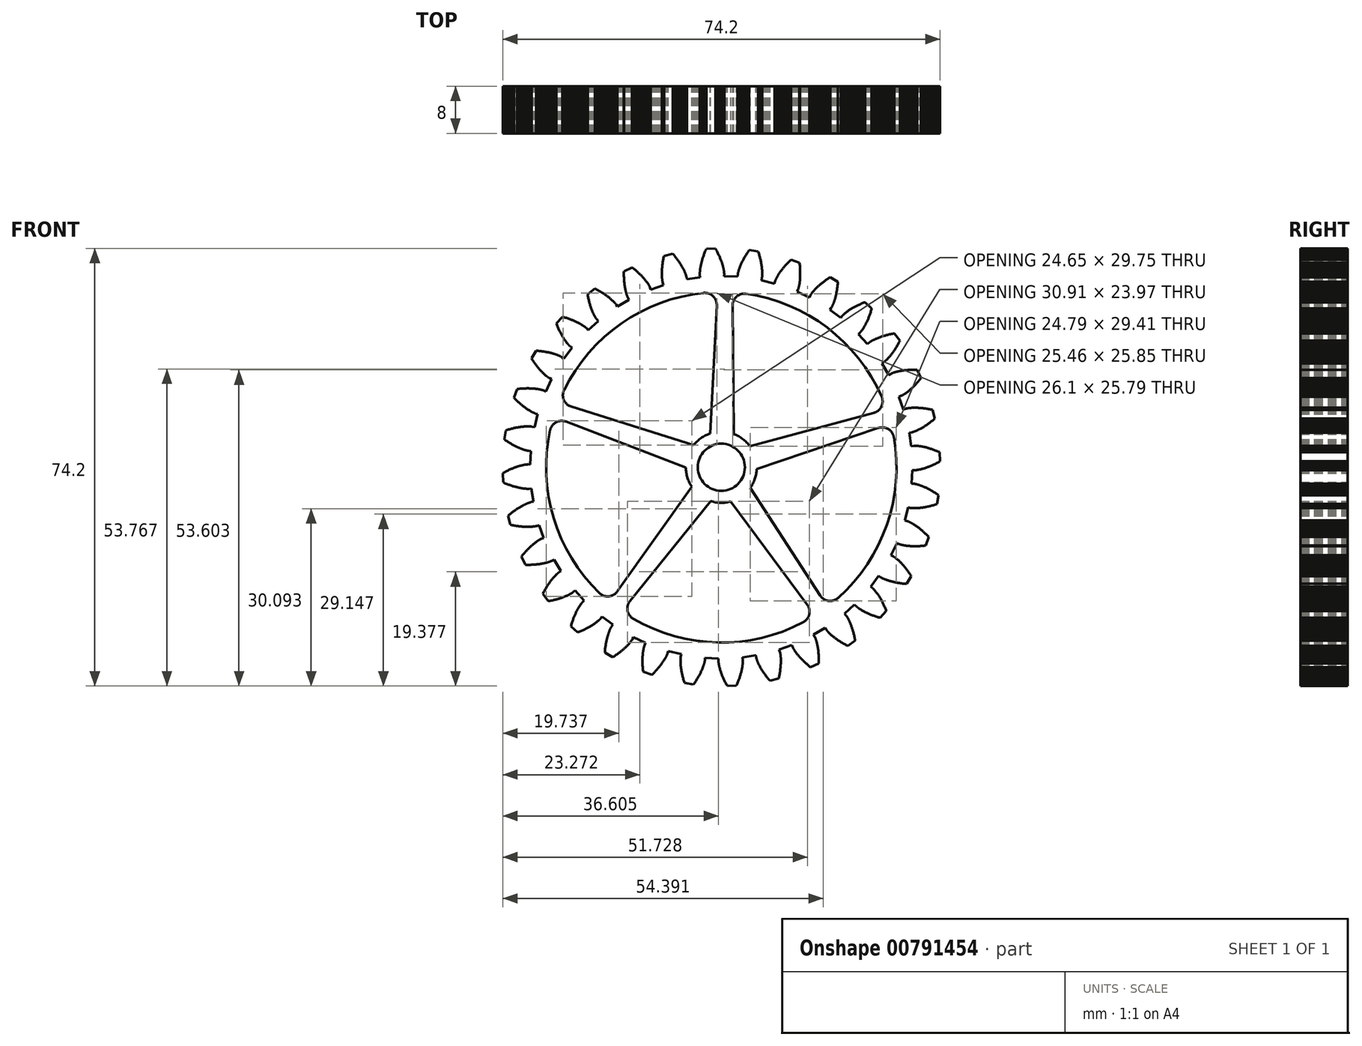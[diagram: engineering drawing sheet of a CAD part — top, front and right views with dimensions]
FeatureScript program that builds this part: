
annotation { "Feature Type Name" : "Feature", "Feature Type Description" : "" }
export const myFeature = defineFeature(function(context is Context, id is Id, definition is map)
    precondition{}
    {
        {
            var Q0;
            Q0=qCreatedBy(makeId("Front.planeOp"),FACE);
            var sketch = newSketch(context, id + "F0", { "sketchPlane" : qUnion([Q0])});
            skLineSegment(sketch, "E0", {"start": v(-0.78, 27.44) * mm, "end": v(-1.9, 5.7) * mm});
            skLineSegment(sketch, "E1", {"start": v(1.9, 27.38) * mm, "end": v(2.14, 5.63) * mm});
            skLineSegment(sketch, "E2", {"start": v(-26.33, 7.74) * mm, "end": v(-6.02, -0.05) * mm});
            skLineSegment(sketch, "E3", {"start": v(-25.45, 10.27) * mm, "end": v(-4.69, 3.77) * mm});
            skLineSegment(sketch, "E4", {"start": v(-15.5, -22.65) * mm, "end": v(-1.81, -5.74) * mm});
            skLineSegment(sketch, "E5", {"start": v(-17.63, -21.04) * mm, "end": v(-5.04, -3.3) * mm});
            skLineSegment(sketch, "E6", {"start": v(16.76, -21.74) * mm, "end": v(4.9, -3.5) * mm});
            skLineSegment(sketch, "E7", {"start": v(14.56, -23.27) * mm, "end": v(1.58, -5.8) * mm});
            skLineSegment(sketch, "E8", {"start": v(25.85, 9.22) * mm, "end": v(4.84, 3.58) * mm});
            skLineSegment(sketch, "E9", {"start": v(26.63, 6.66) * mm, "end": v(6.01, -0.3) * mm});
            skArc(sketch, "E10", {"start": v(19.81, -22.15) * mm, "mid": v(28.07, -9.76) * mm, "end": v(29.28, 5.08) * mm});
            skArc(sketch, "E11", {"start": v(-14.94, -25.69) * mm, "mid": v(-0.6, -29.7) * mm, "end": v(13.88, -26.28) * mm});
            skArc(sketch, "E12", {"start": v(-29.05, 6.27) * mm, "mid": v(-28.44, -8.6) * mm, "end": v(-20.7, -21.32) * mm});
            skArc(sketch, "E13", {"start": v(-3.01, 29.56) * mm, "mid": v(-16.97, 24.4) * mm, "end": v(-26.67, 13.1) * mm});
            skArc(sketch, "E14", {"start": v(27.18, 12) * mm, "mid": v(17.95, 23.68) * mm, "end": v(4.22, 29.41) * mm});
            skArc(sketch, "E15", {"start": v(-26.33, 7.74) * mm, "mid": v(-28.03, 7.63) * mm, "end": v(-29.05, 6.27) * mm});
            skArc(sketch, "E16", {"start": v(-26.67, 13.1) * mm, "mid": v(-26.71, 11.4) * mm, "end": v(-25.45, 10.27) * mm});
            skArc(sketch, "E17", {"start": v(-0.78, 27.44) * mm, "mid": v(-1.4, 29.01) * mm, "end": v(-3.01, 29.56) * mm});
            skArc(sketch, "E18", {"start": v(4.22, 29.41) * mm, "mid": v(2.6, 28.93) * mm, "end": v(1.9, 27.38) * mm});
            skArc(sketch, "E19", {"start": v(25.85, 9.22) * mm, "mid": v(27.16, 10.3) * mm, "end": v(27.18, 12) * mm});
            skArc(sketch, "E20", {"start": v(29.28, 5.08) * mm, "mid": v(28.32, 6.48) * mm, "end": v(26.63, 6.66) * mm});
            skArc(sketch, "E21", {"start": v(16.76, -21.74) * mm, "mid": v(18.2, -22.65) * mm, "end": v(19.81, -22.15) * mm});
            skArc(sketch, "E22", {"start": v(13.88, -26.28) * mm, "mid": v(14.9, -24.93) * mm, "end": v(14.56, -23.27) * mm});
            skArc(sketch, "E23", {"start": v(-15.5, -22.65) * mm, "mid": v(-15.92, -24.3) * mm, "end": v(-14.94, -25.69) * mm});
            skArc(sketch, "E24", {"start": v(-20.7, -21.32) * mm, "mid": v(-19.1, -21.88) * mm, "end": v(-17.63, -21.04) * mm});
            skLineSegment(sketch, "E25", {"start": v(-32.42, 0.48) * mm, "end": v(-32.83, 0.49) * mm});
            skLineSegment(sketch, "E26", {"start": v(-32.83, 0.49) * mm, "end": v(-32.84, 0.49) * mm});
            skLineSegment(sketch, "E27", {"start": v(-32.84, 0.49) * mm, "end": v(-32.85, 0.49) * mm});
            skLineSegment(sketch, "E28", {"start": v(-32.85, 0.49) * mm, "end": v(-32.86, 0.49) * mm});
            skLineSegment(sketch, "E29", {"start": v(-32.86, 0.49) * mm, "end": v(-32.88, 0.49) * mm});
            skLineSegment(sketch, "E30", {"start": v(-32.88, 0.49) * mm, "end": v(-32.9, 0.49) * mm});
            skLineSegment(sketch, "E31", {"start": v(-32.9, 0.49) * mm, "end": v(-32.94, 0.48) * mm});
            skLineSegment(sketch, "E32", {"start": v(-32.94, 0.48) * mm, "end": v(-32.97, 0.48) * mm});
            skLineSegment(sketch, "E33", {"start": v(-32.97, 0.48) * mm, "end": v(-33, 0.48) * mm});
            skLineSegment(sketch, "E34", {"start": v(-33, 0.48) * mm, "end": v(-33.04, 0.48) * mm});
            skLineSegment(sketch, "E35", {"start": v(-33.04, 0.48) * mm, "end": v(-33.09, 0.47) * mm});
            skLineSegment(sketch, "E36", {"start": v(-33.09, 0.47) * mm, "end": v(-33.13, 0.47) * mm});
            skLineSegment(sketch, "E37", {"start": v(-33.13, 0.47) * mm, "end": v(-33.18, 0.46) * mm});
            skLineSegment(sketch, "E38", {"start": v(-33.18, 0.46) * mm, "end": v(-33.24, 0.45) * mm});
            skLineSegment(sketch, "E39", {"start": v(-33.24, 0.45) * mm, "end": v(-33.3, 0.44) * mm});
            skLineSegment(sketch, "E40", {"start": v(-33.3, 0.44) * mm, "end": v(-33.36, 0.43) * mm});
            skLineSegment(sketch, "E41", {"start": v(-33.36, 0.43) * mm, "end": v(-33.42, 0.42) * mm});
            skLineSegment(sketch, "E42", {"start": v(-33.42, 0.42) * mm, "end": v(-33.5, 0.4) * mm});
            skLineSegment(sketch, "E43", {"start": v(-33.5, 0.4) * mm, "end": v(-33.57, 0.4) * mm});
            skLineSegment(sketch, "E44", {"start": v(-33.57, 0.4) * mm, "end": v(-33.64, 0.38) * mm});
            skLineSegment(sketch, "E45", {"start": v(-33.64, 0.38) * mm, "end": v(-33.72, 0.36) * mm});
            skLineSegment(sketch, "E46", {"start": v(-33.72, 0.36) * mm, "end": v(-33.8, 0.34) * mm});
            skLineSegment(sketch, "E47", {"start": v(-33.8, 0.34) * mm, "end": v(-33.9, 0.32) * mm});
            skLineSegment(sketch, "E48", {"start": v(-33.9, 0.32) * mm, "end": v(-33.99, 0.3) * mm});
            skLineSegment(sketch, "E49", {"start": v(-33.99, 0.3) * mm, "end": v(-34.08, 0.27) * mm});
            skLineSegment(sketch, "E50", {"start": v(-34.08, 0.27) * mm, "end": v(-34.18, 0.24) * mm});
            skLineSegment(sketch, "E51", {"start": v(-34.18, 0.24) * mm, "end": v(-34.28, 0.22) * mm});
            skLineSegment(sketch, "E52", {"start": v(-34.28, 0.22) * mm, "end": v(-34.39, 0.18) * mm});
            skLineSegment(sketch, "E53", {"start": v(-34.39, 0.18) * mm, "end": v(-34.5, 0.15) * mm});
            skLineSegment(sketch, "E54", {"start": v(-34.5, 0.15) * mm, "end": v(-34.6, 0.11) * mm});
            skLineSegment(sketch, "E55", {"start": v(-34.6, 0.11) * mm, "end": v(-34.72, 0.07) * mm});
            skLineSegment(sketch, "E56", {"start": v(-34.72, 0.07) * mm, "end": v(-34.84, 0.03) * mm});
            skLineSegment(sketch, "E57", {"start": v(-34.84, 0.03) * mm, "end": v(-34.96, -0.01) * mm});
            skLineSegment(sketch, "E58", {"start": v(-34.96, -0.01) * mm, "end": v(-35.09, -0.06) * mm});
            skLineSegment(sketch, "E59", {"start": v(-35.09, -0.06) * mm, "end": v(-35.21, -0.1) * mm});
            skLineSegment(sketch, "E60", {"start": v(-35.21, -0.1) * mm, "end": v(-35.35, -0.16) * mm});
            skLineSegment(sketch, "E61", {"start": v(-35.35, -0.16) * mm, "end": v(-35.48, -0.21) * mm});
            skLineSegment(sketch, "E62", {"start": v(-35.48, -0.21) * mm, "end": v(-35.62, -0.27) * mm});
            skLineSegment(sketch, "E63", {"start": v(-35.62, -0.27) * mm, "end": v(-35.76, -0.33) * mm});
            skLineSegment(sketch, "E64", {"start": v(-35.76, -0.33) * mm, "end": v(-35.9, -0.4) * mm});
            skLineSegment(sketch, "E65", {"start": v(-35.9, -0.4) * mm, "end": v(-36.05, -0.46) * mm});
            skLineSegment(sketch, "E66", {"start": v(-36.05, -0.46) * mm, "end": v(-36.2, -0.53) * mm});
            skLineSegment(sketch, "E67", {"start": v(-36.2, -0.53) * mm, "end": v(-36.35, -0.6) * mm});
            skLineSegment(sketch, "E68", {"start": v(-36.35, -0.6) * mm, "end": v(-36.5, -0.69) * mm});
            skLineSegment(sketch, "E69", {"start": v(-36.5, -0.69) * mm, "end": v(-36.66, -0.77) * mm});
            skLineSegment(sketch, "E70", {"start": v(-36.66, -0.77) * mm, "end": v(-36.81, -0.85) * mm});
            skLineSegment(sketch, "E71", {"start": v(-36.81, -0.85) * mm, "end": v(-36.98, -0.94) * mm});
            skLineSegment(sketch, "E72", {"start": v(-36.98, -0.94) * mm, "end": v(-37.1, -1.03) * mm});
            skLineSegment(sketch, "E73", {"start": v(-37.1, -1.03) * mm, "end": v(-37.03, -2.54) * mm});
            skLineSegment(sketch, "E74", {"start": v(-37.03, -2.54) * mm, "end": v(-36.9, -2.62) * mm});
            skLineSegment(sketch, "E75", {"start": v(-36.9, -2.62) * mm, "end": v(-36.73, -2.7) * mm});
            skLineSegment(sketch, "E76", {"start": v(-36.73, -2.7) * mm, "end": v(-36.56, -2.76) * mm});
            skLineSegment(sketch, "E77", {"start": v(-36.56, -2.76) * mm, "end": v(-36.4, -2.82) * mm});
            skLineSegment(sketch, "E78", {"start": v(-36.4, -2.82) * mm, "end": v(-36.24, -2.89) * mm});
            skLineSegment(sketch, "E79", {"start": v(-36.24, -2.89) * mm, "end": v(-36.08, -2.95) * mm});
            skLineSegment(sketch, "E80", {"start": v(-36.08, -2.95) * mm, "end": v(-35.92, -3) * mm});
            skLineSegment(sketch, "E81", {"start": v(-35.92, -3) * mm, "end": v(-35.77, -3.05) * mm});
            skLineSegment(sketch, "E82", {"start": v(-35.77, -3.05) * mm, "end": v(-35.62, -3.1) * mm});
            skLineSegment(sketch, "E83", {"start": v(-35.62, -3.1) * mm, "end": v(-35.48, -3.15) * mm});
            skLineSegment(sketch, "E84", {"start": v(-35.48, -3.15) * mm, "end": v(-35.34, -3.2) * mm});
            skLineSegment(sketch, "E85", {"start": v(-35.34, -3.2) * mm, "end": v(-35.2, -3.24) * mm});
            skLineSegment(sketch, "E86", {"start": v(-35.2, -3.24) * mm, "end": v(-35.06, -3.28) * mm});
            skLineSegment(sketch, "E87", {"start": v(-35.06, -3.28) * mm, "end": v(-34.93, -3.32) * mm});
            skLineSegment(sketch, "E88", {"start": v(-34.93, -3.32) * mm, "end": v(-34.8, -3.35) * mm});
            skLineSegment(sketch, "E89", {"start": v(-34.8, -3.35) * mm, "end": v(-34.68, -3.38) * mm});
            skLineSegment(sketch, "E90", {"start": v(-34.68, -3.38) * mm, "end": v(-34.55, -3.41) * mm});
            skLineSegment(sketch, "E91", {"start": v(-34.55, -3.41) * mm, "end": v(-34.44, -3.44) * mm});
            skLineSegment(sketch, "E92", {"start": v(-34.44, -3.44) * mm, "end": v(-34.32, -3.46) * mm});
            skLineSegment(sketch, "E93", {"start": v(-34.32, -3.46) * mm, "end": v(-34.2, -3.49) * mm});
            skLineSegment(sketch, "E94", {"start": v(-34.2, -3.49) * mm, "end": v(-34.1, -3.5) * mm});
            skLineSegment(sketch, "E95", {"start": v(-34.1, -3.5) * mm, "end": v(-34, -3.53) * mm});
            skLineSegment(sketch, "E96", {"start": v(-34, -3.53) * mm, "end": v(-33.9, -3.55) * mm});
            skLineSegment(sketch, "E97", {"start": v(-33.9, -3.55) * mm, "end": v(-33.8, -3.56) * mm});
            skLineSegment(sketch, "E98", {"start": v(-33.8, -3.56) * mm, "end": v(-33.7, -3.58) * mm});
            skLineSegment(sketch, "E99", {"start": v(-33.7, -3.58) * mm, "end": v(-33.62, -3.59) * mm});
            skLineSegment(sketch, "E100", {"start": v(-33.62, -3.59) * mm, "end": v(-33.53, -3.6) * mm});
            skLineSegment(sketch, "E101", {"start": v(-33.53, -3.6) * mm, "end": v(-33.45, -3.6) * mm});
            skLineSegment(sketch, "E102", {"start": v(-33.45, -3.6) * mm, "end": v(-33.37, -3.62) * mm});
            skLineSegment(sketch, "E103", {"start": v(-33.37, -3.62) * mm, "end": v(-33.3, -3.63) * mm});
            skLineSegment(sketch, "E104", {"start": v(-33.3, -3.63) * mm, "end": v(-33.23, -3.63) * mm});
            skLineSegment(sketch, "E105", {"start": v(-33.23, -3.63) * mm, "end": v(-33.16, -3.64) * mm});
            skLineSegment(sketch, "E106", {"start": v(-33.16, -3.64) * mm, "end": v(-33.1, -3.64) * mm});
            skLineSegment(sketch, "E107", {"start": v(-33.1, -3.64) * mm, "end": v(-33.04, -3.64) * mm});
            skLineSegment(sketch, "E108", {"start": v(-33.04, -3.64) * mm, "end": v(-32.98, -3.65) * mm});
            skLineSegment(sketch, "E109", {"start": v(-32.98, -3.65) * mm, "end": v(-32.93, -3.65) * mm});
            skLineSegment(sketch, "E110", {"start": v(-32.93, -3.65) * mm, "end": v(-32.89, -3.65) * mm});
            skLineSegment(sketch, "E111", {"start": v(-32.89, -3.65) * mm, "end": v(-32.84, -3.65) * mm});
            skLineSegment(sketch, "E112", {"start": v(-32.84, -3.65) * mm, "end": v(-32.8, -3.65) * mm});
            skLineSegment(sketch, "E113", {"start": v(-32.8, -3.65) * mm, "end": v(-32.77, -3.65) * mm});
            skLineSegment(sketch, "E114", {"start": v(-32.77, -3.65) * mm, "end": v(-32.74, -3.65) * mm});
            skLineSegment(sketch, "E115", {"start": v(-32.74, -3.65) * mm, "end": v(-32.7, -3.65) * mm});
            skLineSegment(sketch, "E116", {"start": v(-32.7, -3.65) * mm, "end": v(-32.69, -3.65) * mm});
            skLineSegment(sketch, "E117", {"start": v(-32.69, -3.65) * mm, "end": v(-32.67, -3.64) * mm});
            skLineSegment(sketch, "E118", {"start": v(-32.67, -3.64) * mm, "end": v(-32.65, -3.64) * mm});
            skLineSegment(sketch, "E119", {"start": v(-32.65, -3.64) * mm, "end": v(-32.64, -3.64) * mm});
            skLineSegment(sketch, "E120", {"start": v(-32.64, -3.64) * mm, "end": v(-32.63, -3.64) * mm});
            skLineSegment(sketch, "E121", {"start": v(-32.63, -3.64) * mm, "end": v(-32.22, -3.6) * mm});
            skLineSegment(sketch, "E122", {"start": v(-32.22, -3.6) * mm, "end": v(-31.9, -5.85) * mm});
            skLineSegment(sketch, "E123", {"start": v(-31.9, -5.85) * mm, "end": v(-32.3, -5.92) * mm});
            skLineSegment(sketch, "E124", {"start": v(-32.3, -5.92) * mm, "end": v(-32.3, -5.93) * mm});
            skLineSegment(sketch, "E125", {"start": v(-32.3, -5.93) * mm, "end": v(-32.31, -5.93) * mm});
            skLineSegment(sketch, "E126", {"start": v(-32.31, -5.93) * mm, "end": v(-32.33, -5.93) * mm});
            skLineSegment(sketch, "E127", {"start": v(-32.33, -5.93) * mm, "end": v(-32.35, -5.94) * mm});
            skLineSegment(sketch, "E128", {"start": v(-32.35, -5.94) * mm, "end": v(-32.37, -5.94) * mm});
            skLineSegment(sketch, "E129", {"start": v(-32.37, -5.94) * mm, "end": v(-32.4, -5.95) * mm});
            skLineSegment(sketch, "E130", {"start": v(-32.4, -5.95) * mm, "end": v(-32.43, -5.96) * mm});
            skLineSegment(sketch, "E131", {"start": v(-32.43, -5.96) * mm, "end": v(-32.46, -5.97) * mm});
            skLineSegment(sketch, "E132", {"start": v(-32.46, -5.97) * mm, "end": v(-32.5, -5.98) * mm});
            skLineSegment(sketch, "E133", {"start": v(-32.5, -5.98) * mm, "end": v(-32.54, -6) * mm});
            skLineSegment(sketch, "E134", {"start": v(-32.54, -6) * mm, "end": v(-32.59, -6) * mm});
            skLineSegment(sketch, "E135", {"start": v(-32.59, -6) * mm, "end": v(-32.63, -6.02) * mm});
            skLineSegment(sketch, "E136", {"start": v(-32.63, -6.02) * mm, "end": v(-32.69, -6.04) * mm});
            skLineSegment(sketch, "E137", {"start": v(-32.69, -6.04) * mm, "end": v(-32.74, -6.06) * mm});
            skLineSegment(sketch, "E138", {"start": v(-32.74, -6.06) * mm, "end": v(-32.8, -6.08) * mm});
            skLineSegment(sketch, "E139", {"start": v(-32.8, -6.08) * mm, "end": v(-32.86, -6.1) * mm});
            skLineSegment(sketch, "E140", {"start": v(-32.86, -6.1) * mm, "end": v(-32.93, -6.13) * mm});
            skLineSegment(sketch, "E141", {"start": v(-32.93, -6.13) * mm, "end": v(-33, -6.16) * mm});
            skLineSegment(sketch, "E142", {"start": v(-33, -6.16) * mm, "end": v(-33.07, -6.2) * mm});
            skLineSegment(sketch, "E143", {"start": v(-33.07, -6.2) * mm, "end": v(-33.15, -6.23) * mm});
            skLineSegment(sketch, "E144", {"start": v(-33.15, -6.23) * mm, "end": v(-33.22, -6.26) * mm});
            skLineSegment(sketch, "E145", {"start": v(-33.22, -6.26) * mm, "end": v(-33.3, -6.3) * mm});
            skLineSegment(sketch, "E146", {"start": v(-33.3, -6.3) * mm, "end": v(-33.4, -6.34) * mm});
            skLineSegment(sketch, "E147", {"start": v(-33.4, -6.34) * mm, "end": v(-33.48, -6.38) * mm});
            skLineSegment(sketch, "E148", {"start": v(-33.48, -6.38) * mm, "end": v(-33.57, -6.43) * mm});
            skLineSegment(sketch, "E149", {"start": v(-33.57, -6.43) * mm, "end": v(-33.66, -6.48) * mm});
            skLineSegment(sketch, "E150", {"start": v(-33.66, -6.48) * mm, "end": v(-33.76, -6.53) * mm});
            skLineSegment(sketch, "E151", {"start": v(-33.76, -6.53) * mm, "end": v(-33.86, -6.58) * mm});
            skLineSegment(sketch, "E152", {"start": v(-33.86, -6.58) * mm, "end": v(-33.96, -6.64) * mm});
            skLineSegment(sketch, "E153", {"start": v(-33.96, -6.64) * mm, "end": v(-34.07, -6.7) * mm});
            skLineSegment(sketch, "E154", {"start": v(-34.07, -6.7) * mm, "end": v(-34.18, -6.76) * mm});
            skLineSegment(sketch, "E155", {"start": v(-34.18, -6.76) * mm, "end": v(-34.29, -6.83) * mm});
            skLineSegment(sketch, "E156", {"start": v(-34.29, -6.83) * mm, "end": v(-34.4, -6.9) * mm});
            skLineSegment(sketch, "E157", {"start": v(-34.4, -6.9) * mm, "end": v(-34.52, -6.97) * mm});
            skLineSegment(sketch, "E158", {"start": v(-34.52, -6.97) * mm, "end": v(-34.64, -7.05) * mm});
            skLineSegment(sketch, "E159", {"start": v(-34.64, -7.05) * mm, "end": v(-34.76, -7.13) * mm});
            skLineSegment(sketch, "E160", {"start": v(-34.76, -7.13) * mm, "end": v(-34.88, -7.21) * mm});
            skLineSegment(sketch, "E161", {"start": v(-34.88, -7.21) * mm, "end": v(-35, -7.3) * mm});
            skLineSegment(sketch, "E162", {"start": v(-35, -7.3) * mm, "end": v(-35.13, -7.4) * mm});
            skLineSegment(sketch, "E163", {"start": v(-35.13, -7.4) * mm, "end": v(-35.26, -7.49) * mm});
            skLineSegment(sketch, "E164", {"start": v(-35.26, -7.49) * mm, "end": v(-35.4, -7.59) * mm});
            skLineSegment(sketch, "E165", {"start": v(-35.4, -7.59) * mm, "end": v(-35.53, -7.69) * mm});
            skLineSegment(sketch, "E166", {"start": v(-35.53, -7.69) * mm, "end": v(-35.66, -7.8) * mm});
            skLineSegment(sketch, "E167", {"start": v(-35.66, -7.8) * mm, "end": v(-35.8, -7.9) * mm});
            skLineSegment(sketch, "E168", {"start": v(-35.8, -7.9) * mm, "end": v(-35.94, -8.02) * mm});
            skLineSegment(sketch, "E169", {"start": v(-35.94, -8.02) * mm, "end": v(-36.08, -8.14) * mm});
            skLineSegment(sketch, "E170", {"start": v(-36.08, -8.14) * mm, "end": v(-36.19, -8.25) * mm});
            skLineSegment(sketch, "E171", {"start": v(-36.19, -8.25) * mm, "end": v(-35.82, -9.72) * mm});
            skLineSegment(sketch, "E172", {"start": v(-35.82, -9.72) * mm, "end": v(-35.68, -9.77) * mm});
            skLineSegment(sketch, "E173", {"start": v(-35.68, -9.77) * mm, "end": v(-35.5, -9.8) * mm});
            skLineSegment(sketch, "E174", {"start": v(-35.5, -9.8) * mm, "end": v(-35.32, -9.84) * mm});
            skLineSegment(sketch, "E175", {"start": v(-35.32, -9.84) * mm, "end": v(-35.15, -9.87) * mm});
            skLineSegment(sketch, "E176", {"start": v(-35.15, -9.87) * mm, "end": v(-34.98, -9.9) * mm});
            skLineSegment(sketch, "E177", {"start": v(-34.98, -9.9) * mm, "end": v(-34.8, -9.93) * mm});
            skLineSegment(sketch, "E178", {"start": v(-34.8, -9.93) * mm, "end": v(-34.65, -9.95) * mm});
            skLineSegment(sketch, "E179", {"start": v(-34.65, -9.95) * mm, "end": v(-34.49, -9.98) * mm});
            skLineSegment(sketch, "E180", {"start": v(-34.49, -9.98) * mm, "end": v(-34.33, -10) * mm});
            skLineSegment(sketch, "E181", {"start": v(-34.33, -10) * mm, "end": v(-34.18, -10.01) * mm});
            skLineSegment(sketch, "E182", {"start": v(-34.18, -10.01) * mm, "end": v(-34.03, -10.03) * mm});
            skLineSegment(sketch, "E183", {"start": v(-34.03, -10.03) * mm, "end": v(-33.89, -10.04) * mm});
            skLineSegment(sketch, "E184", {"start": v(-33.89, -10.04) * mm, "end": v(-33.75, -10.06) * mm});
            skLineSegment(sketch, "E185", {"start": v(-33.75, -10.06) * mm, "end": v(-33.61, -10.07) * mm});
            skLineSegment(sketch, "E186", {"start": v(-33.61, -10.07) * mm, "end": v(-33.48, -10.07) * mm});
            skLineSegment(sketch, "E187", {"start": v(-33.48, -10.07) * mm, "end": v(-33.35, -10.08) * mm});
            skLineSegment(sketch, "E188", {"start": v(-33.35, -10.08) * mm, "end": v(-33.22, -10.09) * mm});
            skLineSegment(sketch, "E189", {"start": v(-33.22, -10.09) * mm, "end": v(-33.1, -10.1) * mm});
            skLineSegment(sketch, "E190", {"start": v(-33.1, -10.1) * mm, "end": v(-32.99, -10.1) * mm});
            skLineSegment(sketch, "E191", {"start": v(-32.99, -10.1) * mm, "end": v(-32.87, -10.1) * mm});
            skLineSegment(sketch, "E192", {"start": v(-32.87, -10.1) * mm, "end": v(-32.76, -10.1) * mm});
            skLineSegment(sketch, "E193", {"start": v(-32.76, -10.1) * mm, "end": v(-32.66, -10.1) * mm});
            skLineSegment(sketch, "E194", {"start": v(-32.66, -10.1) * mm, "end": v(-32.55, -10.1) * mm});
            skLineSegment(sketch, "E195", {"start": v(-32.55, -10.1) * mm, "end": v(-32.46, -10.09) * mm});
            skLineSegment(sketch, "E196", {"start": v(-32.46, -10.09) * mm, "end": v(-32.36, -10.08) * mm});
            skLineSegment(sketch, "E197", {"start": v(-32.36, -10.08) * mm, "end": v(-32.27, -10.08) * mm});
            skLineSegment(sketch, "E198", {"start": v(-32.27, -10.08) * mm, "end": v(-32.19, -10.07) * mm});
            skLineSegment(sketch, "E199", {"start": v(-32.19, -10.07) * mm, "end": v(-32.1, -10.07) * mm});
            skLineSegment(sketch, "E200", {"start": v(-32.1, -10.07) * mm, "end": v(-32.03, -10.06) * mm});
            skLineSegment(sketch, "E201", {"start": v(-32.03, -10.06) * mm, "end": v(-31.95, -10.05) * mm});
            skLineSegment(sketch, "E202", {"start": v(-31.95, -10.05) * mm, "end": v(-31.88, -10.04) * mm});
            skLineSegment(sketch, "E203", {"start": v(-31.88, -10.04) * mm, "end": v(-31.82, -10.04) * mm});
            skLineSegment(sketch, "E204", {"start": v(-31.82, -10.04) * mm, "end": v(-31.75, -10.03) * mm});
            skLineSegment(sketch, "E205", {"start": v(-31.75, -10.03) * mm, "end": v(-31.7, -10.02) * mm});
            skLineSegment(sketch, "E206", {"start": v(-31.7, -10.02) * mm, "end": v(-31.64, -10.01) * mm});
            skLineSegment(sketch, "E207", {"start": v(-31.64, -10.01) * mm, "end": v(-31.59, -10) * mm});
            skLineSegment(sketch, "E208", {"start": v(-31.59, -10) * mm, "end": v(-31.54, -10) * mm});
            skLineSegment(sketch, "E209", {"start": v(-31.54, -10) * mm, "end": v(-31.5, -9.99) * mm});
            skLineSegment(sketch, "E210", {"start": v(-31.5, -9.99) * mm, "end": v(-31.46, -9.98) * mm});
            skLineSegment(sketch, "E211", {"start": v(-31.46, -9.98) * mm, "end": v(-31.43, -9.97) * mm});
            skLineSegment(sketch, "E212", {"start": v(-31.43, -9.97) * mm, "end": v(-31.4, -9.96) * mm});
            skLineSegment(sketch, "E213", {"start": v(-31.4, -9.96) * mm, "end": v(-31.37, -9.96) * mm});
            skLineSegment(sketch, "E214", {"start": v(-31.37, -9.96) * mm, "end": v(-31.35, -9.95) * mm});
            skLineSegment(sketch, "E215", {"start": v(-31.35, -9.95) * mm, "end": v(-31.33, -9.95) * mm});
            skLineSegment(sketch, "E216", {"start": v(-31.33, -9.95) * mm, "end": v(-31.31, -9.94) * mm});
            skLineSegment(sketch, "E217", {"start": v(-31.31, -9.94) * mm, "end": v(-31.3, -9.94) * mm});
            skLineSegment(sketch, "E218", {"start": v(-31.3, -9.94) * mm, "end": v(-31.3, -9.94) * mm});
            skLineSegment(sketch, "E219", {"start": v(-31.3, -9.94) * mm, "end": v(-30.9, -9.81) * mm});
            skLineSegment(sketch, "E220", {"start": v(-30.9, -9.81) * mm, "end": v(-30.14, -11.96) * mm});
            skLineSegment(sketch, "E221", {"start": v(-30.14, -11.96) * mm, "end": v(-30.52, -12.11) * mm});
            skLineSegment(sketch, "E222", {"start": v(-30.52, -12.11) * mm, "end": v(-30.52, -12.11) * mm});
            skLineSegment(sketch, "E223", {"start": v(-30.52, -12.11) * mm, "end": v(-30.54, -12.12) * mm});
            skLineSegment(sketch, "E224", {"start": v(-30.54, -12.12) * mm, "end": v(-30.55, -12.13) * mm});
            skLineSegment(sketch, "E225", {"start": v(-30.55, -12.13) * mm, "end": v(-30.57, -12.13) * mm});
            skLineSegment(sketch, "E226", {"start": v(-30.57, -12.13) * mm, "end": v(-30.59, -12.14) * mm});
            skLineSegment(sketch, "E227", {"start": v(-30.59, -12.14) * mm, "end": v(-30.61, -12.16) * mm});
            skLineSegment(sketch, "E228", {"start": v(-30.61, -12.16) * mm, "end": v(-30.64, -12.17) * mm});
            skLineSegment(sketch, "E229", {"start": v(-30.64, -12.17) * mm, "end": v(-30.67, -12.19) * mm});
            skLineSegment(sketch, "E230", {"start": v(-30.67, -12.19) * mm, "end": v(-30.7, -12.2) * mm});
            skLineSegment(sketch, "E231", {"start": v(-30.7, -12.2) * mm, "end": v(-30.75, -12.23) * mm});
            skLineSegment(sketch, "E232", {"start": v(-30.75, -12.23) * mm, "end": v(-30.79, -12.25) * mm});
            skLineSegment(sketch, "E233", {"start": v(-30.79, -12.25) * mm, "end": v(-30.83, -12.27) * mm});
            skLineSegment(sketch, "E234", {"start": v(-30.83, -12.27) * mm, "end": v(-30.88, -12.3) * mm});
            skLineSegment(sketch, "E235", {"start": v(-30.88, -12.3) * mm, "end": v(-30.93, -12.33) * mm});
            skLineSegment(sketch, "E236", {"start": v(-30.93, -12.33) * mm, "end": v(-30.98, -12.37) * mm});
            skLineSegment(sketch, "E237", {"start": v(-30.98, -12.37) * mm, "end": v(-31.04, -12.4) * mm});
            skLineSegment(sketch, "E238", {"start": v(-31.04, -12.4) * mm, "end": v(-31.1, -12.44) * mm});
            skLineSegment(sketch, "E239", {"start": v(-31.1, -12.44) * mm, "end": v(-31.16, -12.48) * mm});
            skLineSegment(sketch, "E240", {"start": v(-31.16, -12.48) * mm, "end": v(-31.23, -12.53) * mm});
            skLineSegment(sketch, "E241", {"start": v(-31.23, -12.53) * mm, "end": v(-31.3, -12.57) * mm});
            skLineSegment(sketch, "E242", {"start": v(-31.3, -12.57) * mm, "end": v(-31.36, -12.62) * mm});
            skLineSegment(sketch, "E243", {"start": v(-31.36, -12.62) * mm, "end": v(-31.44, -12.68) * mm});
            skLineSegment(sketch, "E244", {"start": v(-31.44, -12.68) * mm, "end": v(-31.51, -12.73) * mm});
            skLineSegment(sketch, "E245", {"start": v(-31.51, -12.73) * mm, "end": v(-31.6, -12.8) * mm});
            skLineSegment(sketch, "E246", {"start": v(-31.6, -12.8) * mm, "end": v(-31.67, -12.85) * mm});
            skLineSegment(sketch, "E247", {"start": v(-31.67, -12.85) * mm, "end": v(-31.75, -12.92) * mm});
            skLineSegment(sketch, "E248", {"start": v(-31.75, -12.92) * mm, "end": v(-31.84, -12.99) * mm});
            skLineSegment(sketch, "E249", {"start": v(-31.84, -12.99) * mm, "end": v(-31.93, -13.06) * mm});
            skLineSegment(sketch, "E250", {"start": v(-31.93, -13.06) * mm, "end": v(-32.02, -13.14) * mm});
            skLineSegment(sketch, "E251", {"start": v(-32.02, -13.14) * mm, "end": v(-32.1, -13.22) * mm});
            skLineSegment(sketch, "E252", {"start": v(-32.1, -13.22) * mm, "end": v(-32.2, -13.3) * mm});
            skLineSegment(sketch, "E253", {"start": v(-32.2, -13.3) * mm, "end": v(-32.3, -13.39) * mm});
            skLineSegment(sketch, "E254", {"start": v(-32.3, -13.39) * mm, "end": v(-32.4, -13.48) * mm});
            skLineSegment(sketch, "E255", {"start": v(-32.4, -13.48) * mm, "end": v(-32.5, -13.57) * mm});
            skLineSegment(sketch, "E256", {"start": v(-32.5, -13.57) * mm, "end": v(-32.6, -13.67) * mm});
            skLineSegment(sketch, "E257", {"start": v(-32.6, -13.67) * mm, "end": v(-32.7, -13.77) * mm});
            skLineSegment(sketch, "E258", {"start": v(-32.7, -13.77) * mm, "end": v(-32.8, -13.88) * mm});
            skLineSegment(sketch, "E259", {"start": v(-32.8, -13.88) * mm, "end": v(-32.9, -14) * mm});
            skLineSegment(sketch, "E260", {"start": v(-32.9, -14) * mm, "end": v(-33.02, -14.1) * mm});
            skLineSegment(sketch, "E261", {"start": v(-33.02, -14.1) * mm, "end": v(-33.12, -14.22) * mm});
            skLineSegment(sketch, "E262", {"start": v(-33.12, -14.22) * mm, "end": v(-33.23, -14.35) * mm});
            skLineSegment(sketch, "E263", {"start": v(-33.23, -14.35) * mm, "end": v(-33.35, -14.47) * mm});
            skLineSegment(sketch, "E264", {"start": v(-33.35, -14.47) * mm, "end": v(-33.46, -14.6) * mm});
            skLineSegment(sketch, "E265", {"start": v(-33.46, -14.6) * mm, "end": v(-33.57, -14.74) * mm});
            skLineSegment(sketch, "E266", {"start": v(-33.57, -14.74) * mm, "end": v(-33.69, -14.88) * mm});
            skLineSegment(sketch, "E267", {"start": v(-33.69, -14.88) * mm, "end": v(-33.8, -15.02) * mm});
            skLineSegment(sketch, "E268", {"start": v(-33.8, -15.02) * mm, "end": v(-33.88, -15.15) * mm});
            skLineSegment(sketch, "E269", {"start": v(-33.88, -15.15) * mm, "end": v(-33.24, -16.52) * mm});
            skLineSegment(sketch, "E270", {"start": v(-33.24, -16.52) * mm, "end": v(-33.08, -16.54) * mm});
            skLineSegment(sketch, "E271", {"start": v(-33.08, -16.54) * mm, "end": v(-32.9, -16.54) * mm});
            skLineSegment(sketch, "E272", {"start": v(-32.9, -16.54) * mm, "end": v(-32.72, -16.54) * mm});
            skLineSegment(sketch, "E273", {"start": v(-32.72, -16.54) * mm, "end": v(-32.54, -16.54) * mm});
            skLineSegment(sketch, "E274", {"start": v(-32.54, -16.54) * mm, "end": v(-32.37, -16.53) * mm});
            skLineSegment(sketch, "E275", {"start": v(-32.37, -16.53) * mm, "end": v(-32.2, -16.53) * mm});
            skLineSegment(sketch, "E276", {"start": v(-32.2, -16.53) * mm, "end": v(-32.04, -16.52) * mm});
            skLineSegment(sketch, "E277", {"start": v(-32.04, -16.52) * mm, "end": v(-31.88, -16.51) * mm});
            skLineSegment(sketch, "E278", {"start": v(-31.88, -16.51) * mm, "end": v(-31.72, -16.5) * mm});
            skLineSegment(sketch, "E279", {"start": v(-31.72, -16.5) * mm, "end": v(-31.57, -16.49) * mm});
            skLineSegment(sketch, "E280", {"start": v(-31.57, -16.49) * mm, "end": v(-31.42, -16.48) * mm});
            skLineSegment(sketch, "E281", {"start": v(-31.42, -16.48) * mm, "end": v(-31.28, -16.46) * mm});
            skLineSegment(sketch, "E282", {"start": v(-31.28, -16.46) * mm, "end": v(-31.14, -16.45) * mm});
            skLineSegment(sketch, "E283", {"start": v(-31.14, -16.45) * mm, "end": v(-31, -16.43) * mm});
            skLineSegment(sketch, "E284", {"start": v(-31, -16.43) * mm, "end": v(-30.87, -16.41) * mm});
            skLineSegment(sketch, "E285", {"start": v(-30.87, -16.41) * mm, "end": v(-30.74, -16.4) * mm});
            skLineSegment(sketch, "E286", {"start": v(-30.74, -16.4) * mm, "end": v(-30.62, -16.37) * mm});
            skLineSegment(sketch, "E287", {"start": v(-30.62, -16.37) * mm, "end": v(-30.5, -16.36) * mm});
            skLineSegment(sketch, "E288", {"start": v(-30.5, -16.36) * mm, "end": v(-30.38, -16.33) * mm});
            skLineSegment(sketch, "E289", {"start": v(-30.38, -16.33) * mm, "end": v(-30.27, -16.31) * mm});
            skLineSegment(sketch, "E290", {"start": v(-30.27, -16.31) * mm, "end": v(-30.16, -16.3) * mm});
            skLineSegment(sketch, "E291", {"start": v(-30.16, -16.3) * mm, "end": v(-30.06, -16.27) * mm});
            skLineSegment(sketch, "E292", {"start": v(-30.06, -16.27) * mm, "end": v(-29.96, -16.25) * mm});
            skLineSegment(sketch, "E293", {"start": v(-29.96, -16.25) * mm, "end": v(-29.86, -16.23) * mm});
            skLineSegment(sketch, "E294", {"start": v(-29.86, -16.23) * mm, "end": v(-29.77, -16.2) * mm});
            skLineSegment(sketch, "E295", {"start": v(-29.77, -16.2) * mm, "end": v(-29.69, -16.18) * mm});
            skLineSegment(sketch, "E296", {"start": v(-29.69, -16.18) * mm, "end": v(-29.6, -16.16) * mm});
            skLineSegment(sketch, "E297", {"start": v(-29.6, -16.16) * mm, "end": v(-29.52, -16.14) * mm});
            skLineSegment(sketch, "E298", {"start": v(-29.52, -16.14) * mm, "end": v(-29.45, -16.11) * mm});
            skLineSegment(sketch, "E299", {"start": v(-29.45, -16.11) * mm, "end": v(-29.38, -16.1) * mm});
            skLineSegment(sketch, "E300", {"start": v(-29.38, -16.1) * mm, "end": v(-29.3, -16.07) * mm});
            skLineSegment(sketch, "E301", {"start": v(-29.3, -16.07) * mm, "end": v(-29.25, -16.05) * mm});
            skLineSegment(sketch, "E302", {"start": v(-29.25, -16.05) * mm, "end": v(-29.19, -16.03) * mm});
            skLineSegment(sketch, "E303", {"start": v(-29.19, -16.03) * mm, "end": v(-29.13, -16.01) * mm});
            skLineSegment(sketch, "E304", {"start": v(-29.13, -16.01) * mm, "end": v(-29.08, -16) * mm});
            skLineSegment(sketch, "E305", {"start": v(-29.08, -16) * mm, "end": v(-29.03, -15.97) * mm});
            skLineSegment(sketch, "E306", {"start": v(-29.03, -15.97) * mm, "end": v(-28.99, -15.96) * mm});
            skLineSegment(sketch, "E307", {"start": v(-28.99, -15.96) * mm, "end": v(-28.95, -15.94) * mm});
            skLineSegment(sketch, "E308", {"start": v(-28.95, -15.94) * mm, "end": v(-28.91, -15.92) * mm});
            skLineSegment(sketch, "E309", {"start": v(-28.91, -15.92) * mm, "end": v(-28.88, -15.91) * mm});
            skLineSegment(sketch, "E310", {"start": v(-28.88, -15.91) * mm, "end": v(-28.85, -15.9) * mm});
            skLineSegment(sketch, "E311", {"start": v(-28.85, -15.9) * mm, "end": v(-28.82, -15.89) * mm});
            skLineSegment(sketch, "E312", {"start": v(-28.82, -15.89) * mm, "end": v(-28.8, -15.88) * mm});
            skLineSegment(sketch, "E313", {"start": v(-28.8, -15.88) * mm, "end": v(-28.78, -15.87) * mm});
            skLineSegment(sketch, "E314", {"start": v(-28.78, -15.87) * mm, "end": v(-28.77, -15.86) * mm});
            skLineSegment(sketch, "E315", {"start": v(-28.77, -15.86) * mm, "end": v(-28.76, -15.86) * mm});
            skLineSegment(sketch, "E316", {"start": v(-28.76, -15.86) * mm, "end": v(-28.75, -15.85) * mm});
            skLineSegment(sketch, "E317", {"start": v(-28.75, -15.85) * mm, "end": v(-28.4, -15.65) * mm});
            skLineSegment(sketch, "E318", {"start": v(-28.4, -15.65) * mm, "end": v(-27.22, -17.6) * mm});
            skLineSegment(sketch, "E319", {"start": v(-27.22, -17.6) * mm, "end": v(-27.57, -17.83) * mm});
            skLineSegment(sketch, "E320", {"start": v(-27.57, -17.83) * mm, "end": v(-27.57, -17.84) * mm});
            skLineSegment(sketch, "E321", {"start": v(-27.57, -17.84) * mm, "end": v(-27.58, -17.84) * mm});
            skLineSegment(sketch, "E322", {"start": v(-27.58, -17.84) * mm, "end": v(-27.6, -17.85) * mm});
            skLineSegment(sketch, "E323", {"start": v(-27.6, -17.85) * mm, "end": v(-27.61, -17.86) * mm});
            skLineSegment(sketch, "E324", {"start": v(-27.61, -17.86) * mm, "end": v(-27.63, -17.88) * mm});
            skLineSegment(sketch, "E325", {"start": v(-27.63, -17.88) * mm, "end": v(-27.65, -17.9) * mm});
            skLineSegment(sketch, "E326", {"start": v(-27.65, -17.9) * mm, "end": v(-27.68, -17.91) * mm});
            skLineSegment(sketch, "E327", {"start": v(-27.68, -17.91) * mm, "end": v(-27.7, -17.94) * mm});
            skLineSegment(sketch, "E328", {"start": v(-27.7, -17.94) * mm, "end": v(-27.74, -17.96) * mm});
            skLineSegment(sketch, "E329", {"start": v(-27.74, -17.96) * mm, "end": v(-27.77, -17.99) * mm});
            skLineSegment(sketch, "E330", {"start": v(-27.77, -17.99) * mm, "end": v(-27.8, -18.02) * mm});
            skLineSegment(sketch, "E331", {"start": v(-27.8, -18.02) * mm, "end": v(-27.85, -18.05) * mm});
            skLineSegment(sketch, "E332", {"start": v(-27.85, -18.05) * mm, "end": v(-27.89, -18.1) * mm});
            skLineSegment(sketch, "E333", {"start": v(-27.89, -18.1) * mm, "end": v(-27.93, -18.13) * mm});
            skLineSegment(sketch, "E334", {"start": v(-27.93, -18.13) * mm, "end": v(-27.98, -18.17) * mm});
            skLineSegment(sketch, "E335", {"start": v(-27.98, -18.17) * mm, "end": v(-28.02, -18.22) * mm});
            skLineSegment(sketch, "E336", {"start": v(-28.02, -18.22) * mm, "end": v(-28.08, -18.27) * mm});
            skLineSegment(sketch, "E337", {"start": v(-28.08, -18.27) * mm, "end": v(-28.13, -18.32) * mm});
            skLineSegment(sketch, "E338", {"start": v(-28.13, -18.32) * mm, "end": v(-28.18, -18.38) * mm});
            skLineSegment(sketch, "E339", {"start": v(-28.18, -18.38) * mm, "end": v(-28.24, -18.44) * mm});
            skLineSegment(sketch, "E340", {"start": v(-28.24, -18.44) * mm, "end": v(-28.3, -18.5) * mm});
            skLineSegment(sketch, "E341", {"start": v(-28.3, -18.5) * mm, "end": v(-28.36, -18.57) * mm});
            skLineSegment(sketch, "E342", {"start": v(-28.36, -18.57) * mm, "end": v(-28.42, -18.64) * mm});
            skLineSegment(sketch, "E343", {"start": v(-28.42, -18.64) * mm, "end": v(-28.49, -18.7) * mm});
            skLineSegment(sketch, "E344", {"start": v(-28.49, -18.7) * mm, "end": v(-28.56, -18.79) * mm});
            skLineSegment(sketch, "E345", {"start": v(-28.56, -18.79) * mm, "end": v(-28.62, -18.87) * mm});
            skLineSegment(sketch, "E346", {"start": v(-28.62, -18.87) * mm, "end": v(-28.7, -18.95) * mm});
            skLineSegment(sketch, "E347", {"start": v(-28.7, -18.95) * mm, "end": v(-28.76, -19.04) * mm});
            skLineSegment(sketch, "E348", {"start": v(-28.76, -19.04) * mm, "end": v(-28.84, -19.13) * mm});
            skLineSegment(sketch, "E349", {"start": v(-28.84, -19.13) * mm, "end": v(-28.91, -19.23) * mm});
            skLineSegment(sketch, "E350", {"start": v(-28.91, -19.23) * mm, "end": v(-28.99, -19.33) * mm});
            skLineSegment(sketch, "E351", {"start": v(-28.99, -19.33) * mm, "end": v(-29.06, -19.43) * mm});
            skLineSegment(sketch, "E352", {"start": v(-29.06, -19.43) * mm, "end": v(-29.14, -19.54) * mm});
            skLineSegment(sketch, "E353", {"start": v(-29.14, -19.54) * mm, "end": v(-29.22, -19.65) * mm});
            skLineSegment(sketch, "E354", {"start": v(-29.22, -19.65) * mm, "end": v(-29.3, -19.77) * mm});
            skLineSegment(sketch, "E355", {"start": v(-29.3, -19.77) * mm, "end": v(-29.38, -19.89) * mm});
            skLineSegment(sketch, "E356", {"start": v(-29.38, -19.89) * mm, "end": v(-29.46, -20.01) * mm});
            skLineSegment(sketch, "E357", {"start": v(-29.46, -20.01) * mm, "end": v(-29.55, -20.14) * mm});
            skLineSegment(sketch, "E358", {"start": v(-29.55, -20.14) * mm, "end": v(-29.63, -20.27) * mm});
            skLineSegment(sketch, "E359", {"start": v(-29.63, -20.27) * mm, "end": v(-29.71, -20.41) * mm});
            skLineSegment(sketch, "E360", {"start": v(-29.71, -20.41) * mm, "end": v(-29.8, -20.55) * mm});
            skLineSegment(sketch, "E361", {"start": v(-29.8, -20.55) * mm, "end": v(-29.88, -20.7) * mm});
            skLineSegment(sketch, "E362", {"start": v(-29.88, -20.7) * mm, "end": v(-29.97, -20.85) * mm});
            skLineSegment(sketch, "E363", {"start": v(-29.97, -20.85) * mm, "end": v(-30.05, -21) * mm});
            skLineSegment(sketch, "E364", {"start": v(-30.05, -21) * mm, "end": v(-30.14, -21.16) * mm});
            skLineSegment(sketch, "E365", {"start": v(-30.14, -21.16) * mm, "end": v(-30.22, -21.32) * mm});
            skLineSegment(sketch, "E366", {"start": v(-30.22, -21.32) * mm, "end": v(-30.28, -21.47) * mm});
            skLineSegment(sketch, "E367", {"start": v(-30.28, -21.47) * mm, "end": v(-29.38, -22.68) * mm});
            skLineSegment(sketch, "E368", {"start": v(-29.38, -22.68) * mm, "end": v(-29.22, -22.67) * mm});
            skLineSegment(sketch, "E369", {"start": v(-29.22, -22.67) * mm, "end": v(-29.04, -22.64) * mm});
            skLineSegment(sketch, "E370", {"start": v(-29.04, -22.64) * mm, "end": v(-28.87, -22.6) * mm});
            skLineSegment(sketch, "E371", {"start": v(-28.87, -22.6) * mm, "end": v(-28.7, -22.57) * mm});
            skLineSegment(sketch, "E372", {"start": v(-28.7, -22.57) * mm, "end": v(-28.52, -22.53) * mm});
            skLineSegment(sketch, "E373", {"start": v(-28.52, -22.53) * mm, "end": v(-28.36, -22.5) * mm});
            skLineSegment(sketch, "E374", {"start": v(-28.36, -22.5) * mm, "end": v(-28.2, -22.45) * mm});
            skLineSegment(sketch, "E375", {"start": v(-28.2, -22.45) * mm, "end": v(-28.05, -22.41) * mm});
            skLineSegment(sketch, "E376", {"start": v(-28.05, -22.41) * mm, "end": v(-27.9, -22.37) * mm});
            skLineSegment(sketch, "E377", {"start": v(-27.9, -22.37) * mm, "end": v(-27.75, -22.33) * mm});
            skLineSegment(sketch, "E378", {"start": v(-27.75, -22.33) * mm, "end": v(-27.6, -22.3) * mm});
            skLineSegment(sketch, "E379", {"start": v(-27.6, -22.3) * mm, "end": v(-27.47, -22.25) * mm});
            skLineSegment(sketch, "E380", {"start": v(-27.47, -22.25) * mm, "end": v(-27.33, -22.2) * mm});
            skLineSegment(sketch, "E381", {"start": v(-27.33, -22.2) * mm, "end": v(-27.2, -22.16) * mm});
            skLineSegment(sketch, "E382", {"start": v(-27.2, -22.16) * mm, "end": v(-27.08, -22.12) * mm});
            skLineSegment(sketch, "E383", {"start": v(-27.08, -22.12) * mm, "end": v(-26.95, -22.08) * mm});
            skLineSegment(sketch, "E384", {"start": v(-26.95, -22.08) * mm, "end": v(-26.84, -22.03) * mm});
            skLineSegment(sketch, "E385", {"start": v(-26.84, -22.03) * mm, "end": v(-26.72, -22) * mm});
            skLineSegment(sketch, "E386", {"start": v(-26.72, -22) * mm, "end": v(-26.61, -21.95) * mm});
            skLineSegment(sketch, "E387", {"start": v(-26.61, -21.95) * mm, "end": v(-26.5, -21.9) * mm});
            skLineSegment(sketch, "E388", {"start": v(-26.5, -21.9) * mm, "end": v(-26.4, -21.86) * mm});
            skLineSegment(sketch, "E389", {"start": v(-26.4, -21.86) * mm, "end": v(-26.3, -21.82) * mm});
            skLineSegment(sketch, "E390", {"start": v(-26.3, -21.82) * mm, "end": v(-26.21, -21.78) * mm});
            skLineSegment(sketch, "E391", {"start": v(-26.21, -21.78) * mm, "end": v(-26.13, -21.74) * mm});
            skLineSegment(sketch, "E392", {"start": v(-26.13, -21.74) * mm, "end": v(-26.04, -21.7) * mm});
            skLineSegment(sketch, "E393", {"start": v(-26.04, -21.7) * mm, "end": v(-25.96, -21.66) * mm});
            skLineSegment(sketch, "E394", {"start": v(-25.96, -21.66) * mm, "end": v(-25.88, -21.62) * mm});
            skLineSegment(sketch, "E395", {"start": v(-25.88, -21.62) * mm, "end": v(-25.8, -21.59) * mm});
            skLineSegment(sketch, "E396", {"start": v(-25.8, -21.59) * mm, "end": v(-25.74, -21.55) * mm});
            skLineSegment(sketch, "E397", {"start": v(-25.74, -21.55) * mm, "end": v(-25.67, -21.51) * mm});
            skLineSegment(sketch, "E398", {"start": v(-25.67, -21.51) * mm, "end": v(-25.61, -21.48) * mm});
            skLineSegment(sketch, "E399", {"start": v(-25.61, -21.48) * mm, "end": v(-25.55, -21.45) * mm});
            skLineSegment(sketch, "E400", {"start": v(-25.55, -21.45) * mm, "end": v(-25.5, -21.42) * mm});
            skLineSegment(sketch, "E401", {"start": v(-25.5, -21.42) * mm, "end": v(-25.45, -21.39) * mm});
            skLineSegment(sketch, "E402", {"start": v(-25.45, -21.39) * mm, "end": v(-25.4, -21.36) * mm});
            skLineSegment(sketch, "E403", {"start": v(-25.4, -21.36) * mm, "end": v(-25.36, -21.33) * mm});
            skLineSegment(sketch, "E404", {"start": v(-25.36, -21.33) * mm, "end": v(-25.32, -21.3) * mm});
            skLineSegment(sketch, "E405", {"start": v(-25.32, -21.3) * mm, "end": v(-25.28, -21.28) * mm});
            skLineSegment(sketch, "E406", {"start": v(-25.28, -21.28) * mm, "end": v(-25.25, -21.26) * mm});
            skLineSegment(sketch, "E407", {"start": v(-25.25, -21.26) * mm, "end": v(-25.22, -21.24) * mm});
            skLineSegment(sketch, "E408", {"start": v(-25.22, -21.24) * mm, "end": v(-25.2, -21.22) * mm});
            skLineSegment(sketch, "E409", {"start": v(-25.2, -21.22) * mm, "end": v(-25.17, -21.2) * mm});
            skLineSegment(sketch, "E410", {"start": v(-25.17, -21.2) * mm, "end": v(-25.15, -21.2) * mm});
            skLineSegment(sketch, "E411", {"start": v(-25.15, -21.2) * mm, "end": v(-25.14, -21.18) * mm});
            skLineSegment(sketch, "E412", {"start": v(-25.14, -21.18) * mm, "end": v(-25.12, -21.17) * mm});
            skLineSegment(sketch, "E413", {"start": v(-25.12, -21.17) * mm, "end": v(-25.11, -21.16) * mm});
            skLineSegment(sketch, "E414", {"start": v(-25.11, -21.16) * mm, "end": v(-25.1, -21.16) * mm});
            skLineSegment(sketch, "E415", {"start": v(-25.1, -21.16) * mm, "end": v(-24.8, -20.9) * mm});
            skLineSegment(sketch, "E416", {"start": v(-24.8, -20.9) * mm, "end": v(-23.27, -22.58) * mm});
            skLineSegment(sketch, "E417", {"start": v(-23.27, -22.58) * mm, "end": v(-23.56, -22.87) * mm});
            skLineSegment(sketch, "E418", {"start": v(-23.56, -22.87) * mm, "end": v(-23.56, -22.87) * mm});
            skLineSegment(sketch, "E419", {"start": v(-23.56, -22.87) * mm, "end": v(-23.57, -22.88) * mm});
            skLineSegment(sketch, "E420", {"start": v(-23.57, -22.88) * mm, "end": v(-23.58, -22.9) * mm});
            skLineSegment(sketch, "E421", {"start": v(-23.58, -22.9) * mm, "end": v(-23.6, -22.9) * mm});
            skLineSegment(sketch, "E422", {"start": v(-23.6, -22.9) * mm, "end": v(-23.61, -22.93) * mm});
            skLineSegment(sketch, "E423", {"start": v(-23.61, -22.93) * mm, "end": v(-23.63, -22.95) * mm});
            skLineSegment(sketch, "E424", {"start": v(-23.63, -22.95) * mm, "end": v(-23.65, -22.97) * mm});
            skLineSegment(sketch, "E425", {"start": v(-23.65, -22.97) * mm, "end": v(-23.68, -23) * mm});
            skLineSegment(sketch, "E426", {"start": v(-23.68, -23) * mm, "end": v(-23.7, -23.03) * mm});
            skLineSegment(sketch, "E427", {"start": v(-23.7, -23.03) * mm, "end": v(-23.73, -23.06) * mm});
            skLineSegment(sketch, "E428", {"start": v(-23.73, -23.06) * mm, "end": v(-23.76, -23.1) * mm});
            skLineSegment(sketch, "E429", {"start": v(-23.76, -23.1) * mm, "end": v(-23.79, -23.14) * mm});
            skLineSegment(sketch, "E430", {"start": v(-23.79, -23.14) * mm, "end": v(-23.82, -23.18) * mm});
            skLineSegment(sketch, "E431", {"start": v(-23.82, -23.18) * mm, "end": v(-23.86, -23.23) * mm});
            skLineSegment(sketch, "E432", {"start": v(-23.86, -23.23) * mm, "end": v(-23.9, -23.28) * mm});
            skLineSegment(sketch, "E433", {"start": v(-23.9, -23.28) * mm, "end": v(-23.93, -23.34) * mm});
            skLineSegment(sketch, "E434", {"start": v(-23.93, -23.34) * mm, "end": v(-23.97, -23.4) * mm});
            skLineSegment(sketch, "E435", {"start": v(-23.97, -23.4) * mm, "end": v(-24.01, -23.46) * mm});
            skLineSegment(sketch, "E436", {"start": v(-24.01, -23.46) * mm, "end": v(-24.06, -23.52) * mm});
            skLineSegment(sketch, "E437", {"start": v(-24.06, -23.52) * mm, "end": v(-24.1, -23.6) * mm});
            skLineSegment(sketch, "E438", {"start": v(-24.1, -23.6) * mm, "end": v(-24.15, -23.66) * mm});
            skLineSegment(sketch, "E439", {"start": v(-24.15, -23.66) * mm, "end": v(-24.2, -23.74) * mm});
            skLineSegment(sketch, "E440", {"start": v(-24.2, -23.74) * mm, "end": v(-24.24, -23.82) * mm});
            skLineSegment(sketch, "E441", {"start": v(-24.24, -23.82) * mm, "end": v(-24.3, -23.9) * mm});
            skLineSegment(sketch, "E442", {"start": v(-24.3, -23.9) * mm, "end": v(-24.34, -24) * mm});
            skLineSegment(sketch, "E443", {"start": v(-24.34, -24) * mm, "end": v(-24.4, -24.09) * mm});
            skLineSegment(sketch, "E444", {"start": v(-24.4, -24.09) * mm, "end": v(-24.44, -24.19) * mm});
            skLineSegment(sketch, "E445", {"start": v(-24.44, -24.19) * mm, "end": v(-24.5, -24.29) * mm});
            skLineSegment(sketch, "E446", {"start": v(-24.5, -24.29) * mm, "end": v(-24.55, -24.4) * mm});
            skLineSegment(sketch, "E447", {"start": v(-24.55, -24.4) * mm, "end": v(-24.6, -24.5) * mm});
            skLineSegment(sketch, "E448", {"start": v(-24.6, -24.5) * mm, "end": v(-24.66, -24.61) * mm});
            skLineSegment(sketch, "E449", {"start": v(-24.66, -24.61) * mm, "end": v(-24.71, -24.73) * mm});
            skLineSegment(sketch, "E450", {"start": v(-24.71, -24.73) * mm, "end": v(-24.77, -24.85) * mm});
            skLineSegment(sketch, "E451", {"start": v(-24.77, -24.85) * mm, "end": v(-24.83, -24.98) * mm});
            skLineSegment(sketch, "E452", {"start": v(-24.83, -24.98) * mm, "end": v(-24.88, -25.1) * mm});
            skLineSegment(sketch, "E453", {"start": v(-24.88, -25.1) * mm, "end": v(-24.94, -25.24) * mm});
            skLineSegment(sketch, "E454", {"start": v(-24.94, -25.24) * mm, "end": v(-25, -25.38) * mm});
            skLineSegment(sketch, "E455", {"start": v(-25, -25.38) * mm, "end": v(-25.05, -25.52) * mm});
            skLineSegment(sketch, "E456", {"start": v(-25.05, -25.52) * mm, "end": v(-25.1, -25.67) * mm});
            skLineSegment(sketch, "E457", {"start": v(-25.1, -25.67) * mm, "end": v(-25.16, -25.82) * mm});
            skLineSegment(sketch, "E458", {"start": v(-25.16, -25.82) * mm, "end": v(-25.21, -25.97) * mm});
            skLineSegment(sketch, "E459", {"start": v(-25.21, -25.97) * mm, "end": v(-25.27, -26.13) * mm});
            skLineSegment(sketch, "E460", {"start": v(-25.27, -26.13) * mm, "end": v(-25.32, -26.3) * mm});
            skLineSegment(sketch, "E461", {"start": v(-25.32, -26.3) * mm, "end": v(-25.38, -26.46) * mm});
            skLineSegment(sketch, "E462", {"start": v(-25.38, -26.46) * mm, "end": v(-25.43, -26.63) * mm});
            skLineSegment(sketch, "E463", {"start": v(-25.43, -26.63) * mm, "end": v(-25.48, -26.81) * mm});
            skLineSegment(sketch, "E464", {"start": v(-25.48, -26.81) * mm, "end": v(-25.5, -26.96) * mm});
            skLineSegment(sketch, "E465", {"start": v(-25.5, -26.96) * mm, "end": v(-24.39, -27.98) * mm});
            skLineSegment(sketch, "E466", {"start": v(-24.39, -27.98) * mm, "end": v(-24.24, -27.94) * mm});
            skLineSegment(sketch, "E467", {"start": v(-24.24, -27.94) * mm, "end": v(-24.07, -27.87) * mm});
            skLineSegment(sketch, "E468", {"start": v(-24.07, -27.87) * mm, "end": v(-23.9, -27.8) * mm});
            skLineSegment(sketch, "E469", {"start": v(-23.9, -27.8) * mm, "end": v(-23.74, -27.73) * mm});
            skLineSegment(sketch, "E470", {"start": v(-23.74, -27.73) * mm, "end": v(-23.58, -27.66) * mm});
            skLineSegment(sketch, "E471", {"start": v(-23.58, -27.66) * mm, "end": v(-23.43, -27.6) * mm});
            skLineSegment(sketch, "E472", {"start": v(-23.43, -27.6) * mm, "end": v(-23.28, -27.52) * mm});
            skLineSegment(sketch, "E473", {"start": v(-23.28, -27.52) * mm, "end": v(-23.13, -27.45) * mm});
            skLineSegment(sketch, "E474", {"start": v(-23.13, -27.45) * mm, "end": v(-23, -27.39) * mm});
            skLineSegment(sketch, "E475", {"start": v(-23, -27.39) * mm, "end": v(-22.86, -27.32) * mm});
            skLineSegment(sketch, "E476", {"start": v(-22.86, -27.32) * mm, "end": v(-22.73, -27.25) * mm});
            skLineSegment(sketch, "E477", {"start": v(-22.73, -27.25) * mm, "end": v(-22.6, -27.18) * mm});
            skLineSegment(sketch, "E478", {"start": v(-22.6, -27.18) * mm, "end": v(-22.47, -27.11) * mm});
            skLineSegment(sketch, "E479", {"start": v(-22.47, -27.11) * mm, "end": v(-22.35, -27.04) * mm});
            skLineSegment(sketch, "E480", {"start": v(-22.35, -27.04) * mm, "end": v(-22.24, -26.98) * mm});
            skLineSegment(sketch, "E481", {"start": v(-22.24, -26.98) * mm, "end": v(-22.13, -26.91) * mm});
            skLineSegment(sketch, "E482", {"start": v(-22.13, -26.91) * mm, "end": v(-22.02, -26.85) * mm});
            skLineSegment(sketch, "E483", {"start": v(-22.02, -26.85) * mm, "end": v(-21.92, -26.78) * mm});
            skLineSegment(sketch, "E484", {"start": v(-21.92, -26.78) * mm, "end": v(-21.82, -26.72) * mm});
            skLineSegment(sketch, "E485", {"start": v(-21.82, -26.72) * mm, "end": v(-21.72, -26.66) * mm});
            skLineSegment(sketch, "E486", {"start": v(-21.72, -26.66) * mm, "end": v(-21.63, -26.6) * mm});
            skLineSegment(sketch, "E487", {"start": v(-21.63, -26.6) * mm, "end": v(-21.55, -26.53) * mm});
            skLineSegment(sketch, "E488", {"start": v(-21.55, -26.53) * mm, "end": v(-21.46, -26.48) * mm});
            skLineSegment(sketch, "E489", {"start": v(-21.46, -26.48) * mm, "end": v(-21.38, -26.42) * mm});
            skLineSegment(sketch, "E490", {"start": v(-21.38, -26.42) * mm, "end": v(-21.3, -26.36) * mm});
            skLineSegment(sketch, "E491", {"start": v(-21.3, -26.36) * mm, "end": v(-21.23, -26.3) * mm});
            skLineSegment(sketch, "E492", {"start": v(-21.23, -26.3) * mm, "end": v(-21.17, -26.26) * mm});
            skLineSegment(sketch, "E493", {"start": v(-21.17, -26.26) * mm, "end": v(-21.1, -26.2) * mm});
            skLineSegment(sketch, "E494", {"start": v(-21.1, -26.2) * mm, "end": v(-21.04, -26.16) * mm});
            skLineSegment(sketch, "E495", {"start": v(-21.04, -26.16) * mm, "end": v(-20.98, -26.1) * mm});
            skLineSegment(sketch, "E496", {"start": v(-20.98, -26.1) * mm, "end": v(-20.93, -26.06) * mm});
            skLineSegment(sketch, "E497", {"start": v(-20.93, -26.06) * mm, "end": v(-20.88, -26.02) * mm});
            skLineSegment(sketch, "E498", {"start": v(-20.88, -26.02) * mm, "end": v(-20.83, -25.98) * mm});
            skLineSegment(sketch, "E499", {"start": v(-20.83, -25.98) * mm, "end": v(-20.79, -25.94) * mm});
            skLineSegment(sketch, "E500", {"start": v(-20.79, -25.94) * mm, "end": v(-20.75, -25.9) * mm});
            skLineSegment(sketch, "E501", {"start": v(-20.75, -25.9) * mm, "end": v(-20.7, -25.87) * mm});
            skLineSegment(sketch, "E502", {"start": v(-20.7, -25.87) * mm, "end": v(-20.67, -25.83) * mm});
            skLineSegment(sketch, "E503", {"start": v(-20.67, -25.83) * mm, "end": v(-20.64, -25.8) * mm});
            skLineSegment(sketch, "E504", {"start": v(-20.64, -25.8) * mm, "end": v(-20.62, -25.78) * mm});
            skLineSegment(sketch, "E505", {"start": v(-20.62, -25.78) * mm, "end": v(-20.6, -25.75) * mm});
            skLineSegment(sketch, "E506", {"start": v(-20.6, -25.75) * mm, "end": v(-20.57, -25.73) * mm});
            skLineSegment(sketch, "E507", {"start": v(-20.57, -25.73) * mm, "end": v(-20.55, -25.7) * mm});
            skLineSegment(sketch, "E508", {"start": v(-20.55, -25.7) * mm, "end": v(-20.53, -25.69) * mm});
            skLineSegment(sketch, "E509", {"start": v(-20.53, -25.69) * mm, "end": v(-20.52, -25.67) * mm});
            skLineSegment(sketch, "E510", {"start": v(-20.52, -25.67) * mm, "end": v(-20.51, -25.66) * mm});
            skLineSegment(sketch, "E511", {"start": v(-20.51, -25.66) * mm, "end": v(-20.5, -25.65) * mm});
            skLineSegment(sketch, "E512", {"start": v(-20.5, -25.65) * mm, "end": v(-20.5, -25.65) * mm});
            skLineSegment(sketch, "E513", {"start": v(-20.5, -25.65) * mm, "end": v(-20.24, -25.33) * mm});
            skLineSegment(sketch, "E514", {"start": v(-20.24, -25.33) * mm, "end": v(-18.41, -26.69) * mm});
            skLineSegment(sketch, "E515", {"start": v(-18.41, -26.69) * mm, "end": v(-18.65, -27.02) * mm});
            skLineSegment(sketch, "E516", {"start": v(-18.65, -27.02) * mm, "end": v(-18.65, -27.03) * mm});
            skLineSegment(sketch, "E517", {"start": v(-18.65, -27.03) * mm, "end": v(-18.66, -27.04) * mm});
            skLineSegment(sketch, "E518", {"start": v(-18.66, -27.04) * mm, "end": v(-18.66, -27.05) * mm});
            skLineSegment(sketch, "E519", {"start": v(-18.66, -27.05) * mm, "end": v(-18.68, -27.07) * mm});
            skLineSegment(sketch, "E520", {"start": v(-18.68, -27.07) * mm, "end": v(-18.69, -27.1) * mm});
            skLineSegment(sketch, "E521", {"start": v(-18.69, -27.1) * mm, "end": v(-18.7, -27.12) * mm});
            skLineSegment(sketch, "E522", {"start": v(-18.7, -27.12) * mm, "end": v(-18.72, -27.14) * mm});
            skLineSegment(sketch, "E523", {"start": v(-18.72, -27.14) * mm, "end": v(-18.73, -27.17) * mm});
            skLineSegment(sketch, "E524", {"start": v(-18.73, -27.17) * mm, "end": v(-18.75, -27.2) * mm});
            skLineSegment(sketch, "E525", {"start": v(-18.75, -27.2) * mm, "end": v(-18.77, -27.25) * mm});
            skLineSegment(sketch, "E526", {"start": v(-18.77, -27.25) * mm, "end": v(-18.8, -27.29) * mm});
            skLineSegment(sketch, "E527", {"start": v(-18.8, -27.29) * mm, "end": v(-18.82, -27.34) * mm});
            skLineSegment(sketch, "E528", {"start": v(-18.82, -27.34) * mm, "end": v(-18.84, -27.38) * mm});
            skLineSegment(sketch, "E529", {"start": v(-18.84, -27.38) * mm, "end": v(-18.87, -27.44) * mm});
            skLineSegment(sketch, "E530", {"start": v(-18.87, -27.44) * mm, "end": v(-18.9, -27.5) * mm});
            skLineSegment(sketch, "E531", {"start": v(-18.9, -27.5) * mm, "end": v(-18.92, -27.56) * mm});
            skLineSegment(sketch, "E532", {"start": v(-18.92, -27.56) * mm, "end": v(-18.95, -27.62) * mm});
            skLineSegment(sketch, "E533", {"start": v(-18.95, -27.62) * mm, "end": v(-18.98, -27.7) * mm});
            skLineSegment(sketch, "E534", {"start": v(-18.98, -27.7) * mm, "end": v(-19, -27.76) * mm});
            skLineSegment(sketch, "E535", {"start": v(-19, -27.76) * mm, "end": v(-19.04, -27.84) * mm});
            skLineSegment(sketch, "E536", {"start": v(-19.04, -27.84) * mm, "end": v(-19.07, -27.92) * mm});
            skLineSegment(sketch, "E537", {"start": v(-19.07, -27.92) * mm, "end": v(-19.1, -28) * mm});
            skLineSegment(sketch, "E538", {"start": v(-19.1, -28) * mm, "end": v(-19.13, -28.1) * mm});
            skLineSegment(sketch, "E539", {"start": v(-19.13, -28.1) * mm, "end": v(-19.16, -28.19) * mm});
            skLineSegment(sketch, "E540", {"start": v(-19.16, -28.19) * mm, "end": v(-19.2, -28.28) * mm});
            skLineSegment(sketch, "E541", {"start": v(-19.2, -28.28) * mm, "end": v(-19.22, -28.38) * mm});
            skLineSegment(sketch, "E542", {"start": v(-19.22, -28.38) * mm, "end": v(-19.26, -28.49) * mm});
            skLineSegment(sketch, "E543", {"start": v(-19.26, -28.49) * mm, "end": v(-19.29, -28.6) * mm});
            skLineSegment(sketch, "E544", {"start": v(-19.29, -28.6) * mm, "end": v(-19.32, -28.71) * mm});
            skLineSegment(sketch, "E545", {"start": v(-19.32, -28.71) * mm, "end": v(-19.35, -28.83) * mm});
            skLineSegment(sketch, "E546", {"start": v(-19.35, -28.83) * mm, "end": v(-19.38, -28.95) * mm});
            skLineSegment(sketch, "E547", {"start": v(-19.38, -28.95) * mm, "end": v(-19.42, -29.08) * mm});
            skLineSegment(sketch, "E548", {"start": v(-19.42, -29.08) * mm, "end": v(-19.45, -29.2) * mm});
            skLineSegment(sketch, "E549", {"start": v(-19.45, -29.2) * mm, "end": v(-19.48, -29.34) * mm});
            skLineSegment(sketch, "E550", {"start": v(-19.48, -29.34) * mm, "end": v(-19.5, -29.48) * mm});
            skLineSegment(sketch, "E551", {"start": v(-19.5, -29.48) * mm, "end": v(-19.53, -29.62) * mm});
            skLineSegment(sketch, "E552", {"start": v(-19.53, -29.62) * mm, "end": v(-19.56, -29.77) * mm});
            skLineSegment(sketch, "E553", {"start": v(-19.56, -29.77) * mm, "end": v(-19.59, -29.92) * mm});
            skLineSegment(sketch, "E554", {"start": v(-19.59, -29.92) * mm, "end": v(-19.61, -30.07) * mm});
            skLineSegment(sketch, "E555", {"start": v(-19.61, -30.07) * mm, "end": v(-19.64, -30.23) * mm});
            skLineSegment(sketch, "E556", {"start": v(-19.64, -30.23) * mm, "end": v(-19.66, -30.4) * mm});
            skLineSegment(sketch, "E557", {"start": v(-19.66, -30.4) * mm, "end": v(-19.69, -30.56) * mm});
            skLineSegment(sketch, "E558", {"start": v(-19.69, -30.56) * mm, "end": v(-19.7, -30.73) * mm});
            skLineSegment(sketch, "E559", {"start": v(-19.7, -30.73) * mm, "end": v(-19.73, -30.9) * mm});
            skLineSegment(sketch, "E560", {"start": v(-19.73, -30.9) * mm, "end": v(-19.74, -31.08) * mm});
            skLineSegment(sketch, "E561", {"start": v(-19.74, -31.08) * mm, "end": v(-19.76, -31.27) * mm});
            skLineSegment(sketch, "E562", {"start": v(-19.76, -31.27) * mm, "end": v(-19.76, -31.42) * mm});
            skLineSegment(sketch, "E563", {"start": v(-19.76, -31.42) * mm, "end": v(-18.46, -32.2) * mm});
            skLineSegment(sketch, "E564", {"start": v(-18.46, -32.2) * mm, "end": v(-18.32, -32.13) * mm});
            skLineSegment(sketch, "E565", {"start": v(-18.32, -32.13) * mm, "end": v(-18.17, -32.03) * mm});
            skLineSegment(sketch, "E566", {"start": v(-18.17, -32.03) * mm, "end": v(-18.02, -31.93) * mm});
            skLineSegment(sketch, "E567", {"start": v(-18.02, -31.93) * mm, "end": v(-17.87, -31.83) * mm});
            skLineSegment(sketch, "E568", {"start": v(-17.87, -31.83) * mm, "end": v(-17.73, -31.73) * mm});
            skLineSegment(sketch, "E569", {"start": v(-17.73, -31.73) * mm, "end": v(-17.6, -31.63) * mm});
            skLineSegment(sketch, "E570", {"start": v(-17.6, -31.63) * mm, "end": v(-17.46, -31.54) * mm});
            skLineSegment(sketch, "E571", {"start": v(-17.46, -31.54) * mm, "end": v(-17.33, -31.44) * mm});
            skLineSegment(sketch, "E572", {"start": v(-17.33, -31.44) * mm, "end": v(-17.2, -31.34) * mm});
            skLineSegment(sketch, "E573", {"start": v(-17.2, -31.34) * mm, "end": v(-17.09, -31.25) * mm});
            skLineSegment(sketch, "E574", {"start": v(-17.09, -31.25) * mm, "end": v(-16.97, -31.16) * mm});
            skLineSegment(sketch, "E575", {"start": v(-16.97, -31.16) * mm, "end": v(-16.86, -31.07) * mm});
            skLineSegment(sketch, "E576", {"start": v(-16.86, -31.07) * mm, "end": v(-16.75, -30.97) * mm});
            skLineSegment(sketch, "E577", {"start": v(-16.75, -30.97) * mm, "end": v(-16.65, -30.89) * mm});
            skLineSegment(sketch, "E578", {"start": v(-16.65, -30.89) * mm, "end": v(-16.55, -30.8) * mm});
            skLineSegment(sketch, "E579", {"start": v(-16.55, -30.8) * mm, "end": v(-16.45, -30.71) * mm});
            skLineSegment(sketch, "E580", {"start": v(-16.45, -30.71) * mm, "end": v(-16.36, -30.63) * mm});
            skLineSegment(sketch, "E581", {"start": v(-16.36, -30.63) * mm, "end": v(-16.27, -30.54) * mm});
            skLineSegment(sketch, "E582", {"start": v(-16.27, -30.54) * mm, "end": v(-16.19, -30.46) * mm});
            skLineSegment(sketch, "E583", {"start": v(-16.19, -30.46) * mm, "end": v(-16.1, -30.38) * mm});
            skLineSegment(sketch, "E584", {"start": v(-16.1, -30.38) * mm, "end": v(-16.03, -30.3) * mm});
            skLineSegment(sketch, "E585", {"start": v(-16.03, -30.3) * mm, "end": v(-15.95, -30.23) * mm});
            skLineSegment(sketch, "E586", {"start": v(-15.95, -30.23) * mm, "end": v(-15.88, -30.15) * mm});
            skLineSegment(sketch, "E587", {"start": v(-15.88, -30.15) * mm, "end": v(-15.82, -30.08) * mm});
            skLineSegment(sketch, "E588", {"start": v(-15.82, -30.08) * mm, "end": v(-15.75, -30.01) * mm});
            skLineSegment(sketch, "E589", {"start": v(-15.75, -30.01) * mm, "end": v(-15.7, -29.95) * mm});
            skLineSegment(sketch, "E590", {"start": v(-15.7, -29.95) * mm, "end": v(-15.64, -29.88) * mm});
            skLineSegment(sketch, "E591", {"start": v(-15.64, -29.88) * mm, "end": v(-15.58, -29.82) * mm});
            skLineSegment(sketch, "E592", {"start": v(-15.58, -29.82) * mm, "end": v(-15.53, -29.76) * mm});
            skLineSegment(sketch, "E593", {"start": v(-15.53, -29.76) * mm, "end": v(-15.49, -29.7) * mm});
            skLineSegment(sketch, "E594", {"start": v(-15.49, -29.7) * mm, "end": v(-15.44, -29.65) * mm});
            skLineSegment(sketch, "E595", {"start": v(-15.44, -29.65) * mm, "end": v(-15.4, -29.6) * mm});
            skLineSegment(sketch, "E596", {"start": v(-15.4, -29.6) * mm, "end": v(-15.36, -29.54) * mm});
            skLineSegment(sketch, "E597", {"start": v(-15.36, -29.54) * mm, "end": v(-15.33, -29.5) * mm});
            skLineSegment(sketch, "E598", {"start": v(-15.33, -29.5) * mm, "end": v(-15.3, -29.45) * mm});
            skLineSegment(sketch, "E599", {"start": v(-15.3, -29.45) * mm, "end": v(-15.26, -29.4) * mm});
            skLineSegment(sketch, "E600", {"start": v(-15.26, -29.4) * mm, "end": v(-15.24, -29.37) * mm});
            skLineSegment(sketch, "E601", {"start": v(-15.24, -29.37) * mm, "end": v(-15.21, -29.34) * mm});
            skLineSegment(sketch, "E602", {"start": v(-15.21, -29.34) * mm, "end": v(-15.2, -29.3) * mm});
            skLineSegment(sketch, "E603", {"start": v(-15.2, -29.3) * mm, "end": v(-15.17, -29.27) * mm});
            skLineSegment(sketch, "E604", {"start": v(-15.17, -29.27) * mm, "end": v(-15.15, -29.25) * mm});
            skLineSegment(sketch, "E605", {"start": v(-15.15, -29.25) * mm, "end": v(-15.14, -29.22) * mm});
            skLineSegment(sketch, "E606", {"start": v(-15.14, -29.22) * mm, "end": v(-15.13, -29.2) * mm});
            skLineSegment(sketch, "E607", {"start": v(-15.13, -29.2) * mm, "end": v(-15.12, -29.19) * mm});
            skLineSegment(sketch, "E608", {"start": v(-15.12, -29.19) * mm, "end": v(-15.1, -29.17) * mm});
            skLineSegment(sketch, "E609", {"start": v(-15.1, -29.17) * mm, "end": v(-15.1, -29.16) * mm});
            skLineSegment(sketch, "E610", {"start": v(-15.1, -29.16) * mm, "end": v(-15.1, -29.15) * mm});
            skLineSegment(sketch, "E611", {"start": v(-15.1, -29.15) * mm, "end": v(-14.91, -28.8) * mm});
            skLineSegment(sketch, "E612", {"start": v(-14.91, -28.8) * mm, "end": v(-12.85, -29.77) * mm});
            skLineSegment(sketch, "E613", {"start": v(-12.85, -29.77) * mm, "end": v(-13.01, -30.14) * mm});
            skLineSegment(sketch, "E614", {"start": v(-13.01, -30.14) * mm, "end": v(-13.02, -30.15) * mm});
            skLineSegment(sketch, "E615", {"start": v(-13.02, -30.15) * mm, "end": v(-13.02, -30.16) * mm});
            skLineSegment(sketch, "E616", {"start": v(-13.02, -30.16) * mm, "end": v(-13.03, -30.18) * mm});
            skLineSegment(sketch, "E617", {"start": v(-13.03, -30.18) * mm, "end": v(-13.03, -30.2) * mm});
            skLineSegment(sketch, "E618", {"start": v(-13.03, -30.2) * mm, "end": v(-13.04, -30.22) * mm});
            skLineSegment(sketch, "E619", {"start": v(-13.04, -30.22) * mm, "end": v(-13.05, -30.24) * mm});
            skLineSegment(sketch, "E620", {"start": v(-13.05, -30.24) * mm, "end": v(-13.06, -30.27) * mm});
            skLineSegment(sketch, "E621", {"start": v(-13.06, -30.27) * mm, "end": v(-13.07, -30.3) * mm});
            skLineSegment(sketch, "E622", {"start": v(-13.07, -30.3) * mm, "end": v(-13.08, -30.34) * mm});
            skLineSegment(sketch, "E623", {"start": v(-13.08, -30.34) * mm, "end": v(-13.1, -30.39) * mm});
            skLineSegment(sketch, "E624", {"start": v(-13.1, -30.39) * mm, "end": v(-13.1, -30.43) * mm});
            skLineSegment(sketch, "E625", {"start": v(-13.1, -30.43) * mm, "end": v(-13.12, -30.48) * mm});
            skLineSegment(sketch, "E626", {"start": v(-13.12, -30.48) * mm, "end": v(-13.14, -30.53) * mm});
            skLineSegment(sketch, "E627", {"start": v(-13.14, -30.53) * mm, "end": v(-13.15, -30.6) * mm});
            skLineSegment(sketch, "E628", {"start": v(-13.15, -30.6) * mm, "end": v(-13.17, -30.65) * mm});
            skLineSegment(sketch, "E629", {"start": v(-13.17, -30.65) * mm, "end": v(-13.18, -30.72) * mm});
            skLineSegment(sketch, "E630", {"start": v(-13.18, -30.72) * mm, "end": v(-13.2, -30.79) * mm});
            skLineSegment(sketch, "E631", {"start": v(-13.2, -30.79) * mm, "end": v(-13.2, -30.86) * mm});
            skLineSegment(sketch, "E632", {"start": v(-13.2, -30.86) * mm, "end": v(-13.22, -30.94) * mm});
            skLineSegment(sketch, "E633", {"start": v(-13.22, -30.94) * mm, "end": v(-13.24, -31.02) * mm});
            skLineSegment(sketch, "E634", {"start": v(-13.24, -31.02) * mm, "end": v(-13.25, -31.1) * mm});
            skLineSegment(sketch, "E635", {"start": v(-13.25, -31.1) * mm, "end": v(-13.27, -31.2) * mm});
            skLineSegment(sketch, "E636", {"start": v(-13.27, -31.2) * mm, "end": v(-13.28, -31.29) * mm});
            skLineSegment(sketch, "E637", {"start": v(-13.28, -31.29) * mm, "end": v(-13.3, -31.38) * mm});
            skLineSegment(sketch, "E638", {"start": v(-13.3, -31.38) * mm, "end": v(-13.3, -31.48) * mm});
            skLineSegment(sketch, "E639", {"start": v(-13.3, -31.48) * mm, "end": v(-13.32, -31.59) * mm});
            skLineSegment(sketch, "E640", {"start": v(-13.32, -31.59) * mm, "end": v(-13.33, -31.7) * mm});
            skLineSegment(sketch, "E641", {"start": v(-13.33, -31.7) * mm, "end": v(-13.34, -31.81) * mm});
            skLineSegment(sketch, "E642", {"start": v(-13.34, -31.81) * mm, "end": v(-13.35, -31.93) * mm});
            skLineSegment(sketch, "E643", {"start": v(-13.35, -31.93) * mm, "end": v(-13.36, -32.05) * mm});
            skLineSegment(sketch, "E644", {"start": v(-13.36, -32.05) * mm, "end": v(-13.36, -32.18) * mm});
            skLineSegment(sketch, "E645", {"start": v(-13.36, -32.18) * mm, "end": v(-13.37, -32.3) * mm});
            skLineSegment(sketch, "E646", {"start": v(-13.37, -32.3) * mm, "end": v(-13.37, -32.44) * mm});
            skLineSegment(sketch, "E647", {"start": v(-13.37, -32.44) * mm, "end": v(-13.38, -32.57) * mm});
            skLineSegment(sketch, "E648", {"start": v(-13.38, -32.57) * mm, "end": v(-13.38, -32.72) * mm});
            skLineSegment(sketch, "E649", {"start": v(-13.38, -32.72) * mm, "end": v(-13.38, -32.86) * mm});
            skLineSegment(sketch, "E650", {"start": v(-13.38, -32.86) * mm, "end": v(-13.38, -33) * mm});
            skLineSegment(sketch, "E651", {"start": v(-13.38, -33) * mm, "end": v(-13.38, -33.16) * mm});
            skLineSegment(sketch, "E652", {"start": v(-13.38, -33.16) * mm, "end": v(-13.37, -33.32) * mm});
            skLineSegment(sketch, "E653", {"start": v(-13.37, -33.32) * mm, "end": v(-13.37, -33.48) * mm});
            skLineSegment(sketch, "E654", {"start": v(-13.37, -33.48) * mm, "end": v(-13.36, -33.64) * mm});
            skLineSegment(sketch, "E655", {"start": v(-13.36, -33.64) * mm, "end": v(-13.35, -33.81) * mm});
            skLineSegment(sketch, "E656", {"start": v(-13.35, -33.81) * mm, "end": v(-13.33, -33.98) * mm});
            skLineSegment(sketch, "E657", {"start": v(-13.33, -33.98) * mm, "end": v(-13.32, -34.16) * mm});
            skLineSegment(sketch, "E658", {"start": v(-13.32, -34.16) * mm, "end": v(-13.3, -34.34) * mm});
            skLineSegment(sketch, "E659", {"start": v(-13.3, -34.34) * mm, "end": v(-13.28, -34.52) * mm});
            skLineSegment(sketch, "E660", {"start": v(-13.28, -34.52) * mm, "end": v(-13.25, -34.67) * mm});
            skLineSegment(sketch, "E661", {"start": v(-13.25, -34.67) * mm, "end": v(-11.82, -35.18) * mm});
            skLineSegment(sketch, "E662", {"start": v(-11.82, -35.18) * mm, "end": v(-11.7, -35.09) * mm});
            skLineSegment(sketch, "E663", {"start": v(-11.7, -35.09) * mm, "end": v(-11.57, -34.96) * mm});
            skLineSegment(sketch, "E664", {"start": v(-11.57, -34.96) * mm, "end": v(-11.44, -34.83) * mm});
            skLineSegment(sketch, "E665", {"start": v(-11.44, -34.83) * mm, "end": v(-11.32, -34.7) * mm});
            skLineSegment(sketch, "E666", {"start": v(-11.32, -34.7) * mm, "end": v(-11.2, -34.58) * mm});
            skLineSegment(sketch, "E667", {"start": v(-11.2, -34.58) * mm, "end": v(-11.08, -34.46) * mm});
            skLineSegment(sketch, "E668", {"start": v(-11.08, -34.46) * mm, "end": v(-10.97, -34.34) * mm});
            skLineSegment(sketch, "E669", {"start": v(-10.97, -34.34) * mm, "end": v(-10.87, -34.22) * mm});
            skLineSegment(sketch, "E670", {"start": v(-10.87, -34.22) * mm, "end": v(-10.76, -34.1) * mm});
            skLineSegment(sketch, "E671", {"start": v(-10.76, -34.1) * mm, "end": v(-10.66, -33.98) * mm});
            skLineSegment(sketch, "E672", {"start": v(-10.66, -33.98) * mm, "end": v(-10.57, -33.87) * mm});
            skLineSegment(sketch, "E673", {"start": v(-10.57, -33.87) * mm, "end": v(-10.48, -33.76) * mm});
            skLineSegment(sketch, "E674", {"start": v(-10.48, -33.76) * mm, "end": v(-10.39, -33.65) * mm});
            skLineSegment(sketch, "E675", {"start": v(-10.39, -33.65) * mm, "end": v(-10.3, -33.54) * mm});
            skLineSegment(sketch, "E676", {"start": v(-10.3, -33.54) * mm, "end": v(-10.22, -33.43) * mm});
            skLineSegment(sketch, "E677", {"start": v(-10.22, -33.43) * mm, "end": v(-10.15, -33.33) * mm});
            skLineSegment(sketch, "E678", {"start": v(-10.15, -33.33) * mm, "end": v(-10.07, -33.23) * mm});
            skLineSegment(sketch, "E679", {"start": v(-10.07, -33.23) * mm, "end": v(-10, -33.13) * mm});
            skLineSegment(sketch, "E680", {"start": v(-10, -33.13) * mm, "end": v(-9.93, -33.03) * mm});
            skLineSegment(sketch, "E681", {"start": v(-9.93, -33.03) * mm, "end": v(-9.87, -32.94) * mm});
            skLineSegment(sketch, "E682", {"start": v(-9.87, -32.94) * mm, "end": v(-9.8, -32.85) * mm});
            skLineSegment(sketch, "E683", {"start": v(-9.8, -32.85) * mm, "end": v(-9.75, -32.76) * mm});
            skLineSegment(sketch, "E684", {"start": v(-9.75, -32.76) * mm, "end": v(-9.7, -32.67) * mm});
            skLineSegment(sketch, "E685", {"start": v(-9.7, -32.67) * mm, "end": v(-9.64, -32.6) * mm});
            skLineSegment(sketch, "E686", {"start": v(-9.64, -32.6) * mm, "end": v(-9.6, -32.51) * mm});
            skLineSegment(sketch, "E687", {"start": v(-9.6, -32.51) * mm, "end": v(-9.55, -32.43) * mm});
            skLineSegment(sketch, "E688", {"start": v(-9.55, -32.43) * mm, "end": v(-9.5, -32.36) * mm});
            skLineSegment(sketch, "E689", {"start": v(-9.5, -32.36) * mm, "end": v(-9.47, -32.29) * mm});
            skLineSegment(sketch, "E690", {"start": v(-9.47, -32.29) * mm, "end": v(-9.43, -32.22) * mm});
            skLineSegment(sketch, "E691", {"start": v(-9.43, -32.22) * mm, "end": v(-9.4, -32.15) * mm});
            skLineSegment(sketch, "E692", {"start": v(-9.4, -32.15) * mm, "end": v(-9.36, -32.09) * mm});
            skLineSegment(sketch, "E693", {"start": v(-9.36, -32.09) * mm, "end": v(-9.33, -32.03) * mm});
            skLineSegment(sketch, "E694", {"start": v(-9.33, -32.03) * mm, "end": v(-9.3, -31.97) * mm});
            skLineSegment(sketch, "E695", {"start": v(-9.3, -31.97) * mm, "end": v(-9.28, -31.92) * mm});
            skLineSegment(sketch, "E696", {"start": v(-9.28, -31.92) * mm, "end": v(-9.25, -31.87) * mm});
            skLineSegment(sketch, "E697", {"start": v(-9.25, -31.87) * mm, "end": v(-9.23, -31.82) * mm});
            skLineSegment(sketch, "E698", {"start": v(-9.23, -31.82) * mm, "end": v(-9.21, -31.78) * mm});
            skLineSegment(sketch, "E699", {"start": v(-9.21, -31.78) * mm, "end": v(-9.2, -31.74) * mm});
            skLineSegment(sketch, "E700", {"start": v(-9.2, -31.74) * mm, "end": v(-9.18, -31.7) * mm});
            skLineSegment(sketch, "E701", {"start": v(-9.18, -31.7) * mm, "end": v(-9.17, -31.67) * mm});
            skLineSegment(sketch, "E702", {"start": v(-9.17, -31.67) * mm, "end": v(-9.16, -31.64) * mm});
            skLineSegment(sketch, "E703", {"start": v(-9.16, -31.64) * mm, "end": v(-9.15, -31.61) * mm});
            skLineSegment(sketch, "E704", {"start": v(-9.15, -31.61) * mm, "end": v(-9.14, -31.6) * mm});
            skLineSegment(sketch, "E705", {"start": v(-9.14, -31.6) * mm, "end": v(-9.13, -31.57) * mm});
            skLineSegment(sketch, "E706", {"start": v(-9.13, -31.57) * mm, "end": v(-9.13, -31.56) * mm});
            skLineSegment(sketch, "E707", {"start": v(-9.13, -31.56) * mm, "end": v(-9.12, -31.55) * mm});
            skLineSegment(sketch, "E708", {"start": v(-9.12, -31.55) * mm, "end": v(-9.12, -31.54) * mm});
            skLineSegment(sketch, "E709", {"start": v(-9.12, -31.54) * mm, "end": v(-9, -31.15) * mm});
            skLineSegment(sketch, "E710", {"start": v(-9, -31.15) * mm, "end": v(-6.8, -31.7) * mm});
            skLineSegment(sketch, "E711", {"start": v(-6.8, -31.7) * mm, "end": v(-6.88, -32.1) * mm});
            skLineSegment(sketch, "E712", {"start": v(-6.88, -32.1) * mm, "end": v(-6.89, -32.1) * mm});
            skLineSegment(sketch, "E713", {"start": v(-6.89, -32.1) * mm, "end": v(-6.89, -32.12) * mm});
            skLineSegment(sketch, "E714", {"start": v(-6.89, -32.12) * mm, "end": v(-6.9, -32.14) * mm});
            skLineSegment(sketch, "E715", {"start": v(-6.9, -32.14) * mm, "end": v(-6.9, -32.16) * mm});
            skLineSegment(sketch, "E716", {"start": v(-6.9, -32.16) * mm, "end": v(-6.9, -32.18) * mm});
            skLineSegment(sketch, "E717", {"start": v(-6.9, -32.18) * mm, "end": v(-6.9, -32.2) * mm});
            skLineSegment(sketch, "E718", {"start": v(-6.9, -32.2) * mm, "end": v(-6.9, -32.24) * mm});
            skLineSegment(sketch, "E719", {"start": v(-6.9, -32.24) * mm, "end": v(-6.9, -32.27) * mm});
            skLineSegment(sketch, "E720", {"start": v(-6.9, -32.27) * mm, "end": v(-6.91, -32.31) * mm});
            skLineSegment(sketch, "E721", {"start": v(-6.91, -32.31) * mm, "end": v(-6.92, -32.36) * mm});
            skLineSegment(sketch, "E722", {"start": v(-6.92, -32.36) * mm, "end": v(-6.92, -32.4) * mm});
            skLineSegment(sketch, "E723", {"start": v(-6.92, -32.4) * mm, "end": v(-6.92, -32.46) * mm});
            skLineSegment(sketch, "E724", {"start": v(-6.92, -32.46) * mm, "end": v(-6.93, -32.51) * mm});
            skLineSegment(sketch, "E725", {"start": v(-6.93, -32.51) * mm, "end": v(-6.93, -32.57) * mm});
            skLineSegment(sketch, "E726", {"start": v(-6.93, -32.57) * mm, "end": v(-6.93, -32.63) * mm});
            skLineSegment(sketch, "E727", {"start": v(-6.93, -32.63) * mm, "end": v(-6.93, -32.7) * mm});
            skLineSegment(sketch, "E728", {"start": v(-6.93, -32.7) * mm, "end": v(-6.93, -32.77) * mm});
            skLineSegment(sketch, "E729", {"start": v(-6.93, -32.77) * mm, "end": v(-6.93, -32.84) * mm});
            skLineSegment(sketch, "E730", {"start": v(-6.93, -32.84) * mm, "end": v(-6.93, -32.92) * mm});
            skLineSegment(sketch, "E731", {"start": v(-6.93, -32.92) * mm, "end": v(-6.93, -33) * mm});
            skLineSegment(sketch, "E732", {"start": v(-6.93, -33) * mm, "end": v(-6.93, -33.1) * mm});
            skLineSegment(sketch, "E733", {"start": v(-6.93, -33.1) * mm, "end": v(-6.93, -33.18) * mm});
            skLineSegment(sketch, "E734", {"start": v(-6.93, -33.18) * mm, "end": v(-6.92, -33.28) * mm});
            skLineSegment(sketch, "E735", {"start": v(-6.92, -33.28) * mm, "end": v(-6.92, -33.37) * mm});
            skLineSegment(sketch, "E736", {"start": v(-6.92, -33.37) * mm, "end": v(-6.9, -33.48) * mm});
            skLineSegment(sketch, "E737", {"start": v(-6.9, -33.48) * mm, "end": v(-6.9, -33.58) * mm});
            skLineSegment(sketch, "E738", {"start": v(-6.9, -33.58) * mm, "end": v(-6.89, -33.7) * mm});
            skLineSegment(sketch, "E739", {"start": v(-6.89, -33.7) * mm, "end": v(-6.88, -33.8) * mm});
            skLineSegment(sketch, "E740", {"start": v(-6.88, -33.8) * mm, "end": v(-6.86, -33.92) * mm});
            skLineSegment(sketch, "E741", {"start": v(-6.86, -33.92) * mm, "end": v(-6.85, -34.04) * mm});
            skLineSegment(sketch, "E742", {"start": v(-6.85, -34.04) * mm, "end": v(-6.83, -34.16) * mm});
            skLineSegment(sketch, "E743", {"start": v(-6.83, -34.16) * mm, "end": v(-6.81, -34.3) * mm});
            skLineSegment(sketch, "E744", {"start": v(-6.81, -34.3) * mm, "end": v(-6.79, -34.42) * mm});
            skLineSegment(sketch, "E745", {"start": v(-6.79, -34.42) * mm, "end": v(-6.77, -34.56) * mm});
            skLineSegment(sketch, "E746", {"start": v(-6.77, -34.56) * mm, "end": v(-6.74, -34.7) * mm});
            skLineSegment(sketch, "E747", {"start": v(-6.74, -34.7) * mm, "end": v(-6.71, -34.84) * mm});
            skLineSegment(sketch, "E748", {"start": v(-6.71, -34.84) * mm, "end": v(-6.68, -34.99) * mm});
            skLineSegment(sketch, "E749", {"start": v(-6.68, -34.99) * mm, "end": v(-6.65, -35.13) * mm});
            skLineSegment(sketch, "E750", {"start": v(-6.65, -35.13) * mm, "end": v(-6.61, -35.29) * mm});
            skLineSegment(sketch, "E751", {"start": v(-6.61, -35.29) * mm, "end": v(-6.58, -35.44) * mm});
            skLineSegment(sketch, "E752", {"start": v(-6.58, -35.44) * mm, "end": v(-6.54, -35.6) * mm});
            skLineSegment(sketch, "E753", {"start": v(-6.54, -35.6) * mm, "end": v(-6.5, -35.77) * mm});
            skLineSegment(sketch, "E754", {"start": v(-6.5, -35.77) * mm, "end": v(-6.45, -35.93) * mm});
            skLineSegment(sketch, "E755", {"start": v(-6.45, -35.93) * mm, "end": v(-6.4, -36.1) * mm});
            skLineSegment(sketch, "E756", {"start": v(-6.4, -36.1) * mm, "end": v(-6.35, -36.27) * mm});
            skLineSegment(sketch, "E757", {"start": v(-6.35, -36.27) * mm, "end": v(-6.3, -36.45) * mm});
            skLineSegment(sketch, "E758", {"start": v(-6.3, -36.45) * mm, "end": v(-6.23, -36.6) * mm});
            skLineSegment(sketch, "E759", {"start": v(-6.23, -36.6) * mm, "end": v(-4.73, -36.81) * mm});
            skLineSegment(sketch, "E760", {"start": v(-4.73, -36.81) * mm, "end": v(-4.63, -36.7) * mm});
            skLineSegment(sketch, "E761", {"start": v(-4.63, -36.7) * mm, "end": v(-4.53, -36.55) * mm});
            skLineSegment(sketch, "E762", {"start": v(-4.53, -36.55) * mm, "end": v(-4.43, -36.4) * mm});
            skLineSegment(sketch, "E763", {"start": v(-4.43, -36.4) * mm, "end": v(-4.33, -36.25) * mm});
            skLineSegment(sketch, "E764", {"start": v(-4.33, -36.25) * mm, "end": v(-4.24, -36.1) * mm});
            skLineSegment(sketch, "E765", {"start": v(-4.24, -36.1) * mm, "end": v(-4.15, -35.96) * mm});
            skLineSegment(sketch, "E766", {"start": v(-4.15, -35.96) * mm, "end": v(-4.06, -35.82) * mm});
            skLineSegment(sketch, "E767", {"start": v(-4.06, -35.82) * mm, "end": v(-3.98, -35.68) * mm});
            skLineSegment(sketch, "E768", {"start": v(-3.98, -35.68) * mm, "end": v(-3.9, -35.54) * mm});
            skLineSegment(sketch, "E769", {"start": v(-3.9, -35.54) * mm, "end": v(-3.83, -35.41) * mm});
            skLineSegment(sketch, "E770", {"start": v(-3.83, -35.41) * mm, "end": v(-3.76, -35.28) * mm});
            skLineSegment(sketch, "E771", {"start": v(-3.76, -35.28) * mm, "end": v(-3.69, -35.15) * mm});
            skLineSegment(sketch, "E772", {"start": v(-3.69, -35.15) * mm, "end": v(-3.62, -35.03) * mm});
            skLineSegment(sketch, "E773", {"start": v(-3.62, -35.03) * mm, "end": v(-3.56, -34.9) * mm});
            skLineSegment(sketch, "E774", {"start": v(-3.56, -34.9) * mm, "end": v(-3.5, -34.79) * mm});
            skLineSegment(sketch, "E775", {"start": v(-3.5, -34.79) * mm, "end": v(-3.45, -34.67) * mm});
            skLineSegment(sketch, "E776", {"start": v(-3.45, -34.67) * mm, "end": v(-3.4, -34.56) * mm});
            skLineSegment(sketch, "E777", {"start": v(-3.4, -34.56) * mm, "end": v(-3.35, -34.45) * mm});
            skLineSegment(sketch, "E778", {"start": v(-3.35, -34.45) * mm, "end": v(-3.3, -34.34) * mm});
            skLineSegment(sketch, "E779", {"start": v(-3.3, -34.34) * mm, "end": v(-3.25, -34.23) * mm});
            skLineSegment(sketch, "E780", {"start": v(-3.25, -34.23) * mm, "end": v(-3.21, -34.13) * mm});
            skLineSegment(sketch, "E781", {"start": v(-3.21, -34.13) * mm, "end": v(-3.17, -34.03) * mm});
            skLineSegment(sketch, "E782", {"start": v(-3.17, -34.03) * mm, "end": v(-3.14, -33.94) * mm});
            skLineSegment(sketch, "E783", {"start": v(-3.14, -33.94) * mm, "end": v(-3.1, -33.85) * mm});
            skLineSegment(sketch, "E784", {"start": v(-3.1, -33.85) * mm, "end": v(-3.07, -33.76) * mm});
            skLineSegment(sketch, "E785", {"start": v(-3.07, -33.76) * mm, "end": v(-3.04, -33.67) * mm});
            skLineSegment(sketch, "E786", {"start": v(-3.04, -33.67) * mm, "end": v(-3.01, -33.6) * mm});
            skLineSegment(sketch, "E787", {"start": v(-3.01, -33.6) * mm, "end": v(-2.99, -33.51) * mm});
            skLineSegment(sketch, "E788", {"start": v(-2.99, -33.51) * mm, "end": v(-2.96, -33.44) * mm});
            skLineSegment(sketch, "E789", {"start": v(-2.96, -33.44) * mm, "end": v(-2.94, -33.37) * mm});
            skLineSegment(sketch, "E790", {"start": v(-2.94, -33.37) * mm, "end": v(-2.92, -33.3) * mm});
            skLineSegment(sketch, "E791", {"start": v(-2.92, -33.3) * mm, "end": v(-2.9, -33.23) * mm});
            skLineSegment(sketch, "E792", {"start": v(-2.9, -33.23) * mm, "end": v(-2.89, -33.17) * mm});
            skLineSegment(sketch, "E793", {"start": v(-2.89, -33.17) * mm, "end": v(-2.87, -33.12) * mm});
            skLineSegment(sketch, "E794", {"start": v(-2.87, -33.12) * mm, "end": v(-2.86, -33.06) * mm});
            skLineSegment(sketch, "E795", {"start": v(-2.86, -33.06) * mm, "end": v(-2.85, -33.01) * mm});
            skLineSegment(sketch, "E796", {"start": v(-2.85, -33.01) * mm, "end": v(-2.84, -32.97) * mm});
            skLineSegment(sketch, "E797", {"start": v(-2.84, -32.97) * mm, "end": v(-2.83, -32.92) * mm});
            skLineSegment(sketch, "E798", {"start": v(-2.83, -32.92) * mm, "end": v(-2.82, -32.89) * mm});
            skLineSegment(sketch, "E799", {"start": v(-2.82, -32.89) * mm, "end": v(-2.81, -32.85) * mm});
            skLineSegment(sketch, "E800", {"start": v(-2.81, -32.85) * mm, "end": v(-2.8, -32.82) * mm});
            skLineSegment(sketch, "E801", {"start": v(-2.8, -32.82) * mm, "end": v(-2.8, -32.8) * mm});
            skLineSegment(sketch, "E802", {"start": v(-2.8, -32.8) * mm, "end": v(-2.8, -32.77) * mm});
            skLineSegment(sketch, "E803", {"start": v(-2.8, -32.77) * mm, "end": v(-2.8, -32.75) * mm});
            skLineSegment(sketch, "E804", {"start": v(-2.8, -32.75) * mm, "end": v(-2.8, -32.73) * mm});
            skLineSegment(sketch, "E805", {"start": v(-2.8, -32.73) * mm, "end": v(-2.8, -32.72) * mm});
            skLineSegment(sketch, "E806", {"start": v(-2.8, -32.72) * mm, "end": v(-2.8, -32.71) * mm});
            skLineSegment(sketch, "E807", {"start": v(-2.8, -32.71) * mm, "end": v(-2.76, -32.3) * mm});
            skLineSegment(sketch, "E808", {"start": v(-2.76, -32.3) * mm, "end": v(-0.48, -32.42) * mm});
            skLineSegment(sketch, "E809", {"start": v(-0.48, -32.42) * mm, "end": v(-0.49, -32.83) * mm});
            skLineSegment(sketch, "E810", {"start": v(-0.49, -32.83) * mm, "end": v(-0.49, -32.84) * mm});
            skLineSegment(sketch, "E811", {"start": v(-0.49, -32.84) * mm, "end": v(-0.49, -32.85) * mm});
            skLineSegment(sketch, "E812", {"start": v(-0.49, -32.85) * mm, "end": v(-0.49, -32.86) * mm});
            skLineSegment(sketch, "E813", {"start": v(-0.49, -32.86) * mm, "end": v(-0.49, -32.88) * mm});
            skLineSegment(sketch, "E814", {"start": v(-0.49, -32.88) * mm, "end": v(-0.49, -32.9) * mm});
            skLineSegment(sketch, "E815", {"start": v(-0.49, -32.9) * mm, "end": v(-0.48, -32.94) * mm});
            skLineSegment(sketch, "E816", {"start": v(-0.48, -32.94) * mm, "end": v(-0.48, -32.97) * mm});
            skLineSegment(sketch, "E817", {"start": v(-0.48, -32.97) * mm, "end": v(-0.48, -33) * mm});
            skLineSegment(sketch, "E818", {"start": v(-0.48, -33) * mm, "end": v(-0.48, -33.04) * mm});
            skLineSegment(sketch, "E819", {"start": v(-0.48, -33.04) * mm, "end": v(-0.47, -33.09) * mm});
            skLineSegment(sketch, "E820", {"start": v(-0.47, -33.09) * mm, "end": v(-0.47, -33.13) * mm});
            skLineSegment(sketch, "E821", {"start": v(-0.47, -33.13) * mm, "end": v(-0.46, -33.18) * mm});
            skLineSegment(sketch, "E822", {"start": v(-0.46, -33.18) * mm, "end": v(-0.45, -33.24) * mm});
            skLineSegment(sketch, "E823", {"start": v(-0.45, -33.24) * mm, "end": v(-0.44, -33.3) * mm});
            skLineSegment(sketch, "E824", {"start": v(-0.44, -33.3) * mm, "end": v(-0.43, -33.36) * mm});
            skLineSegment(sketch, "E825", {"start": v(-0.43, -33.36) * mm, "end": v(-0.42, -33.42) * mm});
            skLineSegment(sketch, "E826", {"start": v(-0.42, -33.42) * mm, "end": v(-0.4, -33.5) * mm});
            skLineSegment(sketch, "E827", {"start": v(-0.4, -33.5) * mm, "end": v(-0.4, -33.57) * mm});
            skLineSegment(sketch, "E828", {"start": v(-0.4, -33.57) * mm, "end": v(-0.38, -33.64) * mm});
            skLineSegment(sketch, "E829", {"start": v(-0.38, -33.64) * mm, "end": v(-0.36, -33.72) * mm});
            skLineSegment(sketch, "E830", {"start": v(-0.36, -33.72) * mm, "end": v(-0.34, -33.8) * mm});
            skLineSegment(sketch, "E831", {"start": v(-0.34, -33.8) * mm, "end": v(-0.32, -33.9) * mm});
            skLineSegment(sketch, "E832", {"start": v(-0.32, -33.9) * mm, "end": v(-0.3, -33.99) * mm});
            skLineSegment(sketch, "E833", {"start": v(-0.3, -33.99) * mm, "end": v(-0.27, -34.08) * mm});
            skLineSegment(sketch, "E834", {"start": v(-0.27, -34.08) * mm, "end": v(-0.24, -34.18) * mm});
            skLineSegment(sketch, "E835", {"start": v(-0.24, -34.18) * mm, "end": v(-0.22, -34.28) * mm});
            skLineSegment(sketch, "E836", {"start": v(-0.22, -34.28) * mm, "end": v(-0.18, -34.39) * mm});
            skLineSegment(sketch, "E837", {"start": v(-0.18, -34.39) * mm, "end": v(-0.15, -34.5) * mm});
            skLineSegment(sketch, "E838", {"start": v(-0.15, -34.5) * mm, "end": v(-0.11, -34.6) * mm});
            skLineSegment(sketch, "E839", {"start": v(-0.11, -34.6) * mm, "end": v(-0.07, -34.72) * mm});
            skLineSegment(sketch, "E840", {"start": v(-0.07, -34.72) * mm, "end": v(-0.03, -34.84) * mm});
            skLineSegment(sketch, "E841", {"start": v(-0.03, -34.84) * mm, "end": v(0.01, -34.96) * mm});
            skLineSegment(sketch, "E842", {"start": v(0.01, -34.96) * mm, "end": v(0.06, -35.09) * mm});
            skLineSegment(sketch, "E843", {"start": v(0.06, -35.09) * mm, "end": v(0.1, -35.21) * mm});
            skLineSegment(sketch, "E844", {"start": v(0.1, -35.21) * mm, "end": v(0.16, -35.35) * mm});
            skLineSegment(sketch, "E845", {"start": v(0.16, -35.35) * mm, "end": v(0.21, -35.48) * mm});
            skLineSegment(sketch, "E846", {"start": v(0.21, -35.48) * mm, "end": v(0.27, -35.62) * mm});
            skLineSegment(sketch, "E847", {"start": v(0.27, -35.62) * mm, "end": v(0.33, -35.76) * mm});
            skLineSegment(sketch, "E848", {"start": v(0.33, -35.76) * mm, "end": v(0.4, -35.9) * mm});
            skLineSegment(sketch, "E849", {"start": v(0.4, -35.9) * mm, "end": v(0.46, -36.05) * mm});
            skLineSegment(sketch, "E850", {"start": v(0.46, -36.05) * mm, "end": v(0.53, -36.2) * mm});
            skLineSegment(sketch, "E851", {"start": v(0.53, -36.2) * mm, "end": v(0.6, -36.35) * mm});
            skLineSegment(sketch, "E852", {"start": v(0.6, -36.35) * mm, "end": v(0.69, -36.5) * mm});
            skLineSegment(sketch, "E853", {"start": v(0.69, -36.5) * mm, "end": v(0.77, -36.66) * mm});
            skLineSegment(sketch, "E854", {"start": v(0.77, -36.66) * mm, "end": v(0.85, -36.81) * mm});
            skLineSegment(sketch, "E855", {"start": v(0.85, -36.81) * mm, "end": v(0.94, -36.98) * mm});
            skLineSegment(sketch, "E856", {"start": v(0.94, -36.98) * mm, "end": v(1.03, -37.1) * mm});
            skLineSegment(sketch, "E857", {"start": v(1.03, -37.1) * mm, "end": v(2.54, -37.03) * mm});
            skLineSegment(sketch, "E858", {"start": v(2.54, -37.03) * mm, "end": v(2.62, -36.9) * mm});
            skLineSegment(sketch, "E859", {"start": v(2.62, -36.9) * mm, "end": v(2.7, -36.73) * mm});
            skLineSegment(sketch, "E860", {"start": v(2.7, -36.73) * mm, "end": v(2.76, -36.56) * mm});
            skLineSegment(sketch, "E861", {"start": v(2.76, -36.56) * mm, "end": v(2.82, -36.4) * mm});
            skLineSegment(sketch, "E862", {"start": v(2.82, -36.4) * mm, "end": v(2.89, -36.24) * mm});
            skLineSegment(sketch, "E863", {"start": v(2.89, -36.24) * mm, "end": v(2.95, -36.08) * mm});
            skLineSegment(sketch, "E864", {"start": v(2.95, -36.08) * mm, "end": v(3, -35.92) * mm});
            skLineSegment(sketch, "E865", {"start": v(3, -35.92) * mm, "end": v(3.05, -35.77) * mm});
            skLineSegment(sketch, "E866", {"start": v(3.05, -35.77) * mm, "end": v(3.1, -35.62) * mm});
            skLineSegment(sketch, "E867", {"start": v(3.1, -35.62) * mm, "end": v(3.15, -35.48) * mm});
            skLineSegment(sketch, "E868", {"start": v(3.15, -35.48) * mm, "end": v(3.2, -35.34) * mm});
            skLineSegment(sketch, "E869", {"start": v(3.2, -35.34) * mm, "end": v(3.24, -35.2) * mm});
            skLineSegment(sketch, "E870", {"start": v(3.24, -35.2) * mm, "end": v(3.28, -35.06) * mm});
            skLineSegment(sketch, "E871", {"start": v(3.28, -35.06) * mm, "end": v(3.32, -34.93) * mm});
            skLineSegment(sketch, "E872", {"start": v(3.32, -34.93) * mm, "end": v(3.35, -34.8) * mm});
            skLineSegment(sketch, "E873", {"start": v(3.35, -34.8) * mm, "end": v(3.38, -34.68) * mm});
            skLineSegment(sketch, "E874", {"start": v(3.38, -34.68) * mm, "end": v(3.41, -34.55) * mm});
            skLineSegment(sketch, "E875", {"start": v(3.41, -34.55) * mm, "end": v(3.44, -34.44) * mm});
            skLineSegment(sketch, "E876", {"start": v(3.44, -34.44) * mm, "end": v(3.46, -34.32) * mm});
            skLineSegment(sketch, "E877", {"start": v(3.46, -34.32) * mm, "end": v(3.49, -34.2) * mm});
            skLineSegment(sketch, "E878", {"start": v(3.49, -34.2) * mm, "end": v(3.5, -34.1) * mm});
            skLineSegment(sketch, "E879", {"start": v(3.5, -34.1) * mm, "end": v(3.53, -34) * mm});
            skLineSegment(sketch, "E880", {"start": v(3.53, -34) * mm, "end": v(3.55, -33.9) * mm});
            skLineSegment(sketch, "E881", {"start": v(3.55, -33.9) * mm, "end": v(3.56, -33.8) * mm});
            skLineSegment(sketch, "E882", {"start": v(3.56, -33.8) * mm, "end": v(3.58, -33.7) * mm});
            skLineSegment(sketch, "E883", {"start": v(3.58, -33.7) * mm, "end": v(3.59, -33.62) * mm});
            skLineSegment(sketch, "E884", {"start": v(3.59, -33.62) * mm, "end": v(3.6, -33.53) * mm});
            skLineSegment(sketch, "E885", {"start": v(3.6, -33.53) * mm, "end": v(3.6, -33.45) * mm});
            skLineSegment(sketch, "E886", {"start": v(3.6, -33.45) * mm, "end": v(3.62, -33.37) * mm});
            skLineSegment(sketch, "E887", {"start": v(3.62, -33.37) * mm, "end": v(3.63, -33.3) * mm});
            skLineSegment(sketch, "E888", {"start": v(3.63, -33.3) * mm, "end": v(3.63, -33.23) * mm});
            skLineSegment(sketch, "E889", {"start": v(3.63, -33.23) * mm, "end": v(3.64, -33.16) * mm});
            skLineSegment(sketch, "E890", {"start": v(3.64, -33.16) * mm, "end": v(3.64, -33.1) * mm});
            skLineSegment(sketch, "E891", {"start": v(3.64, -33.1) * mm, "end": v(3.64, -33.04) * mm});
            skLineSegment(sketch, "E892", {"start": v(3.64, -33.04) * mm, "end": v(3.65, -32.98) * mm});
            skLineSegment(sketch, "E893", {"start": v(3.65, -32.98) * mm, "end": v(3.65, -32.93) * mm});
            skLineSegment(sketch, "E894", {"start": v(3.65, -32.93) * mm, "end": v(3.65, -32.89) * mm});
            skLineSegment(sketch, "E895", {"start": v(3.65, -32.89) * mm, "end": v(3.65, -32.84) * mm});
            skLineSegment(sketch, "E896", {"start": v(3.65, -32.84) * mm, "end": v(3.65, -32.8) * mm});
            skLineSegment(sketch, "E897", {"start": v(3.65, -32.8) * mm, "end": v(3.65, -32.77) * mm});
            skLineSegment(sketch, "E898", {"start": v(3.65, -32.77) * mm, "end": v(3.65, -32.74) * mm});
            skLineSegment(sketch, "E899", {"start": v(3.65, -32.74) * mm, "end": v(3.65, -32.7) * mm});
            skLineSegment(sketch, "E900", {"start": v(3.65, -32.7) * mm, "end": v(3.65, -32.69) * mm});
            skLineSegment(sketch, "E901", {"start": v(3.65, -32.69) * mm, "end": v(3.64, -32.67) * mm});
            skLineSegment(sketch, "E902", {"start": v(3.64, -32.67) * mm, "end": v(3.64, -32.65) * mm});
            skLineSegment(sketch, "E903", {"start": v(3.64, -32.65) * mm, "end": v(3.64, -32.64) * mm});
            skLineSegment(sketch, "E904", {"start": v(3.64, -32.64) * mm, "end": v(3.64, -32.63) * mm});
            skLineSegment(sketch, "E905", {"start": v(3.64, -32.63) * mm, "end": v(3.6, -32.22) * mm});
            skLineSegment(sketch, "E906", {"start": v(3.6, -32.22) * mm, "end": v(5.85, -31.9) * mm});
            skLineSegment(sketch, "E907", {"start": v(5.85, -31.9) * mm, "end": v(5.92, -32.3) * mm});
            skLineSegment(sketch, "E908", {"start": v(5.92, -32.3) * mm, "end": v(5.93, -32.3) * mm});
            skLineSegment(sketch, "E909", {"start": v(5.93, -32.3) * mm, "end": v(5.93, -32.31) * mm});
            skLineSegment(sketch, "E910", {"start": v(5.93, -32.31) * mm, "end": v(5.93, -32.33) * mm});
            skLineSegment(sketch, "E911", {"start": v(5.93, -32.33) * mm, "end": v(5.94, -32.35) * mm});
            skLineSegment(sketch, "E912", {"start": v(5.94, -32.35) * mm, "end": v(5.94, -32.37) * mm});
            skLineSegment(sketch, "E913", {"start": v(5.94, -32.37) * mm, "end": v(5.95, -32.4) * mm});
            skLineSegment(sketch, "E914", {"start": v(5.95, -32.4) * mm, "end": v(5.96, -32.43) * mm});
            skLineSegment(sketch, "E915", {"start": v(5.96, -32.43) * mm, "end": v(5.97, -32.46) * mm});
            skLineSegment(sketch, "E916", {"start": v(5.97, -32.46) * mm, "end": v(5.98, -32.5) * mm});
            skLineSegment(sketch, "E917", {"start": v(5.98, -32.5) * mm, "end": v(6, -32.54) * mm});
            skLineSegment(sketch, "E918", {"start": v(6, -32.54) * mm, "end": v(6, -32.59) * mm});
            skLineSegment(sketch, "E919", {"start": v(6, -32.59) * mm, "end": v(6.02, -32.63) * mm});
            skLineSegment(sketch, "E920", {"start": v(6.02, -32.63) * mm, "end": v(6.04, -32.69) * mm});
            skLineSegment(sketch, "E921", {"start": v(6.04, -32.69) * mm, "end": v(6.06, -32.74) * mm});
            skLineSegment(sketch, "E922", {"start": v(6.06, -32.74) * mm, "end": v(6.08, -32.8) * mm});
            skLineSegment(sketch, "E923", {"start": v(6.08, -32.8) * mm, "end": v(6.1, -32.86) * mm});
            skLineSegment(sketch, "E924", {"start": v(6.1, -32.86) * mm, "end": v(6.13, -32.93) * mm});
            skLineSegment(sketch, "E925", {"start": v(6.13, -32.93) * mm, "end": v(6.16, -33) * mm});
            skLineSegment(sketch, "E926", {"start": v(6.16, -33) * mm, "end": v(6.2, -33.07) * mm});
            skLineSegment(sketch, "E927", {"start": v(6.2, -33.07) * mm, "end": v(6.23, -33.15) * mm});
            skLineSegment(sketch, "E928", {"start": v(6.23, -33.15) * mm, "end": v(6.26, -33.22) * mm});
            skLineSegment(sketch, "E929", {"start": v(6.26, -33.22) * mm, "end": v(6.3, -33.3) * mm});
            skLineSegment(sketch, "E930", {"start": v(6.3, -33.3) * mm, "end": v(6.34, -33.4) * mm});
            skLineSegment(sketch, "E931", {"start": v(6.34, -33.4) * mm, "end": v(6.38, -33.48) * mm});
            skLineSegment(sketch, "E932", {"start": v(6.38, -33.48) * mm, "end": v(6.43, -33.57) * mm});
            skLineSegment(sketch, "E933", {"start": v(6.43, -33.57) * mm, "end": v(6.48, -33.66) * mm});
            skLineSegment(sketch, "E934", {"start": v(6.48, -33.66) * mm, "end": v(6.53, -33.76) * mm});
            skLineSegment(sketch, "E935", {"start": v(6.53, -33.76) * mm, "end": v(6.58, -33.86) * mm});
            skLineSegment(sketch, "E936", {"start": v(6.58, -33.86) * mm, "end": v(6.64, -33.96) * mm});
            skLineSegment(sketch, "E937", {"start": v(6.64, -33.96) * mm, "end": v(6.7, -34.07) * mm});
            skLineSegment(sketch, "E938", {"start": v(6.7, -34.07) * mm, "end": v(6.76, -34.18) * mm});
            skLineSegment(sketch, "E939", {"start": v(6.76, -34.18) * mm, "end": v(6.83, -34.29) * mm});
            skLineSegment(sketch, "E940", {"start": v(6.83, -34.29) * mm, "end": v(6.9, -34.4) * mm});
            skLineSegment(sketch, "E941", {"start": v(6.9, -34.4) * mm, "end": v(6.97, -34.52) * mm});
            skLineSegment(sketch, "E942", {"start": v(6.97, -34.52) * mm, "end": v(7.05, -34.64) * mm});
            skLineSegment(sketch, "E943", {"start": v(7.05, -34.64) * mm, "end": v(7.13, -34.76) * mm});
            skLineSegment(sketch, "E944", {"start": v(7.13, -34.76) * mm, "end": v(7.21, -34.88) * mm});
            skLineSegment(sketch, "E945", {"start": v(7.21, -34.88) * mm, "end": v(7.3, -35) * mm});
            skLineSegment(sketch, "E946", {"start": v(7.3, -35) * mm, "end": v(7.4, -35.13) * mm});
            skLineSegment(sketch, "E947", {"start": v(7.4, -35.13) * mm, "end": v(7.49, -35.26) * mm});
            skLineSegment(sketch, "E948", {"start": v(7.49, -35.26) * mm, "end": v(7.59, -35.4) * mm});
            skLineSegment(sketch, "E949", {"start": v(7.59, -35.4) * mm, "end": v(7.69, -35.53) * mm});
            skLineSegment(sketch, "E950", {"start": v(7.69, -35.53) * mm, "end": v(7.8, -35.66) * mm});
            skLineSegment(sketch, "E951", {"start": v(7.8, -35.66) * mm, "end": v(7.9, -35.8) * mm});
            skLineSegment(sketch, "E952", {"start": v(7.9, -35.8) * mm, "end": v(8.02, -35.94) * mm});
            skLineSegment(sketch, "E953", {"start": v(8.02, -35.94) * mm, "end": v(8.14, -36.08) * mm});
            skLineSegment(sketch, "E954", {"start": v(8.14, -36.08) * mm, "end": v(8.25, -36.19) * mm});
            skLineSegment(sketch, "E955", {"start": v(8.25, -36.19) * mm, "end": v(9.72, -35.82) * mm});
            skLineSegment(sketch, "E956", {"start": v(9.72, -35.82) * mm, "end": v(9.77, -35.68) * mm});
            skLineSegment(sketch, "E957", {"start": v(9.77, -35.68) * mm, "end": v(9.8, -35.5) * mm});
            skLineSegment(sketch, "E958", {"start": v(9.8, -35.5) * mm, "end": v(9.84, -35.32) * mm});
            skLineSegment(sketch, "E959", {"start": v(9.84, -35.32) * mm, "end": v(9.87, -35.15) * mm});
            skLineSegment(sketch, "E960", {"start": v(9.87, -35.15) * mm, "end": v(9.9, -34.98) * mm});
            skLineSegment(sketch, "E961", {"start": v(9.9, -34.98) * mm, "end": v(9.93, -34.8) * mm});
            skLineSegment(sketch, "E962", {"start": v(9.93, -34.8) * mm, "end": v(9.95, -34.65) * mm});
            skLineSegment(sketch, "E963", {"start": v(9.95, -34.65) * mm, "end": v(9.98, -34.49) * mm});
            skLineSegment(sketch, "E964", {"start": v(9.98, -34.49) * mm, "end": v(10, -34.33) * mm});
            skLineSegment(sketch, "E965", {"start": v(10, -34.33) * mm, "end": v(10.01, -34.18) * mm});
            skLineSegment(sketch, "E966", {"start": v(10.01, -34.18) * mm, "end": v(10.03, -34.03) * mm});
            skLineSegment(sketch, "E967", {"start": v(10.03, -34.03) * mm, "end": v(10.04, -33.89) * mm});
            skLineSegment(sketch, "E968", {"start": v(10.04, -33.89) * mm, "end": v(10.06, -33.75) * mm});
            skLineSegment(sketch, "E969", {"start": v(10.06, -33.75) * mm, "end": v(10.07, -33.61) * mm});
            skLineSegment(sketch, "E970", {"start": v(10.07, -33.61) * mm, "end": v(10.07, -33.48) * mm});
            skLineSegment(sketch, "E971", {"start": v(10.07, -33.48) * mm, "end": v(10.08, -33.35) * mm});
            skLineSegment(sketch, "E972", {"start": v(10.08, -33.35) * mm, "end": v(10.09, -33.22) * mm});
            skLineSegment(sketch, "E973", {"start": v(10.09, -33.22) * mm, "end": v(10.1, -33.1) * mm});
            skLineSegment(sketch, "E974", {"start": v(10.1, -33.1) * mm, "end": v(10.1, -32.99) * mm});
            skLineSegment(sketch, "E975", {"start": v(10.1, -32.99) * mm, "end": v(10.1, -32.87) * mm});
            skLineSegment(sketch, "E976", {"start": v(10.1, -32.87) * mm, "end": v(10.1, -32.76) * mm});
            skLineSegment(sketch, "E977", {"start": v(10.1, -32.76) * mm, "end": v(10.1, -32.66) * mm});
            skLineSegment(sketch, "E978", {"start": v(10.1, -32.66) * mm, "end": v(10.1, -32.55) * mm});
            skLineSegment(sketch, "E979", {"start": v(10.1, -32.55) * mm, "end": v(10.09, -32.46) * mm});
            skLineSegment(sketch, "E980", {"start": v(10.09, -32.46) * mm, "end": v(10.08, -32.36) * mm});
            skLineSegment(sketch, "E981", {"start": v(10.08, -32.36) * mm, "end": v(10.08, -32.27) * mm});
            skLineSegment(sketch, "E982", {"start": v(10.08, -32.27) * mm, "end": v(10.07, -32.19) * mm});
            skLineSegment(sketch, "E983", {"start": v(10.07, -32.19) * mm, "end": v(10.07, -32.1) * mm});
            skLineSegment(sketch, "E984", {"start": v(10.07, -32.1) * mm, "end": v(10.06, -32.03) * mm});
            skLineSegment(sketch, "E985", {"start": v(10.06, -32.03) * mm, "end": v(10.05, -31.95) * mm});
            skLineSegment(sketch, "E986", {"start": v(10.05, -31.95) * mm, "end": v(10.04, -31.88) * mm});
            skLineSegment(sketch, "E987", {"start": v(10.04, -31.88) * mm, "end": v(10.04, -31.82) * mm});
            skLineSegment(sketch, "E988", {"start": v(10.04, -31.82) * mm, "end": v(10.03, -31.75) * mm});
            skLineSegment(sketch, "E989", {"start": v(10.03, -31.75) * mm, "end": v(10.02, -31.7) * mm});
            skLineSegment(sketch, "E990", {"start": v(10.02, -31.7) * mm, "end": v(10.01, -31.64) * mm});
            skLineSegment(sketch, "E991", {"start": v(10.01, -31.64) * mm, "end": v(10, -31.59) * mm});
            skLineSegment(sketch, "E992", {"start": v(10, -31.59) * mm, "end": v(10, -31.54) * mm});
            skLineSegment(sketch, "E993", {"start": v(10, -31.54) * mm, "end": v(9.99, -31.5) * mm});
            skLineSegment(sketch, "E994", {"start": v(9.99, -31.5) * mm, "end": v(9.98, -31.46) * mm});
            skLineSegment(sketch, "E995", {"start": v(9.98, -31.46) * mm, "end": v(9.97, -31.43) * mm});
            skLineSegment(sketch, "E996", {"start": v(9.97, -31.43) * mm, "end": v(9.96, -31.4) * mm});
            skLineSegment(sketch, "E997", {"start": v(9.96, -31.4) * mm, "end": v(9.96, -31.37) * mm});
            skLineSegment(sketch, "E998", {"start": v(9.96, -31.37) * mm, "end": v(9.95, -31.35) * mm});
            skLineSegment(sketch, "E999", {"start": v(9.95, -31.35) * mm, "end": v(9.95, -31.33) * mm});
            skLineSegment(sketch, "E1000", {"start": v(9.95, -31.33) * mm, "end": v(9.94, -31.31) * mm});
            skLineSegment(sketch, "E1001", {"start": v(9.94, -31.31) * mm, "end": v(9.94, -31.3) * mm});
            skLineSegment(sketch, "E1002", {"start": v(9.94, -31.3) * mm, "end": v(9.94, -31.3) * mm});
            skLineSegment(sketch, "E1003", {"start": v(9.94, -31.3) * mm, "end": v(9.81, -30.9) * mm});
            skLineSegment(sketch, "E1004", {"start": v(9.81, -30.9) * mm, "end": v(11.96, -30.14) * mm});
            skLineSegment(sketch, "E1005", {"start": v(11.96, -30.14) * mm, "end": v(12.11, -30.52) * mm});
            skLineSegment(sketch, "E1006", {"start": v(12.11, -30.52) * mm, "end": v(12.11, -30.52) * mm});
            skLineSegment(sketch, "E1007", {"start": v(12.11, -30.52) * mm, "end": v(12.12, -30.54) * mm});
            skLineSegment(sketch, "E1008", {"start": v(12.12, -30.54) * mm, "end": v(12.13, -30.55) * mm});
            skLineSegment(sketch, "E1009", {"start": v(12.13, -30.55) * mm, "end": v(12.13, -30.57) * mm});
            skLineSegment(sketch, "E1010", {"start": v(12.13, -30.57) * mm, "end": v(12.14, -30.59) * mm});
            skLineSegment(sketch, "E1011", {"start": v(12.14, -30.59) * mm, "end": v(12.16, -30.61) * mm});
            skLineSegment(sketch, "E1012", {"start": v(12.16, -30.61) * mm, "end": v(12.17, -30.64) * mm});
            skLineSegment(sketch, "E1013", {"start": v(12.17, -30.64) * mm, "end": v(12.19, -30.67) * mm});
            skLineSegment(sketch, "E1014", {"start": v(12.19, -30.67) * mm, "end": v(12.2, -30.7) * mm});
            skLineSegment(sketch, "E1015", {"start": v(12.2, -30.7) * mm, "end": v(12.23, -30.75) * mm});
            skLineSegment(sketch, "E1016", {"start": v(12.23, -30.75) * mm, "end": v(12.25, -30.79) * mm});
            skLineSegment(sketch, "E1017", {"start": v(12.25, -30.79) * mm, "end": v(12.27, -30.83) * mm});
            skLineSegment(sketch, "E1018", {"start": v(12.27, -30.83) * mm, "end": v(12.3, -30.88) * mm});
            skLineSegment(sketch, "E1019", {"start": v(12.3, -30.88) * mm, "end": v(12.33, -30.93) * mm});
            skLineSegment(sketch, "E1020", {"start": v(12.33, -30.93) * mm, "end": v(12.37, -30.98) * mm});
            skLineSegment(sketch, "E1021", {"start": v(12.37, -30.98) * mm, "end": v(12.4, -31.04) * mm});
            skLineSegment(sketch, "E1022", {"start": v(12.4, -31.04) * mm, "end": v(12.44, -31.1) * mm});
            skLineSegment(sketch, "E1023", {"start": v(12.44, -31.1) * mm, "end": v(12.48, -31.16) * mm});
            skLineSegment(sketch, "E1024", {"start": v(12.48, -31.16) * mm, "end": v(12.53, -31.23) * mm});
            skLineSegment(sketch, "E1025", {"start": v(12.53, -31.23) * mm, "end": v(12.57, -31.3) * mm});
            skLineSegment(sketch, "E1026", {"start": v(12.57, -31.3) * mm, "end": v(12.62, -31.36) * mm});
            skLineSegment(sketch, "E1027", {"start": v(12.62, -31.36) * mm, "end": v(12.68, -31.44) * mm});
            skLineSegment(sketch, "E1028", {"start": v(12.68, -31.44) * mm, "end": v(12.73, -31.51) * mm});
            skLineSegment(sketch, "E1029", {"start": v(12.73, -31.51) * mm, "end": v(12.8, -31.6) * mm});
            skLineSegment(sketch, "E1030", {"start": v(12.8, -31.6) * mm, "end": v(12.85, -31.67) * mm});
            skLineSegment(sketch, "E1031", {"start": v(12.85, -31.67) * mm, "end": v(12.92, -31.75) * mm});
            skLineSegment(sketch, "E1032", {"start": v(12.92, -31.75) * mm, "end": v(12.99, -31.84) * mm});
            skLineSegment(sketch, "E1033", {"start": v(12.99, -31.84) * mm, "end": v(13.06, -31.93) * mm});
            skLineSegment(sketch, "E1034", {"start": v(13.06, -31.93) * mm, "end": v(13.14, -32.02) * mm});
            skLineSegment(sketch, "E1035", {"start": v(13.14, -32.02) * mm, "end": v(13.22, -32.1) * mm});
            skLineSegment(sketch, "E1036", {"start": v(13.22, -32.1) * mm, "end": v(13.3, -32.2) * mm});
            skLineSegment(sketch, "E1037", {"start": v(13.3, -32.2) * mm, "end": v(13.39, -32.3) * mm});
            skLineSegment(sketch, "E1038", {"start": v(13.39, -32.3) * mm, "end": v(13.48, -32.4) * mm});
            skLineSegment(sketch, "E1039", {"start": v(13.48, -32.4) * mm, "end": v(13.57, -32.5) * mm});
            skLineSegment(sketch, "E1040", {"start": v(13.57, -32.5) * mm, "end": v(13.67, -32.6) * mm});
            skLineSegment(sketch, "E1041", {"start": v(13.67, -32.6) * mm, "end": v(13.77, -32.7) * mm});
            skLineSegment(sketch, "E1042", {"start": v(13.77, -32.7) * mm, "end": v(13.88, -32.8) * mm});
            skLineSegment(sketch, "E1043", {"start": v(13.88, -32.8) * mm, "end": v(14, -32.9) * mm});
            skLineSegment(sketch, "E1044", {"start": v(14, -32.9) * mm, "end": v(14.1, -33.02) * mm});
            skLineSegment(sketch, "E1045", {"start": v(14.1, -33.02) * mm, "end": v(14.22, -33.12) * mm});
            skLineSegment(sketch, "E1046", {"start": v(14.22, -33.12) * mm, "end": v(14.35, -33.23) * mm});
            skLineSegment(sketch, "E1047", {"start": v(14.35, -33.23) * mm, "end": v(14.47, -33.35) * mm});
            skLineSegment(sketch, "E1048", {"start": v(14.47, -33.35) * mm, "end": v(14.6, -33.46) * mm});
            skLineSegment(sketch, "E1049", {"start": v(14.6, -33.46) * mm, "end": v(14.74, -33.57) * mm});
            skLineSegment(sketch, "E1050", {"start": v(14.74, -33.57) * mm, "end": v(14.88, -33.69) * mm});
            skLineSegment(sketch, "E1051", {"start": v(14.88, -33.69) * mm, "end": v(15.02, -33.8) * mm});
            skLineSegment(sketch, "E1052", {"start": v(15.02, -33.8) * mm, "end": v(15.15, -33.88) * mm});
            skLineSegment(sketch, "E1053", {"start": v(15.15, -33.88) * mm, "end": v(16.52, -33.24) * mm});
            skLineSegment(sketch, "E1054", {"start": v(16.52, -33.24) * mm, "end": v(16.54, -33.08) * mm});
            skLineSegment(sketch, "E1055", {"start": v(16.54, -33.08) * mm, "end": v(16.54, -32.9) * mm});
            skLineSegment(sketch, "E1056", {"start": v(16.54, -32.9) * mm, "end": v(16.54, -32.72) * mm});
            skLineSegment(sketch, "E1057", {"start": v(16.54, -32.72) * mm, "end": v(16.54, -32.54) * mm});
            skLineSegment(sketch, "E1058", {"start": v(16.54, -32.54) * mm, "end": v(16.53, -32.37) * mm});
            skLineSegment(sketch, "E1059", {"start": v(16.53, -32.37) * mm, "end": v(16.53, -32.2) * mm});
            skLineSegment(sketch, "E1060", {"start": v(16.53, -32.2) * mm, "end": v(16.52, -32.04) * mm});
            skLineSegment(sketch, "E1061", {"start": v(16.52, -32.04) * mm, "end": v(16.51, -31.88) * mm});
            skLineSegment(sketch, "E1062", {"start": v(16.51, -31.88) * mm, "end": v(16.5, -31.72) * mm});
            skLineSegment(sketch, "E1063", {"start": v(16.5, -31.72) * mm, "end": v(16.49, -31.57) * mm});
            skLineSegment(sketch, "E1064", {"start": v(16.49, -31.57) * mm, "end": v(16.48, -31.42) * mm});
            skLineSegment(sketch, "E1065", {"start": v(16.48, -31.42) * mm, "end": v(16.46, -31.28) * mm});
            skLineSegment(sketch, "E1066", {"start": v(16.46, -31.28) * mm, "end": v(16.45, -31.14) * mm});
            skLineSegment(sketch, "E1067", {"start": v(16.45, -31.14) * mm, "end": v(16.43, -31) * mm});
            skLineSegment(sketch, "E1068", {"start": v(16.43, -31) * mm, "end": v(16.41, -30.87) * mm});
            skLineSegment(sketch, "E1069", {"start": v(16.41, -30.87) * mm, "end": v(16.4, -30.74) * mm});
            skLineSegment(sketch, "E1070", {"start": v(16.4, -30.74) * mm, "end": v(16.37, -30.62) * mm});
            skLineSegment(sketch, "E1071", {"start": v(16.37, -30.62) * mm, "end": v(16.36, -30.5) * mm});
            skLineSegment(sketch, "E1072", {"start": v(16.36, -30.5) * mm, "end": v(16.33, -30.38) * mm});
            skLineSegment(sketch, "E1073", {"start": v(16.33, -30.38) * mm, "end": v(16.31, -30.27) * mm});
            skLineSegment(sketch, "E1074", {"start": v(16.31, -30.27) * mm, "end": v(16.3, -30.16) * mm});
            skLineSegment(sketch, "E1075", {"start": v(16.3, -30.16) * mm, "end": v(16.27, -30.06) * mm});
            skLineSegment(sketch, "E1076", {"start": v(16.27, -30.06) * mm, "end": v(16.25, -29.96) * mm});
            skLineSegment(sketch, "E1077", {"start": v(16.25, -29.96) * mm, "end": v(16.23, -29.86) * mm});
            skLineSegment(sketch, "E1078", {"start": v(16.23, -29.86) * mm, "end": v(16.2, -29.77) * mm});
            skLineSegment(sketch, "E1079", {"start": v(16.2, -29.77) * mm, "end": v(16.18, -29.69) * mm});
            skLineSegment(sketch, "E1080", {"start": v(16.18, -29.69) * mm, "end": v(16.16, -29.6) * mm});
            skLineSegment(sketch, "E1081", {"start": v(16.16, -29.6) * mm, "end": v(16.14, -29.52) * mm});
            skLineSegment(sketch, "E1082", {"start": v(16.14, -29.52) * mm, "end": v(16.11, -29.45) * mm});
            skLineSegment(sketch, "E1083", {"start": v(16.11, -29.45) * mm, "end": v(16.1, -29.38) * mm});
            skLineSegment(sketch, "E1084", {"start": v(16.1, -29.38) * mm, "end": v(16.07, -29.3) * mm});
            skLineSegment(sketch, "E1085", {"start": v(16.07, -29.3) * mm, "end": v(16.05, -29.25) * mm});
            skLineSegment(sketch, "E1086", {"start": v(16.05, -29.25) * mm, "end": v(16.03, -29.19) * mm});
            skLineSegment(sketch, "E1087", {"start": v(16.03, -29.19) * mm, "end": v(16.01, -29.13) * mm});
            skLineSegment(sketch, "E1088", {"start": v(16.01, -29.13) * mm, "end": v(16, -29.08) * mm});
            skLineSegment(sketch, "E1089", {"start": v(16, -29.08) * mm, "end": v(15.97, -29.03) * mm});
            skLineSegment(sketch, "E1090", {"start": v(15.97, -29.03) * mm, "end": v(15.96, -28.99) * mm});
            skLineSegment(sketch, "E1091", {"start": v(15.96, -28.99) * mm, "end": v(15.94, -28.95) * mm});
            skLineSegment(sketch, "E1092", {"start": v(15.94, -28.95) * mm, "end": v(15.92, -28.91) * mm});
            skLineSegment(sketch, "E1093", {"start": v(15.92, -28.91) * mm, "end": v(15.91, -28.88) * mm});
            skLineSegment(sketch, "E1094", {"start": v(15.91, -28.88) * mm, "end": v(15.9, -28.85) * mm});
            skLineSegment(sketch, "E1095", {"start": v(15.9, -28.85) * mm, "end": v(15.89, -28.82) * mm});
            skLineSegment(sketch, "E1096", {"start": v(15.89, -28.82) * mm, "end": v(15.88, -28.8) * mm});
            skLineSegment(sketch, "E1097", {"start": v(15.88, -28.8) * mm, "end": v(15.87, -28.78) * mm});
            skLineSegment(sketch, "E1098", {"start": v(15.87, -28.78) * mm, "end": v(15.86, -28.77) * mm});
            skLineSegment(sketch, "E1099", {"start": v(15.86, -28.77) * mm, "end": v(15.86, -28.76) * mm});
            skLineSegment(sketch, "E1100", {"start": v(15.86, -28.76) * mm, "end": v(15.85, -28.75) * mm});
            skLineSegment(sketch, "E1101", {"start": v(15.85, -28.75) * mm, "end": v(15.65, -28.4) * mm});
            skLineSegment(sketch, "E1102", {"start": v(15.65, -28.4) * mm, "end": v(17.6, -27.22) * mm});
            skLineSegment(sketch, "E1103", {"start": v(17.6, -27.22) * mm, "end": v(17.83, -27.57) * mm});
            skLineSegment(sketch, "E1104", {"start": v(17.83, -27.57) * mm, "end": v(17.84, -27.57) * mm});
            skLineSegment(sketch, "E1105", {"start": v(17.84, -27.57) * mm, "end": v(17.84, -27.58) * mm});
            skLineSegment(sketch, "E1106", {"start": v(17.84, -27.58) * mm, "end": v(17.85, -27.6) * mm});
            skLineSegment(sketch, "E1107", {"start": v(17.85, -27.6) * mm, "end": v(17.86, -27.61) * mm});
            skLineSegment(sketch, "E1108", {"start": v(17.86, -27.61) * mm, "end": v(17.88, -27.63) * mm});
            skLineSegment(sketch, "E1109", {"start": v(17.88, -27.63) * mm, "end": v(17.9, -27.65) * mm});
            skLineSegment(sketch, "E1110", {"start": v(17.9, -27.65) * mm, "end": v(17.91, -27.68) * mm});
            skLineSegment(sketch, "E1111", {"start": v(17.91, -27.68) * mm, "end": v(17.94, -27.7) * mm});
            skLineSegment(sketch, "E1112", {"start": v(17.94, -27.7) * mm, "end": v(17.96, -27.74) * mm});
            skLineSegment(sketch, "E1113", {"start": v(17.96, -27.74) * mm, "end": v(17.99, -27.77) * mm});
            skLineSegment(sketch, "E1114", {"start": v(17.99, -27.77) * mm, "end": v(18.02, -27.8) * mm});
            skLineSegment(sketch, "E1115", {"start": v(18.02, -27.8) * mm, "end": v(18.05, -27.85) * mm});
            skLineSegment(sketch, "E1116", {"start": v(18.05, -27.85) * mm, "end": v(18.1, -27.89) * mm});
            skLineSegment(sketch, "E1117", {"start": v(18.1, -27.89) * mm, "end": v(18.13, -27.93) * mm});
            skLineSegment(sketch, "E1118", {"start": v(18.13, -27.93) * mm, "end": v(18.17, -27.98) * mm});
            skLineSegment(sketch, "E1119", {"start": v(18.17, -27.98) * mm, "end": v(18.22, -28.02) * mm});
            skLineSegment(sketch, "E1120", {"start": v(18.22, -28.02) * mm, "end": v(18.27, -28.08) * mm});
            skLineSegment(sketch, "E1121", {"start": v(18.27, -28.08) * mm, "end": v(18.32, -28.13) * mm});
            skLineSegment(sketch, "E1122", {"start": v(18.32, -28.13) * mm, "end": v(18.38, -28.18) * mm});
            skLineSegment(sketch, "E1123", {"start": v(18.38, -28.18) * mm, "end": v(18.44, -28.24) * mm});
            skLineSegment(sketch, "E1124", {"start": v(18.44, -28.24) * mm, "end": v(18.5, -28.3) * mm});
            skLineSegment(sketch, "E1125", {"start": v(18.5, -28.3) * mm, "end": v(18.57, -28.36) * mm});
            skLineSegment(sketch, "E1126", {"start": v(18.57, -28.36) * mm, "end": v(18.64, -28.42) * mm});
            skLineSegment(sketch, "E1127", {"start": v(18.64, -28.42) * mm, "end": v(18.7, -28.49) * mm});
            skLineSegment(sketch, "E1128", {"start": v(18.7, -28.49) * mm, "end": v(18.79, -28.56) * mm});
            skLineSegment(sketch, "E1129", {"start": v(18.79, -28.56) * mm, "end": v(18.87, -28.62) * mm});
            skLineSegment(sketch, "E1130", {"start": v(18.87, -28.62) * mm, "end": v(18.95, -28.7) * mm});
            skLineSegment(sketch, "E1131", {"start": v(18.95, -28.7) * mm, "end": v(19.04, -28.76) * mm});
            skLineSegment(sketch, "E1132", {"start": v(19.04, -28.76) * mm, "end": v(19.13, -28.84) * mm});
            skLineSegment(sketch, "E1133", {"start": v(19.13, -28.84) * mm, "end": v(19.23, -28.91) * mm});
            skLineSegment(sketch, "E1134", {"start": v(19.23, -28.91) * mm, "end": v(19.33, -28.99) * mm});
            skLineSegment(sketch, "E1135", {"start": v(19.33, -28.99) * mm, "end": v(19.43, -29.06) * mm});
            skLineSegment(sketch, "E1136", {"start": v(19.43, -29.06) * mm, "end": v(19.54, -29.14) * mm});
            skLineSegment(sketch, "E1137", {"start": v(19.54, -29.14) * mm, "end": v(19.65, -29.22) * mm});
            skLineSegment(sketch, "E1138", {"start": v(19.65, -29.22) * mm, "end": v(19.77, -29.3) * mm});
            skLineSegment(sketch, "E1139", {"start": v(19.77, -29.3) * mm, "end": v(19.89, -29.38) * mm});
            skLineSegment(sketch, "E1140", {"start": v(19.89, -29.38) * mm, "end": v(20.01, -29.46) * mm});
            skLineSegment(sketch, "E1141", {"start": v(20.01, -29.46) * mm, "end": v(20.14, -29.55) * mm});
            skLineSegment(sketch, "E1142", {"start": v(20.14, -29.55) * mm, "end": v(20.27, -29.63) * mm});
            skLineSegment(sketch, "E1143", {"start": v(20.27, -29.63) * mm, "end": v(20.41, -29.71) * mm});
            skLineSegment(sketch, "E1144", {"start": v(20.41, -29.71) * mm, "end": v(20.55, -29.8) * mm});
            skLineSegment(sketch, "E1145", {"start": v(20.55, -29.8) * mm, "end": v(20.7, -29.88) * mm});
            skLineSegment(sketch, "E1146", {"start": v(20.7, -29.88) * mm, "end": v(20.85, -29.97) * mm});
            skLineSegment(sketch, "E1147", {"start": v(20.85, -29.97) * mm, "end": v(21, -30.05) * mm});
            skLineSegment(sketch, "E1148", {"start": v(21, -30.05) * mm, "end": v(21.16, -30.14) * mm});
            skLineSegment(sketch, "E1149", {"start": v(21.16, -30.14) * mm, "end": v(21.32, -30.22) * mm});
            skLineSegment(sketch, "E1150", {"start": v(21.32, -30.22) * mm, "end": v(21.47, -30.28) * mm});
            skLineSegment(sketch, "E1151", {"start": v(21.47, -30.28) * mm, "end": v(22.68, -29.38) * mm});
            skLineSegment(sketch, "E1152", {"start": v(22.68, -29.38) * mm, "end": v(22.67, -29.22) * mm});
            skLineSegment(sketch, "E1153", {"start": v(22.67, -29.22) * mm, "end": v(22.64, -29.04) * mm});
            skLineSegment(sketch, "E1154", {"start": v(22.64, -29.04) * mm, "end": v(22.6, -28.87) * mm});
            skLineSegment(sketch, "E1155", {"start": v(22.6, -28.87) * mm, "end": v(22.57, -28.7) * mm});
            skLineSegment(sketch, "E1156", {"start": v(22.57, -28.7) * mm, "end": v(22.53, -28.52) * mm});
            skLineSegment(sketch, "E1157", {"start": v(22.53, -28.52) * mm, "end": v(22.5, -28.36) * mm});
            skLineSegment(sketch, "E1158", {"start": v(22.5, -28.36) * mm, "end": v(22.45, -28.2) * mm});
            skLineSegment(sketch, "E1159", {"start": v(22.45, -28.2) * mm, "end": v(22.41, -28.05) * mm});
            skLineSegment(sketch, "E1160", {"start": v(22.41, -28.05) * mm, "end": v(22.37, -27.9) * mm});
            skLineSegment(sketch, "E1161", {"start": v(22.37, -27.9) * mm, "end": v(22.33, -27.75) * mm});
            skLineSegment(sketch, "E1162", {"start": v(22.33, -27.75) * mm, "end": v(22.3, -27.6) * mm});
            skLineSegment(sketch, "E1163", {"start": v(22.3, -27.6) * mm, "end": v(22.25, -27.47) * mm});
            skLineSegment(sketch, "E1164", {"start": v(22.25, -27.47) * mm, "end": v(22.2, -27.33) * mm});
            skLineSegment(sketch, "E1165", {"start": v(22.2, -27.33) * mm, "end": v(22.16, -27.2) * mm});
            skLineSegment(sketch, "E1166", {"start": v(22.16, -27.2) * mm, "end": v(22.12, -27.08) * mm});
            skLineSegment(sketch, "E1167", {"start": v(22.12, -27.08) * mm, "end": v(22.08, -26.95) * mm});
            skLineSegment(sketch, "E1168", {"start": v(22.08, -26.95) * mm, "end": v(22.03, -26.84) * mm});
            skLineSegment(sketch, "E1169", {"start": v(22.03, -26.84) * mm, "end": v(22, -26.72) * mm});
            skLineSegment(sketch, "E1170", {"start": v(22, -26.72) * mm, "end": v(21.95, -26.61) * mm});
            skLineSegment(sketch, "E1171", {"start": v(21.95, -26.61) * mm, "end": v(21.9, -26.5) * mm});
            skLineSegment(sketch, "E1172", {"start": v(21.9, -26.5) * mm, "end": v(21.86, -26.4) * mm});
            skLineSegment(sketch, "E1173", {"start": v(21.86, -26.4) * mm, "end": v(21.82, -26.3) * mm});
            skLineSegment(sketch, "E1174", {"start": v(21.82, -26.3) * mm, "end": v(21.78, -26.21) * mm});
            skLineSegment(sketch, "E1175", {"start": v(21.78, -26.21) * mm, "end": v(21.74, -26.13) * mm});
            skLineSegment(sketch, "E1176", {"start": v(21.74, -26.13) * mm, "end": v(21.7, -26.04) * mm});
            skLineSegment(sketch, "E1177", {"start": v(21.7, -26.04) * mm, "end": v(21.66, -25.96) * mm});
            skLineSegment(sketch, "E1178", {"start": v(21.66, -25.96) * mm, "end": v(21.62, -25.88) * mm});
            skLineSegment(sketch, "E1179", {"start": v(21.62, -25.88) * mm, "end": v(21.59, -25.8) * mm});
            skLineSegment(sketch, "E1180", {"start": v(21.59, -25.8) * mm, "end": v(21.55, -25.74) * mm});
            skLineSegment(sketch, "E1181", {"start": v(21.55, -25.74) * mm, "end": v(21.51, -25.67) * mm});
            skLineSegment(sketch, "E1182", {"start": v(21.51, -25.67) * mm, "end": v(21.48, -25.61) * mm});
            skLineSegment(sketch, "E1183", {"start": v(21.48, -25.61) * mm, "end": v(21.45, -25.55) * mm});
            skLineSegment(sketch, "E1184", {"start": v(21.45, -25.55) * mm, "end": v(21.42, -25.5) * mm});
            skLineSegment(sketch, "E1185", {"start": v(21.42, -25.5) * mm, "end": v(21.39, -25.45) * mm});
            skLineSegment(sketch, "E1186", {"start": v(21.39, -25.45) * mm, "end": v(21.36, -25.4) * mm});
            skLineSegment(sketch, "E1187", {"start": v(21.36, -25.4) * mm, "end": v(21.33, -25.36) * mm});
            skLineSegment(sketch, "E1188", {"start": v(21.33, -25.36) * mm, "end": v(21.3, -25.32) * mm});
            skLineSegment(sketch, "E1189", {"start": v(21.3, -25.32) * mm, "end": v(21.28, -25.28) * mm});
            skLineSegment(sketch, "E1190", {"start": v(21.28, -25.28) * mm, "end": v(21.26, -25.25) * mm});
            skLineSegment(sketch, "E1191", {"start": v(21.26, -25.25) * mm, "end": v(21.24, -25.22) * mm});
            skLineSegment(sketch, "E1192", {"start": v(21.24, -25.22) * mm, "end": v(21.22, -25.2) * mm});
            skLineSegment(sketch, "E1193", {"start": v(21.22, -25.2) * mm, "end": v(21.2, -25.17) * mm});
            skLineSegment(sketch, "E1194", {"start": v(21.2, -25.17) * mm, "end": v(21.2, -25.15) * mm});
            skLineSegment(sketch, "E1195", {"start": v(21.2, -25.15) * mm, "end": v(21.18, -25.14) * mm});
            skLineSegment(sketch, "E1196", {"start": v(21.18, -25.14) * mm, "end": v(21.17, -25.12) * mm});
            skLineSegment(sketch, "E1197", {"start": v(21.17, -25.12) * mm, "end": v(21.16, -25.11) * mm});
            skLineSegment(sketch, "E1198", {"start": v(21.16, -25.11) * mm, "end": v(21.16, -25.1) * mm});
            skLineSegment(sketch, "E1199", {"start": v(21.16, -25.1) * mm, "end": v(20.9, -24.8) * mm});
            skLineSegment(sketch, "E1200", {"start": v(20.9, -24.8) * mm, "end": v(22.58, -23.27) * mm});
            skLineSegment(sketch, "E1201", {"start": v(22.58, -23.27) * mm, "end": v(22.87, -23.56) * mm});
            skLineSegment(sketch, "E1202", {"start": v(22.87, -23.56) * mm, "end": v(22.87, -23.56) * mm});
            skLineSegment(sketch, "E1203", {"start": v(22.87, -23.56) * mm, "end": v(22.88, -23.57) * mm});
            skLineSegment(sketch, "E1204", {"start": v(22.88, -23.57) * mm, "end": v(22.9, -23.58) * mm});
            skLineSegment(sketch, "E1205", {"start": v(22.9, -23.58) * mm, "end": v(22.9, -23.6) * mm});
            skLineSegment(sketch, "E1206", {"start": v(22.9, -23.6) * mm, "end": v(22.93, -23.61) * mm});
            skLineSegment(sketch, "E1207", {"start": v(22.93, -23.61) * mm, "end": v(22.95, -23.63) * mm});
            skLineSegment(sketch, "E1208", {"start": v(22.95, -23.63) * mm, "end": v(22.97, -23.65) * mm});
            skLineSegment(sketch, "E1209", {"start": v(22.97, -23.65) * mm, "end": v(23, -23.68) * mm});
            skLineSegment(sketch, "E1210", {"start": v(23, -23.68) * mm, "end": v(23.03, -23.7) * mm});
            skLineSegment(sketch, "E1211", {"start": v(23.03, -23.7) * mm, "end": v(23.06, -23.73) * mm});
            skLineSegment(sketch, "E1212", {"start": v(23.06, -23.73) * mm, "end": v(23.1, -23.76) * mm});
            skLineSegment(sketch, "E1213", {"start": v(23.1, -23.76) * mm, "end": v(23.14, -23.79) * mm});
            skLineSegment(sketch, "E1214", {"start": v(23.14, -23.79) * mm, "end": v(23.18, -23.82) * mm});
            skLineSegment(sketch, "E1215", {"start": v(23.18, -23.82) * mm, "end": v(23.23, -23.86) * mm});
            skLineSegment(sketch, "E1216", {"start": v(23.23, -23.86) * mm, "end": v(23.28, -23.9) * mm});
            skLineSegment(sketch, "E1217", {"start": v(23.28, -23.9) * mm, "end": v(23.34, -23.93) * mm});
            skLineSegment(sketch, "E1218", {"start": v(23.34, -23.93) * mm, "end": v(23.4, -23.97) * mm});
            skLineSegment(sketch, "E1219", {"start": v(23.4, -23.97) * mm, "end": v(23.46, -24.01) * mm});
            skLineSegment(sketch, "E1220", {"start": v(23.46, -24.01) * mm, "end": v(23.52, -24.06) * mm});
            skLineSegment(sketch, "E1221", {"start": v(23.52, -24.06) * mm, "end": v(23.6, -24.1) * mm});
            skLineSegment(sketch, "E1222", {"start": v(23.6, -24.1) * mm, "end": v(23.66, -24.15) * mm});
            skLineSegment(sketch, "E1223", {"start": v(23.66, -24.15) * mm, "end": v(23.74, -24.2) * mm});
            skLineSegment(sketch, "E1224", {"start": v(23.74, -24.2) * mm, "end": v(23.82, -24.24) * mm});
            skLineSegment(sketch, "E1225", {"start": v(23.82, -24.24) * mm, "end": v(23.9, -24.3) * mm});
            skLineSegment(sketch, "E1226", {"start": v(23.9, -24.3) * mm, "end": v(24, -24.34) * mm});
            skLineSegment(sketch, "E1227", {"start": v(24, -24.34) * mm, "end": v(24.09, -24.4) * mm});
            skLineSegment(sketch, "E1228", {"start": v(24.09, -24.4) * mm, "end": v(24.19, -24.44) * mm});
            skLineSegment(sketch, "E1229", {"start": v(24.19, -24.44) * mm, "end": v(24.29, -24.5) * mm});
            skLineSegment(sketch, "E1230", {"start": v(24.29, -24.5) * mm, "end": v(24.4, -24.55) * mm});
            skLineSegment(sketch, "E1231", {"start": v(24.4, -24.55) * mm, "end": v(24.5, -24.6) * mm});
            skLineSegment(sketch, "E1232", {"start": v(24.5, -24.6) * mm, "end": v(24.61, -24.66) * mm});
            skLineSegment(sketch, "E1233", {"start": v(24.61, -24.66) * mm, "end": v(24.73, -24.71) * mm});
            skLineSegment(sketch, "E1234", {"start": v(24.73, -24.71) * mm, "end": v(24.85, -24.77) * mm});
            skLineSegment(sketch, "E1235", {"start": v(24.85, -24.77) * mm, "end": v(24.98, -24.83) * mm});
            skLineSegment(sketch, "E1236", {"start": v(24.98, -24.83) * mm, "end": v(25.1, -24.88) * mm});
            skLineSegment(sketch, "E1237", {"start": v(25.1, -24.88) * mm, "end": v(25.24, -24.94) * mm});
            skLineSegment(sketch, "E1238", {"start": v(25.24, -24.94) * mm, "end": v(25.38, -25) * mm});
            skLineSegment(sketch, "E1239", {"start": v(25.38, -25) * mm, "end": v(25.52, -25.05) * mm});
            skLineSegment(sketch, "E1240", {"start": v(25.52, -25.05) * mm, "end": v(25.67, -25.1) * mm});
            skLineSegment(sketch, "E1241", {"start": v(25.67, -25.1) * mm, "end": v(25.82, -25.16) * mm});
            skLineSegment(sketch, "E1242", {"start": v(25.82, -25.16) * mm, "end": v(25.97, -25.21) * mm});
            skLineSegment(sketch, "E1243", {"start": v(25.97, -25.21) * mm, "end": v(26.13, -25.27) * mm});
            skLineSegment(sketch, "E1244", {"start": v(26.13, -25.27) * mm, "end": v(26.3, -25.32) * mm});
            skLineSegment(sketch, "E1245", {"start": v(26.3, -25.32) * mm, "end": v(26.46, -25.38) * mm});
            skLineSegment(sketch, "E1246", {"start": v(26.46, -25.38) * mm, "end": v(26.63, -25.43) * mm});
            skLineSegment(sketch, "E1247", {"start": v(26.63, -25.43) * mm, "end": v(26.81, -25.48) * mm});
            skLineSegment(sketch, "E1248", {"start": v(26.81, -25.48) * mm, "end": v(26.96, -25.5) * mm});
            skLineSegment(sketch, "E1249", {"start": v(26.96, -25.5) * mm, "end": v(27.98, -24.39) * mm});
            skLineSegment(sketch, "E1250", {"start": v(27.98, -24.39) * mm, "end": v(27.94, -24.24) * mm});
            skLineSegment(sketch, "E1251", {"start": v(27.94, -24.24) * mm, "end": v(27.87, -24.07) * mm});
            skLineSegment(sketch, "E1252", {"start": v(27.87, -24.07) * mm, "end": v(27.8, -23.9) * mm});
            skLineSegment(sketch, "E1253", {"start": v(27.8, -23.9) * mm, "end": v(27.73, -23.74) * mm});
            skLineSegment(sketch, "E1254", {"start": v(27.73, -23.74) * mm, "end": v(27.66, -23.58) * mm});
            skLineSegment(sketch, "E1255", {"start": v(27.66, -23.58) * mm, "end": v(27.6, -23.43) * mm});
            skLineSegment(sketch, "E1256", {"start": v(27.6, -23.43) * mm, "end": v(27.52, -23.28) * mm});
            skLineSegment(sketch, "E1257", {"start": v(27.52, -23.28) * mm, "end": v(27.45, -23.13) * mm});
            skLineSegment(sketch, "E1258", {"start": v(27.45, -23.13) * mm, "end": v(27.39, -23) * mm});
            skLineSegment(sketch, "E1259", {"start": v(27.39, -23) * mm, "end": v(27.32, -22.86) * mm});
            skLineSegment(sketch, "E1260", {"start": v(27.32, -22.86) * mm, "end": v(27.25, -22.73) * mm});
            skLineSegment(sketch, "E1261", {"start": v(27.25, -22.73) * mm, "end": v(27.18, -22.6) * mm});
            skLineSegment(sketch, "E1262", {"start": v(27.18, -22.6) * mm, "end": v(27.11, -22.47) * mm});
            skLineSegment(sketch, "E1263", {"start": v(27.11, -22.47) * mm, "end": v(27.04, -22.35) * mm});
            skLineSegment(sketch, "E1264", {"start": v(27.04, -22.35) * mm, "end": v(26.98, -22.24) * mm});
            skLineSegment(sketch, "E1265", {"start": v(26.98, -22.24) * mm, "end": v(26.91, -22.13) * mm});
            skLineSegment(sketch, "E1266", {"start": v(26.91, -22.13) * mm, "end": v(26.85, -22.02) * mm});
            skLineSegment(sketch, "E1267", {"start": v(26.85, -22.02) * mm, "end": v(26.78, -21.92) * mm});
            skLineSegment(sketch, "E1268", {"start": v(26.78, -21.92) * mm, "end": v(26.72, -21.82) * mm});
            skLineSegment(sketch, "E1269", {"start": v(26.72, -21.82) * mm, "end": v(26.66, -21.72) * mm});
            skLineSegment(sketch, "E1270", {"start": v(26.66, -21.72) * mm, "end": v(26.6, -21.63) * mm});
            skLineSegment(sketch, "E1271", {"start": v(26.6, -21.63) * mm, "end": v(26.53, -21.55) * mm});
            skLineSegment(sketch, "E1272", {"start": v(26.53, -21.55) * mm, "end": v(26.48, -21.46) * mm});
            skLineSegment(sketch, "E1273", {"start": v(26.48, -21.46) * mm, "end": v(26.42, -21.38) * mm});
            skLineSegment(sketch, "E1274", {"start": v(26.42, -21.38) * mm, "end": v(26.36, -21.3) * mm});
            skLineSegment(sketch, "E1275", {"start": v(26.36, -21.3) * mm, "end": v(26.3, -21.23) * mm});
            skLineSegment(sketch, "E1276", {"start": v(26.3, -21.23) * mm, "end": v(26.26, -21.17) * mm});
            skLineSegment(sketch, "E1277", {"start": v(26.26, -21.17) * mm, "end": v(26.2, -21.1) * mm});
            skLineSegment(sketch, "E1278", {"start": v(26.2, -21.1) * mm, "end": v(26.16, -21.04) * mm});
            skLineSegment(sketch, "E1279", {"start": v(26.16, -21.04) * mm, "end": v(26.1, -20.98) * mm});
            skLineSegment(sketch, "E1280", {"start": v(26.1, -20.98) * mm, "end": v(26.06, -20.93) * mm});
            skLineSegment(sketch, "E1281", {"start": v(26.06, -20.93) * mm, "end": v(26.02, -20.88) * mm});
            skLineSegment(sketch, "E1282", {"start": v(26.02, -20.88) * mm, "end": v(25.98, -20.83) * mm});
            skLineSegment(sketch, "E1283", {"start": v(25.98, -20.83) * mm, "end": v(25.94, -20.79) * mm});
            skLineSegment(sketch, "E1284", {"start": v(25.94, -20.79) * mm, "end": v(25.9, -20.75) * mm});
            skLineSegment(sketch, "E1285", {"start": v(25.9, -20.75) * mm, "end": v(25.87, -20.7) * mm});
            skLineSegment(sketch, "E1286", {"start": v(25.87, -20.7) * mm, "end": v(25.83, -20.67) * mm});
            skLineSegment(sketch, "E1287", {"start": v(25.83, -20.67) * mm, "end": v(25.8, -20.64) * mm});
            skLineSegment(sketch, "E1288", {"start": v(25.8, -20.64) * mm, "end": v(25.78, -20.62) * mm});
            skLineSegment(sketch, "E1289", {"start": v(25.78, -20.62) * mm, "end": v(25.75, -20.6) * mm});
            skLineSegment(sketch, "E1290", {"start": v(25.75, -20.6) * mm, "end": v(25.73, -20.57) * mm});
            skLineSegment(sketch, "E1291", {"start": v(25.73, -20.57) * mm, "end": v(25.7, -20.55) * mm});
            skLineSegment(sketch, "E1292", {"start": v(25.7, -20.55) * mm, "end": v(25.69, -20.53) * mm});
            skLineSegment(sketch, "E1293", {"start": v(25.69, -20.53) * mm, "end": v(25.67, -20.52) * mm});
            skLineSegment(sketch, "E1294", {"start": v(25.67, -20.52) * mm, "end": v(25.66, -20.51) * mm});
            skLineSegment(sketch, "E1295", {"start": v(25.66, -20.51) * mm, "end": v(25.65, -20.5) * mm});
            skLineSegment(sketch, "E1296", {"start": v(25.65, -20.5) * mm, "end": v(25.65, -20.5) * mm});
            skLineSegment(sketch, "E1297", {"start": v(25.65, -20.5) * mm, "end": v(25.33, -20.24) * mm});
            skLineSegment(sketch, "E1298", {"start": v(25.33, -20.24) * mm, "end": v(26.69, -18.41) * mm});
            skLineSegment(sketch, "E1299", {"start": v(26.69, -18.41) * mm, "end": v(27.02, -18.65) * mm});
            skLineSegment(sketch, "E1300", {"start": v(27.02, -18.65) * mm, "end": v(27.03, -18.65) * mm});
            skLineSegment(sketch, "E1301", {"start": v(27.03, -18.65) * mm, "end": v(27.04, -18.66) * mm});
            skLineSegment(sketch, "E1302", {"start": v(27.04, -18.66) * mm, "end": v(27.05, -18.66) * mm});
            skLineSegment(sketch, "E1303", {"start": v(27.05, -18.66) * mm, "end": v(27.07, -18.68) * mm});
            skLineSegment(sketch, "E1304", {"start": v(27.07, -18.68) * mm, "end": v(27.1, -18.69) * mm});
            skLineSegment(sketch, "E1305", {"start": v(27.1, -18.69) * mm, "end": v(27.12, -18.7) * mm});
            skLineSegment(sketch, "E1306", {"start": v(27.12, -18.7) * mm, "end": v(27.14, -18.72) * mm});
            skLineSegment(sketch, "E1307", {"start": v(27.14, -18.72) * mm, "end": v(27.17, -18.73) * mm});
            skLineSegment(sketch, "E1308", {"start": v(27.17, -18.73) * mm, "end": v(27.2, -18.75) * mm});
            skLineSegment(sketch, "E1309", {"start": v(27.2, -18.75) * mm, "end": v(27.25, -18.77) * mm});
            skLineSegment(sketch, "E1310", {"start": v(27.25, -18.77) * mm, "end": v(27.29, -18.8) * mm});
            skLineSegment(sketch, "E1311", {"start": v(27.29, -18.8) * mm, "end": v(27.34, -18.82) * mm});
            skLineSegment(sketch, "E1312", {"start": v(27.34, -18.82) * mm, "end": v(27.38, -18.84) * mm});
            skLineSegment(sketch, "E1313", {"start": v(27.38, -18.84) * mm, "end": v(27.44, -18.87) * mm});
            skLineSegment(sketch, "E1314", {"start": v(27.44, -18.87) * mm, "end": v(27.5, -18.9) * mm});
            skLineSegment(sketch, "E1315", {"start": v(27.5, -18.9) * mm, "end": v(27.56, -18.92) * mm});
            skLineSegment(sketch, "E1316", {"start": v(27.56, -18.92) * mm, "end": v(27.62, -18.95) * mm});
            skLineSegment(sketch, "E1317", {"start": v(27.62, -18.95) * mm, "end": v(27.7, -18.98) * mm});
            skLineSegment(sketch, "E1318", {"start": v(27.7, -18.98) * mm, "end": v(27.76, -19) * mm});
            skLineSegment(sketch, "E1319", {"start": v(27.76, -19) * mm, "end": v(27.84, -19.04) * mm});
            skLineSegment(sketch, "E1320", {"start": v(27.84, -19.04) * mm, "end": v(27.92, -19.07) * mm});
            skLineSegment(sketch, "E1321", {"start": v(27.92, -19.07) * mm, "end": v(28, -19.1) * mm});
            skLineSegment(sketch, "E1322", {"start": v(28, -19.1) * mm, "end": v(28.1, -19.13) * mm});
            skLineSegment(sketch, "E1323", {"start": v(28.1, -19.13) * mm, "end": v(28.19, -19.16) * mm});
            skLineSegment(sketch, "E1324", {"start": v(28.19, -19.16) * mm, "end": v(28.28, -19.2) * mm});
            skLineSegment(sketch, "E1325", {"start": v(28.28, -19.2) * mm, "end": v(28.38, -19.22) * mm});
            skLineSegment(sketch, "E1326", {"start": v(28.38, -19.22) * mm, "end": v(28.49, -19.26) * mm});
            skLineSegment(sketch, "E1327", {"start": v(28.49, -19.26) * mm, "end": v(28.6, -19.29) * mm});
            skLineSegment(sketch, "E1328", {"start": v(28.6, -19.29) * mm, "end": v(28.71, -19.32) * mm});
            skLineSegment(sketch, "E1329", {"start": v(28.71, -19.32) * mm, "end": v(28.83, -19.35) * mm});
            skLineSegment(sketch, "E1330", {"start": v(28.83, -19.35) * mm, "end": v(28.95, -19.38) * mm});
            skLineSegment(sketch, "E1331", {"start": v(28.95, -19.38) * mm, "end": v(29.08, -19.42) * mm});
            skLineSegment(sketch, "E1332", {"start": v(29.08, -19.42) * mm, "end": v(29.2, -19.45) * mm});
            skLineSegment(sketch, "E1333", {"start": v(29.2, -19.45) * mm, "end": v(29.34, -19.48) * mm});
            skLineSegment(sketch, "E1334", {"start": v(29.34, -19.48) * mm, "end": v(29.48, -19.5) * mm});
            skLineSegment(sketch, "E1335", {"start": v(29.48, -19.5) * mm, "end": v(29.62, -19.53) * mm});
            skLineSegment(sketch, "E1336", {"start": v(29.62, -19.53) * mm, "end": v(29.77, -19.56) * mm});
            skLineSegment(sketch, "E1337", {"start": v(29.77, -19.56) * mm, "end": v(29.92, -19.59) * mm});
            skLineSegment(sketch, "E1338", {"start": v(29.92, -19.59) * mm, "end": v(30.07, -19.61) * mm});
            skLineSegment(sketch, "E1339", {"start": v(30.07, -19.61) * mm, "end": v(30.23, -19.64) * mm});
            skLineSegment(sketch, "E1340", {"start": v(30.23, -19.64) * mm, "end": v(30.4, -19.66) * mm});
            skLineSegment(sketch, "E1341", {"start": v(30.4, -19.66) * mm, "end": v(30.56, -19.69) * mm});
            skLineSegment(sketch, "E1342", {"start": v(30.56, -19.69) * mm, "end": v(30.73, -19.7) * mm});
            skLineSegment(sketch, "E1343", {"start": v(30.73, -19.7) * mm, "end": v(30.9, -19.73) * mm});
            skLineSegment(sketch, "E1344", {"start": v(30.9, -19.73) * mm, "end": v(31.08, -19.74) * mm});
            skLineSegment(sketch, "E1345", {"start": v(31.08, -19.74) * mm, "end": v(31.27, -19.76) * mm});
            skLineSegment(sketch, "E1346", {"start": v(31.27, -19.76) * mm, "end": v(31.42, -19.76) * mm});
            skLineSegment(sketch, "E1347", {"start": v(31.42, -19.76) * mm, "end": v(32.2, -18.46) * mm});
            skLineSegment(sketch, "E1348", {"start": v(32.2, -18.46) * mm, "end": v(32.13, -18.32) * mm});
            skLineSegment(sketch, "E1349", {"start": v(32.13, -18.32) * mm, "end": v(32.03, -18.17) * mm});
            skLineSegment(sketch, "E1350", {"start": v(32.03, -18.17) * mm, "end": v(31.93, -18.02) * mm});
            skLineSegment(sketch, "E1351", {"start": v(31.93, -18.02) * mm, "end": v(31.83, -17.87) * mm});
            skLineSegment(sketch, "E1352", {"start": v(31.83, -17.87) * mm, "end": v(31.73, -17.73) * mm});
            skLineSegment(sketch, "E1353", {"start": v(31.73, -17.73) * mm, "end": v(31.63, -17.6) * mm});
            skLineSegment(sketch, "E1354", {"start": v(31.63, -17.6) * mm, "end": v(31.54, -17.46) * mm});
            skLineSegment(sketch, "E1355", {"start": v(31.54, -17.46) * mm, "end": v(31.44, -17.33) * mm});
            skLineSegment(sketch, "E1356", {"start": v(31.44, -17.33) * mm, "end": v(31.34, -17.2) * mm});
            skLineSegment(sketch, "E1357", {"start": v(31.34, -17.2) * mm, "end": v(31.25, -17.09) * mm});
            skLineSegment(sketch, "E1358", {"start": v(31.25, -17.09) * mm, "end": v(31.16, -16.97) * mm});
            skLineSegment(sketch, "E1359", {"start": v(31.16, -16.97) * mm, "end": v(31.07, -16.86) * mm});
            skLineSegment(sketch, "E1360", {"start": v(31.07, -16.86) * mm, "end": v(30.97, -16.75) * mm});
            skLineSegment(sketch, "E1361", {"start": v(30.97, -16.75) * mm, "end": v(30.89, -16.65) * mm});
            skLineSegment(sketch, "E1362", {"start": v(30.89, -16.65) * mm, "end": v(30.8, -16.55) * mm});
            skLineSegment(sketch, "E1363", {"start": v(30.8, -16.55) * mm, "end": v(30.71, -16.45) * mm});
            skLineSegment(sketch, "E1364", {"start": v(30.71, -16.45) * mm, "end": v(30.63, -16.36) * mm});
            skLineSegment(sketch, "E1365", {"start": v(30.63, -16.36) * mm, "end": v(30.54, -16.27) * mm});
            skLineSegment(sketch, "E1366", {"start": v(30.54, -16.27) * mm, "end": v(30.46, -16.19) * mm});
            skLineSegment(sketch, "E1367", {"start": v(30.46, -16.19) * mm, "end": v(30.38, -16.1) * mm});
            skLineSegment(sketch, "E1368", {"start": v(30.38, -16.1) * mm, "end": v(30.3, -16.03) * mm});
            skLineSegment(sketch, "E1369", {"start": v(30.3, -16.03) * mm, "end": v(30.23, -15.95) * mm});
            skLineSegment(sketch, "E1370", {"start": v(30.23, -15.95) * mm, "end": v(30.15, -15.88) * mm});
            skLineSegment(sketch, "E1371", {"start": v(30.15, -15.88) * mm, "end": v(30.08, -15.82) * mm});
            skLineSegment(sketch, "E1372", {"start": v(30.08, -15.82) * mm, "end": v(30.01, -15.75) * mm});
            skLineSegment(sketch, "E1373", {"start": v(30.01, -15.75) * mm, "end": v(29.95, -15.7) * mm});
            skLineSegment(sketch, "E1374", {"start": v(29.95, -15.7) * mm, "end": v(29.88, -15.64) * mm});
            skLineSegment(sketch, "E1375", {"start": v(29.88, -15.64) * mm, "end": v(29.82, -15.58) * mm});
            skLineSegment(sketch, "E1376", {"start": v(29.82, -15.58) * mm, "end": v(29.76, -15.53) * mm});
            skLineSegment(sketch, "E1377", {"start": v(29.76, -15.53) * mm, "end": v(29.7, -15.49) * mm});
            skLineSegment(sketch, "E1378", {"start": v(29.7, -15.49) * mm, "end": v(29.65, -15.44) * mm});
            skLineSegment(sketch, "E1379", {"start": v(29.65, -15.44) * mm, "end": v(29.6, -15.4) * mm});
            skLineSegment(sketch, "E1380", {"start": v(29.6, -15.4) * mm, "end": v(29.54, -15.36) * mm});
            skLineSegment(sketch, "E1381", {"start": v(29.54, -15.36) * mm, "end": v(29.5, -15.33) * mm});
            skLineSegment(sketch, "E1382", {"start": v(29.5, -15.33) * mm, "end": v(29.45, -15.3) * mm});
            skLineSegment(sketch, "E1383", {"start": v(29.45, -15.3) * mm, "end": v(29.4, -15.26) * mm});
            skLineSegment(sketch, "E1384", {"start": v(29.4, -15.26) * mm, "end": v(29.37, -15.24) * mm});
            skLineSegment(sketch, "E1385", {"start": v(29.37, -15.24) * mm, "end": v(29.34, -15.21) * mm});
            skLineSegment(sketch, "E1386", {"start": v(29.34, -15.21) * mm, "end": v(29.3, -15.2) * mm});
            skLineSegment(sketch, "E1387", {"start": v(29.3, -15.2) * mm, "end": v(29.27, -15.17) * mm});
            skLineSegment(sketch, "E1388", {"start": v(29.27, -15.17) * mm, "end": v(29.25, -15.15) * mm});
            skLineSegment(sketch, "E1389", {"start": v(29.25, -15.15) * mm, "end": v(29.22, -15.14) * mm});
            skLineSegment(sketch, "E1390", {"start": v(29.22, -15.14) * mm, "end": v(29.2, -15.13) * mm});
            skLineSegment(sketch, "E1391", {"start": v(29.2, -15.13) * mm, "end": v(29.19, -15.12) * mm});
            skLineSegment(sketch, "E1392", {"start": v(29.19, -15.12) * mm, "end": v(29.17, -15.1) * mm});
            skLineSegment(sketch, "E1393", {"start": v(29.17, -15.1) * mm, "end": v(29.16, -15.1) * mm});
            skLineSegment(sketch, "E1394", {"start": v(29.16, -15.1) * mm, "end": v(29.15, -15.1) * mm});
            skLineSegment(sketch, "E1395", {"start": v(29.15, -15.1) * mm, "end": v(28.8, -14.91) * mm});
            skLineSegment(sketch, "E1396", {"start": v(28.8, -14.91) * mm, "end": v(29.77, -12.85) * mm});
            skLineSegment(sketch, "E1397", {"start": v(29.77, -12.85) * mm, "end": v(30.14, -13.01) * mm});
            skLineSegment(sketch, "E1398", {"start": v(30.14, -13.01) * mm, "end": v(30.15, -13.02) * mm});
            skLineSegment(sketch, "E1399", {"start": v(30.15, -13.02) * mm, "end": v(30.16, -13.02) * mm});
            skLineSegment(sketch, "E1400", {"start": v(30.16, -13.02) * mm, "end": v(30.18, -13.03) * mm});
            skLineSegment(sketch, "E1401", {"start": v(30.18, -13.03) * mm, "end": v(30.2, -13.03) * mm});
            skLineSegment(sketch, "E1402", {"start": v(30.2, -13.03) * mm, "end": v(30.22, -13.04) * mm});
            skLineSegment(sketch, "E1403", {"start": v(30.22, -13.04) * mm, "end": v(30.24, -13.05) * mm});
            skLineSegment(sketch, "E1404", {"start": v(30.24, -13.05) * mm, "end": v(30.27, -13.06) * mm});
            skLineSegment(sketch, "E1405", {"start": v(30.27, -13.06) * mm, "end": v(30.3, -13.07) * mm});
            skLineSegment(sketch, "E1406", {"start": v(30.3, -13.07) * mm, "end": v(30.34, -13.08) * mm});
            skLineSegment(sketch, "E1407", {"start": v(30.34, -13.08) * mm, "end": v(30.39, -13.1) * mm});
            skLineSegment(sketch, "E1408", {"start": v(30.39, -13.1) * mm, "end": v(30.43, -13.1) * mm});
            skLineSegment(sketch, "E1409", {"start": v(30.43, -13.1) * mm, "end": v(30.48, -13.12) * mm});
            skLineSegment(sketch, "E1410", {"start": v(30.48, -13.12) * mm, "end": v(30.53, -13.14) * mm});
            skLineSegment(sketch, "E1411", {"start": v(30.53, -13.14) * mm, "end": v(30.6, -13.15) * mm});
            skLineSegment(sketch, "E1412", {"start": v(30.6, -13.15) * mm, "end": v(30.65, -13.17) * mm});
            skLineSegment(sketch, "E1413", {"start": v(30.65, -13.17) * mm, "end": v(30.72, -13.18) * mm});
            skLineSegment(sketch, "E1414", {"start": v(30.72, -13.18) * mm, "end": v(30.79, -13.2) * mm});
            skLineSegment(sketch, "E1415", {"start": v(30.79, -13.2) * mm, "end": v(30.86, -13.2) * mm});
            skLineSegment(sketch, "E1416", {"start": v(30.86, -13.2) * mm, "end": v(30.94, -13.22) * mm});
            skLineSegment(sketch, "E1417", {"start": v(30.94, -13.22) * mm, "end": v(31.02, -13.24) * mm});
            skLineSegment(sketch, "E1418", {"start": v(31.02, -13.24) * mm, "end": v(31.1, -13.25) * mm});
            skLineSegment(sketch, "E1419", {"start": v(31.1, -13.25) * mm, "end": v(31.2, -13.27) * mm});
            skLineSegment(sketch, "E1420", {"start": v(31.2, -13.27) * mm, "end": v(31.29, -13.28) * mm});
            skLineSegment(sketch, "E1421", {"start": v(31.29, -13.28) * mm, "end": v(31.38, -13.3) * mm});
            skLineSegment(sketch, "E1422", {"start": v(31.38, -13.3) * mm, "end": v(31.48, -13.3) * mm});
            skLineSegment(sketch, "E1423", {"start": v(31.48, -13.3) * mm, "end": v(31.59, -13.32) * mm});
            skLineSegment(sketch, "E1424", {"start": v(31.59, -13.32) * mm, "end": v(31.7, -13.33) * mm});
            skLineSegment(sketch, "E1425", {"start": v(31.7, -13.33) * mm, "end": v(31.81, -13.34) * mm});
            skLineSegment(sketch, "E1426", {"start": v(31.81, -13.34) * mm, "end": v(31.93, -13.35) * mm});
            skLineSegment(sketch, "E1427", {"start": v(31.93, -13.35) * mm, "end": v(32.05, -13.36) * mm});
            skLineSegment(sketch, "E1428", {"start": v(32.05, -13.36) * mm, "end": v(32.18, -13.36) * mm});
            skLineSegment(sketch, "E1429", {"start": v(32.18, -13.36) * mm, "end": v(32.3, -13.37) * mm});
            skLineSegment(sketch, "E1430", {"start": v(32.3, -13.37) * mm, "end": v(32.44, -13.37) * mm});
            skLineSegment(sketch, "E1431", {"start": v(32.44, -13.37) * mm, "end": v(32.57, -13.38) * mm});
            skLineSegment(sketch, "E1432", {"start": v(32.57, -13.38) * mm, "end": v(32.72, -13.38) * mm});
            skLineSegment(sketch, "E1433", {"start": v(32.72, -13.38) * mm, "end": v(32.86, -13.38) * mm});
            skLineSegment(sketch, "E1434", {"start": v(32.86, -13.38) * mm, "end": v(33, -13.38) * mm});
            skLineSegment(sketch, "E1435", {"start": v(33, -13.38) * mm, "end": v(33.16, -13.38) * mm});
            skLineSegment(sketch, "E1436", {"start": v(33.16, -13.38) * mm, "end": v(33.32, -13.37) * mm});
            skLineSegment(sketch, "E1437", {"start": v(33.32, -13.37) * mm, "end": v(33.48, -13.37) * mm});
            skLineSegment(sketch, "E1438", {"start": v(33.48, -13.37) * mm, "end": v(33.64, -13.36) * mm});
            skLineSegment(sketch, "E1439", {"start": v(33.64, -13.36) * mm, "end": v(33.81, -13.35) * mm});
            skLineSegment(sketch, "E1440", {"start": v(33.81, -13.35) * mm, "end": v(33.98, -13.33) * mm});
            skLineSegment(sketch, "E1441", {"start": v(33.98, -13.33) * mm, "end": v(34.16, -13.32) * mm});
            skLineSegment(sketch, "E1442", {"start": v(34.16, -13.32) * mm, "end": v(34.34, -13.3) * mm});
            skLineSegment(sketch, "E1443", {"start": v(34.34, -13.3) * mm, "end": v(34.52, -13.28) * mm});
            skLineSegment(sketch, "E1444", {"start": v(34.52, -13.28) * mm, "end": v(34.67, -13.25) * mm});
            skLineSegment(sketch, "E1445", {"start": v(34.67, -13.25) * mm, "end": v(35.18, -11.82) * mm});
            skLineSegment(sketch, "E1446", {"start": v(35.18, -11.82) * mm, "end": v(35.09, -11.7) * mm});
            skLineSegment(sketch, "E1447", {"start": v(35.09, -11.7) * mm, "end": v(34.96, -11.57) * mm});
            skLineSegment(sketch, "E1448", {"start": v(34.96, -11.57) * mm, "end": v(34.83, -11.44) * mm});
            skLineSegment(sketch, "E1449", {"start": v(34.83, -11.44) * mm, "end": v(34.7, -11.32) * mm});
            skLineSegment(sketch, "E1450", {"start": v(34.7, -11.32) * mm, "end": v(34.58, -11.2) * mm});
            skLineSegment(sketch, "E1451", {"start": v(34.58, -11.2) * mm, "end": v(34.46, -11.08) * mm});
            skLineSegment(sketch, "E1452", {"start": v(34.46, -11.08) * mm, "end": v(34.34, -10.97) * mm});
            skLineSegment(sketch, "E1453", {"start": v(34.34, -10.97) * mm, "end": v(34.22, -10.87) * mm});
            skLineSegment(sketch, "E1454", {"start": v(34.22, -10.87) * mm, "end": v(34.1, -10.76) * mm});
            skLineSegment(sketch, "E1455", {"start": v(34.1, -10.76) * mm, "end": v(33.98, -10.66) * mm});
            skLineSegment(sketch, "E1456", {"start": v(33.98, -10.66) * mm, "end": v(33.87, -10.57) * mm});
            skLineSegment(sketch, "E1457", {"start": v(33.87, -10.57) * mm, "end": v(33.76, -10.48) * mm});
            skLineSegment(sketch, "E1458", {"start": v(33.76, -10.48) * mm, "end": v(33.65, -10.39) * mm});
            skLineSegment(sketch, "E1459", {"start": v(33.65, -10.39) * mm, "end": v(33.54, -10.3) * mm});
            skLineSegment(sketch, "E1460", {"start": v(33.54, -10.3) * mm, "end": v(33.43, -10.22) * mm});
            skLineSegment(sketch, "E1461", {"start": v(33.43, -10.22) * mm, "end": v(33.33, -10.15) * mm});
            skLineSegment(sketch, "E1462", {"start": v(33.33, -10.15) * mm, "end": v(33.23, -10.07) * mm});
            skLineSegment(sketch, "E1463", {"start": v(33.23, -10.07) * mm, "end": v(33.13, -10) * mm});
            skLineSegment(sketch, "E1464", {"start": v(33.13, -10) * mm, "end": v(33.03, -9.93) * mm});
            skLineSegment(sketch, "E1465", {"start": v(33.03, -9.93) * mm, "end": v(32.94, -9.87) * mm});
            skLineSegment(sketch, "E1466", {"start": v(32.94, -9.87) * mm, "end": v(32.85, -9.8) * mm});
            skLineSegment(sketch, "E1467", {"start": v(32.85, -9.8) * mm, "end": v(32.76, -9.75) * mm});
            skLineSegment(sketch, "E1468", {"start": v(32.76, -9.75) * mm, "end": v(32.67, -9.7) * mm});
            skLineSegment(sketch, "E1469", {"start": v(32.67, -9.7) * mm, "end": v(32.6, -9.64) * mm});
            skLineSegment(sketch, "E1470", {"start": v(32.6, -9.64) * mm, "end": v(32.51, -9.6) * mm});
            skLineSegment(sketch, "E1471", {"start": v(32.51, -9.6) * mm, "end": v(32.43, -9.55) * mm});
            skLineSegment(sketch, "E1472", {"start": v(32.43, -9.55) * mm, "end": v(32.36, -9.5) * mm});
            skLineSegment(sketch, "E1473", {"start": v(32.36, -9.5) * mm, "end": v(32.29, -9.47) * mm});
            skLineSegment(sketch, "E1474", {"start": v(32.29, -9.47) * mm, "end": v(32.22, -9.43) * mm});
            skLineSegment(sketch, "E1475", {"start": v(32.22, -9.43) * mm, "end": v(32.15, -9.4) * mm});
            skLineSegment(sketch, "E1476", {"start": v(32.15, -9.4) * mm, "end": v(32.09, -9.36) * mm});
            skLineSegment(sketch, "E1477", {"start": v(32.09, -9.36) * mm, "end": v(32.03, -9.33) * mm});
            skLineSegment(sketch, "E1478", {"start": v(32.03, -9.33) * mm, "end": v(31.97, -9.3) * mm});
            skLineSegment(sketch, "E1479", {"start": v(31.97, -9.3) * mm, "end": v(31.92, -9.28) * mm});
            skLineSegment(sketch, "E1480", {"start": v(31.92, -9.28) * mm, "end": v(31.87, -9.25) * mm});
            skLineSegment(sketch, "E1481", {"start": v(31.87, -9.25) * mm, "end": v(31.82, -9.23) * mm});
            skLineSegment(sketch, "E1482", {"start": v(31.82, -9.23) * mm, "end": v(31.78, -9.21) * mm});
            skLineSegment(sketch, "E1483", {"start": v(31.78, -9.21) * mm, "end": v(31.74, -9.2) * mm});
            skLineSegment(sketch, "E1484", {"start": v(31.74, -9.2) * mm, "end": v(31.7, -9.18) * mm});
            skLineSegment(sketch, "E1485", {"start": v(31.7, -9.18) * mm, "end": v(31.67, -9.17) * mm});
            skLineSegment(sketch, "E1486", {"start": v(31.67, -9.17) * mm, "end": v(31.64, -9.16) * mm});
            skLineSegment(sketch, "E1487", {"start": v(31.64, -9.16) * mm, "end": v(31.61, -9.15) * mm});
            skLineSegment(sketch, "E1488", {"start": v(31.61, -9.15) * mm, "end": v(31.6, -9.14) * mm});
            skLineSegment(sketch, "E1489", {"start": v(31.6, -9.14) * mm, "end": v(31.57, -9.13) * mm});
            skLineSegment(sketch, "E1490", {"start": v(31.57, -9.13) * mm, "end": v(31.56, -9.13) * mm});
            skLineSegment(sketch, "E1491", {"start": v(31.56, -9.13) * mm, "end": v(31.55, -9.12) * mm});
            skLineSegment(sketch, "E1492", {"start": v(31.55, -9.12) * mm, "end": v(31.54, -9.12) * mm});
            skLineSegment(sketch, "E1493", {"start": v(31.54, -9.12) * mm, "end": v(31.15, -9) * mm});
            skLineSegment(sketch, "E1494", {"start": v(31.15, -9) * mm, "end": v(31.7, -6.8) * mm});
            skLineSegment(sketch, "E1495", {"start": v(31.7, -6.8) * mm, "end": v(32.1, -6.88) * mm});
            skLineSegment(sketch, "E1496", {"start": v(32.1, -6.88) * mm, "end": v(32.1, -6.89) * mm});
            skLineSegment(sketch, "E1497", {"start": v(32.1, -6.89) * mm, "end": v(32.12, -6.89) * mm});
            skLineSegment(sketch, "E1498", {"start": v(32.12, -6.89) * mm, "end": v(32.14, -6.9) * mm});
            skLineSegment(sketch, "E1499", {"start": v(32.14, -6.9) * mm, "end": v(32.16, -6.9) * mm});
            skLineSegment(sketch, "E1500", {"start": v(32.16, -6.9) * mm, "end": v(32.18, -6.9) * mm});
            skLineSegment(sketch, "E1501", {"start": v(32.18, -6.9) * mm, "end": v(32.2, -6.9) * mm});
            skLineSegment(sketch, "E1502", {"start": v(32.2, -6.9) * mm, "end": v(32.24, -6.9) * mm});
            skLineSegment(sketch, "E1503", {"start": v(32.24, -6.9) * mm, "end": v(32.27, -6.9) * mm});
            skLineSegment(sketch, "E1504", {"start": v(32.27, -6.9) * mm, "end": v(32.31, -6.91) * mm});
            skLineSegment(sketch, "E1505", {"start": v(32.31, -6.91) * mm, "end": v(32.36, -6.92) * mm});
            skLineSegment(sketch, "E1506", {"start": v(32.36, -6.92) * mm, "end": v(32.4, -6.92) * mm});
            skLineSegment(sketch, "E1507", {"start": v(32.4, -6.92) * mm, "end": v(32.46, -6.92) * mm});
            skLineSegment(sketch, "E1508", {"start": v(32.46, -6.92) * mm, "end": v(32.51, -6.93) * mm});
            skLineSegment(sketch, "E1509", {"start": v(32.51, -6.93) * mm, "end": v(32.57, -6.93) * mm});
            skLineSegment(sketch, "E1510", {"start": v(32.57, -6.93) * mm, "end": v(32.63, -6.93) * mm});
            skLineSegment(sketch, "E1511", {"start": v(32.63, -6.93) * mm, "end": v(32.7, -6.93) * mm});
            skLineSegment(sketch, "E1512", {"start": v(32.7, -6.93) * mm, "end": v(32.77, -6.93) * mm});
            skLineSegment(sketch, "E1513", {"start": v(32.77, -6.93) * mm, "end": v(32.84, -6.93) * mm});
            skLineSegment(sketch, "E1514", {"start": v(32.84, -6.93) * mm, "end": v(32.92, -6.93) * mm});
            skLineSegment(sketch, "E1515", {"start": v(32.92, -6.93) * mm, "end": v(33, -6.93) * mm});
            skLineSegment(sketch, "E1516", {"start": v(33, -6.93) * mm, "end": v(33.1, -6.93) * mm});
            skLineSegment(sketch, "E1517", {"start": v(33.1, -6.93) * mm, "end": v(33.18, -6.93) * mm});
            skLineSegment(sketch, "E1518", {"start": v(33.18, -6.93) * mm, "end": v(33.28, -6.92) * mm});
            skLineSegment(sketch, "E1519", {"start": v(33.28, -6.92) * mm, "end": v(33.37, -6.92) * mm});
            skLineSegment(sketch, "E1520", {"start": v(33.37, -6.92) * mm, "end": v(33.48, -6.9) * mm});
            skLineSegment(sketch, "E1521", {"start": v(33.48, -6.9) * mm, "end": v(33.58, -6.9) * mm});
            skLineSegment(sketch, "E1522", {"start": v(33.58, -6.9) * mm, "end": v(33.7, -6.89) * mm});
            skLineSegment(sketch, "E1523", {"start": v(33.7, -6.89) * mm, "end": v(33.8, -6.88) * mm});
            skLineSegment(sketch, "E1524", {"start": v(33.8, -6.88) * mm, "end": v(33.92, -6.86) * mm});
            skLineSegment(sketch, "E1525", {"start": v(33.92, -6.86) * mm, "end": v(34.04, -6.85) * mm});
            skLineSegment(sketch, "E1526", {"start": v(34.04, -6.85) * mm, "end": v(34.16, -6.83) * mm});
            skLineSegment(sketch, "E1527", {"start": v(34.16, -6.83) * mm, "end": v(34.3, -6.81) * mm});
            skLineSegment(sketch, "E1528", {"start": v(34.3, -6.81) * mm, "end": v(34.42, -6.79) * mm});
            skLineSegment(sketch, "E1529", {"start": v(34.42, -6.79) * mm, "end": v(34.56, -6.77) * mm});
            skLineSegment(sketch, "E1530", {"start": v(34.56, -6.77) * mm, "end": v(34.7, -6.74) * mm});
            skLineSegment(sketch, "E1531", {"start": v(34.7, -6.74) * mm, "end": v(34.84, -6.71) * mm});
            skLineSegment(sketch, "E1532", {"start": v(34.84, -6.71) * mm, "end": v(34.99, -6.68) * mm});
            skLineSegment(sketch, "E1533", {"start": v(34.99, -6.68) * mm, "end": v(35.13, -6.65) * mm});
            skLineSegment(sketch, "E1534", {"start": v(35.13, -6.65) * mm, "end": v(35.29, -6.61) * mm});
            skLineSegment(sketch, "E1535", {"start": v(35.29, -6.61) * mm, "end": v(35.44, -6.58) * mm});
            skLineSegment(sketch, "E1536", {"start": v(35.44, -6.58) * mm, "end": v(35.6, -6.54) * mm});
            skLineSegment(sketch, "E1537", {"start": v(35.6, -6.54) * mm, "end": v(35.77, -6.5) * mm});
            skLineSegment(sketch, "E1538", {"start": v(35.77, -6.5) * mm, "end": v(35.93, -6.45) * mm});
            skLineSegment(sketch, "E1539", {"start": v(35.93, -6.45) * mm, "end": v(36.1, -6.4) * mm});
            skLineSegment(sketch, "E1540", {"start": v(36.1, -6.4) * mm, "end": v(36.27, -6.35) * mm});
            skLineSegment(sketch, "E1541", {"start": v(36.27, -6.35) * mm, "end": v(36.45, -6.3) * mm});
            skLineSegment(sketch, "E1542", {"start": v(36.45, -6.3) * mm, "end": v(36.6, -6.23) * mm});
            skLineSegment(sketch, "E1543", {"start": v(36.6, -6.23) * mm, "end": v(36.81, -4.73) * mm});
            skLineSegment(sketch, "E1544", {"start": v(36.81, -4.73) * mm, "end": v(36.7, -4.63) * mm});
            skLineSegment(sketch, "E1545", {"start": v(36.7, -4.63) * mm, "end": v(36.55, -4.53) * mm});
            skLineSegment(sketch, "E1546", {"start": v(36.55, -4.53) * mm, "end": v(36.4, -4.43) * mm});
            skLineSegment(sketch, "E1547", {"start": v(36.4, -4.43) * mm, "end": v(36.25, -4.33) * mm});
            skLineSegment(sketch, "E1548", {"start": v(36.25, -4.33) * mm, "end": v(36.1, -4.24) * mm});
            skLineSegment(sketch, "E1549", {"start": v(36.1, -4.24) * mm, "end": v(35.96, -4.15) * mm});
            skLineSegment(sketch, "E1550", {"start": v(35.96, -4.15) * mm, "end": v(35.82, -4.06) * mm});
            skLineSegment(sketch, "E1551", {"start": v(35.82, -4.06) * mm, "end": v(35.68, -3.98) * mm});
            skLineSegment(sketch, "E1552", {"start": v(35.68, -3.98) * mm, "end": v(35.54, -3.9) * mm});
            skLineSegment(sketch, "E1553", {"start": v(35.54, -3.9) * mm, "end": v(35.41, -3.83) * mm});
            skLineSegment(sketch, "E1554", {"start": v(35.41, -3.83) * mm, "end": v(35.28, -3.76) * mm});
            skLineSegment(sketch, "E1555", {"start": v(35.28, -3.76) * mm, "end": v(35.15, -3.69) * mm});
            skLineSegment(sketch, "E1556", {"start": v(35.15, -3.69) * mm, "end": v(35.03, -3.62) * mm});
            skLineSegment(sketch, "E1557", {"start": v(35.03, -3.62) * mm, "end": v(34.9, -3.56) * mm});
            skLineSegment(sketch, "E1558", {"start": v(34.9, -3.56) * mm, "end": v(34.79, -3.5) * mm});
            skLineSegment(sketch, "E1559", {"start": v(34.79, -3.5) * mm, "end": v(34.67, -3.45) * mm});
            skLineSegment(sketch, "E1560", {"start": v(34.67, -3.45) * mm, "end": v(34.56, -3.4) * mm});
            skLineSegment(sketch, "E1561", {"start": v(34.56, -3.4) * mm, "end": v(34.45, -3.35) * mm});
            skLineSegment(sketch, "E1562", {"start": v(34.45, -3.35) * mm, "end": v(34.34, -3.3) * mm});
            skLineSegment(sketch, "E1563", {"start": v(34.34, -3.3) * mm, "end": v(34.23, -3.25) * mm});
            skLineSegment(sketch, "E1564", {"start": v(34.23, -3.25) * mm, "end": v(34.13, -3.21) * mm});
            skLineSegment(sketch, "E1565", {"start": v(34.13, -3.21) * mm, "end": v(34.03, -3.17) * mm});
            skLineSegment(sketch, "E1566", {"start": v(34.03, -3.17) * mm, "end": v(33.94, -3.14) * mm});
            skLineSegment(sketch, "E1567", {"start": v(33.94, -3.14) * mm, "end": v(33.85, -3.1) * mm});
            skLineSegment(sketch, "E1568", {"start": v(33.85, -3.1) * mm, "end": v(33.76, -3.07) * mm});
            skLineSegment(sketch, "E1569", {"start": v(33.76, -3.07) * mm, "end": v(33.67, -3.04) * mm});
            skLineSegment(sketch, "E1570", {"start": v(33.67, -3.04) * mm, "end": v(33.6, -3.01) * mm});
            skLineSegment(sketch, "E1571", {"start": v(33.6, -3.01) * mm, "end": v(33.51, -2.99) * mm});
            skLineSegment(sketch, "E1572", {"start": v(33.51, -2.99) * mm, "end": v(33.44, -2.96) * mm});
            skLineSegment(sketch, "E1573", {"start": v(33.44, -2.96) * mm, "end": v(33.37, -2.94) * mm});
            skLineSegment(sketch, "E1574", {"start": v(33.37, -2.94) * mm, "end": v(33.3, -2.92) * mm});
            skLineSegment(sketch, "E1575", {"start": v(33.3, -2.92) * mm, "end": v(33.23, -2.9) * mm});
            skLineSegment(sketch, "E1576", {"start": v(33.23, -2.9) * mm, "end": v(33.17, -2.89) * mm});
            skLineSegment(sketch, "E1577", {"start": v(33.17, -2.89) * mm, "end": v(33.12, -2.87) * mm});
            skLineSegment(sketch, "E1578", {"start": v(33.12, -2.87) * mm, "end": v(33.06, -2.86) * mm});
            skLineSegment(sketch, "E1579", {"start": v(33.06, -2.86) * mm, "end": v(33.01, -2.85) * mm});
            skLineSegment(sketch, "E1580", {"start": v(33.01, -2.85) * mm, "end": v(32.97, -2.84) * mm});
            skLineSegment(sketch, "E1581", {"start": v(32.97, -2.84) * mm, "end": v(32.92, -2.83) * mm});
            skLineSegment(sketch, "E1582", {"start": v(32.92, -2.83) * mm, "end": v(32.89, -2.82) * mm});
            skLineSegment(sketch, "E1583", {"start": v(32.89, -2.82) * mm, "end": v(32.85, -2.81) * mm});
            skLineSegment(sketch, "E1584", {"start": v(32.85, -2.81) * mm, "end": v(32.82, -2.8) * mm});
            skLineSegment(sketch, "E1585", {"start": v(32.82, -2.8) * mm, "end": v(32.8, -2.8) * mm});
            skLineSegment(sketch, "E1586", {"start": v(32.8, -2.8) * mm, "end": v(32.77, -2.8) * mm});
            skLineSegment(sketch, "E1587", {"start": v(32.77, -2.8) * mm, "end": v(32.75, -2.8) * mm});
            skLineSegment(sketch, "E1588", {"start": v(32.75, -2.8) * mm, "end": v(32.73, -2.8) * mm});
            skLineSegment(sketch, "E1589", {"start": v(32.73, -2.8) * mm, "end": v(32.72, -2.8) * mm});
            skLineSegment(sketch, "E1590", {"start": v(32.72, -2.8) * mm, "end": v(32.71, -2.8) * mm});
            skLineSegment(sketch, "E1591", {"start": v(32.71, -2.8) * mm, "end": v(32.3, -2.76) * mm});
            skLineSegment(sketch, "E1592", {"start": v(32.3, -2.76) * mm, "end": v(32.42, -0.48) * mm});
            skLineSegment(sketch, "E1593", {"start": v(32.42, -0.48) * mm, "end": v(32.83, -0.49) * mm});
            skLineSegment(sketch, "E1594", {"start": v(32.83, -0.49) * mm, "end": v(32.84, -0.49) * mm});
            skLineSegment(sketch, "E1595", {"start": v(32.84, -0.49) * mm, "end": v(32.85, -0.49) * mm});
            skLineSegment(sketch, "E1596", {"start": v(32.85, -0.49) * mm, "end": v(32.86, -0.49) * mm});
            skLineSegment(sketch, "E1597", {"start": v(32.86, -0.49) * mm, "end": v(32.88, -0.49) * mm});
            skLineSegment(sketch, "E1598", {"start": v(32.88, -0.49) * mm, "end": v(32.9, -0.49) * mm});
            skLineSegment(sketch, "E1599", {"start": v(32.9, -0.49) * mm, "end": v(32.94, -0.48) * mm});
            skLineSegment(sketch, "E1600", {"start": v(32.94, -0.48) * mm, "end": v(32.97, -0.48) * mm});
            skLineSegment(sketch, "E1601", {"start": v(32.97, -0.48) * mm, "end": v(33, -0.48) * mm});
            skLineSegment(sketch, "E1602", {"start": v(33, -0.48) * mm, "end": v(33.04, -0.48) * mm});
            skLineSegment(sketch, "E1603", {"start": v(33.04, -0.48) * mm, "end": v(33.09, -0.47) * mm});
            skLineSegment(sketch, "E1604", {"start": v(33.09, -0.47) * mm, "end": v(33.13, -0.47) * mm});
            skLineSegment(sketch, "E1605", {"start": v(33.13, -0.47) * mm, "end": v(33.18, -0.46) * mm});
            skLineSegment(sketch, "E1606", {"start": v(33.18, -0.46) * mm, "end": v(33.24, -0.45) * mm});
            skLineSegment(sketch, "E1607", {"start": v(33.24, -0.45) * mm, "end": v(33.3, -0.44) * mm});
            skLineSegment(sketch, "E1608", {"start": v(33.3, -0.44) * mm, "end": v(33.36, -0.43) * mm});
            skLineSegment(sketch, "E1609", {"start": v(33.36, -0.43) * mm, "end": v(33.42, -0.42) * mm});
            skLineSegment(sketch, "E1610", {"start": v(33.42, -0.42) * mm, "end": v(33.5, -0.4) * mm});
            skLineSegment(sketch, "E1611", {"start": v(33.5, -0.4) * mm, "end": v(33.57, -0.4) * mm});
            skLineSegment(sketch, "E1612", {"start": v(33.57, -0.4) * mm, "end": v(33.64, -0.38) * mm});
            skLineSegment(sketch, "E1613", {"start": v(33.64, -0.38) * mm, "end": v(33.72, -0.36) * mm});
            skLineSegment(sketch, "E1614", {"start": v(33.72, -0.36) * mm, "end": v(33.8, -0.34) * mm});
            skLineSegment(sketch, "E1615", {"start": v(33.8, -0.34) * mm, "end": v(33.9, -0.32) * mm});
            skLineSegment(sketch, "E1616", {"start": v(33.9, -0.32) * mm, "end": v(33.99, -0.3) * mm});
            skLineSegment(sketch, "E1617", {"start": v(33.99, -0.3) * mm, "end": v(34.08, -0.27) * mm});
            skLineSegment(sketch, "E1618", {"start": v(34.08, -0.27) * mm, "end": v(34.18, -0.24) * mm});
            skLineSegment(sketch, "E1619", {"start": v(34.18, -0.24) * mm, "end": v(34.28, -0.22) * mm});
            skLineSegment(sketch, "E1620", {"start": v(34.28, -0.22) * mm, "end": v(34.39, -0.18) * mm});
            skLineSegment(sketch, "E1621", {"start": v(34.39, -0.18) * mm, "end": v(34.5, -0.15) * mm});
            skLineSegment(sketch, "E1622", {"start": v(34.5, -0.15) * mm, "end": v(34.6, -0.11) * mm});
            skLineSegment(sketch, "E1623", {"start": v(34.6, -0.11) * mm, "end": v(34.72, -0.07) * mm});
            skLineSegment(sketch, "E1624", {"start": v(34.72, -0.07) * mm, "end": v(34.84, -0.03) * mm});
            skLineSegment(sketch, "E1625", {"start": v(34.84, -0.03) * mm, "end": v(34.96, 0.01) * mm});
            skLineSegment(sketch, "E1626", {"start": v(34.96, 0.01) * mm, "end": v(35.09, 0.06) * mm});
            skLineSegment(sketch, "E1627", {"start": v(35.09, 0.06) * mm, "end": v(35.21, 0.1) * mm});
            skLineSegment(sketch, "E1628", {"start": v(35.21, 0.1) * mm, "end": v(35.35, 0.16) * mm});
            skLineSegment(sketch, "E1629", {"start": v(35.35, 0.16) * mm, "end": v(35.48, 0.21) * mm});
            skLineSegment(sketch, "E1630", {"start": v(35.48, 0.21) * mm, "end": v(35.62, 0.27) * mm});
            skLineSegment(sketch, "E1631", {"start": v(35.62, 0.27) * mm, "end": v(35.76, 0.33) * mm});
            skLineSegment(sketch, "E1632", {"start": v(35.76, 0.33) * mm, "end": v(35.9, 0.4) * mm});
            skLineSegment(sketch, "E1633", {"start": v(35.9, 0.4) * mm, "end": v(36.05, 0.46) * mm});
            skLineSegment(sketch, "E1634", {"start": v(36.05, 0.46) * mm, "end": v(36.2, 0.53) * mm});
            skLineSegment(sketch, "E1635", {"start": v(36.2, 0.53) * mm, "end": v(36.35, 0.6) * mm});
            skLineSegment(sketch, "E1636", {"start": v(36.35, 0.6) * mm, "end": v(36.5, 0.69) * mm});
            skLineSegment(sketch, "E1637", {"start": v(36.5, 0.69) * mm, "end": v(36.66, 0.77) * mm});
            skLineSegment(sketch, "E1638", {"start": v(36.66, 0.77) * mm, "end": v(36.81, 0.85) * mm});
            skLineSegment(sketch, "E1639", {"start": v(36.81, 0.85) * mm, "end": v(36.98, 0.94) * mm});
            skLineSegment(sketch, "E1640", {"start": v(36.98, 0.94) * mm, "end": v(37.1, 1.03) * mm});
            skLineSegment(sketch, "E1641", {"start": v(37.1, 1.03) * mm, "end": v(37.03, 2.54) * mm});
            skLineSegment(sketch, "E1642", {"start": v(37.03, 2.54) * mm, "end": v(36.9, 2.62) * mm});
            skLineSegment(sketch, "E1643", {"start": v(36.9, 2.62) * mm, "end": v(36.73, 2.7) * mm});
            skLineSegment(sketch, "E1644", {"start": v(36.73, 2.7) * mm, "end": v(36.56, 2.76) * mm});
            skLineSegment(sketch, "E1645", {"start": v(36.56, 2.76) * mm, "end": v(36.4, 2.82) * mm});
            skLineSegment(sketch, "E1646", {"start": v(36.4, 2.82) * mm, "end": v(36.24, 2.89) * mm});
            skLineSegment(sketch, "E1647", {"start": v(36.24, 2.89) * mm, "end": v(36.08, 2.95) * mm});
            skLineSegment(sketch, "E1648", {"start": v(36.08, 2.95) * mm, "end": v(35.92, 3) * mm});
            skLineSegment(sketch, "E1649", {"start": v(35.92, 3) * mm, "end": v(35.77, 3.05) * mm});
            skLineSegment(sketch, "E1650", {"start": v(35.77, 3.05) * mm, "end": v(35.62, 3.1) * mm});
            skLineSegment(sketch, "E1651", {"start": v(35.62, 3.1) * mm, "end": v(35.48, 3.15) * mm});
            skLineSegment(sketch, "E1652", {"start": v(35.48, 3.15) * mm, "end": v(35.34, 3.2) * mm});
            skLineSegment(sketch, "E1653", {"start": v(35.34, 3.2) * mm, "end": v(35.2, 3.24) * mm});
            skLineSegment(sketch, "E1654", {"start": v(35.2, 3.24) * mm, "end": v(35.06, 3.28) * mm});
            skLineSegment(sketch, "E1655", {"start": v(35.06, 3.28) * mm, "end": v(34.93, 3.32) * mm});
            skLineSegment(sketch, "E1656", {"start": v(34.93, 3.32) * mm, "end": v(34.8, 3.35) * mm});
            skLineSegment(sketch, "E1657", {"start": v(34.8, 3.35) * mm, "end": v(34.68, 3.38) * mm});
            skLineSegment(sketch, "E1658", {"start": v(34.68, 3.38) * mm, "end": v(34.55, 3.41) * mm});
            skLineSegment(sketch, "E1659", {"start": v(34.55, 3.41) * mm, "end": v(34.44, 3.44) * mm});
            skLineSegment(sketch, "E1660", {"start": v(34.44, 3.44) * mm, "end": v(34.32, 3.46) * mm});
            skLineSegment(sketch, "E1661", {"start": v(34.32, 3.46) * mm, "end": v(34.2, 3.49) * mm});
            skLineSegment(sketch, "E1662", {"start": v(34.2, 3.49) * mm, "end": v(34.1, 3.5) * mm});
            skLineSegment(sketch, "E1663", {"start": v(34.1, 3.5) * mm, "end": v(34, 3.53) * mm});
            skLineSegment(sketch, "E1664", {"start": v(34, 3.53) * mm, "end": v(33.9, 3.55) * mm});
            skLineSegment(sketch, "E1665", {"start": v(33.9, 3.55) * mm, "end": v(33.8, 3.56) * mm});
            skLineSegment(sketch, "E1666", {"start": v(33.8, 3.56) * mm, "end": v(33.7, 3.58) * mm});
            skLineSegment(sketch, "E1667", {"start": v(33.7, 3.58) * mm, "end": v(33.62, 3.59) * mm});
            skLineSegment(sketch, "E1668", {"start": v(33.62, 3.59) * mm, "end": v(33.53, 3.6) * mm});
            skLineSegment(sketch, "E1669", {"start": v(33.53, 3.6) * mm, "end": v(33.45, 3.6) * mm});
            skLineSegment(sketch, "E1670", {"start": v(33.45, 3.6) * mm, "end": v(33.37, 3.62) * mm});
            skLineSegment(sketch, "E1671", {"start": v(33.37, 3.62) * mm, "end": v(33.3, 3.63) * mm});
            skLineSegment(sketch, "E1672", {"start": v(33.3, 3.63) * mm, "end": v(33.23, 3.63) * mm});
            skLineSegment(sketch, "E1673", {"start": v(33.23, 3.63) * mm, "end": v(33.16, 3.64) * mm});
            skLineSegment(sketch, "E1674", {"start": v(33.16, 3.64) * mm, "end": v(33.1, 3.64) * mm});
            skLineSegment(sketch, "E1675", {"start": v(33.1, 3.64) * mm, "end": v(33.04, 3.64) * mm});
            skLineSegment(sketch, "E1676", {"start": v(33.04, 3.64) * mm, "end": v(32.98, 3.65) * mm});
            skLineSegment(sketch, "E1677", {"start": v(32.98, 3.65) * mm, "end": v(32.93, 3.65) * mm});
            skLineSegment(sketch, "E1678", {"start": v(32.93, 3.65) * mm, "end": v(32.89, 3.65) * mm});
            skLineSegment(sketch, "E1679", {"start": v(32.89, 3.65) * mm, "end": v(32.84, 3.65) * mm});
            skLineSegment(sketch, "E1680", {"start": v(32.84, 3.65) * mm, "end": v(32.8, 3.65) * mm});
            skLineSegment(sketch, "E1681", {"start": v(32.8, 3.65) * mm, "end": v(32.77, 3.65) * mm});
            skLineSegment(sketch, "E1682", {"start": v(32.77, 3.65) * mm, "end": v(32.74, 3.65) * mm});
            skLineSegment(sketch, "E1683", {"start": v(32.74, 3.65) * mm, "end": v(32.7, 3.65) * mm});
            skLineSegment(sketch, "E1684", {"start": v(32.7, 3.65) * mm, "end": v(32.69, 3.65) * mm});
            skLineSegment(sketch, "E1685", {"start": v(32.69, 3.65) * mm, "end": v(32.67, 3.64) * mm});
            skLineSegment(sketch, "E1686", {"start": v(32.67, 3.64) * mm, "end": v(32.65, 3.64) * mm});
            skLineSegment(sketch, "E1687", {"start": v(32.65, 3.64) * mm, "end": v(32.64, 3.64) * mm});
            skLineSegment(sketch, "E1688", {"start": v(32.64, 3.64) * mm, "end": v(32.63, 3.64) * mm});
            skLineSegment(sketch, "E1689", {"start": v(32.63, 3.64) * mm, "end": v(32.22, 3.6) * mm});
            skLineSegment(sketch, "E1690", {"start": v(32.22, 3.6) * mm, "end": v(31.9, 5.85) * mm});
            skLineSegment(sketch, "E1691", {"start": v(31.9, 5.85) * mm, "end": v(32.3, 5.92) * mm});
            skLineSegment(sketch, "E1692", {"start": v(32.3, 5.92) * mm, "end": v(32.3, 5.93) * mm});
            skLineSegment(sketch, "E1693", {"start": v(32.3, 5.93) * mm, "end": v(32.31, 5.93) * mm});
            skLineSegment(sketch, "E1694", {"start": v(32.31, 5.93) * mm, "end": v(32.33, 5.93) * mm});
            skLineSegment(sketch, "E1695", {"start": v(32.33, 5.93) * mm, "end": v(32.35, 5.94) * mm});
            skLineSegment(sketch, "E1696", {"start": v(32.35, 5.94) * mm, "end": v(32.37, 5.94) * mm});
            skLineSegment(sketch, "E1697", {"start": v(32.37, 5.94) * mm, "end": v(32.4, 5.95) * mm});
            skLineSegment(sketch, "E1698", {"start": v(32.4, 5.95) * mm, "end": v(32.43, 5.96) * mm});
            skLineSegment(sketch, "E1699", {"start": v(32.43, 5.96) * mm, "end": v(32.46, 5.97) * mm});
            skLineSegment(sketch, "E1700", {"start": v(32.46, 5.97) * mm, "end": v(32.5, 5.98) * mm});
            skLineSegment(sketch, "E1701", {"start": v(32.5, 5.98) * mm, "end": v(32.54, 6) * mm});
            skLineSegment(sketch, "E1702", {"start": v(32.54, 6) * mm, "end": v(32.59, 6) * mm});
            skLineSegment(sketch, "E1703", {"start": v(32.59, 6) * mm, "end": v(32.63, 6.02) * mm});
            skLineSegment(sketch, "E1704", {"start": v(32.63, 6.02) * mm, "end": v(32.69, 6.04) * mm});
            skLineSegment(sketch, "E1705", {"start": v(32.69, 6.04) * mm, "end": v(32.74, 6.06) * mm});
            skLineSegment(sketch, "E1706", {"start": v(32.74, 6.06) * mm, "end": v(32.8, 6.08) * mm});
            skLineSegment(sketch, "E1707", {"start": v(32.8, 6.08) * mm, "end": v(32.86, 6.1) * mm});
            skLineSegment(sketch, "E1708", {"start": v(32.86, 6.1) * mm, "end": v(32.93, 6.13) * mm});
            skLineSegment(sketch, "E1709", {"start": v(32.93, 6.13) * mm, "end": v(33, 6.16) * mm});
            skLineSegment(sketch, "E1710", {"start": v(33, 6.16) * mm, "end": v(33.07, 6.2) * mm});
            skLineSegment(sketch, "E1711", {"start": v(33.07, 6.2) * mm, "end": v(33.15, 6.23) * mm});
            skLineSegment(sketch, "E1712", {"start": v(33.15, 6.23) * mm, "end": v(33.22, 6.26) * mm});
            skLineSegment(sketch, "E1713", {"start": v(33.22, 6.26) * mm, "end": v(33.3, 6.3) * mm});
            skLineSegment(sketch, "E1714", {"start": v(33.3, 6.3) * mm, "end": v(33.4, 6.34) * mm});
            skLineSegment(sketch, "E1715", {"start": v(33.4, 6.34) * mm, "end": v(33.48, 6.38) * mm});
            skLineSegment(sketch, "E1716", {"start": v(33.48, 6.38) * mm, "end": v(33.57, 6.43) * mm});
            skLineSegment(sketch, "E1717", {"start": v(33.57, 6.43) * mm, "end": v(33.66, 6.48) * mm});
            skLineSegment(sketch, "E1718", {"start": v(33.66, 6.48) * mm, "end": v(33.76, 6.53) * mm});
            skLineSegment(sketch, "E1719", {"start": v(33.76, 6.53) * mm, "end": v(33.86, 6.58) * mm});
            skLineSegment(sketch, "E1720", {"start": v(33.86, 6.58) * mm, "end": v(33.96, 6.64) * mm});
            skLineSegment(sketch, "E1721", {"start": v(33.96, 6.64) * mm, "end": v(34.07, 6.7) * mm});
            skLineSegment(sketch, "E1722", {"start": v(34.07, 6.7) * mm, "end": v(34.18, 6.76) * mm});
            skLineSegment(sketch, "E1723", {"start": v(34.18, 6.76) * mm, "end": v(34.29, 6.83) * mm});
            skLineSegment(sketch, "E1724", {"start": v(34.29, 6.83) * mm, "end": v(34.4, 6.9) * mm});
            skLineSegment(sketch, "E1725", {"start": v(34.4, 6.9) * mm, "end": v(34.52, 6.97) * mm});
            skLineSegment(sketch, "E1726", {"start": v(34.52, 6.97) * mm, "end": v(34.64, 7.05) * mm});
            skLineSegment(sketch, "E1727", {"start": v(34.64, 7.05) * mm, "end": v(34.76, 7.13) * mm});
            skLineSegment(sketch, "E1728", {"start": v(34.76, 7.13) * mm, "end": v(34.88, 7.21) * mm});
            skLineSegment(sketch, "E1729", {"start": v(34.88, 7.21) * mm, "end": v(35, 7.3) * mm});
            skLineSegment(sketch, "E1730", {"start": v(35, 7.3) * mm, "end": v(35.13, 7.4) * mm});
            skLineSegment(sketch, "E1731", {"start": v(35.13, 7.4) * mm, "end": v(35.26, 7.49) * mm});
            skLineSegment(sketch, "E1732", {"start": v(35.26, 7.49) * mm, "end": v(35.4, 7.59) * mm});
            skLineSegment(sketch, "E1733", {"start": v(35.4, 7.59) * mm, "end": v(35.53, 7.69) * mm});
            skLineSegment(sketch, "E1734", {"start": v(35.53, 7.69) * mm, "end": v(35.66, 7.8) * mm});
            skLineSegment(sketch, "E1735", {"start": v(35.66, 7.8) * mm, "end": v(35.8, 7.9) * mm});
            skLineSegment(sketch, "E1736", {"start": v(35.8, 7.9) * mm, "end": v(35.94, 8.02) * mm});
            skLineSegment(sketch, "E1737", {"start": v(35.94, 8.02) * mm, "end": v(36.08, 8.14) * mm});
            skLineSegment(sketch, "E1738", {"start": v(36.08, 8.14) * mm, "end": v(36.19, 8.25) * mm});
            skLineSegment(sketch, "E1739", {"start": v(36.19, 8.25) * mm, "end": v(35.82, 9.72) * mm});
            skLineSegment(sketch, "E1740", {"start": v(35.82, 9.72) * mm, "end": v(35.68, 9.77) * mm});
            skLineSegment(sketch, "E1741", {"start": v(35.68, 9.77) * mm, "end": v(35.5, 9.8) * mm});
            skLineSegment(sketch, "E1742", {"start": v(35.5, 9.8) * mm, "end": v(35.32, 9.84) * mm});
            skLineSegment(sketch, "E1743", {"start": v(35.32, 9.84) * mm, "end": v(35.15, 9.87) * mm});
            skLineSegment(sketch, "E1744", {"start": v(35.15, 9.87) * mm, "end": v(34.98, 9.9) * mm});
            skLineSegment(sketch, "E1745", {"start": v(34.98, 9.9) * mm, "end": v(34.8, 9.93) * mm});
            skLineSegment(sketch, "E1746", {"start": v(34.8, 9.93) * mm, "end": v(34.65, 9.95) * mm});
            skLineSegment(sketch, "E1747", {"start": v(34.65, 9.95) * mm, "end": v(34.49, 9.98) * mm});
            skLineSegment(sketch, "E1748", {"start": v(34.49, 9.98) * mm, "end": v(34.33, 10) * mm});
            skLineSegment(sketch, "E1749", {"start": v(34.33, 10) * mm, "end": v(34.18, 10.01) * mm});
            skLineSegment(sketch, "E1750", {"start": v(34.18, 10.01) * mm, "end": v(34.03, 10.03) * mm});
            skLineSegment(sketch, "E1751", {"start": v(34.03, 10.03) * mm, "end": v(33.89, 10.04) * mm});
            skLineSegment(sketch, "E1752", {"start": v(33.89, 10.04) * mm, "end": v(33.75, 10.06) * mm});
            skLineSegment(sketch, "E1753", {"start": v(33.75, 10.06) * mm, "end": v(33.61, 10.07) * mm});
            skLineSegment(sketch, "E1754", {"start": v(33.61, 10.07) * mm, "end": v(33.48, 10.07) * mm});
            skLineSegment(sketch, "E1755", {"start": v(33.48, 10.07) * mm, "end": v(33.35, 10.08) * mm});
            skLineSegment(sketch, "E1756", {"start": v(33.35, 10.08) * mm, "end": v(33.22, 10.09) * mm});
            skLineSegment(sketch, "E1757", {"start": v(33.22, 10.09) * mm, "end": v(33.1, 10.1) * mm});
            skLineSegment(sketch, "E1758", {"start": v(33.1, 10.1) * mm, "end": v(32.99, 10.1) * mm});
            skLineSegment(sketch, "E1759", {"start": v(32.99, 10.1) * mm, "end": v(32.87, 10.1) * mm});
            skLineSegment(sketch, "E1760", {"start": v(32.87, 10.1) * mm, "end": v(32.76, 10.1) * mm});
            skLineSegment(sketch, "E1761", {"start": v(32.76, 10.1) * mm, "end": v(32.66, 10.1) * mm});
            skLineSegment(sketch, "E1762", {"start": v(32.66, 10.1) * mm, "end": v(32.55, 10.1) * mm});
            skLineSegment(sketch, "E1763", {"start": v(32.55, 10.1) * mm, "end": v(32.46, 10.09) * mm});
            skLineSegment(sketch, "E1764", {"start": v(32.46, 10.09) * mm, "end": v(32.36, 10.08) * mm});
            skLineSegment(sketch, "E1765", {"start": v(32.36, 10.08) * mm, "end": v(32.27, 10.08) * mm});
            skLineSegment(sketch, "E1766", {"start": v(32.27, 10.08) * mm, "end": v(32.19, 10.07) * mm});
            skLineSegment(sketch, "E1767", {"start": v(32.19, 10.07) * mm, "end": v(32.1, 10.07) * mm});
            skLineSegment(sketch, "E1768", {"start": v(32.1, 10.07) * mm, "end": v(32.03, 10.06) * mm});
            skLineSegment(sketch, "E1769", {"start": v(32.03, 10.06) * mm, "end": v(31.95, 10.05) * mm});
            skLineSegment(sketch, "E1770", {"start": v(31.95, 10.05) * mm, "end": v(31.88, 10.04) * mm});
            skLineSegment(sketch, "E1771", {"start": v(31.88, 10.04) * mm, "end": v(31.82, 10.04) * mm});
            skLineSegment(sketch, "E1772", {"start": v(31.82, 10.04) * mm, "end": v(31.75, 10.03) * mm});
            skLineSegment(sketch, "E1773", {"start": v(31.75, 10.03) * mm, "end": v(31.7, 10.02) * mm});
            skLineSegment(sketch, "E1774", {"start": v(31.7, 10.02) * mm, "end": v(31.64, 10.01) * mm});
            skLineSegment(sketch, "E1775", {"start": v(31.64, 10.01) * mm, "end": v(31.59, 10) * mm});
            skLineSegment(sketch, "E1776", {"start": v(31.59, 10) * mm, "end": v(31.54, 10) * mm});
            skLineSegment(sketch, "E1777", {"start": v(31.54, 10) * mm, "end": v(31.5, 9.99) * mm});
            skLineSegment(sketch, "E1778", {"start": v(31.5, 9.99) * mm, "end": v(31.46, 9.98) * mm});
            skLineSegment(sketch, "E1779", {"start": v(31.46, 9.98) * mm, "end": v(31.43, 9.97) * mm});
            skLineSegment(sketch, "E1780", {"start": v(31.43, 9.97) * mm, "end": v(31.4, 9.96) * mm});
            skLineSegment(sketch, "E1781", {"start": v(31.4, 9.96) * mm, "end": v(31.37, 9.96) * mm});
            skLineSegment(sketch, "E1782", {"start": v(31.37, 9.96) * mm, "end": v(31.35, 9.95) * mm});
            skLineSegment(sketch, "E1783", {"start": v(31.35, 9.95) * mm, "end": v(31.33, 9.95) * mm});
            skLineSegment(sketch, "E1784", {"start": v(31.33, 9.95) * mm, "end": v(31.31, 9.94) * mm});
            skLineSegment(sketch, "E1785", {"start": v(31.31, 9.94) * mm, "end": v(31.3, 9.94) * mm});
            skLineSegment(sketch, "E1786", {"start": v(31.3, 9.94) * mm, "end": v(31.3, 9.94) * mm});
            skLineSegment(sketch, "E1787", {"start": v(31.3, 9.94) * mm, "end": v(30.9, 9.81) * mm});
            skLineSegment(sketch, "E1788", {"start": v(30.9, 9.81) * mm, "end": v(30.14, 11.96) * mm});
            skLineSegment(sketch, "E1789", {"start": v(30.14, 11.96) * mm, "end": v(30.52, 12.11) * mm});
            skLineSegment(sketch, "E1790", {"start": v(30.52, 12.11) * mm, "end": v(30.52, 12.11) * mm});
            skLineSegment(sketch, "E1791", {"start": v(30.52, 12.11) * mm, "end": v(30.54, 12.12) * mm});
            skLineSegment(sketch, "E1792", {"start": v(30.54, 12.12) * mm, "end": v(30.55, 12.13) * mm});
            skLineSegment(sketch, "E1793", {"start": v(30.55, 12.13) * mm, "end": v(30.57, 12.13) * mm});
            skLineSegment(sketch, "E1794", {"start": v(30.57, 12.13) * mm, "end": v(30.59, 12.14) * mm});
            skLineSegment(sketch, "E1795", {"start": v(30.59, 12.14) * mm, "end": v(30.61, 12.16) * mm});
            skLineSegment(sketch, "E1796", {"start": v(30.61, 12.16) * mm, "end": v(30.64, 12.17) * mm});
            skLineSegment(sketch, "E1797", {"start": v(30.64, 12.17) * mm, "end": v(30.67, 12.19) * mm});
            skLineSegment(sketch, "E1798", {"start": v(30.67, 12.19) * mm, "end": v(30.7, 12.2) * mm});
            skLineSegment(sketch, "E1799", {"start": v(30.7, 12.2) * mm, "end": v(30.75, 12.23) * mm});
            skLineSegment(sketch, "E1800", {"start": v(30.75, 12.23) * mm, "end": v(30.79, 12.25) * mm});
            skLineSegment(sketch, "E1801", {"start": v(30.79, 12.25) * mm, "end": v(30.83, 12.27) * mm});
            skLineSegment(sketch, "E1802", {"start": v(30.83, 12.27) * mm, "end": v(30.88, 12.3) * mm});
            skLineSegment(sketch, "E1803", {"start": v(30.88, 12.3) * mm, "end": v(30.93, 12.33) * mm});
            skLineSegment(sketch, "E1804", {"start": v(30.93, 12.33) * mm, "end": v(30.98, 12.37) * mm});
            skLineSegment(sketch, "E1805", {"start": v(30.98, 12.37) * mm, "end": v(31.04, 12.4) * mm});
            skLineSegment(sketch, "E1806", {"start": v(31.04, 12.4) * mm, "end": v(31.1, 12.44) * mm});
            skLineSegment(sketch, "E1807", {"start": v(31.1, 12.44) * mm, "end": v(31.16, 12.48) * mm});
            skLineSegment(sketch, "E1808", {"start": v(31.16, 12.48) * mm, "end": v(31.23, 12.53) * mm});
            skLineSegment(sketch, "E1809", {"start": v(31.23, 12.53) * mm, "end": v(31.3, 12.57) * mm});
            skLineSegment(sketch, "E1810", {"start": v(31.3, 12.57) * mm, "end": v(31.36, 12.62) * mm});
            skLineSegment(sketch, "E1811", {"start": v(31.36, 12.62) * mm, "end": v(31.44, 12.68) * mm});
            skLineSegment(sketch, "E1812", {"start": v(31.44, 12.68) * mm, "end": v(31.51, 12.73) * mm});
            skLineSegment(sketch, "E1813", {"start": v(31.51, 12.73) * mm, "end": v(31.6, 12.8) * mm});
            skLineSegment(sketch, "E1814", {"start": v(31.6, 12.8) * mm, "end": v(31.67, 12.85) * mm});
            skLineSegment(sketch, "E1815", {"start": v(31.67, 12.85) * mm, "end": v(31.75, 12.92) * mm});
            skLineSegment(sketch, "E1816", {"start": v(31.75, 12.92) * mm, "end": v(31.84, 12.99) * mm});
            skLineSegment(sketch, "E1817", {"start": v(31.84, 12.99) * mm, "end": v(31.93, 13.06) * mm});
            skLineSegment(sketch, "E1818", {"start": v(31.93, 13.06) * mm, "end": v(32.02, 13.14) * mm});
            skLineSegment(sketch, "E1819", {"start": v(32.02, 13.14) * mm, "end": v(32.1, 13.22) * mm});
            skLineSegment(sketch, "E1820", {"start": v(32.1, 13.22) * mm, "end": v(32.2, 13.3) * mm});
            skLineSegment(sketch, "E1821", {"start": v(32.2, 13.3) * mm, "end": v(32.3, 13.39) * mm});
            skLineSegment(sketch, "E1822", {"start": v(32.3, 13.39) * mm, "end": v(32.4, 13.48) * mm});
            skLineSegment(sketch, "E1823", {"start": v(32.4, 13.48) * mm, "end": v(32.5, 13.57) * mm});
            skLineSegment(sketch, "E1824", {"start": v(32.5, 13.57) * mm, "end": v(32.6, 13.67) * mm});
            skLineSegment(sketch, "E1825", {"start": v(32.6, 13.67) * mm, "end": v(32.7, 13.77) * mm});
            skLineSegment(sketch, "E1826", {"start": v(32.7, 13.77) * mm, "end": v(32.8, 13.88) * mm});
            skLineSegment(sketch, "E1827", {"start": v(32.8, 13.88) * mm, "end": v(32.9, 14) * mm});
            skLineSegment(sketch, "E1828", {"start": v(32.9, 14) * mm, "end": v(33.02, 14.1) * mm});
            skLineSegment(sketch, "E1829", {"start": v(33.02, 14.1) * mm, "end": v(33.12, 14.22) * mm});
            skLineSegment(sketch, "E1830", {"start": v(33.12, 14.22) * mm, "end": v(33.23, 14.35) * mm});
            skLineSegment(sketch, "E1831", {"start": v(33.23, 14.35) * mm, "end": v(33.35, 14.47) * mm});
            skLineSegment(sketch, "E1832", {"start": v(33.35, 14.47) * mm, "end": v(33.46, 14.6) * mm});
            skLineSegment(sketch, "E1833", {"start": v(33.46, 14.6) * mm, "end": v(33.57, 14.74) * mm});
            skLineSegment(sketch, "E1834", {"start": v(33.57, 14.74) * mm, "end": v(33.69, 14.88) * mm});
            skLineSegment(sketch, "E1835", {"start": v(33.69, 14.88) * mm, "end": v(33.8, 15.02) * mm});
            skLineSegment(sketch, "E1836", {"start": v(33.8, 15.02) * mm, "end": v(33.88, 15.15) * mm});
            skLineSegment(sketch, "E1837", {"start": v(33.88, 15.15) * mm, "end": v(33.24, 16.52) * mm});
            skLineSegment(sketch, "E1838", {"start": v(33.24, 16.52) * mm, "end": v(33.08, 16.54) * mm});
            skLineSegment(sketch, "E1839", {"start": v(33.08, 16.54) * mm, "end": v(32.9, 16.54) * mm});
            skLineSegment(sketch, "E1840", {"start": v(32.9, 16.54) * mm, "end": v(32.72, 16.54) * mm});
            skLineSegment(sketch, "E1841", {"start": v(32.72, 16.54) * mm, "end": v(32.54, 16.54) * mm});
            skLineSegment(sketch, "E1842", {"start": v(32.54, 16.54) * mm, "end": v(32.37, 16.53) * mm});
            skLineSegment(sketch, "E1843", {"start": v(32.37, 16.53) * mm, "end": v(32.2, 16.53) * mm});
            skLineSegment(sketch, "E1844", {"start": v(32.2, 16.53) * mm, "end": v(32.04, 16.52) * mm});
            skLineSegment(sketch, "E1845", {"start": v(32.04, 16.52) * mm, "end": v(31.88, 16.51) * mm});
            skLineSegment(sketch, "E1846", {"start": v(31.88, 16.51) * mm, "end": v(31.72, 16.5) * mm});
            skLineSegment(sketch, "E1847", {"start": v(31.72, 16.5) * mm, "end": v(31.57, 16.49) * mm});
            skLineSegment(sketch, "E1848", {"start": v(31.57, 16.49) * mm, "end": v(31.42, 16.48) * mm});
            skLineSegment(sketch, "E1849", {"start": v(31.42, 16.48) * mm, "end": v(31.28, 16.46) * mm});
            skLineSegment(sketch, "E1850", {"start": v(31.28, 16.46) * mm, "end": v(31.14, 16.45) * mm});
            skLineSegment(sketch, "E1851", {"start": v(31.14, 16.45) * mm, "end": v(31, 16.43) * mm});
            skLineSegment(sketch, "E1852", {"start": v(31, 16.43) * mm, "end": v(30.87, 16.41) * mm});
            skLineSegment(sketch, "E1853", {"start": v(30.87, 16.41) * mm, "end": v(30.74, 16.4) * mm});
            skLineSegment(sketch, "E1854", {"start": v(30.74, 16.4) * mm, "end": v(30.62, 16.37) * mm});
            skLineSegment(sketch, "E1855", {"start": v(30.62, 16.37) * mm, "end": v(30.5, 16.36) * mm});
            skLineSegment(sketch, "E1856", {"start": v(30.5, 16.36) * mm, "end": v(30.38, 16.33) * mm});
            skLineSegment(sketch, "E1857", {"start": v(30.38, 16.33) * mm, "end": v(30.27, 16.31) * mm});
            skLineSegment(sketch, "E1858", {"start": v(30.27, 16.31) * mm, "end": v(30.16, 16.3) * mm});
            skLineSegment(sketch, "E1859", {"start": v(30.16, 16.3) * mm, "end": v(30.06, 16.27) * mm});
            skLineSegment(sketch, "E1860", {"start": v(30.06, 16.27) * mm, "end": v(29.96, 16.25) * mm});
            skLineSegment(sketch, "E1861", {"start": v(29.96, 16.25) * mm, "end": v(29.86, 16.23) * mm});
            skLineSegment(sketch, "E1862", {"start": v(29.86, 16.23) * mm, "end": v(29.77, 16.2) * mm});
            skLineSegment(sketch, "E1863", {"start": v(29.77, 16.2) * mm, "end": v(29.69, 16.18) * mm});
            skLineSegment(sketch, "E1864", {"start": v(29.69, 16.18) * mm, "end": v(29.6, 16.16) * mm});
            skLineSegment(sketch, "E1865", {"start": v(29.6, 16.16) * mm, "end": v(29.52, 16.14) * mm});
            skLineSegment(sketch, "E1866", {"start": v(29.52, 16.14) * mm, "end": v(29.45, 16.11) * mm});
            skLineSegment(sketch, "E1867", {"start": v(29.45, 16.11) * mm, "end": v(29.38, 16.1) * mm});
            skLineSegment(sketch, "E1868", {"start": v(29.38, 16.1) * mm, "end": v(29.3, 16.07) * mm});
            skLineSegment(sketch, "E1869", {"start": v(29.3, 16.07) * mm, "end": v(29.25, 16.05) * mm});
            skLineSegment(sketch, "E1870", {"start": v(29.25, 16.05) * mm, "end": v(29.19, 16.03) * mm});
            skLineSegment(sketch, "E1871", {"start": v(29.19, 16.03) * mm, "end": v(29.13, 16.01) * mm});
            skLineSegment(sketch, "E1872", {"start": v(29.13, 16.01) * mm, "end": v(29.08, 16) * mm});
            skLineSegment(sketch, "E1873", {"start": v(29.08, 16) * mm, "end": v(29.03, 15.97) * mm});
            skLineSegment(sketch, "E1874", {"start": v(29.03, 15.97) * mm, "end": v(28.99, 15.96) * mm});
            skLineSegment(sketch, "E1875", {"start": v(28.99, 15.96) * mm, "end": v(28.95, 15.94) * mm});
            skLineSegment(sketch, "E1876", {"start": v(28.95, 15.94) * mm, "end": v(28.91, 15.92) * mm});
            skLineSegment(sketch, "E1877", {"start": v(28.91, 15.92) * mm, "end": v(28.88, 15.91) * mm});
            skLineSegment(sketch, "E1878", {"start": v(28.88, 15.91) * mm, "end": v(28.85, 15.9) * mm});
            skLineSegment(sketch, "E1879", {"start": v(28.85, 15.9) * mm, "end": v(28.82, 15.89) * mm});
            skLineSegment(sketch, "E1880", {"start": v(28.82, 15.89) * mm, "end": v(28.8, 15.88) * mm});
            skLineSegment(sketch, "E1881", {"start": v(28.8, 15.88) * mm, "end": v(28.78, 15.87) * mm});
            skLineSegment(sketch, "E1882", {"start": v(28.78, 15.87) * mm, "end": v(28.77, 15.86) * mm});
            skLineSegment(sketch, "E1883", {"start": v(28.77, 15.86) * mm, "end": v(28.76, 15.86) * mm});
            skLineSegment(sketch, "E1884", {"start": v(28.76, 15.86) * mm, "end": v(28.75, 15.85) * mm});
            skLineSegment(sketch, "E1885", {"start": v(28.75, 15.85) * mm, "end": v(28.4, 15.65) * mm});
            skLineSegment(sketch, "E1886", {"start": v(28.4, 15.65) * mm, "end": v(27.22, 17.6) * mm});
            skLineSegment(sketch, "E1887", {"start": v(27.22, 17.6) * mm, "end": v(27.57, 17.83) * mm});
            skLineSegment(sketch, "E1888", {"start": v(27.57, 17.83) * mm, "end": v(27.57, 17.84) * mm});
            skLineSegment(sketch, "E1889", {"start": v(27.57, 17.84) * mm, "end": v(27.58, 17.84) * mm});
            skLineSegment(sketch, "E1890", {"start": v(27.58, 17.84) * mm, "end": v(27.6, 17.85) * mm});
            skLineSegment(sketch, "E1891", {"start": v(27.6, 17.85) * mm, "end": v(27.61, 17.86) * mm});
            skLineSegment(sketch, "E1892", {"start": v(27.61, 17.86) * mm, "end": v(27.63, 17.88) * mm});
            skLineSegment(sketch, "E1893", {"start": v(27.63, 17.88) * mm, "end": v(27.65, 17.9) * mm});
            skLineSegment(sketch, "E1894", {"start": v(27.65, 17.9) * mm, "end": v(27.68, 17.91) * mm});
            skLineSegment(sketch, "E1895", {"start": v(27.68, 17.91) * mm, "end": v(27.7, 17.94) * mm});
            skLineSegment(sketch, "E1896", {"start": v(27.7, 17.94) * mm, "end": v(27.74, 17.96) * mm});
            skLineSegment(sketch, "E1897", {"start": v(27.74, 17.96) * mm, "end": v(27.77, 17.99) * mm});
            skLineSegment(sketch, "E1898", {"start": v(27.77, 17.99) * mm, "end": v(27.8, 18.02) * mm});
            skLineSegment(sketch, "E1899", {"start": v(27.8, 18.02) * mm, "end": v(27.85, 18.05) * mm});
            skLineSegment(sketch, "E1900", {"start": v(27.85, 18.05) * mm, "end": v(27.89, 18.1) * mm});
            skLineSegment(sketch, "E1901", {"start": v(27.89, 18.1) * mm, "end": v(27.93, 18.13) * mm});
            skLineSegment(sketch, "E1902", {"start": v(27.93, 18.13) * mm, "end": v(27.98, 18.17) * mm});
            skLineSegment(sketch, "E1903", {"start": v(27.98, 18.17) * mm, "end": v(28.02, 18.22) * mm});
            skLineSegment(sketch, "E1904", {"start": v(28.02, 18.22) * mm, "end": v(28.08, 18.27) * mm});
            skLineSegment(sketch, "E1905", {"start": v(28.08, 18.27) * mm, "end": v(28.13, 18.32) * mm});
            skLineSegment(sketch, "E1906", {"start": v(28.13, 18.32) * mm, "end": v(28.18, 18.38) * mm});
            skLineSegment(sketch, "E1907", {"start": v(28.18, 18.38) * mm, "end": v(28.24, 18.44) * mm});
            skLineSegment(sketch, "E1908", {"start": v(28.24, 18.44) * mm, "end": v(28.3, 18.5) * mm});
            skLineSegment(sketch, "E1909", {"start": v(28.3, 18.5) * mm, "end": v(28.36, 18.57) * mm});
            skLineSegment(sketch, "E1910", {"start": v(28.36, 18.57) * mm, "end": v(28.42, 18.64) * mm});
            skLineSegment(sketch, "E1911", {"start": v(28.42, 18.64) * mm, "end": v(28.49, 18.7) * mm});
            skLineSegment(sketch, "E1912", {"start": v(28.49, 18.7) * mm, "end": v(28.56, 18.79) * mm});
            skLineSegment(sketch, "E1913", {"start": v(28.56, 18.79) * mm, "end": v(28.62, 18.87) * mm});
            skLineSegment(sketch, "E1914", {"start": v(28.62, 18.87) * mm, "end": v(28.7, 18.95) * mm});
            skLineSegment(sketch, "E1915", {"start": v(28.7, 18.95) * mm, "end": v(28.76, 19.04) * mm});
            skLineSegment(sketch, "E1916", {"start": v(28.76, 19.04) * mm, "end": v(28.84, 19.13) * mm});
            skLineSegment(sketch, "E1917", {"start": v(28.84, 19.13) * mm, "end": v(28.91, 19.23) * mm});
            skLineSegment(sketch, "E1918", {"start": v(28.91, 19.23) * mm, "end": v(28.99, 19.33) * mm});
            skLineSegment(sketch, "E1919", {"start": v(28.99, 19.33) * mm, "end": v(29.06, 19.43) * mm});
            skLineSegment(sketch, "E1920", {"start": v(29.06, 19.43) * mm, "end": v(29.14, 19.54) * mm});
            skLineSegment(sketch, "E1921", {"start": v(29.14, 19.54) * mm, "end": v(29.22, 19.65) * mm});
            skLineSegment(sketch, "E1922", {"start": v(29.22, 19.65) * mm, "end": v(29.3, 19.77) * mm});
            skLineSegment(sketch, "E1923", {"start": v(29.3, 19.77) * mm, "end": v(29.38, 19.89) * mm});
            skLineSegment(sketch, "E1924", {"start": v(29.38, 19.89) * mm, "end": v(29.46, 20.01) * mm});
            skLineSegment(sketch, "E1925", {"start": v(29.46, 20.01) * mm, "end": v(29.55, 20.14) * mm});
            skLineSegment(sketch, "E1926", {"start": v(29.55, 20.14) * mm, "end": v(29.63, 20.27) * mm});
            skLineSegment(sketch, "E1927", {"start": v(29.63, 20.27) * mm, "end": v(29.71, 20.41) * mm});
            skLineSegment(sketch, "E1928", {"start": v(29.71, 20.41) * mm, "end": v(29.8, 20.55) * mm});
            skLineSegment(sketch, "E1929", {"start": v(29.8, 20.55) * mm, "end": v(29.88, 20.7) * mm});
            skLineSegment(sketch, "E1930", {"start": v(29.88, 20.7) * mm, "end": v(29.97, 20.85) * mm});
            skLineSegment(sketch, "E1931", {"start": v(29.97, 20.85) * mm, "end": v(30.05, 21) * mm});
            skLineSegment(sketch, "E1932", {"start": v(30.05, 21) * mm, "end": v(30.14, 21.16) * mm});
            skLineSegment(sketch, "E1933", {"start": v(30.14, 21.16) * mm, "end": v(30.22, 21.32) * mm});
            skLineSegment(sketch, "E1934", {"start": v(30.22, 21.32) * mm, "end": v(30.28, 21.47) * mm});
            skLineSegment(sketch, "E1935", {"start": v(30.28, 21.47) * mm, "end": v(29.38, 22.68) * mm});
            skLineSegment(sketch, "E1936", {"start": v(29.38, 22.68) * mm, "end": v(29.22, 22.67) * mm});
            skLineSegment(sketch, "E1937", {"start": v(29.22, 22.67) * mm, "end": v(29.04, 22.64) * mm});
            skLineSegment(sketch, "E1938", {"start": v(29.04, 22.64) * mm, "end": v(28.87, 22.6) * mm});
            skLineSegment(sketch, "E1939", {"start": v(28.87, 22.6) * mm, "end": v(28.7, 22.57) * mm});
            skLineSegment(sketch, "E1940", {"start": v(28.7, 22.57) * mm, "end": v(28.52, 22.53) * mm});
            skLineSegment(sketch, "E1941", {"start": v(28.52, 22.53) * mm, "end": v(28.36, 22.5) * mm});
            skLineSegment(sketch, "E1942", {"start": v(28.36, 22.5) * mm, "end": v(28.2, 22.45) * mm});
            skLineSegment(sketch, "E1943", {"start": v(28.2, 22.45) * mm, "end": v(28.05, 22.41) * mm});
            skLineSegment(sketch, "E1944", {"start": v(28.05, 22.41) * mm, "end": v(27.9, 22.37) * mm});
            skLineSegment(sketch, "E1945", {"start": v(27.9, 22.37) * mm, "end": v(27.75, 22.33) * mm});
            skLineSegment(sketch, "E1946", {"start": v(27.75, 22.33) * mm, "end": v(27.6, 22.3) * mm});
            skLineSegment(sketch, "E1947", {"start": v(27.6, 22.3) * mm, "end": v(27.47, 22.25) * mm});
            skLineSegment(sketch, "E1948", {"start": v(27.47, 22.25) * mm, "end": v(27.33, 22.2) * mm});
            skLineSegment(sketch, "E1949", {"start": v(27.33, 22.2) * mm, "end": v(27.2, 22.16) * mm});
            skLineSegment(sketch, "E1950", {"start": v(27.2, 22.16) * mm, "end": v(27.08, 22.12) * mm});
            skLineSegment(sketch, "E1951", {"start": v(27.08, 22.12) * mm, "end": v(26.95, 22.08) * mm});
            skLineSegment(sketch, "E1952", {"start": v(26.95, 22.08) * mm, "end": v(26.84, 22.03) * mm});
            skLineSegment(sketch, "E1953", {"start": v(26.84, 22.03) * mm, "end": v(26.72, 22) * mm});
            skLineSegment(sketch, "E1954", {"start": v(26.72, 22) * mm, "end": v(26.61, 21.95) * mm});
            skLineSegment(sketch, "E1955", {"start": v(26.61, 21.95) * mm, "end": v(26.5, 21.9) * mm});
            skLineSegment(sketch, "E1956", {"start": v(26.5, 21.9) * mm, "end": v(26.4, 21.86) * mm});
            skLineSegment(sketch, "E1957", {"start": v(26.4, 21.86) * mm, "end": v(26.3, 21.82) * mm});
            skLineSegment(sketch, "E1958", {"start": v(26.3, 21.82) * mm, "end": v(26.21, 21.78) * mm});
            skLineSegment(sketch, "E1959", {"start": v(26.21, 21.78) * mm, "end": v(26.13, 21.74) * mm});
            skLineSegment(sketch, "E1960", {"start": v(26.13, 21.74) * mm, "end": v(26.04, 21.7) * mm});
            skLineSegment(sketch, "E1961", {"start": v(26.04, 21.7) * mm, "end": v(25.96, 21.66) * mm});
            skLineSegment(sketch, "E1962", {"start": v(25.96, 21.66) * mm, "end": v(25.88, 21.62) * mm});
            skLineSegment(sketch, "E1963", {"start": v(25.88, 21.62) * mm, "end": v(25.8, 21.59) * mm});
            skLineSegment(sketch, "E1964", {"start": v(25.8, 21.59) * mm, "end": v(25.74, 21.55) * mm});
            skLineSegment(sketch, "E1965", {"start": v(25.74, 21.55) * mm, "end": v(25.67, 21.51) * mm});
            skLineSegment(sketch, "E1966", {"start": v(25.67, 21.51) * mm, "end": v(25.61, 21.48) * mm});
            skLineSegment(sketch, "E1967", {"start": v(25.61, 21.48) * mm, "end": v(25.55, 21.45) * mm});
            skLineSegment(sketch, "E1968", {"start": v(25.55, 21.45) * mm, "end": v(25.5, 21.42) * mm});
            skLineSegment(sketch, "E1969", {"start": v(25.5, 21.42) * mm, "end": v(25.45, 21.39) * mm});
            skLineSegment(sketch, "E1970", {"start": v(25.45, 21.39) * mm, "end": v(25.4, 21.36) * mm});
            skLineSegment(sketch, "E1971", {"start": v(25.4, 21.36) * mm, "end": v(25.36, 21.33) * mm});
            skLineSegment(sketch, "E1972", {"start": v(25.36, 21.33) * mm, "end": v(25.32, 21.3) * mm});
            skLineSegment(sketch, "E1973", {"start": v(25.32, 21.3) * mm, "end": v(25.28, 21.28) * mm});
            skLineSegment(sketch, "E1974", {"start": v(25.28, 21.28) * mm, "end": v(25.25, 21.26) * mm});
            skLineSegment(sketch, "E1975", {"start": v(25.25, 21.26) * mm, "end": v(25.22, 21.24) * mm});
            skLineSegment(sketch, "E1976", {"start": v(25.22, 21.24) * mm, "end": v(25.2, 21.22) * mm});
            skLineSegment(sketch, "E1977", {"start": v(25.2, 21.22) * mm, "end": v(25.17, 21.2) * mm});
            skLineSegment(sketch, "E1978", {"start": v(25.17, 21.2) * mm, "end": v(25.15, 21.2) * mm});
            skLineSegment(sketch, "E1979", {"start": v(25.15, 21.2) * mm, "end": v(25.14, 21.18) * mm});
            skLineSegment(sketch, "E1980", {"start": v(25.14, 21.18) * mm, "end": v(25.12, 21.17) * mm});
            skLineSegment(sketch, "E1981", {"start": v(25.12, 21.17) * mm, "end": v(25.11, 21.16) * mm});
            skLineSegment(sketch, "E1982", {"start": v(25.11, 21.16) * mm, "end": v(25.1, 21.16) * mm});
            skLineSegment(sketch, "E1983", {"start": v(25.1, 21.16) * mm, "end": v(24.8, 20.9) * mm});
            skLineSegment(sketch, "E1984", {"start": v(24.8, 20.9) * mm, "end": v(23.27, 22.58) * mm});
            skLineSegment(sketch, "E1985", {"start": v(23.27, 22.58) * mm, "end": v(23.56, 22.87) * mm});
            skLineSegment(sketch, "E1986", {"start": v(23.56, 22.87) * mm, "end": v(23.56, 22.87) * mm});
            skLineSegment(sketch, "E1987", {"start": v(23.56, 22.87) * mm, "end": v(23.57, 22.88) * mm});
            skLineSegment(sketch, "E1988", {"start": v(23.57, 22.88) * mm, "end": v(23.58, 22.9) * mm});
            skLineSegment(sketch, "E1989", {"start": v(23.58, 22.9) * mm, "end": v(23.6, 22.9) * mm});
            skLineSegment(sketch, "E1990", {"start": v(23.6, 22.9) * mm, "end": v(23.61, 22.93) * mm});
            skLineSegment(sketch, "E1991", {"start": v(23.61, 22.93) * mm, "end": v(23.63, 22.95) * mm});
            skLineSegment(sketch, "E1992", {"start": v(23.63, 22.95) * mm, "end": v(23.65, 22.97) * mm});
            skLineSegment(sketch, "E1993", {"start": v(23.65, 22.97) * mm, "end": v(23.68, 23) * mm});
            skLineSegment(sketch, "E1994", {"start": v(23.68, 23) * mm, "end": v(23.7, 23.03) * mm});
            skLineSegment(sketch, "E1995", {"start": v(23.7, 23.03) * mm, "end": v(23.73, 23.06) * mm});
            skLineSegment(sketch, "E1996", {"start": v(23.73, 23.06) * mm, "end": v(23.76, 23.1) * mm});
            skLineSegment(sketch, "E1997", {"start": v(23.76, 23.1) * mm, "end": v(23.79, 23.14) * mm});
            skLineSegment(sketch, "E1998", {"start": v(23.79, 23.14) * mm, "end": v(23.82, 23.18) * mm});
            skLineSegment(sketch, "E1999", {"start": v(23.82, 23.18) * mm, "end": v(23.86, 23.23) * mm});
            skLineSegment(sketch, "E2000", {"start": v(23.86, 23.23) * mm, "end": v(23.9, 23.28) * mm});
            skLineSegment(sketch, "E2001", {"start": v(23.9, 23.28) * mm, "end": v(23.93, 23.34) * mm});
            skLineSegment(sketch, "E2002", {"start": v(23.93, 23.34) * mm, "end": v(23.97, 23.4) * mm});
            skLineSegment(sketch, "E2003", {"start": v(23.97, 23.4) * mm, "end": v(24.01, 23.46) * mm});
            skLineSegment(sketch, "E2004", {"start": v(24.01, 23.46) * mm, "end": v(24.06, 23.52) * mm});
            skLineSegment(sketch, "E2005", {"start": v(24.06, 23.52) * mm, "end": v(24.1, 23.6) * mm});
            skLineSegment(sketch, "E2006", {"start": v(24.1, 23.6) * mm, "end": v(24.15, 23.66) * mm});
            skLineSegment(sketch, "E2007", {"start": v(24.15, 23.66) * mm, "end": v(24.2, 23.74) * mm});
            skLineSegment(sketch, "E2008", {"start": v(24.2, 23.74) * mm, "end": v(24.24, 23.82) * mm});
            skLineSegment(sketch, "E2009", {"start": v(24.24, 23.82) * mm, "end": v(24.3, 23.9) * mm});
            skLineSegment(sketch, "E2010", {"start": v(24.3, 23.9) * mm, "end": v(24.34, 24) * mm});
            skLineSegment(sketch, "E2011", {"start": v(24.34, 24) * mm, "end": v(24.4, 24.09) * mm});
            skLineSegment(sketch, "E2012", {"start": v(24.4, 24.09) * mm, "end": v(24.44, 24.19) * mm});
            skLineSegment(sketch, "E2013", {"start": v(24.44, 24.19) * mm, "end": v(24.5, 24.29) * mm});
            skLineSegment(sketch, "E2014", {"start": v(24.5, 24.29) * mm, "end": v(24.55, 24.4) * mm});
            skLineSegment(sketch, "E2015", {"start": v(24.55, 24.4) * mm, "end": v(24.6, 24.5) * mm});
            skLineSegment(sketch, "E2016", {"start": v(24.6, 24.5) * mm, "end": v(24.66, 24.61) * mm});
            skLineSegment(sketch, "E2017", {"start": v(24.66, 24.61) * mm, "end": v(24.71, 24.73) * mm});
            skLineSegment(sketch, "E2018", {"start": v(24.71, 24.73) * mm, "end": v(24.77, 24.85) * mm});
            skLineSegment(sketch, "E2019", {"start": v(24.77, 24.85) * mm, "end": v(24.83, 24.98) * mm});
            skLineSegment(sketch, "E2020", {"start": v(24.83, 24.98) * mm, "end": v(24.88, 25.1) * mm});
            skLineSegment(sketch, "E2021", {"start": v(24.88, 25.1) * mm, "end": v(24.94, 25.24) * mm});
            skLineSegment(sketch, "E2022", {"start": v(24.94, 25.24) * mm, "end": v(25, 25.38) * mm});
            skLineSegment(sketch, "E2023", {"start": v(25, 25.38) * mm, "end": v(25.05, 25.52) * mm});
            skLineSegment(sketch, "E2024", {"start": v(25.05, 25.52) * mm, "end": v(25.1, 25.67) * mm});
            skLineSegment(sketch, "E2025", {"start": v(25.1, 25.67) * mm, "end": v(25.16, 25.82) * mm});
            skLineSegment(sketch, "E2026", {"start": v(25.16, 25.82) * mm, "end": v(25.21, 25.97) * mm});
            skLineSegment(sketch, "E2027", {"start": v(25.21, 25.97) * mm, "end": v(25.27, 26.13) * mm});
            skLineSegment(sketch, "E2028", {"start": v(25.27, 26.13) * mm, "end": v(25.32, 26.3) * mm});
            skLineSegment(sketch, "E2029", {"start": v(25.32, 26.3) * mm, "end": v(25.38, 26.46) * mm});
            skLineSegment(sketch, "E2030", {"start": v(25.38, 26.46) * mm, "end": v(25.43, 26.63) * mm});
            skLineSegment(sketch, "E2031", {"start": v(25.43, 26.63) * mm, "end": v(25.48, 26.81) * mm});
            skLineSegment(sketch, "E2032", {"start": v(25.48, 26.81) * mm, "end": v(25.5, 26.96) * mm});
            skLineSegment(sketch, "E2033", {"start": v(25.5, 26.96) * mm, "end": v(24.39, 27.98) * mm});
            skLineSegment(sketch, "E2034", {"start": v(24.39, 27.98) * mm, "end": v(24.24, 27.94) * mm});
            skLineSegment(sketch, "E2035", {"start": v(24.24, 27.94) * mm, "end": v(24.07, 27.87) * mm});
            skLineSegment(sketch, "E2036", {"start": v(24.07, 27.87) * mm, "end": v(23.9, 27.8) * mm});
            skLineSegment(sketch, "E2037", {"start": v(23.9, 27.8) * mm, "end": v(23.74, 27.73) * mm});
            skLineSegment(sketch, "E2038", {"start": v(23.74, 27.73) * mm, "end": v(23.58, 27.66) * mm});
            skLineSegment(sketch, "E2039", {"start": v(23.58, 27.66) * mm, "end": v(23.43, 27.6) * mm});
            skLineSegment(sketch, "E2040", {"start": v(23.43, 27.6) * mm, "end": v(23.28, 27.52) * mm});
            skLineSegment(sketch, "E2041", {"start": v(23.28, 27.52) * mm, "end": v(23.13, 27.45) * mm});
            skLineSegment(sketch, "E2042", {"start": v(23.13, 27.45) * mm, "end": v(23, 27.39) * mm});
            skLineSegment(sketch, "E2043", {"start": v(23, 27.39) * mm, "end": v(22.86, 27.32) * mm});
            skLineSegment(sketch, "E2044", {"start": v(22.86, 27.32) * mm, "end": v(22.73, 27.25) * mm});
            skLineSegment(sketch, "E2045", {"start": v(22.73, 27.25) * mm, "end": v(22.6, 27.18) * mm});
            skLineSegment(sketch, "E2046", {"start": v(22.6, 27.18) * mm, "end": v(22.47, 27.11) * mm});
            skLineSegment(sketch, "E2047", {"start": v(22.47, 27.11) * mm, "end": v(22.35, 27.04) * mm});
            skLineSegment(sketch, "E2048", {"start": v(22.35, 27.04) * mm, "end": v(22.24, 26.98) * mm});
            skLineSegment(sketch, "E2049", {"start": v(22.24, 26.98) * mm, "end": v(22.13, 26.91) * mm});
            skLineSegment(sketch, "E2050", {"start": v(22.13, 26.91) * mm, "end": v(22.02, 26.85) * mm});
            skLineSegment(sketch, "E2051", {"start": v(22.02, 26.85) * mm, "end": v(21.92, 26.78) * mm});
            skLineSegment(sketch, "E2052", {"start": v(21.92, 26.78) * mm, "end": v(21.82, 26.72) * mm});
            skLineSegment(sketch, "E2053", {"start": v(21.82, 26.72) * mm, "end": v(21.72, 26.66) * mm});
            skLineSegment(sketch, "E2054", {"start": v(21.72, 26.66) * mm, "end": v(21.63, 26.6) * mm});
            skLineSegment(sketch, "E2055", {"start": v(21.63, 26.6) * mm, "end": v(21.55, 26.53) * mm});
            skLineSegment(sketch, "E2056", {"start": v(21.55, 26.53) * mm, "end": v(21.46, 26.48) * mm});
            skLineSegment(sketch, "E2057", {"start": v(21.46, 26.48) * mm, "end": v(21.38, 26.42) * mm});
            skLineSegment(sketch, "E2058", {"start": v(21.38, 26.42) * mm, "end": v(21.3, 26.36) * mm});
            skLineSegment(sketch, "E2059", {"start": v(21.3, 26.36) * mm, "end": v(21.23, 26.3) * mm});
            skLineSegment(sketch, "E2060", {"start": v(21.23, 26.3) * mm, "end": v(21.17, 26.26) * mm});
            skLineSegment(sketch, "E2061", {"start": v(21.17, 26.26) * mm, "end": v(21.1, 26.2) * mm});
            skLineSegment(sketch, "E2062", {"start": v(21.1, 26.2) * mm, "end": v(21.04, 26.16) * mm});
            skLineSegment(sketch, "E2063", {"start": v(21.04, 26.16) * mm, "end": v(20.98, 26.1) * mm});
            skLineSegment(sketch, "E2064", {"start": v(20.98, 26.1) * mm, "end": v(20.93, 26.06) * mm});
            skLineSegment(sketch, "E2065", {"start": v(20.93, 26.06) * mm, "end": v(20.88, 26.02) * mm});
            skLineSegment(sketch, "E2066", {"start": v(20.88, 26.02) * mm, "end": v(20.83, 25.98) * mm});
            skLineSegment(sketch, "E2067", {"start": v(20.83, 25.98) * mm, "end": v(20.79, 25.94) * mm});
            skLineSegment(sketch, "E2068", {"start": v(20.79, 25.94) * mm, "end": v(20.75, 25.9) * mm});
            skLineSegment(sketch, "E2069", {"start": v(20.75, 25.9) * mm, "end": v(20.7, 25.87) * mm});
            skLineSegment(sketch, "E2070", {"start": v(20.7, 25.87) * mm, "end": v(20.67, 25.83) * mm});
            skLineSegment(sketch, "E2071", {"start": v(20.67, 25.83) * mm, "end": v(20.64, 25.8) * mm});
            skLineSegment(sketch, "E2072", {"start": v(20.64, 25.8) * mm, "end": v(20.62, 25.78) * mm});
            skLineSegment(sketch, "E2073", {"start": v(20.62, 25.78) * mm, "end": v(20.6, 25.75) * mm});
            skLineSegment(sketch, "E2074", {"start": v(20.6, 25.75) * mm, "end": v(20.57, 25.73) * mm});
            skLineSegment(sketch, "E2075", {"start": v(20.57, 25.73) * mm, "end": v(20.55, 25.7) * mm});
            skLineSegment(sketch, "E2076", {"start": v(20.55, 25.7) * mm, "end": v(20.53, 25.69) * mm});
            skLineSegment(sketch, "E2077", {"start": v(20.53, 25.69) * mm, "end": v(20.52, 25.67) * mm});
            skLineSegment(sketch, "E2078", {"start": v(20.52, 25.67) * mm, "end": v(20.51, 25.66) * mm});
            skLineSegment(sketch, "E2079", {"start": v(20.51, 25.66) * mm, "end": v(20.5, 25.65) * mm});
            skLineSegment(sketch, "E2080", {"start": v(20.5, 25.65) * mm, "end": v(20.5, 25.65) * mm});
            skLineSegment(sketch, "E2081", {"start": v(20.5, 25.65) * mm, "end": v(20.24, 25.33) * mm});
            skLineSegment(sketch, "E2082", {"start": v(20.24, 25.33) * mm, "end": v(18.41, 26.69) * mm});
            skLineSegment(sketch, "E2083", {"start": v(18.41, 26.69) * mm, "end": v(18.65, 27.02) * mm});
            skLineSegment(sketch, "E2084", {"start": v(18.65, 27.02) * mm, "end": v(18.65, 27.03) * mm});
            skLineSegment(sketch, "E2085", {"start": v(18.65, 27.03) * mm, "end": v(18.66, 27.04) * mm});
            skLineSegment(sketch, "E2086", {"start": v(18.66, 27.04) * mm, "end": v(18.66, 27.05) * mm});
            skLineSegment(sketch, "E2087", {"start": v(18.66, 27.05) * mm, "end": v(18.68, 27.07) * mm});
            skLineSegment(sketch, "E2088", {"start": v(18.68, 27.07) * mm, "end": v(18.69, 27.1) * mm});
            skLineSegment(sketch, "E2089", {"start": v(18.69, 27.1) * mm, "end": v(18.7, 27.12) * mm});
            skLineSegment(sketch, "E2090", {"start": v(18.7, 27.12) * mm, "end": v(18.72, 27.14) * mm});
            skLineSegment(sketch, "E2091", {"start": v(18.72, 27.14) * mm, "end": v(18.73, 27.17) * mm});
            skLineSegment(sketch, "E2092", {"start": v(18.73, 27.17) * mm, "end": v(18.75, 27.2) * mm});
            skLineSegment(sketch, "E2093", {"start": v(18.75, 27.2) * mm, "end": v(18.77, 27.25) * mm});
            skLineSegment(sketch, "E2094", {"start": v(18.77, 27.25) * mm, "end": v(18.8, 27.29) * mm});
            skLineSegment(sketch, "E2095", {"start": v(18.8, 27.29) * mm, "end": v(18.82, 27.34) * mm});
            skLineSegment(sketch, "E2096", {"start": v(18.82, 27.34) * mm, "end": v(18.84, 27.38) * mm});
            skLineSegment(sketch, "E2097", {"start": v(18.84, 27.38) * mm, "end": v(18.87, 27.44) * mm});
            skLineSegment(sketch, "E2098", {"start": v(18.87, 27.44) * mm, "end": v(18.9, 27.5) * mm});
            skLineSegment(sketch, "E2099", {"start": v(18.9, 27.5) * mm, "end": v(18.92, 27.56) * mm});
            skLineSegment(sketch, "E2100", {"start": v(18.92, 27.56) * mm, "end": v(18.95, 27.62) * mm});
            skLineSegment(sketch, "E2101", {"start": v(18.95, 27.62) * mm, "end": v(18.98, 27.7) * mm});
            skLineSegment(sketch, "E2102", {"start": v(18.98, 27.7) * mm, "end": v(19, 27.76) * mm});
            skLineSegment(sketch, "E2103", {"start": v(19, 27.76) * mm, "end": v(19.04, 27.84) * mm});
            skLineSegment(sketch, "E2104", {"start": v(19.04, 27.84) * mm, "end": v(19.07, 27.92) * mm});
            skLineSegment(sketch, "E2105", {"start": v(19.07, 27.92) * mm, "end": v(19.1, 28) * mm});
            skLineSegment(sketch, "E2106", {"start": v(19.1, 28) * mm, "end": v(19.13, 28.1) * mm});
            skLineSegment(sketch, "E2107", {"start": v(19.13, 28.1) * mm, "end": v(19.16, 28.19) * mm});
            skLineSegment(sketch, "E2108", {"start": v(19.16, 28.19) * mm, "end": v(19.2, 28.28) * mm});
            skLineSegment(sketch, "E2109", {"start": v(19.2, 28.28) * mm, "end": v(19.22, 28.38) * mm});
            skLineSegment(sketch, "E2110", {"start": v(19.22, 28.38) * mm, "end": v(19.26, 28.49) * mm});
            skLineSegment(sketch, "E2111", {"start": v(19.26, 28.49) * mm, "end": v(19.29, 28.6) * mm});
            skLineSegment(sketch, "E2112", {"start": v(19.29, 28.6) * mm, "end": v(19.32, 28.71) * mm});
            skLineSegment(sketch, "E2113", {"start": v(19.32, 28.71) * mm, "end": v(19.35, 28.83) * mm});
            skLineSegment(sketch, "E2114", {"start": v(19.35, 28.83) * mm, "end": v(19.38, 28.95) * mm});
            skLineSegment(sketch, "E2115", {"start": v(19.38, 28.95) * mm, "end": v(19.42, 29.08) * mm});
            skLineSegment(sketch, "E2116", {"start": v(19.42, 29.08) * mm, "end": v(19.45, 29.2) * mm});
            skLineSegment(sketch, "E2117", {"start": v(19.45, 29.2) * mm, "end": v(19.48, 29.34) * mm});
            skLineSegment(sketch, "E2118", {"start": v(19.48, 29.34) * mm, "end": v(19.5, 29.48) * mm});
            skLineSegment(sketch, "E2119", {"start": v(19.5, 29.48) * mm, "end": v(19.53, 29.62) * mm});
            skLineSegment(sketch, "E2120", {"start": v(19.53, 29.62) * mm, "end": v(19.56, 29.77) * mm});
            skLineSegment(sketch, "E2121", {"start": v(19.56, 29.77) * mm, "end": v(19.59, 29.92) * mm});
            skLineSegment(sketch, "E2122", {"start": v(19.59, 29.92) * mm, "end": v(19.61, 30.07) * mm});
            skLineSegment(sketch, "E2123", {"start": v(19.61, 30.07) * mm, "end": v(19.64, 30.23) * mm});
            skLineSegment(sketch, "E2124", {"start": v(19.64, 30.23) * mm, "end": v(19.66, 30.4) * mm});
            skLineSegment(sketch, "E2125", {"start": v(19.66, 30.4) * mm, "end": v(19.69, 30.56) * mm});
            skLineSegment(sketch, "E2126", {"start": v(19.69, 30.56) * mm, "end": v(19.7, 30.73) * mm});
            skLineSegment(sketch, "E2127", {"start": v(19.7, 30.73) * mm, "end": v(19.73, 30.9) * mm});
            skLineSegment(sketch, "E2128", {"start": v(19.73, 30.9) * mm, "end": v(19.74, 31.08) * mm});
            skLineSegment(sketch, "E2129", {"start": v(19.74, 31.08) * mm, "end": v(19.76, 31.27) * mm});
            skLineSegment(sketch, "E2130", {"start": v(19.76, 31.27) * mm, "end": v(19.76, 31.42) * mm});
            skLineSegment(sketch, "E2131", {"start": v(19.76, 31.42) * mm, "end": v(18.46, 32.2) * mm});
            skLineSegment(sketch, "E2132", {"start": v(18.46, 32.2) * mm, "end": v(18.32, 32.13) * mm});
            skLineSegment(sketch, "E2133", {"start": v(18.32, 32.13) * mm, "end": v(18.17, 32.03) * mm});
            skLineSegment(sketch, "E2134", {"start": v(18.17, 32.03) * mm, "end": v(18.02, 31.93) * mm});
            skLineSegment(sketch, "E2135", {"start": v(18.02, 31.93) * mm, "end": v(17.87, 31.83) * mm});
            skLineSegment(sketch, "E2136", {"start": v(17.87, 31.83) * mm, "end": v(17.73, 31.73) * mm});
            skLineSegment(sketch, "E2137", {"start": v(17.73, 31.73) * mm, "end": v(17.6, 31.63) * mm});
            skLineSegment(sketch, "E2138", {"start": v(17.6, 31.63) * mm, "end": v(17.46, 31.54) * mm});
            skLineSegment(sketch, "E2139", {"start": v(17.46, 31.54) * mm, "end": v(17.33, 31.44) * mm});
            skLineSegment(sketch, "E2140", {"start": v(17.33, 31.44) * mm, "end": v(17.2, 31.34) * mm});
            skLineSegment(sketch, "E2141", {"start": v(17.2, 31.34) * mm, "end": v(17.09, 31.25) * mm});
            skLineSegment(sketch, "E2142", {"start": v(17.09, 31.25) * mm, "end": v(16.97, 31.16) * mm});
            skLineSegment(sketch, "E2143", {"start": v(16.97, 31.16) * mm, "end": v(16.86, 31.07) * mm});
            skLineSegment(sketch, "E2144", {"start": v(16.86, 31.07) * mm, "end": v(16.75, 30.97) * mm});
            skLineSegment(sketch, "E2145", {"start": v(16.75, 30.97) * mm, "end": v(16.65, 30.89) * mm});
            skLineSegment(sketch, "E2146", {"start": v(16.65, 30.89) * mm, "end": v(16.55, 30.8) * mm});
            skLineSegment(sketch, "E2147", {"start": v(16.55, 30.8) * mm, "end": v(16.45, 30.71) * mm});
            skLineSegment(sketch, "E2148", {"start": v(16.45, 30.71) * mm, "end": v(16.36, 30.63) * mm});
            skLineSegment(sketch, "E2149", {"start": v(16.36, 30.63) * mm, "end": v(16.27, 30.54) * mm});
            skLineSegment(sketch, "E2150", {"start": v(16.27, 30.54) * mm, "end": v(16.19, 30.46) * mm});
            skLineSegment(sketch, "E2151", {"start": v(16.19, 30.46) * mm, "end": v(16.1, 30.38) * mm});
            skLineSegment(sketch, "E2152", {"start": v(16.1, 30.38) * mm, "end": v(16.03, 30.3) * mm});
            skLineSegment(sketch, "E2153", {"start": v(16.03, 30.3) * mm, "end": v(15.95, 30.23) * mm});
            skLineSegment(sketch, "E2154", {"start": v(15.95, 30.23) * mm, "end": v(15.88, 30.15) * mm});
            skLineSegment(sketch, "E2155", {"start": v(15.88, 30.15) * mm, "end": v(15.82, 30.08) * mm});
            skLineSegment(sketch, "E2156", {"start": v(15.82, 30.08) * mm, "end": v(15.75, 30.01) * mm});
            skLineSegment(sketch, "E2157", {"start": v(15.75, 30.01) * mm, "end": v(15.7, 29.95) * mm});
            skLineSegment(sketch, "E2158", {"start": v(15.7, 29.95) * mm, "end": v(15.64, 29.88) * mm});
            skLineSegment(sketch, "E2159", {"start": v(15.64, 29.88) * mm, "end": v(15.58, 29.82) * mm});
            skLineSegment(sketch, "E2160", {"start": v(15.58, 29.82) * mm, "end": v(15.53, 29.76) * mm});
            skLineSegment(sketch, "E2161", {"start": v(15.53, 29.76) * mm, "end": v(15.49, 29.7) * mm});
            skLineSegment(sketch, "E2162", {"start": v(15.49, 29.7) * mm, "end": v(15.44, 29.65) * mm});
            skLineSegment(sketch, "E2163", {"start": v(15.44, 29.65) * mm, "end": v(15.4, 29.6) * mm});
            skLineSegment(sketch, "E2164", {"start": v(15.4, 29.6) * mm, "end": v(15.36, 29.54) * mm});
            skLineSegment(sketch, "E2165", {"start": v(15.36, 29.54) * mm, "end": v(15.33, 29.5) * mm});
            skLineSegment(sketch, "E2166", {"start": v(15.33, 29.5) * mm, "end": v(15.3, 29.45) * mm});
            skLineSegment(sketch, "E2167", {"start": v(15.3, 29.45) * mm, "end": v(15.26, 29.4) * mm});
            skLineSegment(sketch, "E2168", {"start": v(15.26, 29.4) * mm, "end": v(15.24, 29.37) * mm});
            skLineSegment(sketch, "E2169", {"start": v(15.24, 29.37) * mm, "end": v(15.21, 29.34) * mm});
            skLineSegment(sketch, "E2170", {"start": v(15.21, 29.34) * mm, "end": v(15.2, 29.3) * mm});
            skLineSegment(sketch, "E2171", {"start": v(15.2, 29.3) * mm, "end": v(15.17, 29.27) * mm});
            skLineSegment(sketch, "E2172", {"start": v(15.17, 29.27) * mm, "end": v(15.15, 29.25) * mm});
            skLineSegment(sketch, "E2173", {"start": v(15.15, 29.25) * mm, "end": v(15.14, 29.22) * mm});
            skLineSegment(sketch, "E2174", {"start": v(15.14, 29.22) * mm, "end": v(15.13, 29.2) * mm});
            skLineSegment(sketch, "E2175", {"start": v(15.13, 29.2) * mm, "end": v(15.12, 29.19) * mm});
            skLineSegment(sketch, "E2176", {"start": v(15.12, 29.19) * mm, "end": v(15.1, 29.17) * mm});
            skLineSegment(sketch, "E2177", {"start": v(15.1, 29.17) * mm, "end": v(15.1, 29.16) * mm});
            skLineSegment(sketch, "E2178", {"start": v(15.1, 29.16) * mm, "end": v(15.1, 29.15) * mm});
            skLineSegment(sketch, "E2179", {"start": v(15.1, 29.15) * mm, "end": v(14.91, 28.8) * mm});
            skLineSegment(sketch, "E2180", {"start": v(14.91, 28.8) * mm, "end": v(12.85, 29.77) * mm});
            skLineSegment(sketch, "E2181", {"start": v(12.85, 29.77) * mm, "end": v(13.01, 30.14) * mm});
            skLineSegment(sketch, "E2182", {"start": v(13.01, 30.14) * mm, "end": v(13.02, 30.15) * mm});
            skLineSegment(sketch, "E2183", {"start": v(13.02, 30.15) * mm, "end": v(13.02, 30.16) * mm});
            skLineSegment(sketch, "E2184", {"start": v(13.02, 30.16) * mm, "end": v(13.03, 30.18) * mm});
            skLineSegment(sketch, "E2185", {"start": v(13.03, 30.18) * mm, "end": v(13.03, 30.2) * mm});
            skLineSegment(sketch, "E2186", {"start": v(13.03, 30.2) * mm, "end": v(13.04, 30.22) * mm});
            skLineSegment(sketch, "E2187", {"start": v(13.04, 30.22) * mm, "end": v(13.05, 30.24) * mm});
            skLineSegment(sketch, "E2188", {"start": v(13.05, 30.24) * mm, "end": v(13.06, 30.27) * mm});
            skLineSegment(sketch, "E2189", {"start": v(13.06, 30.27) * mm, "end": v(13.07, 30.3) * mm});
            skLineSegment(sketch, "E2190", {"start": v(13.07, 30.3) * mm, "end": v(13.08, 30.34) * mm});
            skLineSegment(sketch, "E2191", {"start": v(13.08, 30.34) * mm, "end": v(13.1, 30.39) * mm});
            skLineSegment(sketch, "E2192", {"start": v(13.1, 30.39) * mm, "end": v(13.1, 30.43) * mm});
            skLineSegment(sketch, "E2193", {"start": v(13.1, 30.43) * mm, "end": v(13.12, 30.48) * mm});
            skLineSegment(sketch, "E2194", {"start": v(13.12, 30.48) * mm, "end": v(13.14, 30.53) * mm});
            skLineSegment(sketch, "E2195", {"start": v(13.14, 30.53) * mm, "end": v(13.15, 30.6) * mm});
            skLineSegment(sketch, "E2196", {"start": v(13.15, 30.6) * mm, "end": v(13.17, 30.65) * mm});
            skLineSegment(sketch, "E2197", {"start": v(13.17, 30.65) * mm, "end": v(13.18, 30.72) * mm});
            skLineSegment(sketch, "E2198", {"start": v(13.18, 30.72) * mm, "end": v(13.2, 30.79) * mm});
            skLineSegment(sketch, "E2199", {"start": v(13.2, 30.79) * mm, "end": v(13.2, 30.86) * mm});
            skLineSegment(sketch, "E2200", {"start": v(13.2, 30.86) * mm, "end": v(13.22, 30.94) * mm});
            skLineSegment(sketch, "E2201", {"start": v(13.22, 30.94) * mm, "end": v(13.24, 31.02) * mm});
            skLineSegment(sketch, "E2202", {"start": v(13.24, 31.02) * mm, "end": v(13.25, 31.1) * mm});
            skLineSegment(sketch, "E2203", {"start": v(13.25, 31.1) * mm, "end": v(13.27, 31.2) * mm});
            skLineSegment(sketch, "E2204", {"start": v(13.27, 31.2) * mm, "end": v(13.28, 31.29) * mm});
            skLineSegment(sketch, "E2205", {"start": v(13.28, 31.29) * mm, "end": v(13.3, 31.38) * mm});
            skLineSegment(sketch, "E2206", {"start": v(13.3, 31.38) * mm, "end": v(13.3, 31.48) * mm});
            skLineSegment(sketch, "E2207", {"start": v(13.3, 31.48) * mm, "end": v(13.32, 31.59) * mm});
            skLineSegment(sketch, "E2208", {"start": v(13.32, 31.59) * mm, "end": v(13.33, 31.7) * mm});
            skLineSegment(sketch, "E2209", {"start": v(13.33, 31.7) * mm, "end": v(13.34, 31.81) * mm});
            skLineSegment(sketch, "E2210", {"start": v(13.34, 31.81) * mm, "end": v(13.35, 31.93) * mm});
            skLineSegment(sketch, "E2211", {"start": v(13.35, 31.93) * mm, "end": v(13.36, 32.05) * mm});
            skLineSegment(sketch, "E2212", {"start": v(13.36, 32.05) * mm, "end": v(13.36, 32.18) * mm});
            skLineSegment(sketch, "E2213", {"start": v(13.36, 32.18) * mm, "end": v(13.37, 32.3) * mm});
            skLineSegment(sketch, "E2214", {"start": v(13.37, 32.3) * mm, "end": v(13.37, 32.44) * mm});
            skLineSegment(sketch, "E2215", {"start": v(13.37, 32.44) * mm, "end": v(13.38, 32.57) * mm});
            skLineSegment(sketch, "E2216", {"start": v(13.38, 32.57) * mm, "end": v(13.38, 32.72) * mm});
            skLineSegment(sketch, "E2217", {"start": v(13.38, 32.72) * mm, "end": v(13.38, 32.86) * mm});
            skLineSegment(sketch, "E2218", {"start": v(13.38, 32.86) * mm, "end": v(13.38, 33) * mm});
            skLineSegment(sketch, "E2219", {"start": v(13.38, 33) * mm, "end": v(13.38, 33.16) * mm});
            skLineSegment(sketch, "E2220", {"start": v(13.38, 33.16) * mm, "end": v(13.37, 33.32) * mm});
            skLineSegment(sketch, "E2221", {"start": v(13.37, 33.32) * mm, "end": v(13.37, 33.48) * mm});
            skLineSegment(sketch, "E2222", {"start": v(13.37, 33.48) * mm, "end": v(13.36, 33.64) * mm});
            skLineSegment(sketch, "E2223", {"start": v(13.36, 33.64) * mm, "end": v(13.35, 33.81) * mm});
            skLineSegment(sketch, "E2224", {"start": v(13.35, 33.81) * mm, "end": v(13.33, 33.98) * mm});
            skLineSegment(sketch, "E2225", {"start": v(13.33, 33.98) * mm, "end": v(13.32, 34.16) * mm});
            skLineSegment(sketch, "E2226", {"start": v(13.32, 34.16) * mm, "end": v(13.3, 34.34) * mm});
            skLineSegment(sketch, "E2227", {"start": v(13.3, 34.34) * mm, "end": v(13.28, 34.52) * mm});
            skLineSegment(sketch, "E2228", {"start": v(13.28, 34.52) * mm, "end": v(13.25, 34.67) * mm});
            skLineSegment(sketch, "E2229", {"start": v(13.25, 34.67) * mm, "end": v(11.82, 35.18) * mm});
            skLineSegment(sketch, "E2230", {"start": v(11.82, 35.18) * mm, "end": v(11.7, 35.09) * mm});
            skLineSegment(sketch, "E2231", {"start": v(11.7, 35.09) * mm, "end": v(11.57, 34.96) * mm});
            skLineSegment(sketch, "E2232", {"start": v(11.57, 34.96) * mm, "end": v(11.44, 34.83) * mm});
            skLineSegment(sketch, "E2233", {"start": v(11.44, 34.83) * mm, "end": v(11.32, 34.7) * mm});
            skLineSegment(sketch, "E2234", {"start": v(11.32, 34.7) * mm, "end": v(11.2, 34.58) * mm});
            skLineSegment(sketch, "E2235", {"start": v(11.2, 34.58) * mm, "end": v(11.08, 34.46) * mm});
            skLineSegment(sketch, "E2236", {"start": v(11.08, 34.46) * mm, "end": v(10.97, 34.34) * mm});
            skLineSegment(sketch, "E2237", {"start": v(10.97, 34.34) * mm, "end": v(10.87, 34.22) * mm});
            skLineSegment(sketch, "E2238", {"start": v(10.87, 34.22) * mm, "end": v(10.76, 34.1) * mm});
            skLineSegment(sketch, "E2239", {"start": v(10.76, 34.1) * mm, "end": v(10.66, 33.98) * mm});
            skLineSegment(sketch, "E2240", {"start": v(10.66, 33.98) * mm, "end": v(10.57, 33.87) * mm});
            skLineSegment(sketch, "E2241", {"start": v(10.57, 33.87) * mm, "end": v(10.48, 33.76) * mm});
            skLineSegment(sketch, "E2242", {"start": v(10.48, 33.76) * mm, "end": v(10.39, 33.65) * mm});
            skLineSegment(sketch, "E2243", {"start": v(10.39, 33.65) * mm, "end": v(10.3, 33.54) * mm});
            skLineSegment(sketch, "E2244", {"start": v(10.3, 33.54) * mm, "end": v(10.22, 33.43) * mm});
            skLineSegment(sketch, "E2245", {"start": v(10.22, 33.43) * mm, "end": v(10.15, 33.33) * mm});
            skLineSegment(sketch, "E2246", {"start": v(10.15, 33.33) * mm, "end": v(10.07, 33.23) * mm});
            skLineSegment(sketch, "E2247", {"start": v(10.07, 33.23) * mm, "end": v(10, 33.13) * mm});
            skLineSegment(sketch, "E2248", {"start": v(10, 33.13) * mm, "end": v(9.93, 33.03) * mm});
            skLineSegment(sketch, "E2249", {"start": v(9.93, 33.03) * mm, "end": v(9.87, 32.94) * mm});
            skLineSegment(sketch, "E2250", {"start": v(9.87, 32.94) * mm, "end": v(9.8, 32.85) * mm});
            skLineSegment(sketch, "E2251", {"start": v(9.8, 32.85) * mm, "end": v(9.75, 32.76) * mm});
            skLineSegment(sketch, "E2252", {"start": v(9.75, 32.76) * mm, "end": v(9.7, 32.67) * mm});
            skLineSegment(sketch, "E2253", {"start": v(9.7, 32.67) * mm, "end": v(9.64, 32.6) * mm});
            skLineSegment(sketch, "E2254", {"start": v(9.64, 32.6) * mm, "end": v(9.6, 32.51) * mm});
            skLineSegment(sketch, "E2255", {"start": v(9.6, 32.51) * mm, "end": v(9.55, 32.43) * mm});
            skLineSegment(sketch, "E2256", {"start": v(9.55, 32.43) * mm, "end": v(9.5, 32.36) * mm});
            skLineSegment(sketch, "E2257", {"start": v(9.5, 32.36) * mm, "end": v(9.47, 32.29) * mm});
            skLineSegment(sketch, "E2258", {"start": v(9.47, 32.29) * mm, "end": v(9.43, 32.22) * mm});
            skLineSegment(sketch, "E2259", {"start": v(9.43, 32.22) * mm, "end": v(9.4, 32.15) * mm});
            skLineSegment(sketch, "E2260", {"start": v(9.4, 32.15) * mm, "end": v(9.36, 32.09) * mm});
            skLineSegment(sketch, "E2261", {"start": v(9.36, 32.09) * mm, "end": v(9.33, 32.03) * mm});
            skLineSegment(sketch, "E2262", {"start": v(9.33, 32.03) * mm, "end": v(9.3, 31.97) * mm});
            skLineSegment(sketch, "E2263", {"start": v(9.3, 31.97) * mm, "end": v(9.28, 31.92) * mm});
            skLineSegment(sketch, "E2264", {"start": v(9.28, 31.92) * mm, "end": v(9.25, 31.87) * mm});
            skLineSegment(sketch, "E2265", {"start": v(9.25, 31.87) * mm, "end": v(9.23, 31.82) * mm});
            skLineSegment(sketch, "E2266", {"start": v(9.23, 31.82) * mm, "end": v(9.21, 31.78) * mm});
            skLineSegment(sketch, "E2267", {"start": v(9.21, 31.78) * mm, "end": v(9.2, 31.74) * mm});
            skLineSegment(sketch, "E2268", {"start": v(9.2, 31.74) * mm, "end": v(9.18, 31.7) * mm});
            skLineSegment(sketch, "E2269", {"start": v(9.18, 31.7) * mm, "end": v(9.17, 31.67) * mm});
            skLineSegment(sketch, "E2270", {"start": v(9.17, 31.67) * mm, "end": v(9.16, 31.64) * mm});
            skLineSegment(sketch, "E2271", {"start": v(9.16, 31.64) * mm, "end": v(9.15, 31.61) * mm});
            skLineSegment(sketch, "E2272", {"start": v(9.15, 31.61) * mm, "end": v(9.14, 31.6) * mm});
            skLineSegment(sketch, "E2273", {"start": v(9.14, 31.6) * mm, "end": v(9.13, 31.57) * mm});
            skLineSegment(sketch, "E2274", {"start": v(9.13, 31.57) * mm, "end": v(9.13, 31.56) * mm});
            skLineSegment(sketch, "E2275", {"start": v(9.13, 31.56) * mm, "end": v(9.12, 31.55) * mm});
            skLineSegment(sketch, "E2276", {"start": v(9.12, 31.55) * mm, "end": v(9.12, 31.54) * mm});
            skLineSegment(sketch, "E2277", {"start": v(9.12, 31.54) * mm, "end": v(9, 31.15) * mm});
            skLineSegment(sketch, "E2278", {"start": v(9, 31.15) * mm, "end": v(6.8, 31.7) * mm});
            skLineSegment(sketch, "E2279", {"start": v(6.8, 31.7) * mm, "end": v(6.88, 32.1) * mm});
            skLineSegment(sketch, "E2280", {"start": v(6.88, 32.1) * mm, "end": v(6.89, 32.1) * mm});
            skLineSegment(sketch, "E2281", {"start": v(6.89, 32.1) * mm, "end": v(6.89, 32.12) * mm});
            skLineSegment(sketch, "E2282", {"start": v(6.89, 32.12) * mm, "end": v(6.9, 32.14) * mm});
            skLineSegment(sketch, "E2283", {"start": v(6.9, 32.14) * mm, "end": v(6.9, 32.16) * mm});
            skLineSegment(sketch, "E2284", {"start": v(6.9, 32.16) * mm, "end": v(6.9, 32.18) * mm});
            skLineSegment(sketch, "E2285", {"start": v(6.9, 32.18) * mm, "end": v(6.9, 32.2) * mm});
            skLineSegment(sketch, "E2286", {"start": v(6.9, 32.2) * mm, "end": v(6.9, 32.24) * mm});
            skLineSegment(sketch, "E2287", {"start": v(6.9, 32.24) * mm, "end": v(6.9, 32.27) * mm});
            skLineSegment(sketch, "E2288", {"start": v(6.9, 32.27) * mm, "end": v(6.91, 32.31) * mm});
            skLineSegment(sketch, "E2289", {"start": v(6.91, 32.31) * mm, "end": v(6.92, 32.36) * mm});
            skLineSegment(sketch, "E2290", {"start": v(6.92, 32.36) * mm, "end": v(6.92, 32.4) * mm});
            skLineSegment(sketch, "E2291", {"start": v(6.92, 32.4) * mm, "end": v(6.92, 32.46) * mm});
            skLineSegment(sketch, "E2292", {"start": v(6.92, 32.46) * mm, "end": v(6.93, 32.51) * mm});
            skLineSegment(sketch, "E2293", {"start": v(6.93, 32.51) * mm, "end": v(6.93, 32.57) * mm});
            skLineSegment(sketch, "E2294", {"start": v(6.93, 32.57) * mm, "end": v(6.93, 32.63) * mm});
            skLineSegment(sketch, "E2295", {"start": v(6.93, 32.63) * mm, "end": v(6.93, 32.7) * mm});
            skLineSegment(sketch, "E2296", {"start": v(6.93, 32.7) * mm, "end": v(6.93, 32.77) * mm});
            skLineSegment(sketch, "E2297", {"start": v(6.93, 32.77) * mm, "end": v(6.93, 32.84) * mm});
            skLineSegment(sketch, "E2298", {"start": v(6.93, 32.84) * mm, "end": v(6.93, 32.92) * mm});
            skLineSegment(sketch, "E2299", {"start": v(6.93, 32.92) * mm, "end": v(6.93, 33) * mm});
            skLineSegment(sketch, "E2300", {"start": v(6.93, 33) * mm, "end": v(6.93, 33.1) * mm});
            skLineSegment(sketch, "E2301", {"start": v(6.93, 33.1) * mm, "end": v(6.93, 33.18) * mm});
            skLineSegment(sketch, "E2302", {"start": v(6.93, 33.18) * mm, "end": v(6.92, 33.28) * mm});
            skLineSegment(sketch, "E2303", {"start": v(6.92, 33.28) * mm, "end": v(6.92, 33.37) * mm});
            skLineSegment(sketch, "E2304", {"start": v(6.92, 33.37) * mm, "end": v(6.9, 33.48) * mm});
            skLineSegment(sketch, "E2305", {"start": v(6.9, 33.48) * mm, "end": v(6.9, 33.58) * mm});
            skLineSegment(sketch, "E2306", {"start": v(6.9, 33.58) * mm, "end": v(6.89, 33.7) * mm});
            skLineSegment(sketch, "E2307", {"start": v(6.89, 33.7) * mm, "end": v(6.88, 33.8) * mm});
            skLineSegment(sketch, "E2308", {"start": v(6.88, 33.8) * mm, "end": v(6.86, 33.92) * mm});
            skLineSegment(sketch, "E2309", {"start": v(6.86, 33.92) * mm, "end": v(6.85, 34.04) * mm});
            skLineSegment(sketch, "E2310", {"start": v(6.85, 34.04) * mm, "end": v(6.83, 34.16) * mm});
            skLineSegment(sketch, "E2311", {"start": v(6.83, 34.16) * mm, "end": v(6.81, 34.3) * mm});
            skLineSegment(sketch, "E2312", {"start": v(6.81, 34.3) * mm, "end": v(6.79, 34.42) * mm});
            skLineSegment(sketch, "E2313", {"start": v(6.79, 34.42) * mm, "end": v(6.77, 34.56) * mm});
            skLineSegment(sketch, "E2314", {"start": v(6.77, 34.56) * mm, "end": v(6.74, 34.7) * mm});
            skLineSegment(sketch, "E2315", {"start": v(6.74, 34.7) * mm, "end": v(6.71, 34.84) * mm});
            skLineSegment(sketch, "E2316", {"start": v(6.71, 34.84) * mm, "end": v(6.68, 34.99) * mm});
            skLineSegment(sketch, "E2317", {"start": v(6.68, 34.99) * mm, "end": v(6.65, 35.13) * mm});
            skLineSegment(sketch, "E2318", {"start": v(6.65, 35.13) * mm, "end": v(6.61, 35.29) * mm});
            skLineSegment(sketch, "E2319", {"start": v(6.61, 35.29) * mm, "end": v(6.58, 35.44) * mm});
            skLineSegment(sketch, "E2320", {"start": v(6.58, 35.44) * mm, "end": v(6.54, 35.6) * mm});
            skLineSegment(sketch, "E2321", {"start": v(6.54, 35.6) * mm, "end": v(6.5, 35.77) * mm});
            skLineSegment(sketch, "E2322", {"start": v(6.5, 35.77) * mm, "end": v(6.45, 35.93) * mm});
            skLineSegment(sketch, "E2323", {"start": v(6.45, 35.93) * mm, "end": v(6.4, 36.1) * mm});
            skLineSegment(sketch, "E2324", {"start": v(6.4, 36.1) * mm, "end": v(6.35, 36.27) * mm});
            skLineSegment(sketch, "E2325", {"start": v(6.35, 36.27) * mm, "end": v(6.3, 36.45) * mm});
            skLineSegment(sketch, "E2326", {"start": v(6.3, 36.45) * mm, "end": v(6.23, 36.6) * mm});
            skLineSegment(sketch, "E2327", {"start": v(6.23, 36.6) * mm, "end": v(4.73, 36.81) * mm});
            skLineSegment(sketch, "E2328", {"start": v(4.73, 36.81) * mm, "end": v(4.63, 36.7) * mm});
            skLineSegment(sketch, "E2329", {"start": v(4.63, 36.7) * mm, "end": v(4.53, 36.55) * mm});
            skLineSegment(sketch, "E2330", {"start": v(4.53, 36.55) * mm, "end": v(4.43, 36.4) * mm});
            skLineSegment(sketch, "E2331", {"start": v(4.43, 36.4) * mm, "end": v(4.33, 36.25) * mm});
            skLineSegment(sketch, "E2332", {"start": v(4.33, 36.25) * mm, "end": v(4.24, 36.1) * mm});
            skLineSegment(sketch, "E2333", {"start": v(4.24, 36.1) * mm, "end": v(4.15, 35.96) * mm});
            skLineSegment(sketch, "E2334", {"start": v(4.15, 35.96) * mm, "end": v(4.06, 35.82) * mm});
            skLineSegment(sketch, "E2335", {"start": v(4.06, 35.82) * mm, "end": v(3.98, 35.68) * mm});
            skLineSegment(sketch, "E2336", {"start": v(3.98, 35.68) * mm, "end": v(3.9, 35.54) * mm});
            skLineSegment(sketch, "E2337", {"start": v(3.9, 35.54) * mm, "end": v(3.83, 35.41) * mm});
            skLineSegment(sketch, "E2338", {"start": v(3.83, 35.41) * mm, "end": v(3.76, 35.28) * mm});
            skLineSegment(sketch, "E2339", {"start": v(3.76, 35.28) * mm, "end": v(3.69, 35.15) * mm});
            skLineSegment(sketch, "E2340", {"start": v(3.69, 35.15) * mm, "end": v(3.62, 35.03) * mm});
            skLineSegment(sketch, "E2341", {"start": v(3.62, 35.03) * mm, "end": v(3.56, 34.9) * mm});
            skLineSegment(sketch, "E2342", {"start": v(3.56, 34.9) * mm, "end": v(3.5, 34.79) * mm});
            skLineSegment(sketch, "E2343", {"start": v(3.5, 34.79) * mm, "end": v(3.45, 34.67) * mm});
            skLineSegment(sketch, "E2344", {"start": v(3.45, 34.67) * mm, "end": v(3.4, 34.56) * mm});
            skLineSegment(sketch, "E2345", {"start": v(3.4, 34.56) * mm, "end": v(3.35, 34.45) * mm});
            skLineSegment(sketch, "E2346", {"start": v(3.35, 34.45) * mm, "end": v(3.3, 34.34) * mm});
            skLineSegment(sketch, "E2347", {"start": v(3.3, 34.34) * mm, "end": v(3.25, 34.23) * mm});
            skLineSegment(sketch, "E2348", {"start": v(3.25, 34.23) * mm, "end": v(3.21, 34.13) * mm});
            skLineSegment(sketch, "E2349", {"start": v(3.21, 34.13) * mm, "end": v(3.17, 34.03) * mm});
            skLineSegment(sketch, "E2350", {"start": v(3.17, 34.03) * mm, "end": v(3.14, 33.94) * mm});
            skLineSegment(sketch, "E2351", {"start": v(3.14, 33.94) * mm, "end": v(3.1, 33.85) * mm});
            skLineSegment(sketch, "E2352", {"start": v(3.1, 33.85) * mm, "end": v(3.07, 33.76) * mm});
            skLineSegment(sketch, "E2353", {"start": v(3.07, 33.76) * mm, "end": v(3.04, 33.67) * mm});
            skLineSegment(sketch, "E2354", {"start": v(3.04, 33.67) * mm, "end": v(3.01, 33.6) * mm});
            skLineSegment(sketch, "E2355", {"start": v(3.01, 33.6) * mm, "end": v(2.99, 33.51) * mm});
            skLineSegment(sketch, "E2356", {"start": v(2.99, 33.51) * mm, "end": v(2.96, 33.44) * mm});
            skLineSegment(sketch, "E2357", {"start": v(2.96, 33.44) * mm, "end": v(2.94, 33.37) * mm});
            skLineSegment(sketch, "E2358", {"start": v(2.94, 33.37) * mm, "end": v(2.92, 33.3) * mm});
            skLineSegment(sketch, "E2359", {"start": v(2.92, 33.3) * mm, "end": v(2.9, 33.23) * mm});
            skLineSegment(sketch, "E2360", {"start": v(2.9, 33.23) * mm, "end": v(2.89, 33.17) * mm});
            skLineSegment(sketch, "E2361", {"start": v(2.89, 33.17) * mm, "end": v(2.87, 33.12) * mm});
            skLineSegment(sketch, "E2362", {"start": v(2.87, 33.12) * mm, "end": v(2.86, 33.06) * mm});
            skLineSegment(sketch, "E2363", {"start": v(2.86, 33.06) * mm, "end": v(2.85, 33.01) * mm});
            skLineSegment(sketch, "E2364", {"start": v(2.85, 33.01) * mm, "end": v(2.84, 32.97) * mm});
            skLineSegment(sketch, "E2365", {"start": v(2.84, 32.97) * mm, "end": v(2.83, 32.92) * mm});
            skLineSegment(sketch, "E2366", {"start": v(2.83, 32.92) * mm, "end": v(2.82, 32.89) * mm});
            skLineSegment(sketch, "E2367", {"start": v(2.82, 32.89) * mm, "end": v(2.81, 32.85) * mm});
            skLineSegment(sketch, "E2368", {"start": v(2.81, 32.85) * mm, "end": v(2.8, 32.82) * mm});
            skLineSegment(sketch, "E2369", {"start": v(2.8, 32.82) * mm, "end": v(2.8, 32.8) * mm});
            skLineSegment(sketch, "E2370", {"start": v(2.8, 32.8) * mm, "end": v(2.8, 32.77) * mm});
            skLineSegment(sketch, "E2371", {"start": v(2.8, 32.77) * mm, "end": v(2.8, 32.75) * mm});
            skLineSegment(sketch, "E2372", {"start": v(2.8, 32.75) * mm, "end": v(2.8, 32.73) * mm});
            skLineSegment(sketch, "E2373", {"start": v(2.8, 32.73) * mm, "end": v(2.8, 32.72) * mm});
            skLineSegment(sketch, "E2374", {"start": v(2.8, 32.72) * mm, "end": v(2.8, 32.71) * mm});
            skLineSegment(sketch, "E2375", {"start": v(2.8, 32.71) * mm, "end": v(2.76, 32.3) * mm});
            skLineSegment(sketch, "E2376", {"start": v(2.76, 32.3) * mm, "end": v(0.48, 32.42) * mm});
            skLineSegment(sketch, "E2377", {"start": v(0.48, 32.42) * mm, "end": v(0.49, 32.83) * mm});
            skLineSegment(sketch, "E2378", {"start": v(0.49, 32.83) * mm, "end": v(0.49, 32.84) * mm});
            skLineSegment(sketch, "E2379", {"start": v(0.49, 32.84) * mm, "end": v(0.49, 32.85) * mm});
            skLineSegment(sketch, "E2380", {"start": v(0.49, 32.85) * mm, "end": v(0.49, 32.86) * mm});
            skLineSegment(sketch, "E2381", {"start": v(0.49, 32.86) * mm, "end": v(0.49, 32.88) * mm});
            skLineSegment(sketch, "E2382", {"start": v(0.49, 32.88) * mm, "end": v(0.49, 32.9) * mm});
            skLineSegment(sketch, "E2383", {"start": v(0.49, 32.9) * mm, "end": v(0.48, 32.94) * mm});
            skLineSegment(sketch, "E2384", {"start": v(0.48, 32.94) * mm, "end": v(0.48, 32.97) * mm});
            skLineSegment(sketch, "E2385", {"start": v(0.48, 32.97) * mm, "end": v(0.48, 33) * mm});
            skLineSegment(sketch, "E2386", {"start": v(0.48, 33) * mm, "end": v(0.48, 33.04) * mm});
            skLineSegment(sketch, "E2387", {"start": v(0.48, 33.04) * mm, "end": v(0.47, 33.09) * mm});
            skLineSegment(sketch, "E2388", {"start": v(0.47, 33.09) * mm, "end": v(0.47, 33.13) * mm});
            skLineSegment(sketch, "E2389", {"start": v(0.47, 33.13) * mm, "end": v(0.46, 33.18) * mm});
            skLineSegment(sketch, "E2390", {"start": v(0.46, 33.18) * mm, "end": v(0.45, 33.24) * mm});
            skLineSegment(sketch, "E2391", {"start": v(0.45, 33.24) * mm, "end": v(0.44, 33.3) * mm});
            skLineSegment(sketch, "E2392", {"start": v(0.44, 33.3) * mm, "end": v(0.43, 33.36) * mm});
            skLineSegment(sketch, "E2393", {"start": v(0.43, 33.36) * mm, "end": v(0.42, 33.42) * mm});
            skLineSegment(sketch, "E2394", {"start": v(0.42, 33.42) * mm, "end": v(0.4, 33.5) * mm});
            skLineSegment(sketch, "E2395", {"start": v(0.4, 33.5) * mm, "end": v(0.4, 33.57) * mm});
            skLineSegment(sketch, "E2396", {"start": v(0.4, 33.57) * mm, "end": v(0.38, 33.64) * mm});
            skLineSegment(sketch, "E2397", {"start": v(0.38, 33.64) * mm, "end": v(0.36, 33.72) * mm});
            skLineSegment(sketch, "E2398", {"start": v(0.36, 33.72) * mm, "end": v(0.34, 33.8) * mm});
            skLineSegment(sketch, "E2399", {"start": v(0.34, 33.8) * mm, "end": v(0.32, 33.9) * mm});
            skLineSegment(sketch, "E2400", {"start": v(0.32, 33.9) * mm, "end": v(0.3, 33.99) * mm});
            skLineSegment(sketch, "E2401", {"start": v(0.3, 33.99) * mm, "end": v(0.27, 34.08) * mm});
            skLineSegment(sketch, "E2402", {"start": v(0.27, 34.08) * mm, "end": v(0.24, 34.18) * mm});
            skLineSegment(sketch, "E2403", {"start": v(0.24, 34.18) * mm, "end": v(0.22, 34.28) * mm});
            skLineSegment(sketch, "E2404", {"start": v(0.22, 34.28) * mm, "end": v(0.18, 34.39) * mm});
            skLineSegment(sketch, "E2405", {"start": v(0.18, 34.39) * mm, "end": v(0.15, 34.5) * mm});
            skLineSegment(sketch, "E2406", {"start": v(0.15, 34.5) * mm, "end": v(0.11, 34.6) * mm});
            skLineSegment(sketch, "E2407", {"start": v(0.11, 34.6) * mm, "end": v(0.07, 34.72) * mm});
            skLineSegment(sketch, "E2408", {"start": v(0.07, 34.72) * mm, "end": v(0.03, 34.84) * mm});
            skLineSegment(sketch, "E2409", {"start": v(0.03, 34.84) * mm, "end": v(-0.01, 34.96) * mm});
            skLineSegment(sketch, "E2410", {"start": v(-0.01, 34.96) * mm, "end": v(-0.06, 35.09) * mm});
            skLineSegment(sketch, "E2411", {"start": v(-0.06, 35.09) * mm, "end": v(-0.1, 35.21) * mm});
            skLineSegment(sketch, "E2412", {"start": v(-0.1, 35.21) * mm, "end": v(-0.16, 35.35) * mm});
            skLineSegment(sketch, "E2413", {"start": v(-0.16, 35.35) * mm, "end": v(-0.21, 35.48) * mm});
            skLineSegment(sketch, "E2414", {"start": v(-0.21, 35.48) * mm, "end": v(-0.27, 35.62) * mm});
            skLineSegment(sketch, "E2415", {"start": v(-0.27, 35.62) * mm, "end": v(-0.33, 35.76) * mm});
            skLineSegment(sketch, "E2416", {"start": v(-0.33, 35.76) * mm, "end": v(-0.4, 35.9) * mm});
            skLineSegment(sketch, "E2417", {"start": v(-0.4, 35.9) * mm, "end": v(-0.46, 36.05) * mm});
            skLineSegment(sketch, "E2418", {"start": v(-0.46, 36.05) * mm, "end": v(-0.53, 36.2) * mm});
            skLineSegment(sketch, "E2419", {"start": v(-0.53, 36.2) * mm, "end": v(-0.6, 36.35) * mm});
            skLineSegment(sketch, "E2420", {"start": v(-0.6, 36.35) * mm, "end": v(-0.69, 36.5) * mm});
            skLineSegment(sketch, "E2421", {"start": v(-0.69, 36.5) * mm, "end": v(-0.77, 36.66) * mm});
            skLineSegment(sketch, "E2422", {"start": v(-0.77, 36.66) * mm, "end": v(-0.85, 36.81) * mm});
            skLineSegment(sketch, "E2423", {"start": v(-0.85, 36.81) * mm, "end": v(-0.94, 36.98) * mm});
            skLineSegment(sketch, "E2424", {"start": v(-0.94, 36.98) * mm, "end": v(-1.03, 37.1) * mm});
            skLineSegment(sketch, "E2425", {"start": v(-1.03, 37.1) * mm, "end": v(-2.54, 37.03) * mm});
            skLineSegment(sketch, "E2426", {"start": v(-2.54, 37.03) * mm, "end": v(-2.62, 36.9) * mm});
            skLineSegment(sketch, "E2427", {"start": v(-2.62, 36.9) * mm, "end": v(-2.7, 36.73) * mm});
            skLineSegment(sketch, "E2428", {"start": v(-2.7, 36.73) * mm, "end": v(-2.76, 36.56) * mm});
            skLineSegment(sketch, "E2429", {"start": v(-2.76, 36.56) * mm, "end": v(-2.82, 36.4) * mm});
            skLineSegment(sketch, "E2430", {"start": v(-2.82, 36.4) * mm, "end": v(-2.89, 36.24) * mm});
            skLineSegment(sketch, "E2431", {"start": v(-2.89, 36.24) * mm, "end": v(-2.95, 36.08) * mm});
            skLineSegment(sketch, "E2432", {"start": v(-2.95, 36.08) * mm, "end": v(-3, 35.92) * mm});
            skLineSegment(sketch, "E2433", {"start": v(-3, 35.92) * mm, "end": v(-3.05, 35.77) * mm});
            skLineSegment(sketch, "E2434", {"start": v(-3.05, 35.77) * mm, "end": v(-3.1, 35.62) * mm});
            skLineSegment(sketch, "E2435", {"start": v(-3.1, 35.62) * mm, "end": v(-3.15, 35.48) * mm});
            skLineSegment(sketch, "E2436", {"start": v(-3.15, 35.48) * mm, "end": v(-3.2, 35.34) * mm});
            skLineSegment(sketch, "E2437", {"start": v(-3.2, 35.34) * mm, "end": v(-3.24, 35.2) * mm});
            skLineSegment(sketch, "E2438", {"start": v(-3.24, 35.2) * mm, "end": v(-3.28, 35.06) * mm});
            skLineSegment(sketch, "E2439", {"start": v(-3.28, 35.06) * mm, "end": v(-3.32, 34.93) * mm});
            skLineSegment(sketch, "E2440", {"start": v(-3.32, 34.93) * mm, "end": v(-3.35, 34.8) * mm});
            skLineSegment(sketch, "E2441", {"start": v(-3.35, 34.8) * mm, "end": v(-3.38, 34.68) * mm});
            skLineSegment(sketch, "E2442", {"start": v(-3.38, 34.68) * mm, "end": v(-3.41, 34.55) * mm});
            skLineSegment(sketch, "E2443", {"start": v(-3.41, 34.55) * mm, "end": v(-3.44, 34.44) * mm});
            skLineSegment(sketch, "E2444", {"start": v(-3.44, 34.44) * mm, "end": v(-3.46, 34.32) * mm});
            skLineSegment(sketch, "E2445", {"start": v(-3.46, 34.32) * mm, "end": v(-3.49, 34.2) * mm});
            skLineSegment(sketch, "E2446", {"start": v(-3.49, 34.2) * mm, "end": v(-3.5, 34.1) * mm});
            skLineSegment(sketch, "E2447", {"start": v(-3.5, 34.1) * mm, "end": v(-3.53, 34) * mm});
            skLineSegment(sketch, "E2448", {"start": v(-3.53, 34) * mm, "end": v(-3.55, 33.9) * mm});
            skLineSegment(sketch, "E2449", {"start": v(-3.55, 33.9) * mm, "end": v(-3.56, 33.8) * mm});
            skLineSegment(sketch, "E2450", {"start": v(-3.56, 33.8) * mm, "end": v(-3.58, 33.7) * mm});
            skLineSegment(sketch, "E2451", {"start": v(-3.58, 33.7) * mm, "end": v(-3.59, 33.62) * mm});
            skLineSegment(sketch, "E2452", {"start": v(-3.59, 33.62) * mm, "end": v(-3.6, 33.53) * mm});
            skLineSegment(sketch, "E2453", {"start": v(-3.6, 33.53) * mm, "end": v(-3.6, 33.45) * mm});
            skLineSegment(sketch, "E2454", {"start": v(-3.6, 33.45) * mm, "end": v(-3.62, 33.37) * mm});
            skLineSegment(sketch, "E2455", {"start": v(-3.62, 33.37) * mm, "end": v(-3.63, 33.3) * mm});
            skLineSegment(sketch, "E2456", {"start": v(-3.63, 33.3) * mm, "end": v(-3.63, 33.23) * mm});
            skLineSegment(sketch, "E2457", {"start": v(-3.63, 33.23) * mm, "end": v(-3.64, 33.16) * mm});
            skLineSegment(sketch, "E2458", {"start": v(-3.64, 33.16) * mm, "end": v(-3.64, 33.1) * mm});
            skLineSegment(sketch, "E2459", {"start": v(-3.64, 33.1) * mm, "end": v(-3.64, 33.04) * mm});
            skLineSegment(sketch, "E2460", {"start": v(-3.64, 33.04) * mm, "end": v(-3.65, 32.98) * mm});
            skLineSegment(sketch, "E2461", {"start": v(-3.65, 32.98) * mm, "end": v(-3.65, 32.93) * mm});
            skLineSegment(sketch, "E2462", {"start": v(-3.65, 32.93) * mm, "end": v(-3.65, 32.89) * mm});
            skLineSegment(sketch, "E2463", {"start": v(-3.65, 32.89) * mm, "end": v(-3.65, 32.84) * mm});
            skLineSegment(sketch, "E2464", {"start": v(-3.65, 32.84) * mm, "end": v(-3.65, 32.8) * mm});
            skLineSegment(sketch, "E2465", {"start": v(-3.65, 32.8) * mm, "end": v(-3.65, 32.77) * mm});
            skLineSegment(sketch, "E2466", {"start": v(-3.65, 32.77) * mm, "end": v(-3.65, 32.74) * mm});
            skLineSegment(sketch, "E2467", {"start": v(-3.65, 32.74) * mm, "end": v(-3.65, 32.7) * mm});
            skLineSegment(sketch, "E2468", {"start": v(-3.65, 32.7) * mm, "end": v(-3.65, 32.69) * mm});
            skLineSegment(sketch, "E2469", {"start": v(-3.65, 32.69) * mm, "end": v(-3.64, 32.67) * mm});
            skLineSegment(sketch, "E2470", {"start": v(-3.64, 32.67) * mm, "end": v(-3.64, 32.65) * mm});
            skLineSegment(sketch, "E2471", {"start": v(-3.64, 32.65) * mm, "end": v(-3.64, 32.64) * mm});
            skLineSegment(sketch, "E2472", {"start": v(-3.64, 32.64) * mm, "end": v(-3.64, 32.63) * mm});
            skLineSegment(sketch, "E2473", {"start": v(-3.64, 32.63) * mm, "end": v(-3.6, 32.22) * mm});
            skLineSegment(sketch, "E2474", {"start": v(-3.6, 32.22) * mm, "end": v(-5.85, 31.9) * mm});
            skLineSegment(sketch, "E2475", {"start": v(-5.85, 31.9) * mm, "end": v(-5.92, 32.3) * mm});
            skLineSegment(sketch, "E2476", {"start": v(-5.92, 32.3) * mm, "end": v(-5.93, 32.3) * mm});
            skLineSegment(sketch, "E2477", {"start": v(-5.93, 32.3) * mm, "end": v(-5.93, 32.31) * mm});
            skLineSegment(sketch, "E2478", {"start": v(-5.93, 32.31) * mm, "end": v(-5.93, 32.33) * mm});
            skLineSegment(sketch, "E2479", {"start": v(-5.93, 32.33) * mm, "end": v(-5.94, 32.35) * mm});
            skLineSegment(sketch, "E2480", {"start": v(-5.94, 32.35) * mm, "end": v(-5.94, 32.37) * mm});
            skLineSegment(sketch, "E2481", {"start": v(-5.94, 32.37) * mm, "end": v(-5.95, 32.4) * mm});
            skLineSegment(sketch, "E2482", {"start": v(-5.95, 32.4) * mm, "end": v(-5.96, 32.43) * mm});
            skLineSegment(sketch, "E2483", {"start": v(-5.96, 32.43) * mm, "end": v(-5.97, 32.46) * mm});
            skLineSegment(sketch, "E2484", {"start": v(-5.97, 32.46) * mm, "end": v(-5.98, 32.5) * mm});
            skLineSegment(sketch, "E2485", {"start": v(-5.98, 32.5) * mm, "end": v(-6, 32.54) * mm});
            skLineSegment(sketch, "E2486", {"start": v(-6, 32.54) * mm, "end": v(-6, 32.59) * mm});
            skLineSegment(sketch, "E2487", {"start": v(-6, 32.59) * mm, "end": v(-6.02, 32.63) * mm});
            skLineSegment(sketch, "E2488", {"start": v(-6.02, 32.63) * mm, "end": v(-6.04, 32.69) * mm});
            skLineSegment(sketch, "E2489", {"start": v(-6.04, 32.69) * mm, "end": v(-6.06, 32.74) * mm});
            skLineSegment(sketch, "E2490", {"start": v(-6.06, 32.74) * mm, "end": v(-6.08, 32.8) * mm});
            skLineSegment(sketch, "E2491", {"start": v(-6.08, 32.8) * mm, "end": v(-6.1, 32.86) * mm});
            skLineSegment(sketch, "E2492", {"start": v(-6.1, 32.86) * mm, "end": v(-6.13, 32.93) * mm});
            skLineSegment(sketch, "E2493", {"start": v(-6.13, 32.93) * mm, "end": v(-6.16, 33) * mm});
            skLineSegment(sketch, "E2494", {"start": v(-6.16, 33) * mm, "end": v(-6.2, 33.07) * mm});
            skLineSegment(sketch, "E2495", {"start": v(-6.2, 33.07) * mm, "end": v(-6.23, 33.15) * mm});
            skLineSegment(sketch, "E2496", {"start": v(-6.23, 33.15) * mm, "end": v(-6.26, 33.22) * mm});
            skLineSegment(sketch, "E2497", {"start": v(-6.26, 33.22) * mm, "end": v(-6.3, 33.3) * mm});
            skLineSegment(sketch, "E2498", {"start": v(-6.3, 33.3) * mm, "end": v(-6.34, 33.4) * mm});
            skLineSegment(sketch, "E2499", {"start": v(-6.34, 33.4) * mm, "end": v(-6.38, 33.48) * mm});
            skLineSegment(sketch, "E2500", {"start": v(-6.38, 33.48) * mm, "end": v(-6.43, 33.57) * mm});
            skLineSegment(sketch, "E2501", {"start": v(-6.43, 33.57) * mm, "end": v(-6.48, 33.66) * mm});
            skLineSegment(sketch, "E2502", {"start": v(-6.48, 33.66) * mm, "end": v(-6.53, 33.76) * mm});
            skLineSegment(sketch, "E2503", {"start": v(-6.53, 33.76) * mm, "end": v(-6.58, 33.86) * mm});
            skLineSegment(sketch, "E2504", {"start": v(-6.58, 33.86) * mm, "end": v(-6.64, 33.96) * mm});
            skLineSegment(sketch, "E2505", {"start": v(-6.64, 33.96) * mm, "end": v(-6.7, 34.07) * mm});
            skLineSegment(sketch, "E2506", {"start": v(-6.7, 34.07) * mm, "end": v(-6.76, 34.18) * mm});
            skLineSegment(sketch, "E2507", {"start": v(-6.76, 34.18) * mm, "end": v(-6.83, 34.29) * mm});
            skLineSegment(sketch, "E2508", {"start": v(-6.83, 34.29) * mm, "end": v(-6.9, 34.4) * mm});
            skLineSegment(sketch, "E2509", {"start": v(-6.9, 34.4) * mm, "end": v(-6.97, 34.52) * mm});
            skLineSegment(sketch, "E2510", {"start": v(-6.97, 34.52) * mm, "end": v(-7.05, 34.64) * mm});
            skLineSegment(sketch, "E2511", {"start": v(-7.05, 34.64) * mm, "end": v(-7.13, 34.76) * mm});
            skLineSegment(sketch, "E2512", {"start": v(-7.13, 34.76) * mm, "end": v(-7.21, 34.88) * mm});
            skLineSegment(sketch, "E2513", {"start": v(-7.21, 34.88) * mm, "end": v(-7.3, 35) * mm});
            skLineSegment(sketch, "E2514", {"start": v(-7.3, 35) * mm, "end": v(-7.4, 35.13) * mm});
            skLineSegment(sketch, "E2515", {"start": v(-7.4, 35.13) * mm, "end": v(-7.49, 35.26) * mm});
            skLineSegment(sketch, "E2516", {"start": v(-7.49, 35.26) * mm, "end": v(-7.59, 35.4) * mm});
            skLineSegment(sketch, "E2517", {"start": v(-7.59, 35.4) * mm, "end": v(-7.69, 35.53) * mm});
            skLineSegment(sketch, "E2518", {"start": v(-7.69, 35.53) * mm, "end": v(-7.8, 35.66) * mm});
            skLineSegment(sketch, "E2519", {"start": v(-7.8, 35.66) * mm, "end": v(-7.9, 35.8) * mm});
            skLineSegment(sketch, "E2520", {"start": v(-7.9, 35.8) * mm, "end": v(-8.02, 35.94) * mm});
            skLineSegment(sketch, "E2521", {"start": v(-8.02, 35.94) * mm, "end": v(-8.14, 36.08) * mm});
            skLineSegment(sketch, "E2522", {"start": v(-8.14, 36.08) * mm, "end": v(-8.25, 36.19) * mm});
            skLineSegment(sketch, "E2523", {"start": v(-8.25, 36.19) * mm, "end": v(-9.72, 35.82) * mm});
            skLineSegment(sketch, "E2524", {"start": v(-9.72, 35.82) * mm, "end": v(-9.77, 35.68) * mm});
            skLineSegment(sketch, "E2525", {"start": v(-9.77, 35.68) * mm, "end": v(-9.8, 35.5) * mm});
            skLineSegment(sketch, "E2526", {"start": v(-9.8, 35.5) * mm, "end": v(-9.84, 35.32) * mm});
            skLineSegment(sketch, "E2527", {"start": v(-9.84, 35.32) * mm, "end": v(-9.87, 35.15) * mm});
            skLineSegment(sketch, "E2528", {"start": v(-9.87, 35.15) * mm, "end": v(-9.9, 34.98) * mm});
            skLineSegment(sketch, "E2529", {"start": v(-9.9, 34.98) * mm, "end": v(-9.93, 34.8) * mm});
            skLineSegment(sketch, "E2530", {"start": v(-9.93, 34.8) * mm, "end": v(-9.95, 34.65) * mm});
            skLineSegment(sketch, "E2531", {"start": v(-9.95, 34.65) * mm, "end": v(-9.98, 34.49) * mm});
            skLineSegment(sketch, "E2532", {"start": v(-9.98, 34.49) * mm, "end": v(-10, 34.33) * mm});
            skLineSegment(sketch, "E2533", {"start": v(-10, 34.33) * mm, "end": v(-10.01, 34.18) * mm});
            skLineSegment(sketch, "E2534", {"start": v(-10.01, 34.18) * mm, "end": v(-10.03, 34.03) * mm});
            skLineSegment(sketch, "E2535", {"start": v(-10.03, 34.03) * mm, "end": v(-10.04, 33.89) * mm});
            skLineSegment(sketch, "E2536", {"start": v(-10.04, 33.89) * mm, "end": v(-10.06, 33.75) * mm});
            skLineSegment(sketch, "E2537", {"start": v(-10.06, 33.75) * mm, "end": v(-10.07, 33.61) * mm});
            skLineSegment(sketch, "E2538", {"start": v(-10.07, 33.61) * mm, "end": v(-10.07, 33.48) * mm});
            skLineSegment(sketch, "E2539", {"start": v(-10.07, 33.48) * mm, "end": v(-10.08, 33.35) * mm});
            skLineSegment(sketch, "E2540", {"start": v(-10.08, 33.35) * mm, "end": v(-10.09, 33.22) * mm});
            skLineSegment(sketch, "E2541", {"start": v(-10.09, 33.22) * mm, "end": v(-10.1, 33.1) * mm});
            skLineSegment(sketch, "E2542", {"start": v(-10.1, 33.1) * mm, "end": v(-10.1, 32.99) * mm});
            skLineSegment(sketch, "E2543", {"start": v(-10.1, 32.99) * mm, "end": v(-10.1, 32.87) * mm});
            skLineSegment(sketch, "E2544", {"start": v(-10.1, 32.87) * mm, "end": v(-10.1, 32.76) * mm});
            skLineSegment(sketch, "E2545", {"start": v(-10.1, 32.76) * mm, "end": v(-10.1, 32.66) * mm});
            skLineSegment(sketch, "E2546", {"start": v(-10.1, 32.66) * mm, "end": v(-10.1, 32.55) * mm});
            skLineSegment(sketch, "E2547", {"start": v(-10.1, 32.55) * mm, "end": v(-10.09, 32.46) * mm});
            skLineSegment(sketch, "E2548", {"start": v(-10.09, 32.46) * mm, "end": v(-10.08, 32.36) * mm});
            skLineSegment(sketch, "E2549", {"start": v(-10.08, 32.36) * mm, "end": v(-10.08, 32.27) * mm});
            skLineSegment(sketch, "E2550", {"start": v(-10.08, 32.27) * mm, "end": v(-10.07, 32.19) * mm});
            skLineSegment(sketch, "E2551", {"start": v(-10.07, 32.19) * mm, "end": v(-10.07, 32.1) * mm});
            skLineSegment(sketch, "E2552", {"start": v(-10.07, 32.1) * mm, "end": v(-10.06, 32.03) * mm});
            skLineSegment(sketch, "E2553", {"start": v(-10.06, 32.03) * mm, "end": v(-10.05, 31.95) * mm});
            skLineSegment(sketch, "E2554", {"start": v(-10.05, 31.95) * mm, "end": v(-10.04, 31.88) * mm});
            skLineSegment(sketch, "E2555", {"start": v(-10.04, 31.88) * mm, "end": v(-10.04, 31.82) * mm});
            skLineSegment(sketch, "E2556", {"start": v(-10.04, 31.82) * mm, "end": v(-10.03, 31.75) * mm});
            skLineSegment(sketch, "E2557", {"start": v(-10.03, 31.75) * mm, "end": v(-10.02, 31.7) * mm});
            skLineSegment(sketch, "E2558", {"start": v(-10.02, 31.7) * mm, "end": v(-10.01, 31.64) * mm});
            skLineSegment(sketch, "E2559", {"start": v(-10.01, 31.64) * mm, "end": v(-10, 31.59) * mm});
            skLineSegment(sketch, "E2560", {"start": v(-10, 31.59) * mm, "end": v(-10, 31.54) * mm});
            skLineSegment(sketch, "E2561", {"start": v(-10, 31.54) * mm, "end": v(-9.99, 31.5) * mm});
            skLineSegment(sketch, "E2562", {"start": v(-9.99, 31.5) * mm, "end": v(-9.98, 31.46) * mm});
            skLineSegment(sketch, "E2563", {"start": v(-9.98, 31.46) * mm, "end": v(-9.97, 31.43) * mm});
            skLineSegment(sketch, "E2564", {"start": v(-9.97, 31.43) * mm, "end": v(-9.96, 31.4) * mm});
            skLineSegment(sketch, "E2565", {"start": v(-9.96, 31.4) * mm, "end": v(-9.96, 31.37) * mm});
            skLineSegment(sketch, "E2566", {"start": v(-9.96, 31.37) * mm, "end": v(-9.95, 31.35) * mm});
            skLineSegment(sketch, "E2567", {"start": v(-9.95, 31.35) * mm, "end": v(-9.95, 31.33) * mm});
            skLineSegment(sketch, "E2568", {"start": v(-9.95, 31.33) * mm, "end": v(-9.94, 31.31) * mm});
            skLineSegment(sketch, "E2569", {"start": v(-9.94, 31.31) * mm, "end": v(-9.94, 31.3) * mm});
            skLineSegment(sketch, "E2570", {"start": v(-9.94, 31.3) * mm, "end": v(-9.94, 31.3) * mm});
            skLineSegment(sketch, "E2571", {"start": v(-9.94, 31.3) * mm, "end": v(-9.81, 30.9) * mm});
            skLineSegment(sketch, "E2572", {"start": v(-9.81, 30.9) * mm, "end": v(-11.96, 30.14) * mm});
            skLineSegment(sketch, "E2573", {"start": v(-11.96, 30.14) * mm, "end": v(-12.11, 30.52) * mm});
            skLineSegment(sketch, "E2574", {"start": v(-12.11, 30.52) * mm, "end": v(-12.11, 30.52) * mm});
            skLineSegment(sketch, "E2575", {"start": v(-12.11, 30.52) * mm, "end": v(-12.12, 30.54) * mm});
            skLineSegment(sketch, "E2576", {"start": v(-12.12, 30.54) * mm, "end": v(-12.13, 30.55) * mm});
            skLineSegment(sketch, "E2577", {"start": v(-12.13, 30.55) * mm, "end": v(-12.13, 30.57) * mm});
            skLineSegment(sketch, "E2578", {"start": v(-12.13, 30.57) * mm, "end": v(-12.14, 30.59) * mm});
            skLineSegment(sketch, "E2579", {"start": v(-12.14, 30.59) * mm, "end": v(-12.16, 30.61) * mm});
            skLineSegment(sketch, "E2580", {"start": v(-12.16, 30.61) * mm, "end": v(-12.17, 30.64) * mm});
            skLineSegment(sketch, "E2581", {"start": v(-12.17, 30.64) * mm, "end": v(-12.19, 30.67) * mm});
            skLineSegment(sketch, "E2582", {"start": v(-12.19, 30.67) * mm, "end": v(-12.2, 30.7) * mm});
            skLineSegment(sketch, "E2583", {"start": v(-12.2, 30.7) * mm, "end": v(-12.23, 30.75) * mm});
            skLineSegment(sketch, "E2584", {"start": v(-12.23, 30.75) * mm, "end": v(-12.25, 30.79) * mm});
            skLineSegment(sketch, "E2585", {"start": v(-12.25, 30.79) * mm, "end": v(-12.27, 30.83) * mm});
            skLineSegment(sketch, "E2586", {"start": v(-12.27, 30.83) * mm, "end": v(-12.3, 30.88) * mm});
            skLineSegment(sketch, "E2587", {"start": v(-12.3, 30.88) * mm, "end": v(-12.33, 30.93) * mm});
            skLineSegment(sketch, "E2588", {"start": v(-12.33, 30.93) * mm, "end": v(-12.37, 30.98) * mm});
            skLineSegment(sketch, "E2589", {"start": v(-12.37, 30.98) * mm, "end": v(-12.4, 31.04) * mm});
            skLineSegment(sketch, "E2590", {"start": v(-12.4, 31.04) * mm, "end": v(-12.44, 31.1) * mm});
            skLineSegment(sketch, "E2591", {"start": v(-12.44, 31.1) * mm, "end": v(-12.48, 31.16) * mm});
            skLineSegment(sketch, "E2592", {"start": v(-12.48, 31.16) * mm, "end": v(-12.53, 31.23) * mm});
            skLineSegment(sketch, "E2593", {"start": v(-12.53, 31.23) * mm, "end": v(-12.57, 31.3) * mm});
            skLineSegment(sketch, "E2594", {"start": v(-12.57, 31.3) * mm, "end": v(-12.62, 31.36) * mm});
            skLineSegment(sketch, "E2595", {"start": v(-12.62, 31.36) * mm, "end": v(-12.68, 31.44) * mm});
            skLineSegment(sketch, "E2596", {"start": v(-12.68, 31.44) * mm, "end": v(-12.73, 31.51) * mm});
            skLineSegment(sketch, "E2597", {"start": v(-12.73, 31.51) * mm, "end": v(-12.8, 31.6) * mm});
            skLineSegment(sketch, "E2598", {"start": v(-12.8, 31.6) * mm, "end": v(-12.85, 31.67) * mm});
            skLineSegment(sketch, "E2599", {"start": v(-12.85, 31.67) * mm, "end": v(-12.92, 31.75) * mm});
            skLineSegment(sketch, "E2600", {"start": v(-12.92, 31.75) * mm, "end": v(-12.99, 31.84) * mm});
            skLineSegment(sketch, "E2601", {"start": v(-12.99, 31.84) * mm, "end": v(-13.06, 31.93) * mm});
            skLineSegment(sketch, "E2602", {"start": v(-13.06, 31.93) * mm, "end": v(-13.14, 32.02) * mm});
            skLineSegment(sketch, "E2603", {"start": v(-13.14, 32.02) * mm, "end": v(-13.22, 32.1) * mm});
            skLineSegment(sketch, "E2604", {"start": v(-13.22, 32.1) * mm, "end": v(-13.3, 32.2) * mm});
            skLineSegment(sketch, "E2605", {"start": v(-13.3, 32.2) * mm, "end": v(-13.39, 32.3) * mm});
            skLineSegment(sketch, "E2606", {"start": v(-13.39, 32.3) * mm, "end": v(-13.48, 32.4) * mm});
            skLineSegment(sketch, "E2607", {"start": v(-13.48, 32.4) * mm, "end": v(-13.57, 32.5) * mm});
            skLineSegment(sketch, "E2608", {"start": v(-13.57, 32.5) * mm, "end": v(-13.67, 32.6) * mm});
            skLineSegment(sketch, "E2609", {"start": v(-13.67, 32.6) * mm, "end": v(-13.77, 32.7) * mm});
            skLineSegment(sketch, "E2610", {"start": v(-13.77, 32.7) * mm, "end": v(-13.88, 32.8) * mm});
            skLineSegment(sketch, "E2611", {"start": v(-13.88, 32.8) * mm, "end": v(-14, 32.9) * mm});
            skLineSegment(sketch, "E2612", {"start": v(-14, 32.9) * mm, "end": v(-14.1, 33.02) * mm});
            skLineSegment(sketch, "E2613", {"start": v(-14.1, 33.02) * mm, "end": v(-14.22, 33.12) * mm});
            skLineSegment(sketch, "E2614", {"start": v(-14.22, 33.12) * mm, "end": v(-14.35, 33.23) * mm});
            skLineSegment(sketch, "E2615", {"start": v(-14.35, 33.23) * mm, "end": v(-14.47, 33.35) * mm});
            skLineSegment(sketch, "E2616", {"start": v(-14.47, 33.35) * mm, "end": v(-14.6, 33.46) * mm});
            skLineSegment(sketch, "E2617", {"start": v(-14.6, 33.46) * mm, "end": v(-14.74, 33.57) * mm});
            skLineSegment(sketch, "E2618", {"start": v(-14.74, 33.57) * mm, "end": v(-14.88, 33.69) * mm});
            skLineSegment(sketch, "E2619", {"start": v(-14.88, 33.69) * mm, "end": v(-15.02, 33.8) * mm});
            skLineSegment(sketch, "E2620", {"start": v(-15.02, 33.8) * mm, "end": v(-15.15, 33.88) * mm});
            skLineSegment(sketch, "E2621", {"start": v(-15.15, 33.88) * mm, "end": v(-16.52, 33.24) * mm});
            skLineSegment(sketch, "E2622", {"start": v(-16.52, 33.24) * mm, "end": v(-16.54, 33.08) * mm});
            skLineSegment(sketch, "E2623", {"start": v(-16.54, 33.08) * mm, "end": v(-16.54, 32.9) * mm});
            skLineSegment(sketch, "E2624", {"start": v(-16.54, 32.9) * mm, "end": v(-16.54, 32.72) * mm});
            skLineSegment(sketch, "E2625", {"start": v(-16.54, 32.72) * mm, "end": v(-16.54, 32.54) * mm});
            skLineSegment(sketch, "E2626", {"start": v(-16.54, 32.54) * mm, "end": v(-16.53, 32.37) * mm});
            skLineSegment(sketch, "E2627", {"start": v(-16.53, 32.37) * mm, "end": v(-16.53, 32.2) * mm});
            skLineSegment(sketch, "E2628", {"start": v(-16.53, 32.2) * mm, "end": v(-16.52, 32.04) * mm});
            skLineSegment(sketch, "E2629", {"start": v(-16.52, 32.04) * mm, "end": v(-16.51, 31.88) * mm});
            skLineSegment(sketch, "E2630", {"start": v(-16.51, 31.88) * mm, "end": v(-16.5, 31.72) * mm});
            skLineSegment(sketch, "E2631", {"start": v(-16.5, 31.72) * mm, "end": v(-16.49, 31.57) * mm});
            skLineSegment(sketch, "E2632", {"start": v(-16.49, 31.57) * mm, "end": v(-16.48, 31.42) * mm});
            skLineSegment(sketch, "E2633", {"start": v(-16.48, 31.42) * mm, "end": v(-16.46, 31.28) * mm});
            skLineSegment(sketch, "E2634", {"start": v(-16.46, 31.28) * mm, "end": v(-16.45, 31.14) * mm});
            skLineSegment(sketch, "E2635", {"start": v(-16.45, 31.14) * mm, "end": v(-16.43, 31) * mm});
            skLineSegment(sketch, "E2636", {"start": v(-16.43, 31) * mm, "end": v(-16.41, 30.87) * mm});
            skLineSegment(sketch, "E2637", {"start": v(-16.41, 30.87) * mm, "end": v(-16.4, 30.74) * mm});
            skLineSegment(sketch, "E2638", {"start": v(-16.4, 30.74) * mm, "end": v(-16.37, 30.62) * mm});
            skLineSegment(sketch, "E2639", {"start": v(-16.37, 30.62) * mm, "end": v(-16.36, 30.5) * mm});
            skLineSegment(sketch, "E2640", {"start": v(-16.36, 30.5) * mm, "end": v(-16.33, 30.38) * mm});
            skLineSegment(sketch, "E2641", {"start": v(-16.33, 30.38) * mm, "end": v(-16.31, 30.27) * mm});
            skLineSegment(sketch, "E2642", {"start": v(-16.31, 30.27) * mm, "end": v(-16.3, 30.16) * mm});
            skLineSegment(sketch, "E2643", {"start": v(-16.3, 30.16) * mm, "end": v(-16.27, 30.06) * mm});
            skLineSegment(sketch, "E2644", {"start": v(-16.27, 30.06) * mm, "end": v(-16.25, 29.96) * mm});
            skLineSegment(sketch, "E2645", {"start": v(-16.25, 29.96) * mm, "end": v(-16.23, 29.86) * mm});
            skLineSegment(sketch, "E2646", {"start": v(-16.23, 29.86) * mm, "end": v(-16.2, 29.77) * mm});
            skLineSegment(sketch, "E2647", {"start": v(-16.2, 29.77) * mm, "end": v(-16.18, 29.69) * mm});
            skLineSegment(sketch, "E2648", {"start": v(-16.18, 29.69) * mm, "end": v(-16.16, 29.6) * mm});
            skLineSegment(sketch, "E2649", {"start": v(-16.16, 29.6) * mm, "end": v(-16.14, 29.52) * mm});
            skLineSegment(sketch, "E2650", {"start": v(-16.14, 29.52) * mm, "end": v(-16.11, 29.45) * mm});
            skLineSegment(sketch, "E2651", {"start": v(-16.11, 29.45) * mm, "end": v(-16.1, 29.38) * mm});
            skLineSegment(sketch, "E2652", {"start": v(-16.1, 29.38) * mm, "end": v(-16.07, 29.3) * mm});
            skLineSegment(sketch, "E2653", {"start": v(-16.07, 29.3) * mm, "end": v(-16.05, 29.25) * mm});
            skLineSegment(sketch, "E2654", {"start": v(-16.05, 29.25) * mm, "end": v(-16.03, 29.19) * mm});
            skLineSegment(sketch, "E2655", {"start": v(-16.03, 29.19) * mm, "end": v(-16.01, 29.13) * mm});
            skLineSegment(sketch, "E2656", {"start": v(-16.01, 29.13) * mm, "end": v(-16, 29.08) * mm});
            skLineSegment(sketch, "E2657", {"start": v(-16, 29.08) * mm, "end": v(-15.97, 29.03) * mm});
            skLineSegment(sketch, "E2658", {"start": v(-15.97, 29.03) * mm, "end": v(-15.96, 28.99) * mm});
            skLineSegment(sketch, "E2659", {"start": v(-15.96, 28.99) * mm, "end": v(-15.94, 28.95) * mm});
            skLineSegment(sketch, "E2660", {"start": v(-15.94, 28.95) * mm, "end": v(-15.92, 28.91) * mm});
            skLineSegment(sketch, "E2661", {"start": v(-15.92, 28.91) * mm, "end": v(-15.91, 28.88) * mm});
            skLineSegment(sketch, "E2662", {"start": v(-15.91, 28.88) * mm, "end": v(-15.9, 28.85) * mm});
            skLineSegment(sketch, "E2663", {"start": v(-15.9, 28.85) * mm, "end": v(-15.89, 28.82) * mm});
            skLineSegment(sketch, "E2664", {"start": v(-15.89, 28.82) * mm, "end": v(-15.88, 28.8) * mm});
            skLineSegment(sketch, "E2665", {"start": v(-15.88, 28.8) * mm, "end": v(-15.87, 28.78) * mm});
            skLineSegment(sketch, "E2666", {"start": v(-15.87, 28.78) * mm, "end": v(-15.86, 28.77) * mm});
            skLineSegment(sketch, "E2667", {"start": v(-15.86, 28.77) * mm, "end": v(-15.86, 28.76) * mm});
            skLineSegment(sketch, "E2668", {"start": v(-15.86, 28.76) * mm, "end": v(-15.85, 28.75) * mm});
            skLineSegment(sketch, "E2669", {"start": v(-15.85, 28.75) * mm, "end": v(-15.65, 28.4) * mm});
            skLineSegment(sketch, "E2670", {"start": v(-15.65, 28.4) * mm, "end": v(-17.6, 27.22) * mm});
            skLineSegment(sketch, "E2671", {"start": v(-17.6, 27.22) * mm, "end": v(-17.83, 27.57) * mm});
            skLineSegment(sketch, "E2672", {"start": v(-17.83, 27.57) * mm, "end": v(-17.84, 27.57) * mm});
            skLineSegment(sketch, "E2673", {"start": v(-17.84, 27.57) * mm, "end": v(-17.84, 27.58) * mm});
            skLineSegment(sketch, "E2674", {"start": v(-17.84, 27.58) * mm, "end": v(-17.85, 27.6) * mm});
            skLineSegment(sketch, "E2675", {"start": v(-17.85, 27.6) * mm, "end": v(-17.86, 27.61) * mm});
            skLineSegment(sketch, "E2676", {"start": v(-17.86, 27.61) * mm, "end": v(-17.88, 27.63) * mm});
            skLineSegment(sketch, "E2677", {"start": v(-17.88, 27.63) * mm, "end": v(-17.9, 27.65) * mm});
            skLineSegment(sketch, "E2678", {"start": v(-17.9, 27.65) * mm, "end": v(-17.91, 27.68) * mm});
            skLineSegment(sketch, "E2679", {"start": v(-17.91, 27.68) * mm, "end": v(-17.94, 27.7) * mm});
            skLineSegment(sketch, "E2680", {"start": v(-17.94, 27.7) * mm, "end": v(-17.96, 27.74) * mm});
            skLineSegment(sketch, "E2681", {"start": v(-17.96, 27.74) * mm, "end": v(-17.99, 27.77) * mm});
            skLineSegment(sketch, "E2682", {"start": v(-17.99, 27.77) * mm, "end": v(-18.02, 27.8) * mm});
            skLineSegment(sketch, "E2683", {"start": v(-18.02, 27.8) * mm, "end": v(-18.05, 27.85) * mm});
            skLineSegment(sketch, "E2684", {"start": v(-18.05, 27.85) * mm, "end": v(-18.1, 27.89) * mm});
            skLineSegment(sketch, "E2685", {"start": v(-18.1, 27.89) * mm, "end": v(-18.13, 27.93) * mm});
            skLineSegment(sketch, "E2686", {"start": v(-18.13, 27.93) * mm, "end": v(-18.17, 27.98) * mm});
            skLineSegment(sketch, "E2687", {"start": v(-18.17, 27.98) * mm, "end": v(-18.22, 28.02) * mm});
            skLineSegment(sketch, "E2688", {"start": v(-18.22, 28.02) * mm, "end": v(-18.27, 28.08) * mm});
            skLineSegment(sketch, "E2689", {"start": v(-18.27, 28.08) * mm, "end": v(-18.32, 28.13) * mm});
            skLineSegment(sketch, "E2690", {"start": v(-18.32, 28.13) * mm, "end": v(-18.38, 28.18) * mm});
            skLineSegment(sketch, "E2691", {"start": v(-18.38, 28.18) * mm, "end": v(-18.44, 28.24) * mm});
            skLineSegment(sketch, "E2692", {"start": v(-18.44, 28.24) * mm, "end": v(-18.5, 28.3) * mm});
            skLineSegment(sketch, "E2693", {"start": v(-18.5, 28.3) * mm, "end": v(-18.57, 28.36) * mm});
            skLineSegment(sketch, "E2694", {"start": v(-18.57, 28.36) * mm, "end": v(-18.64, 28.42) * mm});
            skLineSegment(sketch, "E2695", {"start": v(-18.64, 28.42) * mm, "end": v(-18.7, 28.49) * mm});
            skLineSegment(sketch, "E2696", {"start": v(-18.7, 28.49) * mm, "end": v(-18.79, 28.56) * mm});
            skLineSegment(sketch, "E2697", {"start": v(-18.79, 28.56) * mm, "end": v(-18.87, 28.62) * mm});
            skLineSegment(sketch, "E2698", {"start": v(-18.87, 28.62) * mm, "end": v(-18.95, 28.7) * mm});
            skLineSegment(sketch, "E2699", {"start": v(-18.95, 28.7) * mm, "end": v(-19.04, 28.76) * mm});
            skLineSegment(sketch, "E2700", {"start": v(-19.04, 28.76) * mm, "end": v(-19.13, 28.84) * mm});
            skLineSegment(sketch, "E2701", {"start": v(-19.13, 28.84) * mm, "end": v(-19.23, 28.91) * mm});
            skLineSegment(sketch, "E2702", {"start": v(-19.23, 28.91) * mm, "end": v(-19.33, 28.99) * mm});
            skLineSegment(sketch, "E2703", {"start": v(-19.33, 28.99) * mm, "end": v(-19.43, 29.06) * mm});
            skLineSegment(sketch, "E2704", {"start": v(-19.43, 29.06) * mm, "end": v(-19.54, 29.14) * mm});
            skLineSegment(sketch, "E2705", {"start": v(-19.54, 29.14) * mm, "end": v(-19.65, 29.22) * mm});
            skLineSegment(sketch, "E2706", {"start": v(-19.65, 29.22) * mm, "end": v(-19.77, 29.3) * mm});
            skLineSegment(sketch, "E2707", {"start": v(-19.77, 29.3) * mm, "end": v(-19.89, 29.38) * mm});
            skLineSegment(sketch, "E2708", {"start": v(-19.89, 29.38) * mm, "end": v(-20.01, 29.46) * mm});
            skLineSegment(sketch, "E2709", {"start": v(-20.01, 29.46) * mm, "end": v(-20.14, 29.55) * mm});
            skLineSegment(sketch, "E2710", {"start": v(-20.14, 29.55) * mm, "end": v(-20.27, 29.63) * mm});
            skLineSegment(sketch, "E2711", {"start": v(-20.27, 29.63) * mm, "end": v(-20.41, 29.71) * mm});
            skLineSegment(sketch, "E2712", {"start": v(-20.41, 29.71) * mm, "end": v(-20.55, 29.8) * mm});
            skLineSegment(sketch, "E2713", {"start": v(-20.55, 29.8) * mm, "end": v(-20.7, 29.88) * mm});
            skLineSegment(sketch, "E2714", {"start": v(-20.7, 29.88) * mm, "end": v(-20.85, 29.97) * mm});
            skLineSegment(sketch, "E2715", {"start": v(-20.85, 29.97) * mm, "end": v(-21, 30.05) * mm});
            skLineSegment(sketch, "E2716", {"start": v(-21, 30.05) * mm, "end": v(-21.16, 30.14) * mm});
            skLineSegment(sketch, "E2717", {"start": v(-21.16, 30.14) * mm, "end": v(-21.32, 30.22) * mm});
            skLineSegment(sketch, "E2718", {"start": v(-21.32, 30.22) * mm, "end": v(-21.47, 30.28) * mm});
            skLineSegment(sketch, "E2719", {"start": v(-21.47, 30.28) * mm, "end": v(-22.68, 29.38) * mm});
            skLineSegment(sketch, "E2720", {"start": v(-22.68, 29.38) * mm, "end": v(-22.67, 29.22) * mm});
            skLineSegment(sketch, "E2721", {"start": v(-22.67, 29.22) * mm, "end": v(-22.64, 29.04) * mm});
            skLineSegment(sketch, "E2722", {"start": v(-22.64, 29.04) * mm, "end": v(-22.6, 28.87) * mm});
            skLineSegment(sketch, "E2723", {"start": v(-22.6, 28.87) * mm, "end": v(-22.57, 28.7) * mm});
            skLineSegment(sketch, "E2724", {"start": v(-22.57, 28.7) * mm, "end": v(-22.53, 28.52) * mm});
            skLineSegment(sketch, "E2725", {"start": v(-22.53, 28.52) * mm, "end": v(-22.5, 28.36) * mm});
            skLineSegment(sketch, "E2726", {"start": v(-22.5, 28.36) * mm, "end": v(-22.45, 28.2) * mm});
            skLineSegment(sketch, "E2727", {"start": v(-22.45, 28.2) * mm, "end": v(-22.41, 28.05) * mm});
            skLineSegment(sketch, "E2728", {"start": v(-22.41, 28.05) * mm, "end": v(-22.37, 27.9) * mm});
            skLineSegment(sketch, "E2729", {"start": v(-22.37, 27.9) * mm, "end": v(-22.33, 27.75) * mm});
            skLineSegment(sketch, "E2730", {"start": v(-22.33, 27.75) * mm, "end": v(-22.3, 27.6) * mm});
            skLineSegment(sketch, "E2731", {"start": v(-22.3, 27.6) * mm, "end": v(-22.25, 27.47) * mm});
            skLineSegment(sketch, "E2732", {"start": v(-22.25, 27.47) * mm, "end": v(-22.2, 27.33) * mm});
            skLineSegment(sketch, "E2733", {"start": v(-22.2, 27.33) * mm, "end": v(-22.16, 27.2) * mm});
            skLineSegment(sketch, "E2734", {"start": v(-22.16, 27.2) * mm, "end": v(-22.12, 27.08) * mm});
            skLineSegment(sketch, "E2735", {"start": v(-22.12, 27.08) * mm, "end": v(-22.08, 26.95) * mm});
            skLineSegment(sketch, "E2736", {"start": v(-22.08, 26.95) * mm, "end": v(-22.03, 26.84) * mm});
            skLineSegment(sketch, "E2737", {"start": v(-22.03, 26.84) * mm, "end": v(-22, 26.72) * mm});
            skLineSegment(sketch, "E2738", {"start": v(-22, 26.72) * mm, "end": v(-21.95, 26.61) * mm});
            skLineSegment(sketch, "E2739", {"start": v(-21.95, 26.61) * mm, "end": v(-21.9, 26.5) * mm});
            skLineSegment(sketch, "E2740", {"start": v(-21.9, 26.5) * mm, "end": v(-21.86, 26.4) * mm});
            skLineSegment(sketch, "E2741", {"start": v(-21.86, 26.4) * mm, "end": v(-21.82, 26.3) * mm});
            skLineSegment(sketch, "E2742", {"start": v(-21.82, 26.3) * mm, "end": v(-21.78, 26.21) * mm});
            skLineSegment(sketch, "E2743", {"start": v(-21.78, 26.21) * mm, "end": v(-21.74, 26.13) * mm});
            skLineSegment(sketch, "E2744", {"start": v(-21.74, 26.13) * mm, "end": v(-21.7, 26.04) * mm});
            skLineSegment(sketch, "E2745", {"start": v(-21.7, 26.04) * mm, "end": v(-21.66, 25.96) * mm});
            skLineSegment(sketch, "E2746", {"start": v(-21.66, 25.96) * mm, "end": v(-21.62, 25.88) * mm});
            skLineSegment(sketch, "E2747", {"start": v(-21.62, 25.88) * mm, "end": v(-21.59, 25.8) * mm});
            skLineSegment(sketch, "E2748", {"start": v(-21.59, 25.8) * mm, "end": v(-21.55, 25.74) * mm});
            skLineSegment(sketch, "E2749", {"start": v(-21.55, 25.74) * mm, "end": v(-21.51, 25.67) * mm});
            skLineSegment(sketch, "E2750", {"start": v(-21.51, 25.67) * mm, "end": v(-21.48, 25.61) * mm});
            skLineSegment(sketch, "E2751", {"start": v(-21.48, 25.61) * mm, "end": v(-21.45, 25.55) * mm});
            skLineSegment(sketch, "E2752", {"start": v(-21.45, 25.55) * mm, "end": v(-21.42, 25.5) * mm});
            skLineSegment(sketch, "E2753", {"start": v(-21.42, 25.5) * mm, "end": v(-21.39, 25.45) * mm});
            skLineSegment(sketch, "E2754", {"start": v(-21.39, 25.45) * mm, "end": v(-21.36, 25.4) * mm});
            skLineSegment(sketch, "E2755", {"start": v(-21.36, 25.4) * mm, "end": v(-21.33, 25.36) * mm});
            skLineSegment(sketch, "E2756", {"start": v(-21.33, 25.36) * mm, "end": v(-21.3, 25.32) * mm});
            skLineSegment(sketch, "E2757", {"start": v(-21.3, 25.32) * mm, "end": v(-21.28, 25.28) * mm});
            skLineSegment(sketch, "E2758", {"start": v(-21.28, 25.28) * mm, "end": v(-21.26, 25.25) * mm});
            skLineSegment(sketch, "E2759", {"start": v(-21.26, 25.25) * mm, "end": v(-21.24, 25.22) * mm});
            skLineSegment(sketch, "E2760", {"start": v(-21.24, 25.22) * mm, "end": v(-21.22, 25.2) * mm});
            skLineSegment(sketch, "E2761", {"start": v(-21.22, 25.2) * mm, "end": v(-21.2, 25.17) * mm});
            skLineSegment(sketch, "E2762", {"start": v(-21.2, 25.17) * mm, "end": v(-21.2, 25.15) * mm});
            skLineSegment(sketch, "E2763", {"start": v(-21.2, 25.15) * mm, "end": v(-21.18, 25.14) * mm});
            skLineSegment(sketch, "E2764", {"start": v(-21.18, 25.14) * mm, "end": v(-21.17, 25.12) * mm});
            skLineSegment(sketch, "E2765", {"start": v(-21.17, 25.12) * mm, "end": v(-21.16, 25.11) * mm});
            skLineSegment(sketch, "E2766", {"start": v(-21.16, 25.11) * mm, "end": v(-21.16, 25.1) * mm});
            skLineSegment(sketch, "E2767", {"start": v(-21.16, 25.1) * mm, "end": v(-20.9, 24.8) * mm});
            skLineSegment(sketch, "E2768", {"start": v(-20.9, 24.8) * mm, "end": v(-22.58, 23.27) * mm});
            skLineSegment(sketch, "E2769", {"start": v(-22.58, 23.27) * mm, "end": v(-22.87, 23.56) * mm});
            skLineSegment(sketch, "E2770", {"start": v(-22.87, 23.56) * mm, "end": v(-22.87, 23.56) * mm});
            skLineSegment(sketch, "E2771", {"start": v(-22.87, 23.56) * mm, "end": v(-22.88, 23.57) * mm});
            skLineSegment(sketch, "E2772", {"start": v(-22.88, 23.57) * mm, "end": v(-22.9, 23.58) * mm});
            skLineSegment(sketch, "E2773", {"start": v(-22.9, 23.58) * mm, "end": v(-22.9, 23.6) * mm});
            skLineSegment(sketch, "E2774", {"start": v(-22.9, 23.6) * mm, "end": v(-22.93, 23.61) * mm});
            skLineSegment(sketch, "E2775", {"start": v(-22.93, 23.61) * mm, "end": v(-22.95, 23.63) * mm});
            skLineSegment(sketch, "E2776", {"start": v(-22.95, 23.63) * mm, "end": v(-22.97, 23.65) * mm});
            skLineSegment(sketch, "E2777", {"start": v(-22.97, 23.65) * mm, "end": v(-23, 23.68) * mm});
            skLineSegment(sketch, "E2778", {"start": v(-23, 23.68) * mm, "end": v(-23.03, 23.7) * mm});
            skLineSegment(sketch, "E2779", {"start": v(-23.03, 23.7) * mm, "end": v(-23.06, 23.73) * mm});
            skLineSegment(sketch, "E2780", {"start": v(-23.06, 23.73) * mm, "end": v(-23.1, 23.76) * mm});
            skLineSegment(sketch, "E2781", {"start": v(-23.1, 23.76) * mm, "end": v(-23.14, 23.79) * mm});
            skLineSegment(sketch, "E2782", {"start": v(-23.14, 23.79) * mm, "end": v(-23.18, 23.82) * mm});
            skLineSegment(sketch, "E2783", {"start": v(-23.18, 23.82) * mm, "end": v(-23.23, 23.86) * mm});
            skLineSegment(sketch, "E2784", {"start": v(-23.23, 23.86) * mm, "end": v(-23.28, 23.9) * mm});
            skLineSegment(sketch, "E2785", {"start": v(-23.28, 23.9) * mm, "end": v(-23.34, 23.93) * mm});
            skLineSegment(sketch, "E2786", {"start": v(-23.34, 23.93) * mm, "end": v(-23.4, 23.97) * mm});
            skLineSegment(sketch, "E2787", {"start": v(-23.4, 23.97) * mm, "end": v(-23.46, 24.01) * mm});
            skLineSegment(sketch, "E2788", {"start": v(-23.46, 24.01) * mm, "end": v(-23.52, 24.06) * mm});
            skLineSegment(sketch, "E2789", {"start": v(-23.52, 24.06) * mm, "end": v(-23.6, 24.1) * mm});
            skLineSegment(sketch, "E2790", {"start": v(-23.6, 24.1) * mm, "end": v(-23.66, 24.15) * mm});
            skLineSegment(sketch, "E2791", {"start": v(-23.66, 24.15) * mm, "end": v(-23.74, 24.2) * mm});
            skLineSegment(sketch, "E2792", {"start": v(-23.74, 24.2) * mm, "end": v(-23.82, 24.24) * mm});
            skLineSegment(sketch, "E2793", {"start": v(-23.82, 24.24) * mm, "end": v(-23.9, 24.3) * mm});
            skLineSegment(sketch, "E2794", {"start": v(-23.9, 24.3) * mm, "end": v(-24, 24.34) * mm});
            skLineSegment(sketch, "E2795", {"start": v(-24, 24.34) * mm, "end": v(-24.09, 24.4) * mm});
            skLineSegment(sketch, "E2796", {"start": v(-24.09, 24.4) * mm, "end": v(-24.19, 24.44) * mm});
            skLineSegment(sketch, "E2797", {"start": v(-24.19, 24.44) * mm, "end": v(-24.29, 24.5) * mm});
            skLineSegment(sketch, "E2798", {"start": v(-24.29, 24.5) * mm, "end": v(-24.4, 24.55) * mm});
            skLineSegment(sketch, "E2799", {"start": v(-24.4, 24.55) * mm, "end": v(-24.5, 24.6) * mm});
            skLineSegment(sketch, "E2800", {"start": v(-24.5, 24.6) * mm, "end": v(-24.61, 24.66) * mm});
            skLineSegment(sketch, "E2801", {"start": v(-24.61, 24.66) * mm, "end": v(-24.73, 24.71) * mm});
            skLineSegment(sketch, "E2802", {"start": v(-24.73, 24.71) * mm, "end": v(-24.85, 24.77) * mm});
            skLineSegment(sketch, "E2803", {"start": v(-24.85, 24.77) * mm, "end": v(-24.98, 24.83) * mm});
            skLineSegment(sketch, "E2804", {"start": v(-24.98, 24.83) * mm, "end": v(-25.1, 24.88) * mm});
            skLineSegment(sketch, "E2805", {"start": v(-25.1, 24.88) * mm, "end": v(-25.24, 24.94) * mm});
            skLineSegment(sketch, "E2806", {"start": v(-25.24, 24.94) * mm, "end": v(-25.38, 25) * mm});
            skLineSegment(sketch, "E2807", {"start": v(-25.38, 25) * mm, "end": v(-25.52, 25.05) * mm});
            skLineSegment(sketch, "E2808", {"start": v(-25.52, 25.05) * mm, "end": v(-25.67, 25.1) * mm});
            skLineSegment(sketch, "E2809", {"start": v(-25.67, 25.1) * mm, "end": v(-25.82, 25.16) * mm});
            skLineSegment(sketch, "E2810", {"start": v(-25.82, 25.16) * mm, "end": v(-25.97, 25.21) * mm});
            skLineSegment(sketch, "E2811", {"start": v(-25.97, 25.21) * mm, "end": v(-26.13, 25.27) * mm});
            skLineSegment(sketch, "E2812", {"start": v(-26.13, 25.27) * mm, "end": v(-26.3, 25.32) * mm});
            skLineSegment(sketch, "E2813", {"start": v(-26.3, 25.32) * mm, "end": v(-26.46, 25.38) * mm});
            skLineSegment(sketch, "E2814", {"start": v(-26.46, 25.38) * mm, "end": v(-26.63, 25.43) * mm});
            skLineSegment(sketch, "E2815", {"start": v(-26.63, 25.43) * mm, "end": v(-26.81, 25.48) * mm});
            skLineSegment(sketch, "E2816", {"start": v(-26.81, 25.48) * mm, "end": v(-26.96, 25.5) * mm});
            skLineSegment(sketch, "E2817", {"start": v(-26.96, 25.5) * mm, "end": v(-27.98, 24.39) * mm});
            skLineSegment(sketch, "E2818", {"start": v(-27.98, 24.39) * mm, "end": v(-27.94, 24.24) * mm});
            skLineSegment(sketch, "E2819", {"start": v(-27.94, 24.24) * mm, "end": v(-27.87, 24.07) * mm});
            skLineSegment(sketch, "E2820", {"start": v(-27.87, 24.07) * mm, "end": v(-27.8, 23.9) * mm});
            skLineSegment(sketch, "E2821", {"start": v(-27.8, 23.9) * mm, "end": v(-27.73, 23.74) * mm});
            skLineSegment(sketch, "E2822", {"start": v(-27.73, 23.74) * mm, "end": v(-27.66, 23.58) * mm});
            skLineSegment(sketch, "E2823", {"start": v(-27.66, 23.58) * mm, "end": v(-27.6, 23.43) * mm});
            skLineSegment(sketch, "E2824", {"start": v(-27.6, 23.43) * mm, "end": v(-27.52, 23.28) * mm});
            skLineSegment(sketch, "E2825", {"start": v(-27.52, 23.28) * mm, "end": v(-27.45, 23.13) * mm});
            skLineSegment(sketch, "E2826", {"start": v(-27.45, 23.13) * mm, "end": v(-27.39, 23) * mm});
            skLineSegment(sketch, "E2827", {"start": v(-27.39, 23) * mm, "end": v(-27.32, 22.86) * mm});
            skLineSegment(sketch, "E2828", {"start": v(-27.32, 22.86) * mm, "end": v(-27.25, 22.73) * mm});
            skLineSegment(sketch, "E2829", {"start": v(-27.25, 22.73) * mm, "end": v(-27.18, 22.6) * mm});
            skLineSegment(sketch, "E2830", {"start": v(-27.18, 22.6) * mm, "end": v(-27.11, 22.47) * mm});
            skLineSegment(sketch, "E2831", {"start": v(-27.11, 22.47) * mm, "end": v(-27.04, 22.35) * mm});
            skLineSegment(sketch, "E2832", {"start": v(-27.04, 22.35) * mm, "end": v(-26.98, 22.24) * mm});
            skLineSegment(sketch, "E2833", {"start": v(-26.98, 22.24) * mm, "end": v(-26.91, 22.13) * mm});
            skLineSegment(sketch, "E2834", {"start": v(-26.91, 22.13) * mm, "end": v(-26.85, 22.02) * mm});
            skLineSegment(sketch, "E2835", {"start": v(-26.85, 22.02) * mm, "end": v(-26.78, 21.92) * mm});
            skLineSegment(sketch, "E2836", {"start": v(-26.78, 21.92) * mm, "end": v(-26.72, 21.82) * mm});
            skLineSegment(sketch, "E2837", {"start": v(-26.72, 21.82) * mm, "end": v(-26.66, 21.72) * mm});
            skLineSegment(sketch, "E2838", {"start": v(-26.66, 21.72) * mm, "end": v(-26.6, 21.63) * mm});
            skLineSegment(sketch, "E2839", {"start": v(-26.6, 21.63) * mm, "end": v(-26.53, 21.55) * mm});
            skLineSegment(sketch, "E2840", {"start": v(-26.53, 21.55) * mm, "end": v(-26.48, 21.46) * mm});
            skLineSegment(sketch, "E2841", {"start": v(-26.48, 21.46) * mm, "end": v(-26.42, 21.38) * mm});
            skLineSegment(sketch, "E2842", {"start": v(-26.42, 21.38) * mm, "end": v(-26.36, 21.3) * mm});
            skLineSegment(sketch, "E2843", {"start": v(-26.36, 21.3) * mm, "end": v(-26.3, 21.23) * mm});
            skLineSegment(sketch, "E2844", {"start": v(-26.3, 21.23) * mm, "end": v(-26.26, 21.17) * mm});
            skLineSegment(sketch, "E2845", {"start": v(-26.26, 21.17) * mm, "end": v(-26.2, 21.1) * mm});
            skLineSegment(sketch, "E2846", {"start": v(-26.2, 21.1) * mm, "end": v(-26.16, 21.04) * mm});
            skLineSegment(sketch, "E2847", {"start": v(-26.16, 21.04) * mm, "end": v(-26.1, 20.98) * mm});
            skLineSegment(sketch, "E2848", {"start": v(-26.1, 20.98) * mm, "end": v(-26.06, 20.93) * mm});
            skLineSegment(sketch, "E2849", {"start": v(-26.06, 20.93) * mm, "end": v(-26.02, 20.88) * mm});
            skLineSegment(sketch, "E2850", {"start": v(-26.02, 20.88) * mm, "end": v(-25.98, 20.83) * mm});
            skLineSegment(sketch, "E2851", {"start": v(-25.98, 20.83) * mm, "end": v(-25.94, 20.79) * mm});
            skLineSegment(sketch, "E2852", {"start": v(-25.94, 20.79) * mm, "end": v(-25.9, 20.75) * mm});
            skLineSegment(sketch, "E2853", {"start": v(-25.9, 20.75) * mm, "end": v(-25.87, 20.7) * mm});
            skLineSegment(sketch, "E2854", {"start": v(-25.87, 20.7) * mm, "end": v(-25.83, 20.67) * mm});
            skLineSegment(sketch, "E2855", {"start": v(-25.83, 20.67) * mm, "end": v(-25.8, 20.64) * mm});
            skLineSegment(sketch, "E2856", {"start": v(-25.8, 20.64) * mm, "end": v(-25.78, 20.62) * mm});
            skLineSegment(sketch, "E2857", {"start": v(-25.78, 20.62) * mm, "end": v(-25.75, 20.6) * mm});
            skLineSegment(sketch, "E2858", {"start": v(-25.75, 20.6) * mm, "end": v(-25.73, 20.57) * mm});
            skLineSegment(sketch, "E2859", {"start": v(-25.73, 20.57) * mm, "end": v(-25.7, 20.55) * mm});
            skLineSegment(sketch, "E2860", {"start": v(-25.7, 20.55) * mm, "end": v(-25.69, 20.53) * mm});
            skLineSegment(sketch, "E2861", {"start": v(-25.69, 20.53) * mm, "end": v(-25.67, 20.52) * mm});
            skLineSegment(sketch, "E2862", {"start": v(-25.67, 20.52) * mm, "end": v(-25.66, 20.51) * mm});
            skLineSegment(sketch, "E2863", {"start": v(-25.66, 20.51) * mm, "end": v(-25.65, 20.5) * mm});
            skLineSegment(sketch, "E2864", {"start": v(-25.65, 20.5) * mm, "end": v(-25.65, 20.5) * mm});
            skLineSegment(sketch, "E2865", {"start": v(-25.65, 20.5) * mm, "end": v(-25.33, 20.24) * mm});
            skLineSegment(sketch, "E2866", {"start": v(-25.33, 20.24) * mm, "end": v(-26.69, 18.41) * mm});
            skLineSegment(sketch, "E2867", {"start": v(-26.69, 18.41) * mm, "end": v(-27.02, 18.65) * mm});
            skLineSegment(sketch, "E2868", {"start": v(-27.02, 18.65) * mm, "end": v(-27.03, 18.65) * mm});
            skLineSegment(sketch, "E2869", {"start": v(-27.03, 18.65) * mm, "end": v(-27.04, 18.66) * mm});
            skLineSegment(sketch, "E2870", {"start": v(-27.04, 18.66) * mm, "end": v(-27.05, 18.66) * mm});
            skLineSegment(sketch, "E2871", {"start": v(-27.05, 18.66) * mm, "end": v(-27.07, 18.68) * mm});
            skLineSegment(sketch, "E2872", {"start": v(-27.07, 18.68) * mm, "end": v(-27.1, 18.69) * mm});
            skLineSegment(sketch, "E2873", {"start": v(-27.1, 18.69) * mm, "end": v(-27.12, 18.7) * mm});
            skLineSegment(sketch, "E2874", {"start": v(-27.12, 18.7) * mm, "end": v(-27.14, 18.72) * mm});
            skLineSegment(sketch, "E2875", {"start": v(-27.14, 18.72) * mm, "end": v(-27.17, 18.73) * mm});
            skLineSegment(sketch, "E2876", {"start": v(-27.17, 18.73) * mm, "end": v(-27.2, 18.75) * mm});
            skLineSegment(sketch, "E2877", {"start": v(-27.2, 18.75) * mm, "end": v(-27.25, 18.77) * mm});
            skLineSegment(sketch, "E2878", {"start": v(-27.25, 18.77) * mm, "end": v(-27.29, 18.8) * mm});
            skLineSegment(sketch, "E2879", {"start": v(-27.29, 18.8) * mm, "end": v(-27.34, 18.82) * mm});
            skLineSegment(sketch, "E2880", {"start": v(-27.34, 18.82) * mm, "end": v(-27.38, 18.84) * mm});
            skLineSegment(sketch, "E2881", {"start": v(-27.38, 18.84) * mm, "end": v(-27.44, 18.87) * mm});
            skLineSegment(sketch, "E2882", {"start": v(-27.44, 18.87) * mm, "end": v(-27.5, 18.9) * mm});
            skLineSegment(sketch, "E2883", {"start": v(-27.5, 18.9) * mm, "end": v(-27.56, 18.92) * mm});
            skLineSegment(sketch, "E2884", {"start": v(-27.56, 18.92) * mm, "end": v(-27.62, 18.95) * mm});
            skLineSegment(sketch, "E2885", {"start": v(-27.62, 18.95) * mm, "end": v(-27.7, 18.98) * mm});
            skLineSegment(sketch, "E2886", {"start": v(-27.7, 18.98) * mm, "end": v(-27.76, 19) * mm});
            skLineSegment(sketch, "E2887", {"start": v(-27.76, 19) * mm, "end": v(-27.84, 19.04) * mm});
            skLineSegment(sketch, "E2888", {"start": v(-27.84, 19.04) * mm, "end": v(-27.92, 19.07) * mm});
            skLineSegment(sketch, "E2889", {"start": v(-27.92, 19.07) * mm, "end": v(-28, 19.1) * mm});
            skLineSegment(sketch, "E2890", {"start": v(-28, 19.1) * mm, "end": v(-28.1, 19.13) * mm});
            skLineSegment(sketch, "E2891", {"start": v(-28.1, 19.13) * mm, "end": v(-28.19, 19.16) * mm});
            skLineSegment(sketch, "E2892", {"start": v(-28.19, 19.16) * mm, "end": v(-28.28, 19.2) * mm});
            skLineSegment(sketch, "E2893", {"start": v(-28.28, 19.2) * mm, "end": v(-28.38, 19.22) * mm});
            skLineSegment(sketch, "E2894", {"start": v(-28.38, 19.22) * mm, "end": v(-28.49, 19.26) * mm});
            skLineSegment(sketch, "E2895", {"start": v(-28.49, 19.26) * mm, "end": v(-28.6, 19.29) * mm});
            skLineSegment(sketch, "E2896", {"start": v(-28.6, 19.29) * mm, "end": v(-28.71, 19.32) * mm});
            skLineSegment(sketch, "E2897", {"start": v(-28.71, 19.32) * mm, "end": v(-28.83, 19.35) * mm});
            skLineSegment(sketch, "E2898", {"start": v(-28.83, 19.35) * mm, "end": v(-28.95, 19.38) * mm});
            skLineSegment(sketch, "E2899", {"start": v(-28.95, 19.38) * mm, "end": v(-29.08, 19.42) * mm});
            skLineSegment(sketch, "E2900", {"start": v(-29.08, 19.42) * mm, "end": v(-29.2, 19.45) * mm});
            skLineSegment(sketch, "E2901", {"start": v(-29.2, 19.45) * mm, "end": v(-29.34, 19.48) * mm});
            skLineSegment(sketch, "E2902", {"start": v(-29.34, 19.48) * mm, "end": v(-29.48, 19.5) * mm});
            skLineSegment(sketch, "E2903", {"start": v(-29.48, 19.5) * mm, "end": v(-29.62, 19.53) * mm});
            skLineSegment(sketch, "E2904", {"start": v(-29.62, 19.53) * mm, "end": v(-29.77, 19.56) * mm});
            skLineSegment(sketch, "E2905", {"start": v(-29.77, 19.56) * mm, "end": v(-29.92, 19.59) * mm});
            skLineSegment(sketch, "E2906", {"start": v(-29.92, 19.59) * mm, "end": v(-30.07, 19.61) * mm});
            skLineSegment(sketch, "E2907", {"start": v(-30.07, 19.61) * mm, "end": v(-30.23, 19.64) * mm});
            skLineSegment(sketch, "E2908", {"start": v(-30.23, 19.64) * mm, "end": v(-30.4, 19.66) * mm});
            skLineSegment(sketch, "E2909", {"start": v(-30.4, 19.66) * mm, "end": v(-30.56, 19.69) * mm});
            skLineSegment(sketch, "E2910", {"start": v(-30.56, 19.69) * mm, "end": v(-30.73, 19.7) * mm});
            skLineSegment(sketch, "E2911", {"start": v(-30.73, 19.7) * mm, "end": v(-30.9, 19.73) * mm});
            skLineSegment(sketch, "E2912", {"start": v(-30.9, 19.73) * mm, "end": v(-31.08, 19.74) * mm});
            skLineSegment(sketch, "E2913", {"start": v(-31.08, 19.74) * mm, "end": v(-31.27, 19.76) * mm});
            skLineSegment(sketch, "E2914", {"start": v(-31.27, 19.76) * mm, "end": v(-31.42, 19.76) * mm});
            skLineSegment(sketch, "E2915", {"start": v(-31.42, 19.76) * mm, "end": v(-32.2, 18.46) * mm});
            skLineSegment(sketch, "E2916", {"start": v(-32.2, 18.46) * mm, "end": v(-32.13, 18.32) * mm});
            skLineSegment(sketch, "E2917", {"start": v(-32.13, 18.32) * mm, "end": v(-32.03, 18.17) * mm});
            skLineSegment(sketch, "E2918", {"start": v(-32.03, 18.17) * mm, "end": v(-31.93, 18.02) * mm});
            skLineSegment(sketch, "E2919", {"start": v(-31.93, 18.02) * mm, "end": v(-31.83, 17.87) * mm});
            skLineSegment(sketch, "E2920", {"start": v(-31.83, 17.87) * mm, "end": v(-31.73, 17.73) * mm});
            skLineSegment(sketch, "E2921", {"start": v(-31.73, 17.73) * mm, "end": v(-31.63, 17.6) * mm});
            skLineSegment(sketch, "E2922", {"start": v(-31.63, 17.6) * mm, "end": v(-31.54, 17.46) * mm});
            skLineSegment(sketch, "E2923", {"start": v(-31.54, 17.46) * mm, "end": v(-31.44, 17.33) * mm});
            skLineSegment(sketch, "E2924", {"start": v(-31.44, 17.33) * mm, "end": v(-31.34, 17.2) * mm});
            skLineSegment(sketch, "E2925", {"start": v(-31.34, 17.2) * mm, "end": v(-31.25, 17.09) * mm});
            skLineSegment(sketch, "E2926", {"start": v(-31.25, 17.09) * mm, "end": v(-31.16, 16.97) * mm});
            skLineSegment(sketch, "E2927", {"start": v(-31.16, 16.97) * mm, "end": v(-31.07, 16.86) * mm});
            skLineSegment(sketch, "E2928", {"start": v(-31.07, 16.86) * mm, "end": v(-30.97, 16.75) * mm});
            skLineSegment(sketch, "E2929", {"start": v(-30.97, 16.75) * mm, "end": v(-30.89, 16.65) * mm});
            skLineSegment(sketch, "E2930", {"start": v(-30.89, 16.65) * mm, "end": v(-30.8, 16.55) * mm});
            skLineSegment(sketch, "E2931", {"start": v(-30.8, 16.55) * mm, "end": v(-30.71, 16.45) * mm});
            skLineSegment(sketch, "E2932", {"start": v(-30.71, 16.45) * mm, "end": v(-30.63, 16.36) * mm});
            skLineSegment(sketch, "E2933", {"start": v(-30.63, 16.36) * mm, "end": v(-30.54, 16.27) * mm});
            skLineSegment(sketch, "E2934", {"start": v(-30.54, 16.27) * mm, "end": v(-30.46, 16.19) * mm});
            skLineSegment(sketch, "E2935", {"start": v(-30.46, 16.19) * mm, "end": v(-30.38, 16.1) * mm});
            skLineSegment(sketch, "E2936", {"start": v(-30.38, 16.1) * mm, "end": v(-30.3, 16.03) * mm});
            skLineSegment(sketch, "E2937", {"start": v(-30.3, 16.03) * mm, "end": v(-30.23, 15.95) * mm});
            skLineSegment(sketch, "E2938", {"start": v(-30.23, 15.95) * mm, "end": v(-30.15, 15.88) * mm});
            skLineSegment(sketch, "E2939", {"start": v(-30.15, 15.88) * mm, "end": v(-30.08, 15.82) * mm});
            skLineSegment(sketch, "E2940", {"start": v(-30.08, 15.82) * mm, "end": v(-30.01, 15.75) * mm});
            skLineSegment(sketch, "E2941", {"start": v(-30.01, 15.75) * mm, "end": v(-29.95, 15.7) * mm});
            skLineSegment(sketch, "E2942", {"start": v(-29.95, 15.7) * mm, "end": v(-29.88, 15.64) * mm});
            skLineSegment(sketch, "E2943", {"start": v(-29.88, 15.64) * mm, "end": v(-29.82, 15.58) * mm});
            skLineSegment(sketch, "E2944", {"start": v(-29.82, 15.58) * mm, "end": v(-29.76, 15.53) * mm});
            skLineSegment(sketch, "E2945", {"start": v(-29.76, 15.53) * mm, "end": v(-29.7, 15.49) * mm});
            skLineSegment(sketch, "E2946", {"start": v(-29.7, 15.49) * mm, "end": v(-29.65, 15.44) * mm});
            skLineSegment(sketch, "E2947", {"start": v(-29.65, 15.44) * mm, "end": v(-29.6, 15.4) * mm});
            skLineSegment(sketch, "E2948", {"start": v(-29.6, 15.4) * mm, "end": v(-29.54, 15.36) * mm});
            skLineSegment(sketch, "E2949", {"start": v(-29.54, 15.36) * mm, "end": v(-29.5, 15.33) * mm});
            skLineSegment(sketch, "E2950", {"start": v(-29.5, 15.33) * mm, "end": v(-29.45, 15.3) * mm});
            skLineSegment(sketch, "E2951", {"start": v(-29.45, 15.3) * mm, "end": v(-29.4, 15.26) * mm});
            skLineSegment(sketch, "E2952", {"start": v(-29.4, 15.26) * mm, "end": v(-29.37, 15.24) * mm});
            skLineSegment(sketch, "E2953", {"start": v(-29.37, 15.24) * mm, "end": v(-29.34, 15.21) * mm});
            skLineSegment(sketch, "E2954", {"start": v(-29.34, 15.21) * mm, "end": v(-29.3, 15.2) * mm});
            skLineSegment(sketch, "E2955", {"start": v(-29.3, 15.2) * mm, "end": v(-29.27, 15.17) * mm});
            skLineSegment(sketch, "E2956", {"start": v(-29.27, 15.17) * mm, "end": v(-29.25, 15.15) * mm});
            skLineSegment(sketch, "E2957", {"start": v(-29.25, 15.15) * mm, "end": v(-29.22, 15.14) * mm});
            skLineSegment(sketch, "E2958", {"start": v(-29.22, 15.14) * mm, "end": v(-29.2, 15.13) * mm});
            skLineSegment(sketch, "E2959", {"start": v(-29.2, 15.13) * mm, "end": v(-29.19, 15.12) * mm});
            skLineSegment(sketch, "E2960", {"start": v(-29.19, 15.12) * mm, "end": v(-29.17, 15.1) * mm});
            skLineSegment(sketch, "E2961", {"start": v(-29.17, 15.1) * mm, "end": v(-29.16, 15.1) * mm});
            skLineSegment(sketch, "E2962", {"start": v(-29.16, 15.1) * mm, "end": v(-29.15, 15.1) * mm});
            skLineSegment(sketch, "E2963", {"start": v(-29.15, 15.1) * mm, "end": v(-28.8, 14.91) * mm});
            skLineSegment(sketch, "E2964", {"start": v(-28.8, 14.91) * mm, "end": v(-29.77, 12.85) * mm});
            skLineSegment(sketch, "E2965", {"start": v(-29.77, 12.85) * mm, "end": v(-30.14, 13.01) * mm});
            skLineSegment(sketch, "E2966", {"start": v(-30.14, 13.01) * mm, "end": v(-30.15, 13.02) * mm});
            skLineSegment(sketch, "E2967", {"start": v(-30.15, 13.02) * mm, "end": v(-30.16, 13.02) * mm});
            skLineSegment(sketch, "E2968", {"start": v(-30.16, 13.02) * mm, "end": v(-30.18, 13.03) * mm});
            skLineSegment(sketch, "E2969", {"start": v(-30.18, 13.03) * mm, "end": v(-30.2, 13.03) * mm});
            skLineSegment(sketch, "E2970", {"start": v(-30.2, 13.03) * mm, "end": v(-30.22, 13.04) * mm});
            skLineSegment(sketch, "E2971", {"start": v(-30.22, 13.04) * mm, "end": v(-30.24, 13.05) * mm});
            skLineSegment(sketch, "E2972", {"start": v(-30.24, 13.05) * mm, "end": v(-30.27, 13.06) * mm});
            skLineSegment(sketch, "E2973", {"start": v(-30.27, 13.06) * mm, "end": v(-30.3, 13.07) * mm});
            skLineSegment(sketch, "E2974", {"start": v(-30.3, 13.07) * mm, "end": v(-30.34, 13.08) * mm});
            skLineSegment(sketch, "E2975", {"start": v(-30.34, 13.08) * mm, "end": v(-30.39, 13.1) * mm});
            skLineSegment(sketch, "E2976", {"start": v(-30.39, 13.1) * mm, "end": v(-30.43, 13.1) * mm});
            skLineSegment(sketch, "E2977", {"start": v(-30.43, 13.1) * mm, "end": v(-30.48, 13.12) * mm});
            skLineSegment(sketch, "E2978", {"start": v(-30.48, 13.12) * mm, "end": v(-30.53, 13.14) * mm});
            skLineSegment(sketch, "E2979", {"start": v(-30.53, 13.14) * mm, "end": v(-30.6, 13.15) * mm});
            skLineSegment(sketch, "E2980", {"start": v(-30.6, 13.15) * mm, "end": v(-30.65, 13.17) * mm});
            skLineSegment(sketch, "E2981", {"start": v(-30.65, 13.17) * mm, "end": v(-30.72, 13.18) * mm});
            skLineSegment(sketch, "E2982", {"start": v(-30.72, 13.18) * mm, "end": v(-30.79, 13.2) * mm});
            skLineSegment(sketch, "E2983", {"start": v(-30.79, 13.2) * mm, "end": v(-30.86, 13.2) * mm});
            skLineSegment(sketch, "E2984", {"start": v(-30.86, 13.2) * mm, "end": v(-30.94, 13.22) * mm});
            skLineSegment(sketch, "E2985", {"start": v(-30.94, 13.22) * mm, "end": v(-31.02, 13.24) * mm});
            skLineSegment(sketch, "E2986", {"start": v(-31.02, 13.24) * mm, "end": v(-31.1, 13.25) * mm});
            skLineSegment(sketch, "E2987", {"start": v(-31.1, 13.25) * mm, "end": v(-31.2, 13.27) * mm});
            skLineSegment(sketch, "E2988", {"start": v(-31.2, 13.27) * mm, "end": v(-31.29, 13.28) * mm});
            skLineSegment(sketch, "E2989", {"start": v(-31.29, 13.28) * mm, "end": v(-31.38, 13.3) * mm});
            skLineSegment(sketch, "E2990", {"start": v(-31.38, 13.3) * mm, "end": v(-31.48, 13.3) * mm});
            skLineSegment(sketch, "E2991", {"start": v(-31.48, 13.3) * mm, "end": v(-31.59, 13.32) * mm});
            skLineSegment(sketch, "E2992", {"start": v(-31.59, 13.32) * mm, "end": v(-31.7, 13.33) * mm});
            skLineSegment(sketch, "E2993", {"start": v(-31.7, 13.33) * mm, "end": v(-31.81, 13.34) * mm});
            skLineSegment(sketch, "E2994", {"start": v(-31.81, 13.34) * mm, "end": v(-31.93, 13.35) * mm});
            skLineSegment(sketch, "E2995", {"start": v(-31.93, 13.35) * mm, "end": v(-32.05, 13.36) * mm});
            skLineSegment(sketch, "E2996", {"start": v(-32.05, 13.36) * mm, "end": v(-32.18, 13.36) * mm});
            skLineSegment(sketch, "E2997", {"start": v(-32.18, 13.36) * mm, "end": v(-32.3, 13.37) * mm});
            skLineSegment(sketch, "E2998", {"start": v(-32.3, 13.37) * mm, "end": v(-32.44, 13.37) * mm});
            skLineSegment(sketch, "E2999", {"start": v(-32.44, 13.37) * mm, "end": v(-32.57, 13.38) * mm});
            skLineSegment(sketch, "E3000", {"start": v(-32.57, 13.38) * mm, "end": v(-32.72, 13.38) * mm});
            skLineSegment(sketch, "E3001", {"start": v(-32.72, 13.38) * mm, "end": v(-32.86, 13.38) * mm});
            skLineSegment(sketch, "E3002", {"start": v(-32.86, 13.38) * mm, "end": v(-33, 13.38) * mm});
            skLineSegment(sketch, "E3003", {"start": v(-33, 13.38) * mm, "end": v(-33.16, 13.38) * mm});
            skLineSegment(sketch, "E3004", {"start": v(-33.16, 13.38) * mm, "end": v(-33.32, 13.37) * mm});
            skLineSegment(sketch, "E3005", {"start": v(-33.32, 13.37) * mm, "end": v(-33.48, 13.37) * mm});
            skLineSegment(sketch, "E3006", {"start": v(-33.48, 13.37) * mm, "end": v(-33.64, 13.36) * mm});
            skLineSegment(sketch, "E3007", {"start": v(-33.64, 13.36) * mm, "end": v(-33.81, 13.35) * mm});
            skLineSegment(sketch, "E3008", {"start": v(-33.81, 13.35) * mm, "end": v(-33.98, 13.33) * mm});
            skLineSegment(sketch, "E3009", {"start": v(-33.98, 13.33) * mm, "end": v(-34.16, 13.32) * mm});
            skLineSegment(sketch, "E3010", {"start": v(-34.16, 13.32) * mm, "end": v(-34.34, 13.3) * mm});
            skLineSegment(sketch, "E3011", {"start": v(-34.34, 13.3) * mm, "end": v(-34.52, 13.28) * mm});
            skLineSegment(sketch, "E3012", {"start": v(-34.52, 13.28) * mm, "end": v(-34.67, 13.25) * mm});
            skLineSegment(sketch, "E3013", {"start": v(-34.67, 13.25) * mm, "end": v(-35.18, 11.82) * mm});
            skLineSegment(sketch, "E3014", {"start": v(-35.18, 11.82) * mm, "end": v(-35.09, 11.7) * mm});
            skLineSegment(sketch, "E3015", {"start": v(-35.09, 11.7) * mm, "end": v(-34.96, 11.57) * mm});
            skLineSegment(sketch, "E3016", {"start": v(-34.96, 11.57) * mm, "end": v(-34.83, 11.44) * mm});
            skLineSegment(sketch, "E3017", {"start": v(-34.83, 11.44) * mm, "end": v(-34.7, 11.32) * mm});
            skLineSegment(sketch, "E3018", {"start": v(-34.7, 11.32) * mm, "end": v(-34.58, 11.2) * mm});
            skLineSegment(sketch, "E3019", {"start": v(-34.58, 11.2) * mm, "end": v(-34.46, 11.08) * mm});
            skLineSegment(sketch, "E3020", {"start": v(-34.46, 11.08) * mm, "end": v(-34.34, 10.97) * mm});
            skLineSegment(sketch, "E3021", {"start": v(-34.34, 10.97) * mm, "end": v(-34.22, 10.87) * mm});
            skLineSegment(sketch, "E3022", {"start": v(-34.22, 10.87) * mm, "end": v(-34.1, 10.76) * mm});
            skLineSegment(sketch, "E3023", {"start": v(-34.1, 10.76) * mm, "end": v(-33.98, 10.66) * mm});
            skLineSegment(sketch, "E3024", {"start": v(-33.98, 10.66) * mm, "end": v(-33.87, 10.57) * mm});
            skLineSegment(sketch, "E3025", {"start": v(-33.87, 10.57) * mm, "end": v(-33.76, 10.48) * mm});
            skLineSegment(sketch, "E3026", {"start": v(-33.76, 10.48) * mm, "end": v(-33.65, 10.39) * mm});
            skLineSegment(sketch, "E3027", {"start": v(-33.65, 10.39) * mm, "end": v(-33.54, 10.3) * mm});
            skLineSegment(sketch, "E3028", {"start": v(-33.54, 10.3) * mm, "end": v(-33.43, 10.22) * mm});
            skLineSegment(sketch, "E3029", {"start": v(-33.43, 10.22) * mm, "end": v(-33.33, 10.15) * mm});
            skLineSegment(sketch, "E3030", {"start": v(-33.33, 10.15) * mm, "end": v(-33.23, 10.07) * mm});
            skLineSegment(sketch, "E3031", {"start": v(-33.23, 10.07) * mm, "end": v(-33.13, 10) * mm});
            skLineSegment(sketch, "E3032", {"start": v(-33.13, 10) * mm, "end": v(-33.03, 9.93) * mm});
            skLineSegment(sketch, "E3033", {"start": v(-33.03, 9.93) * mm, "end": v(-32.94, 9.87) * mm});
            skLineSegment(sketch, "E3034", {"start": v(-32.94, 9.87) * mm, "end": v(-32.85, 9.8) * mm});
            skLineSegment(sketch, "E3035", {"start": v(-32.85, 9.8) * mm, "end": v(-32.76, 9.75) * mm});
            skLineSegment(sketch, "E3036", {"start": v(-32.76, 9.75) * mm, "end": v(-32.67, 9.7) * mm});
            skLineSegment(sketch, "E3037", {"start": v(-32.67, 9.7) * mm, "end": v(-32.6, 9.64) * mm});
            skLineSegment(sketch, "E3038", {"start": v(-32.6, 9.64) * mm, "end": v(-32.51, 9.6) * mm});
            skLineSegment(sketch, "E3039", {"start": v(-32.51, 9.6) * mm, "end": v(-32.43, 9.55) * mm});
            skLineSegment(sketch, "E3040", {"start": v(-32.43, 9.55) * mm, "end": v(-32.36, 9.5) * mm});
            skLineSegment(sketch, "E3041", {"start": v(-32.36, 9.5) * mm, "end": v(-32.29, 9.47) * mm});
            skLineSegment(sketch, "E3042", {"start": v(-32.29, 9.47) * mm, "end": v(-32.22, 9.43) * mm});
            skLineSegment(sketch, "E3043", {"start": v(-32.22, 9.43) * mm, "end": v(-32.15, 9.4) * mm});
            skLineSegment(sketch, "E3044", {"start": v(-32.15, 9.4) * mm, "end": v(-32.09, 9.36) * mm});
            skLineSegment(sketch, "E3045", {"start": v(-32.09, 9.36) * mm, "end": v(-32.03, 9.33) * mm});
            skLineSegment(sketch, "E3046", {"start": v(-32.03, 9.33) * mm, "end": v(-31.97, 9.3) * mm});
            skLineSegment(sketch, "E3047", {"start": v(-31.97, 9.3) * mm, "end": v(-31.92, 9.28) * mm});
            skLineSegment(sketch, "E3048", {"start": v(-31.92, 9.28) * mm, "end": v(-31.87, 9.25) * mm});
            skLineSegment(sketch, "E3049", {"start": v(-31.87, 9.25) * mm, "end": v(-31.82, 9.23) * mm});
            skLineSegment(sketch, "E3050", {"start": v(-31.82, 9.23) * mm, "end": v(-31.78, 9.21) * mm});
            skLineSegment(sketch, "E3051", {"start": v(-31.78, 9.21) * mm, "end": v(-31.74, 9.2) * mm});
            skLineSegment(sketch, "E3052", {"start": v(-31.74, 9.2) * mm, "end": v(-31.7, 9.18) * mm});
            skLineSegment(sketch, "E3053", {"start": v(-31.7, 9.18) * mm, "end": v(-31.67, 9.17) * mm});
            skLineSegment(sketch, "E3054", {"start": v(-31.67, 9.17) * mm, "end": v(-31.64, 9.16) * mm});
            skLineSegment(sketch, "E3055", {"start": v(-31.64, 9.16) * mm, "end": v(-31.61, 9.15) * mm});
            skLineSegment(sketch, "E3056", {"start": v(-31.61, 9.15) * mm, "end": v(-31.6, 9.14) * mm});
            skLineSegment(sketch, "E3057", {"start": v(-31.6, 9.14) * mm, "end": v(-31.57, 9.13) * mm});
            skLineSegment(sketch, "E3058", {"start": v(-31.57, 9.13) * mm, "end": v(-31.56, 9.13) * mm});
            skLineSegment(sketch, "E3059", {"start": v(-31.56, 9.13) * mm, "end": v(-31.55, 9.12) * mm});
            skLineSegment(sketch, "E3060", {"start": v(-31.55, 9.12) * mm, "end": v(-31.54, 9.12) * mm});
            skLineSegment(sketch, "E3061", {"start": v(-31.54, 9.12) * mm, "end": v(-31.15, 9) * mm});
            skLineSegment(sketch, "E3062", {"start": v(-31.15, 9) * mm, "end": v(-31.7, 6.8) * mm});
            skLineSegment(sketch, "E3063", {"start": v(-31.7, 6.8) * mm, "end": v(-32.1, 6.88) * mm});
            skLineSegment(sketch, "E3064", {"start": v(-32.1, 6.88) * mm, "end": v(-32.1, 6.89) * mm});
            skLineSegment(sketch, "E3065", {"start": v(-32.1, 6.89) * mm, "end": v(-32.12, 6.89) * mm});
            skLineSegment(sketch, "E3066", {"start": v(-32.12, 6.89) * mm, "end": v(-32.14, 6.9) * mm});
            skLineSegment(sketch, "E3067", {"start": v(-32.14, 6.9) * mm, "end": v(-32.16, 6.9) * mm});
            skLineSegment(sketch, "E3068", {"start": v(-32.16, 6.9) * mm, "end": v(-32.18, 6.9) * mm});
            skLineSegment(sketch, "E3069", {"start": v(-32.18, 6.9) * mm, "end": v(-32.2, 6.9) * mm});
            skLineSegment(sketch, "E3070", {"start": v(-32.2, 6.9) * mm, "end": v(-32.24, 6.9) * mm});
            skLineSegment(sketch, "E3071", {"start": v(-32.24, 6.9) * mm, "end": v(-32.27, 6.9) * mm});
            skLineSegment(sketch, "E3072", {"start": v(-32.27, 6.9) * mm, "end": v(-32.31, 6.91) * mm});
            skLineSegment(sketch, "E3073", {"start": v(-32.31, 6.91) * mm, "end": v(-32.36, 6.92) * mm});
            skLineSegment(sketch, "E3074", {"start": v(-32.36, 6.92) * mm, "end": v(-32.4, 6.92) * mm});
            skLineSegment(sketch, "E3075", {"start": v(-32.4, 6.92) * mm, "end": v(-32.46, 6.92) * mm});
            skLineSegment(sketch, "E3076", {"start": v(-32.46, 6.92) * mm, "end": v(-32.51, 6.93) * mm});
            skLineSegment(sketch, "E3077", {"start": v(-32.51, 6.93) * mm, "end": v(-32.57, 6.93) * mm});
            skLineSegment(sketch, "E3078", {"start": v(-32.57, 6.93) * mm, "end": v(-32.63, 6.93) * mm});
            skLineSegment(sketch, "E3079", {"start": v(-32.63, 6.93) * mm, "end": v(-32.7, 6.93) * mm});
            skLineSegment(sketch, "E3080", {"start": v(-32.7, 6.93) * mm, "end": v(-32.77, 6.93) * mm});
            skLineSegment(sketch, "E3081", {"start": v(-32.77, 6.93) * mm, "end": v(-32.84, 6.93) * mm});
            skLineSegment(sketch, "E3082", {"start": v(-32.84, 6.93) * mm, "end": v(-32.92, 6.93) * mm});
            skLineSegment(sketch, "E3083", {"start": v(-32.92, 6.93) * mm, "end": v(-33, 6.93) * mm});
            skLineSegment(sketch, "E3084", {"start": v(-33, 6.93) * mm, "end": v(-33.1, 6.93) * mm});
            skLineSegment(sketch, "E3085", {"start": v(-33.1, 6.93) * mm, "end": v(-33.18, 6.93) * mm});
            skLineSegment(sketch, "E3086", {"start": v(-33.18, 6.93) * mm, "end": v(-33.28, 6.92) * mm});
            skLineSegment(sketch, "E3087", {"start": v(-33.28, 6.92) * mm, "end": v(-33.37, 6.92) * mm});
            skLineSegment(sketch, "E3088", {"start": v(-33.37, 6.92) * mm, "end": v(-33.48, 6.9) * mm});
            skLineSegment(sketch, "E3089", {"start": v(-33.48, 6.9) * mm, "end": v(-33.58, 6.9) * mm});
            skLineSegment(sketch, "E3090", {"start": v(-33.58, 6.9) * mm, "end": v(-33.7, 6.89) * mm});
            skLineSegment(sketch, "E3091", {"start": v(-33.7, 6.89) * mm, "end": v(-33.8, 6.88) * mm});
            skLineSegment(sketch, "E3092", {"start": v(-33.8, 6.88) * mm, "end": v(-33.92, 6.86) * mm});
            skLineSegment(sketch, "E3093", {"start": v(-33.92, 6.86) * mm, "end": v(-34.04, 6.85) * mm});
            skLineSegment(sketch, "E3094", {"start": v(-34.04, 6.85) * mm, "end": v(-34.16, 6.83) * mm});
            skLineSegment(sketch, "E3095", {"start": v(-34.16, 6.83) * mm, "end": v(-34.3, 6.81) * mm});
            skLineSegment(sketch, "E3096", {"start": v(-34.3, 6.81) * mm, "end": v(-34.42, 6.79) * mm});
            skLineSegment(sketch, "E3097", {"start": v(-34.42, 6.79) * mm, "end": v(-34.56, 6.77) * mm});
            skLineSegment(sketch, "E3098", {"start": v(-34.56, 6.77) * mm, "end": v(-34.7, 6.74) * mm});
            skLineSegment(sketch, "E3099", {"start": v(-34.7, 6.74) * mm, "end": v(-34.84, 6.71) * mm});
            skLineSegment(sketch, "E3100", {"start": v(-34.84, 6.71) * mm, "end": v(-34.99, 6.68) * mm});
            skLineSegment(sketch, "E3101", {"start": v(-34.99, 6.68) * mm, "end": v(-35.13, 6.65) * mm});
            skLineSegment(sketch, "E3102", {"start": v(-35.13, 6.65) * mm, "end": v(-35.29, 6.61) * mm});
            skLineSegment(sketch, "E3103", {"start": v(-35.29, 6.61) * mm, "end": v(-35.44, 6.58) * mm});
            skLineSegment(sketch, "E3104", {"start": v(-35.44, 6.58) * mm, "end": v(-35.6, 6.54) * mm});
            skLineSegment(sketch, "E3105", {"start": v(-35.6, 6.54) * mm, "end": v(-35.77, 6.5) * mm});
            skLineSegment(sketch, "E3106", {"start": v(-35.77, 6.5) * mm, "end": v(-35.93, 6.45) * mm});
            skLineSegment(sketch, "E3107", {"start": v(-35.93, 6.45) * mm, "end": v(-36.1, 6.4) * mm});
            skLineSegment(sketch, "E3108", {"start": v(-36.1, 6.4) * mm, "end": v(-36.27, 6.35) * mm});
            skLineSegment(sketch, "E3109", {"start": v(-36.27, 6.35) * mm, "end": v(-36.45, 6.3) * mm});
            skLineSegment(sketch, "E3110", {"start": v(-36.45, 6.3) * mm, "end": v(-36.6, 6.23) * mm});
            skLineSegment(sketch, "E3111", {"start": v(-36.6, 6.23) * mm, "end": v(-36.81, 4.73) * mm});
            skLineSegment(sketch, "E3112", {"start": v(-36.81, 4.73) * mm, "end": v(-36.7, 4.63) * mm});
            skLineSegment(sketch, "E3113", {"start": v(-36.7, 4.63) * mm, "end": v(-36.55, 4.53) * mm});
            skLineSegment(sketch, "E3114", {"start": v(-36.55, 4.53) * mm, "end": v(-36.4, 4.43) * mm});
            skLineSegment(sketch, "E3115", {"start": v(-36.4, 4.43) * mm, "end": v(-36.25, 4.33) * mm});
            skLineSegment(sketch, "E3116", {"start": v(-36.25, 4.33) * mm, "end": v(-36.1, 4.24) * mm});
            skLineSegment(sketch, "E3117", {"start": v(-36.1, 4.24) * mm, "end": v(-35.96, 4.15) * mm});
            skLineSegment(sketch, "E3118", {"start": v(-35.96, 4.15) * mm, "end": v(-35.82, 4.06) * mm});
            skLineSegment(sketch, "E3119", {"start": v(-35.82, 4.06) * mm, "end": v(-35.68, 3.98) * mm});
            skLineSegment(sketch, "E3120", {"start": v(-35.68, 3.98) * mm, "end": v(-35.54, 3.9) * mm});
            skLineSegment(sketch, "E3121", {"start": v(-35.54, 3.9) * mm, "end": v(-35.41, 3.83) * mm});
            skLineSegment(sketch, "E3122", {"start": v(-35.41, 3.83) * mm, "end": v(-35.28, 3.76) * mm});
            skLineSegment(sketch, "E3123", {"start": v(-35.28, 3.76) * mm, "end": v(-35.15, 3.69) * mm});
            skLineSegment(sketch, "E3124", {"start": v(-35.15, 3.69) * mm, "end": v(-35.03, 3.62) * mm});
            skLineSegment(sketch, "E3125", {"start": v(-35.03, 3.62) * mm, "end": v(-34.9, 3.56) * mm});
            skLineSegment(sketch, "E3126", {"start": v(-34.9, 3.56) * mm, "end": v(-34.79, 3.5) * mm});
            skLineSegment(sketch, "E3127", {"start": v(-34.79, 3.5) * mm, "end": v(-34.67, 3.45) * mm});
            skLineSegment(sketch, "E3128", {"start": v(-34.67, 3.45) * mm, "end": v(-34.56, 3.4) * mm});
            skLineSegment(sketch, "E3129", {"start": v(-34.56, 3.4) * mm, "end": v(-34.45, 3.35) * mm});
            skLineSegment(sketch, "E3130", {"start": v(-34.45, 3.35) * mm, "end": v(-34.34, 3.3) * mm});
            skLineSegment(sketch, "E3131", {"start": v(-34.34, 3.3) * mm, "end": v(-34.23, 3.25) * mm});
            skLineSegment(sketch, "E3132", {"start": v(-34.23, 3.25) * mm, "end": v(-34.13, 3.21) * mm});
            skLineSegment(sketch, "E3133", {"start": v(-34.13, 3.21) * mm, "end": v(-34.03, 3.17) * mm});
            skLineSegment(sketch, "E3134", {"start": v(-34.03, 3.17) * mm, "end": v(-33.94, 3.14) * mm});
            skLineSegment(sketch, "E3135", {"start": v(-33.94, 3.14) * mm, "end": v(-33.85, 3.1) * mm});
            skLineSegment(sketch, "E3136", {"start": v(-33.85, 3.1) * mm, "end": v(-33.76, 3.07) * mm});
            skLineSegment(sketch, "E3137", {"start": v(-33.76, 3.07) * mm, "end": v(-33.67, 3.04) * mm});
            skLineSegment(sketch, "E3138", {"start": v(-33.67, 3.04) * mm, "end": v(-33.6, 3.01) * mm});
            skLineSegment(sketch, "E3139", {"start": v(-33.6, 3.01) * mm, "end": v(-33.51, 2.99) * mm});
            skLineSegment(sketch, "E3140", {"start": v(-33.51, 2.99) * mm, "end": v(-33.44, 2.96) * mm});
            skLineSegment(sketch, "E3141", {"start": v(-33.44, 2.96) * mm, "end": v(-33.37, 2.94) * mm});
            skLineSegment(sketch, "E3142", {"start": v(-33.37, 2.94) * mm, "end": v(-33.3, 2.92) * mm});
            skLineSegment(sketch, "E3143", {"start": v(-33.3, 2.92) * mm, "end": v(-33.23, 2.9) * mm});
            skLineSegment(sketch, "E3144", {"start": v(-33.23, 2.9) * mm, "end": v(-33.17, 2.89) * mm});
            skLineSegment(sketch, "E3145", {"start": v(-33.17, 2.89) * mm, "end": v(-33.12, 2.87) * mm});
            skLineSegment(sketch, "E3146", {"start": v(-33.12, 2.87) * mm, "end": v(-33.06, 2.86) * mm});
            skLineSegment(sketch, "E3147", {"start": v(-33.06, 2.86) * mm, "end": v(-33.01, 2.85) * mm});
            skLineSegment(sketch, "E3148", {"start": v(-33.01, 2.85) * mm, "end": v(-32.97, 2.84) * mm});
            skLineSegment(sketch, "E3149", {"start": v(-32.97, 2.84) * mm, "end": v(-32.92, 2.83) * mm});
            skLineSegment(sketch, "E3150", {"start": v(-32.92, 2.83) * mm, "end": v(-32.89, 2.82) * mm});
            skLineSegment(sketch, "E3151", {"start": v(-32.89, 2.82) * mm, "end": v(-32.85, 2.81) * mm});
            skLineSegment(sketch, "E3152", {"start": v(-32.85, 2.81) * mm, "end": v(-32.82, 2.8) * mm});
            skLineSegment(sketch, "E3153", {"start": v(-32.82, 2.8) * mm, "end": v(-32.8, 2.8) * mm});
            skLineSegment(sketch, "E3154", {"start": v(-32.8, 2.8) * mm, "end": v(-32.77, 2.8) * mm});
            skLineSegment(sketch, "E3155", {"start": v(-32.77, 2.8) * mm, "end": v(-32.75, 2.8) * mm});
            skLineSegment(sketch, "E3156", {"start": v(-32.75, 2.8) * mm, "end": v(-32.73, 2.8) * mm});
            skLineSegment(sketch, "E3157", {"start": v(-32.73, 2.8) * mm, "end": v(-32.72, 2.8) * mm});
            skLineSegment(sketch, "E3158", {"start": v(-32.72, 2.8) * mm, "end": v(-32.71, 2.8) * mm});
            skLineSegment(sketch, "E3159", {"start": v(-32.71, 2.8) * mm, "end": v(-32.3, 2.76) * mm});
            skLineSegment(sketch, "E3160", {"start": v(-32.3, 2.76) * mm, "end": v(-32.42, 0.48) * mm});
            skCircle(sketch, "E3161", {"center": v(0, 0) * mm, "radius": 34.93 * mm, "construction": true});
            skArc(sketch, "E3162", {"start": v(-1.9, 5.7) * mm, "mid": v(-3.44, 4.94) * mm, "end": v(-4.69, 3.77) * mm});
            skArc(sketch, "E3163", {"start": v(4.84, 3.58) * mm, "mid": v(3.64, 4.8) * mm, "end": v(2.14, 5.63) * mm});
            skArc(sketch, "E3164", {"start": v(4.9, -3.5) * mm, "mid": v(5.68, -1.98) * mm, "end": v(6.01, -0.3) * mm});
            skArc(sketch, "E3165", {"start": v(-1.81, -5.74) * mm, "mid": v(-0.12, -6.02) * mm, "end": v(1.58, -5.8) * mm});
            skArc(sketch, "E3166", {"start": v(-6.02, -0.05) * mm, "mid": v(-5.76, -1.74) * mm, "end": v(-5.04, -3.3) * mm});
            skCircle(sketch, "E3167", {"center": v(0, 0) * mm, "radius": 4 * mm});
            skSolve(sketch);
        }
        {
            var Q0;
            Q0 = qSketchRegion(id + "F0", true);
            extrude(context, id + "F1", {"entities" : qUnion([Q0]), "depth" : 8 * mm, "offsetDistance" : 25 * mm});
        }
    });
